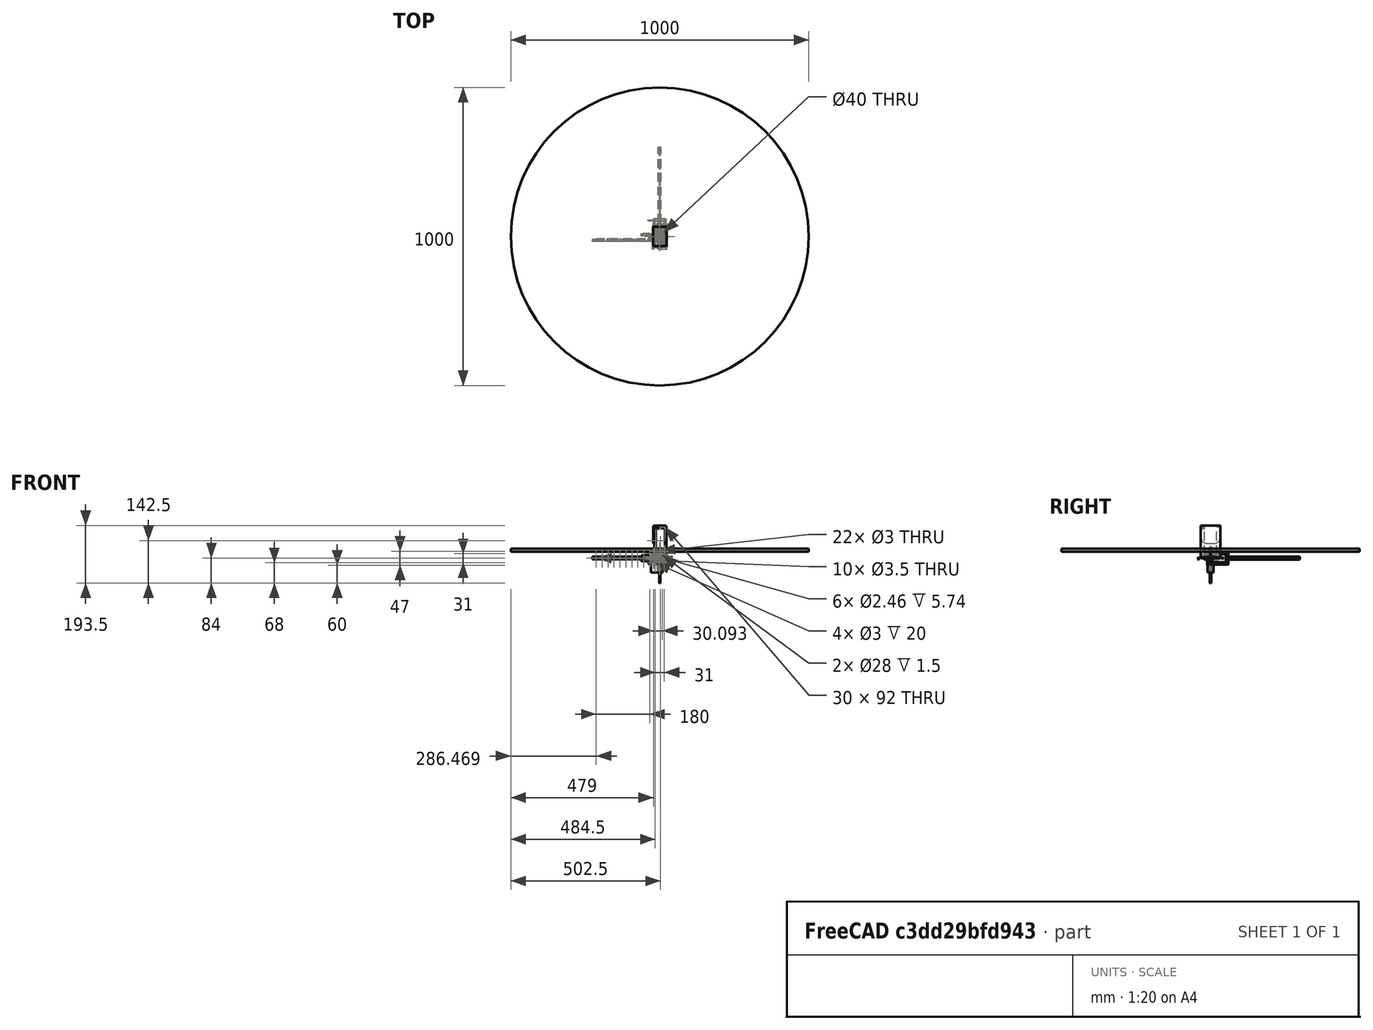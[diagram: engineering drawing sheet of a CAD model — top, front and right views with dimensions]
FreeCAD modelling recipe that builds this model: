
FCSTD DOCUMENT  (FreeCAD 2024.113R14555 (Git shallow))
Label: generic-hardware
License: All rights reserved
LicenseURL: http://en.wikipedia.org/wiki/All_rights_reserved
objects: Sketcher::SketchObject×123, PartDesign::Body×59, PartDesign::Pad×51, PartDesign::Pocket×41, PartDesign::Revolution×27, App::Part×24, PartDesign::Chamfer×22, App::Link×21, PartDesign::Fillet×21, PartDesign::PolarPattern×19, App::DocumentObjectGroup×13, Part::FeaturePython×13, Part::Feature×10, TechDraw::DrawViewDimension×9, PartDesign::FeatureBase×6, PartDesign::Groove×5, PartDesign::CoordinateSystem×4, TechDraw::DrawProjGroupItem×4, PartDesign::Line×3, Part::Mirroring×3, +13 more types
note: 943 computed .brp shape members not serialized (recipe doc carries the construction recipe); baked Part::Feature solids carry a one-line shape summary decoded from their .brp

FEATURE [Sketcher::SketchObject] Sketch
  ArcFitTolerance = 0
  ExternalBSplineMaxDegree = 0
  ExternalBSplineTolerance = 0
  FixShape = 1
  FullyConstrained = true
  InternalTolerance = 1e-06
  InvalidShape = false
  MakeInternals = false
  MapMode = 5
  Placement = pos=(0,0,0) rot=(1,0,0;1.5708rad)
  TreeRank = 0
  ValidateShape = false
  sketch-geometry (5):
    g0: LineSegment StartX=-21.15 StartY=-21.15 StartZ=0 EndX=21.15 EndY=-21.15 EndZ=0
    g1: LineSegment StartX=21.15 StartY=-21.15 StartZ=0 EndX=21.15 EndY=21.15 EndZ=0
    g2: LineSegment StartX=21.15 StartY=21.15 StartZ=0 EndX=-21.15 EndY=21.15 EndZ=0
    g3: LineSegment StartX=-21.15 StartY=21.15 StartZ=0 EndX=-21.15 EndY=-21.15 EndZ=0
    g4: GeomPoint [constr] X=0 Y=1e-16 Z=0
  constraints (12):
    c: Coincident(g0,g1)
    c: Coincident(g1,g2)
    c: Coincident(g2,g3)
    c: Coincident(g3,g0)
    c: Horizontal(g0)
    c: Horizontal(g2)
    c: Vertical(g1)
    c: Vertical(g3)
    c: Symmetric(g2,g0,g4)
    c: Coincident(g4,g-1)
    c: Equal(g2,g1)
    c: DistanceX(g2,g2) = 42.3
FEATURE [PartDesign::Pad] Pad
  AddSubType = 0
  AutoTaperInnerAngle = true
  CheckUpToFaceLimits = true
  ClaimChildren = false
  Direction = (0,-1,0)
  Fit = 0
  FitJoin = 0
  FixShape = 1
  InnerFit = 0
  InnerFitJoin = 0
  InvalidShape = false
  Length = 60
  Length2 = 10
  NewSolid = false
  Placement = pos=(0,0,0) rot=(1,0,0;1.5708rad)
  Profile = -> Sketch
  ReferenceAxis = -> Sketch [N_Axis]
  Refine = true
  Reversed = true
  Suppress = false
  TaperInnerAngle = 0
  TaperInnerAngleRev = 0
  TreeRank = 0
  Type = 0
  ValidateShape = true
  _ProfileBasedVersion = 0
FEATURE [Sketcher::SketchObject] Sketch001
  ArcFitTolerance = 0
  AttachmentSupport = -> [Pad]
  ExternalBSplineMaxDegree = 0
  ExternalBSplineTolerance = 0
  FixShape = 1
  FullyConstrained = true
  InternalTolerance = 1e-06
  InvalidShape = false
  MakeInternals = false
  MapMode = 5
  Placement = pos=(0,0,0) rot=(1,0,0;1.5708rad)
  Support = -> [Pad]
  TreeRank = 0
  ValidateShape = false
  sketch-geometry (1):
    g0: Circle CenterX=0 CenterY=0 CenterZ=0 NormalX=0 NormalY=0 NormalZ=1 AngleXU=0 Radius=11
  constraints (2):
    c: Coincident(g0,g-1)
    c: Diameter(g0) = 22
FEATURE [PartDesign::Pad] Pad001
  AddSubType = 0
  AutoTaperInnerAngle = true
  BaseFeature = -> Pad
  CheckUpToFaceLimits = true
  ClaimChildren = false
  Direction = (0,-1,-2e-16)
  Fit = 0
  FitJoin = 0
  FixShape = 1
  InnerFit = 0
  InnerFitJoin = 0
  InvalidShape = false
  Length = 2
  Length2 = 10
  NewSolid = false
  Placement = pos=(0,0,0) rot=(1,0,0;1.5708rad)
  Profile = -> Sketch001
  ReferenceAxis = -> Sketch001 [N_Axis]
  Refine = true
  Suppress = false
  TaperInnerAngle = 0
  TaperInnerAngleRev = 0
  TreeRank = 0
  Type = 0
  ValidateShape = true
  _ProfileBasedVersion = 0
FEATURE [Sketcher::SketchObject] Sketch002
  ArcFitTolerance = 0
  AttachmentSupport = -> [Pad001]
  ExternalBSplineMaxDegree = 0
  ExternalBSplineTolerance = 0
  FixShape = 1
  FullyConstrained = true
  InternalTolerance = 1e-06
  InvalidShape = false
  MakeInternals = false
  MapMode = 5
  Placement = pos=(0,0,0) rot=(1,0,0;1.5708rad)
  Support = -> [Pad001]
  TreeRank = 0
  ValidateShape = false
  sketch-geometry (1):
    g0: Circle CenterX=0 CenterY=0 CenterZ=0 NormalX=0 NormalY=0 NormalZ=1 AngleXU=0 Radius=2.5
  constraints (2):
    c: Coincident(g0,g-1)
    c: Diameter(g0) = 5
FEATURE [PartDesign::Pad] Pad002
  AddSubType = 0
  AutoTaperInnerAngle = true
  BaseFeature = -> Pad001
  CheckUpToFaceLimits = true
  ClaimChildren = false
  Direction = (0,-1,-7e-16)
  Fit = 0
  FitJoin = 0
  FixShape = 1
  InnerFit = 0
  InnerFitJoin = 0
  InvalidShape = false
  Length = 24
  Length2 = 10
  NewSolid = false
  Placement = pos=(0,0,0) rot=(1,0,0;1.5708rad)
  Profile = -> Sketch002
  ReferenceAxis = -> Sketch002 [N_Axis]
  Refine = true
  Suppress = false
  TaperInnerAngle = 0
  TaperInnerAngleRev = 0
  TreeRank = 0
  Type = 0
  ValidateShape = true
  _ProfileBasedVersion = 0
FEATURE [Sketcher::SketchObject] Sketch003
  ArcFitTolerance = 0
  ExternalBSplineMaxDegree = 0
  ExternalBSplineTolerance = 0
  ExternalGeometry = -> [Pad002]
  FixShape = 1
  FullyConstrained = true
  InternalTolerance = 1e-06
  InvalidShape = false
  MakeInternals = false
  MapMode = 5
  Placement = pos=(0,0,0) rot=(0.57735,0.57735,0.57735;2.0944rad)
  TreeRank = 0
  ValidateShape = false
  sketch-geometry (4):
    g0: LineSegment StartX=-24 StartY=2.5 StartZ=0 EndX=-24 EndY=2 EndZ=0
    g1: LineSegment StartX=-24 StartY=2 StartZ=0 EndX=-9 EndY=2 EndZ=0
    g2: LineSegment StartX=-9 StartY=2 StartZ=0 EndX=-9 EndY=2.5 EndZ=0
    g3: LineSegment StartX=-9 StartY=2.5 StartZ=0 EndX=-24 EndY=2.5 EndZ=0
  constraints (11):
    c: Coincident(g0,g1)
    c: Coincident(g1,g2)
    c: Coincident(g2,g3)
    c: Coincident(g3,g0)
    c: Vertical(g0)
    c: Vertical(g2)
    c: Horizontal(g1)
    c: Horizontal(g3)
    c: Coincident(g0,g-3)
    c: Distance(g0,g-3) = 4.5
    c: DistanceX(g1,g1) = 15
FEATURE [PartDesign::Pocket] Pocket
  AddSubType = 1
  AutoTaperInnerAngle = true
  BaseFeature = -> Pad002
  CheckUpToFaceLimits = true
  ClaimChildren = false
  Direction = (-1,-1e-16,1e-16)
  Fit = 0
  FitJoin = 0
  FixShape = 1
  InnerFit = 0
  InnerFitJoin = 0
  InvalidShape = false
  Length = 5
  Length2 = 5
  Midplane = true
  NewSolid = false
  Placement = pos=(0,0,0) rot=(1,0,0;1.5708rad)
  Profile = -> Sketch003
  ReferenceAxis = -> Sketch003 [N_Axis]
  Refine = true
  Suppress = false
  TaperInnerAngle = 0
  TaperInnerAngleRev = 0
  TreeRank = 0
  Type = 1
  ValidateShape = true
  _ProfileBasedVersion = 0
  _Version = 0
FEATURE [Sketcher::SketchObject] Sketch004
  ArcFitTolerance = 0
  ExternalBSplineMaxDegree = 0
  ExternalBSplineTolerance = 0
  FixShape = 1
  FullyConstrained = true
  InternalTolerance = 1e-06
  InvalidShape = false
  MakeInternals = false
  MapMode = 5
  Placement = pos=(0,0,0) rot=(1,0,0;1.5708rad)
  TreeRank = 0
  ValidateShape = false
  sketch-geometry (9):
    g0: LineSegment [constr] StartX=-15.5 StartY=-15.5 StartZ=0 EndX=15.5 EndY=-15.5 EndZ=0
    g1: LineSegment [constr] StartX=15.5 StartY=-15.5 StartZ=0 EndX=15.5 EndY=15.5 EndZ=0
    g2: LineSegment [constr] StartX=15.5 StartY=15.5 StartZ=0 EndX=-15.5 EndY=15.5 EndZ=0
    g3: LineSegment [constr] StartX=-15.5 StartY=15.5 StartZ=0 EndX=-15.5 EndY=-15.5 EndZ=0
    g4: GeomPoint [constr] X=0 Y=0 Z=0
    g5: Circle CenterX=-15.5 CenterY=15.5 CenterZ=0 NormalX=0 NormalY=0 NormalZ=1 AngleXU=0 Radius=1.5
    g6: Circle CenterX=15.5 CenterY=15.5 CenterZ=0 NormalX=0 NormalY=0 NormalZ=1 AngleXU=0 Radius=1.5
    g7: Circle CenterX=15.5 CenterY=-15.5 CenterZ=0 NormalX=0 NormalY=0 NormalZ=1 AngleXU=0 Radius=1.5
    g8: Circle CenterX=-15.5 CenterY=-15.5 CenterZ=0 NormalX=0 NormalY=0 NormalZ=1 AngleXU=0 Radius=1.5
  constraints (20):
    c: Coincident(g0,g1)
    c: Coincident(g1,g2)
    c: Coincident(g2,g3)
    c: Coincident(g3,g0)
    c: Horizontal(g0)
    c: Horizontal(g2)
    c: Vertical(g1)
    c: Vertical(g3)
    c: Symmetric(g2,g0,g4)
    c: Coincident(g4,g-1)
    c: Equal(g1,g2)
    c: DistanceX(g2,g2) = 31
    c: Coincident(g5,g2)
    c: Coincident(g6,g1)
    c: Coincident(g7,g0)
    c: Coincident(g8,g0)
    c: Equal(g8,g5)
    c: Equal(g5,g6)
    c: Equal(g6,g7)
    c: Diameter(g6) = 3
FEATURE [PartDesign::Pocket] Pocket001
  AddSubType = 1
  AutoTaperInnerAngle = true
  BaseFeature = -> Pocket
  CheckUpToFaceLimits = true
  ClaimChildren = false
  Direction = (0,1,0)
  Fit = 0
  FitJoin = 0
  FixShape = 1
  InnerFit = 0
  InnerFitJoin = 0
  InvalidShape = false
  Length = 20
  Length2 = 5
  NewSolid = false
  Placement = pos=(0,0,0) rot=(1,0,0;1.5708rad)
  Profile = -> Sketch004
  ReferenceAxis = -> Sketch004 [N_Axis]
  Refine = true
  Suppress = false
  TaperInnerAngle = 0
  TaperInnerAngleRev = 0
  TreeRank = 0
  Type = 0
  ValidateShape = true
  _ProfileBasedVersion = 0
  _Version = 0
FEATURE [PartDesign::Chamfer] Chamfer
  AddSubType = 0
  Angle = 45
  Base = -> Pocket001 [Edge35]
  BaseFeature = -> Pocket001
  ChamferType = 0
  FixShape = 1
  FlipDirection = false
  InvalidShape = false
  NewSolid = false
  Placement = pos=(0,0,0) rot=(1,0,0;1.5708rad)
  Refine = true
  Size = 0.2
  Size2 = 1
  SupportTransform = false
  Suppress = false
  TreeRank = 0
  UseAllEdges = false
  ValidateShape = true
FEATURE [PartDesign::Chamfer] Chamfer001
  AddSubType = 0
  Angle = 45
  Base = -> Chamfer [Edge32,Edge28,Edge30,Edge27]
  BaseFeature = -> Chamfer
  ChamferType = 0
  FixShape = 1
  FlipDirection = false
  InvalidShape = false
  NewSolid = false
  Placement = pos=(0,0,0) rot=(1,0,0;1.5708rad)
  Refine = true
  Size = 5
  Size2 = 1
  SupportTransform = false
  Suppress = false
  TreeRank = 0
  UseAllEdges = false
  ValidateShape = true
FEATURE [PartDesign::Body] Body  label="Simple-17HS24-2104S"
  AutoGroupSolids = false
  ClaimAllChildren = false
  ExportMode = 0
  FixShape = 1
  Group = -> [Sketch,Pad,Sketch001,Pad001,Sketch002,Pad002,Sketch003,Pocket,Sketch004,Pocket001,Chamfer,Chamfer001]
  InvalidShape = false
  Origin = -> Origin
  SingleSolid = true
  Tip = -> Chamfer001
  TreeRank = 0
  ValidateShape = false
  _ExportChildren = -> [Pad,Pad001,Pad002,Pocket,Pocket001,Chamfer,Chamfer001]
  _GroupVersion = 1
FEATURE [PartDesign::Line] DatumLine001
  AttacherType = Attacher::AttachEngineLine
  AttachmentOffset = pos=(0,23.5,0) rot=(0,0,1;0rad)
  FixShape = 1
  InvalidShape = false
  Length = 80
  MapMode = 16
  MinimumLength = 10
  Placement = pos=(0,0,23.5) rot=(0.57735,0.57735,0.57735;2.0944rad)
  ResizeMode = 1
  TreeRank = 0
  ValidateShape = false
FEATURE [PartDesign::Line] DatumLine002
  AttacherType = Attacher::AttachEngineLine
  FixShape = 1
  InvalidShape = false
  Length = 10
  MapMode = 29
  MinimumLength = 10
  Placement = pos=(0,0,-24) rot=(0,0.707107,0.707107;3.14159rad)
  ResizeMode = 0
  TreeRank = 0
  ValidateShape = false
FEATURE [App::Link] Link084  label="Roller001"
  AutoLinkLabel = false
  AutoPlacement = true
  LinkPlacement = pos=(0,0,0) rot=(0,-1,0;1.25664rad)
  LinkedObject = -> Body050
  Placement = pos=(0,0,0) rot=(0,-1,0;1.25664rad)
  SyncGroupVisibility = false
  TreeRank = 0
  _LinkVersion = 1
FEATURE [App::Link] Link085  label="Roller002"
  AutoLinkLabel = false
  AutoPlacement = true
  LinkPlacement = pos=(0,0,0) rot=(0,1,0;3.76991rad)
  LinkedObject = -> Link084
  Placement = pos=(0,0,0) rot=(0,1,0;3.76991rad)
  SyncGroupVisibility = false
  TreeRank = 0
  _LinkVersion = 1
FEATURE [App::Link] Link086  label="Roller003"
  AutoLinkLabel = false
  AutoPlacement = true
  LinkPlacement = pos=(0,0,0) rot=(0,1,0;2.51327rad)
  LinkedObject = -> Link085
  Placement = pos=(0,0,0) rot=(0,1,0;2.51327rad)
  SyncGroupVisibility = false
  TreeRank = 0
  _LinkVersion = 1
FEATURE [App::Link] Link087  label="Roller004"
  AutoLinkLabel = false
  AutoPlacement = true
  LinkPlacement = pos=(0,0,0) rot=(0,1,0;1.25664rad)
  LinkedObject = -> Link086
  Placement = pos=(0,0,0) rot=(0,1,0;1.25664rad)
  SyncGroupVisibility = false
  TreeRank = 0
  _LinkVersion = 1
FEATURE [App::Link] Link088  label="Rivet001"
  AutoLinkLabel = false
  AutoPlacement = true
  LinkPlacement = pos=(0,0,0) rot=(0,-1,0;1.25664rad)
  LinkedObject = -> Body051
  Placement = pos=(0,0,0) rot=(0,-1,0;1.25664rad)
  SyncGroupVisibility = false
  TreeRank = 0
  _LinkVersion = 1
FEATURE [App::Link] Link089  label="Rivet002"
  AutoLinkLabel = false
  AutoPlacement = true
  LinkPlacement = pos=(0,0,0) rot=(0,1,0;3.76991rad)
  LinkedObject = -> Link088
  Placement = pos=(0,0,0) rot=(0,1,0;3.76991rad)
  SyncGroupVisibility = false
  TreeRank = 0
  _LinkVersion = 1
FEATURE [App::Link] Link090  label="Rivet003"
  AutoLinkLabel = false
  AutoPlacement = true
  LinkPlacement = pos=(0,0,0) rot=(0,1,0;2.51327rad)
  LinkedObject = -> Link089
  Placement = pos=(0,0,0) rot=(0,1,0;2.51327rad)
  SyncGroupVisibility = false
  TreeRank = 0
  _LinkVersion = 1
FEATURE [App::Link] Link091  label="Rivet004"
  AutoLinkLabel = false
  AutoPlacement = true
  LinkPlacement = pos=(0,0,0) rot=(0,1,0;1.25664rad)
  LinkedObject = -> Link090
  Placement = pos=(0,0,0) rot=(0,1,0;1.25664rad)
  SyncGroupVisibility = false
  TreeRank = 0
  _LinkVersion = 1
FEATURE [Sketcher::SketchObject] Sketch095
  ArcFitTolerance = 0
  ExternalBSplineMaxDegree = 0
  ExternalBSplineTolerance = 0
  FixShape = 1
  FullyConstrained = true
  InternalTolerance = 1e-06
  InvalidShape = false
  MakeInternals = false
  MapMode = 5
  Placement = pos=(0,0,0) rot=(1,0,0;1.5708rad)
  TreeRank = 0
  ValidateShape = false
  sketch-geometry (2):
    g0: Circle CenterX=0 CenterY=0 CenterZ=0 NormalX=0 NormalY=0 NormalZ=1 AngleXU=0 Radius=14
    g1: Circle CenterX=0 CenterY=0 CenterZ=0 NormalX=0 NormalY=0 NormalZ=1 AngleXU=0 Radius=28.5
  constraints (4):
    c: Coincident(g0,g-1)
    c: Diameter(g0) = 28
    c: Coincident(g1,g0)
    c: Diameter(g1) = 57
FEATURE [PartDesign::Pad] Pad057
  AddSubType = 0
  AutoTaperInnerAngle = true
  CheckUpToFaceLimits = true
  ClaimChildren = false
  Direction = (0,-1,0)
  Fit = 0
  FitJoin = 0
  FixShape = 1
  InnerFit = 0
  InnerFitJoin = 0
  InvalidShape = false
  Length = 5.5
  Length2 = 100
  Midplane = true
  NewSolid = false
  Placement = pos=(0,0,0) rot=(1,0,0;1.5708rad)
  Profile = -> Sketch095
  Refine = true
  Suppress = false
  TaperInnerAngle = 0
  TaperInnerAngleRev = 0
  TreeRank = 0
  Type = 0
  ValidateShape = true
  _ProfileBasedVersion = 0
FEATURE [Sketcher::SketchObject] Sketch096
  ArcFitTolerance = 0
  AttachmentSupport = -> [XZ_Plane057]
  ExternalBSplineMaxDegree = 0
  ExternalBSplineTolerance = 0
  FixShape = 1
  FullyConstrained = true
  InternalTolerance = 1e-06
  InvalidShape = false
  MakeInternals = false
  MapMode = 5
  Placement = pos=(0,0,0) rot=(1,0,0;1.5708rad)
  TreeRank = 0
  ValidateShape = false
  sketch-geometry (2):
    g0: Circle CenterX=0 CenterY=0 CenterZ=0 NormalX=0 NormalY=0 NormalZ=1 AngleXU=0 Radius=6
    g1: Circle CenterX=0 CenterY=0 CenterZ=0 NormalX=0 NormalY=0 NormalZ=1 AngleXU=0 Radius=14
  constraints (4):
    c: Coincident(g0,g-1)
    c: Diameter(g0) = 12
    c: Coincident(g1,g0)
    c: Diameter(g1) = 28
FEATURE [PartDesign::Pad] Pad058
  AddSubType = 0
  AutoTaperInnerAngle = true
  BaseFeature = -> Pad057
  CheckUpToFaceLimits = true
  ClaimChildren = false
  Direction = (0,-1,-2e-16)
  Fit = 0
  FitJoin = 0
  FixShape = 1
  InnerFit = 0
  InnerFitJoin = 0
  InvalidShape = false
  Length = 2.5
  Length2 = 100
  Midplane = true
  NewSolid = false
  Placement = pos=(0,0,0) rot=(1,0,0;1.5708rad)
  Profile = -> Sketch096
  Refine = true
  Suppress = false
  TaperInnerAngle = 0
  TaperInnerAngleRev = 0
  TreeRank = 0
  Type = 0
  ValidateShape = true
  _ProfileBasedVersion = 0
FEATURE [Sketcher::SketchObject] Sketch097
  ArcFitTolerance = 0
  ExternalBSplineMaxDegree = 0
  ExternalBSplineTolerance = 0
  FixShape = 1
  FullyConstrained = false
  InternalTolerance = 1e-06
  InvalidShape = false
  MakeInternals = false
  MapMode = 5
  Placement = pos=(0,0,0) rot=(1,0,0;1.5708rad)
  TreeRank = 0
  ValidateShape = false
  sketch-geometry (6):
    g0: LineSegment StartX=-9.7 StartY=26.7985 StartZ=0 EndX=-9.7 EndY=17.7985 EndZ=0
    g1: LineSegment StartX=9.7 StartY=26.7985 StartZ=0 EndX=9.7 EndY=17.7985 EndZ=0
    g2: ArcOfCircle CenterX=-1.9e-15 CenterY=37.1169 CenterZ=0 NormalX=0 NormalY=0 NormalZ=1 AngleXU=0 Radius=21.6169 StartAngle=4.24705 EndAngle=5.17773
    g3: GeomPoint [constr] X=0 Y=15.5 Z=0
    g4: ArcOfCircle CenterX=0 CenterY=0 CenterZ=0 NormalX=0 NormalY=0 NormalZ=1 AngleXU=0 Radius=28.5 StartAngle=1.22351 EndAngle=1.91809
    g5: Circle [constr] CenterX=0 CenterY=0 CenterZ=0 NormalX=0 NormalY=0 NormalZ=1 AngleXU=0 Radius=28.5
  constraints (16):
    c: Vertical(g0)
    c: Vertical(g1)
    c: Symmetric(g1,g0,g-2)
    c: Equal(g0,g1)
    c: Coincident(g2,g0)
    c: Coincident(g2,g1)
    c: PointOnObject(g3,g2)
    c: PointOnObject(g3,g-2)
    c: DistanceY(g-1,g3) = 15.5
    c: DistanceY(g1,g1) = 9
    c: Coincident(g4,g-1)
    c: Coincident(g4,g0)
    c: DistanceX(g0,g1) = 19.4
    c: Coincident(g5,g4)
    c: PointOnObject(g1,g5)
    c: Diameter(g5) = 57
FEATURE [PartDesign::Pocket] Pocket036
  AddSubType = 1
  AutoTaperInnerAngle = true
  BaseFeature = -> Pad058
  CheckUpToFaceLimits = true
  ClaimChildren = false
  Direction = (0,1,0)
  Fit = 0
  FitJoin = 0
  FixShape = 1
  InnerFit = 0
  InnerFitJoin = 0
  InvalidShape = false
  Length = 5
  Length2 = 100
  Midplane = true
  NewSolid = false
  Placement = pos=(0,0,0) rot=(1,0,0;1.5708rad)
  Profile = -> Sketch097
  Refine = true
  Suppress = false
  TaperInnerAngle = 0
  TaperInnerAngleRev = 0
  TreeRank = 0
  Type = 1
  ValidateShape = true
  _ProfileBasedVersion = 0
  _Version = 0
FEATURE [PartDesign::PolarPattern] PolarPattern017
  AddSubType = 0
  Angle = 360
  Axis = -> Sketch097 [N_Axis]
  BaseFeature = -> Pocket036
  CopyShape = true
  FixShape = 1
  InvalidShape = false
  NewSolid = false
  Occurrences = 5
  OriginalSubs = -> [Pocket036]
  Originals = -> [Pocket036]
  ParallelTransform = true
  Placement = pos=(0,0,0) rot=(1,0,0;1.5708rad)
  Refine = true
  SubTransform = true
  Suppress = false
  TreeRank = 0
  ValidateShape = true
  _Version = 0
FEATURE [Sketcher::SketchObject] Sketch098
  ArcFitTolerance = 0
  ExternalBSplineMaxDegree = 0
  ExternalBSplineTolerance = 0
  FixShape = 1
  FullyConstrained = true
  InternalTolerance = 1e-06
  InvalidShape = false
  MakeInternals = false
  MapMode = 5
  Placement = pos=(0,0,0) rot=(0.57735,0.57735,0.57735;2.0944rad)
  TreeRank = 0
  ValidateShape = false
  sketch-geometry (3):
    g0: Circle CenterX=0 CenterY=23.5 CenterZ=0 NormalX=0 NormalY=0 NormalZ=1 AngleXU=0 Radius=1
    g1: Circle [constr] CenterX=0 CenterY=23.5 CenterZ=0 NormalX=0 NormalY=0 NormalZ=1 AngleXU=0 Radius=6.5
    g2: GeomPoint [constr] X=0 Y=30 Z=0
  constraints (7):
    c: PointOnObject(g0,g-2)
    c: Diameter(g0) = 2
    c: Coincident(g1,g0)
    c: Diameter(g1) = 13
    c: PointOnObject(g2,g1)
    c: PointOnObject(g2,g-2)
    c: DistanceY(g2) = 30
FEATURE [PartDesign::Pad] Pad059
  AddSubType = 0
  AutoTaperInnerAngle = true
  BaseFeature = -> PolarPattern017
  CheckUpToFaceLimits = true
  ClaimChildren = false
  Direction = (1,1e-16,-1e-16)
  Fit = 0
  FitJoin = 0
  FixShape = 1
  InnerFit = 0
  InnerFitJoin = 0
  InvalidShape = false
  Length = 20
  Length2 = 100
  Midplane = true
  NewSolid = false
  Placement = pos=(0,0,0) rot=(1,0,0;1.5708rad)
  Profile = -> Sketch098
  Refine = true
  Suppress = false
  TaperInnerAngle = 0
  TaperInnerAngleRev = 0
  TreeRank = 0
  Type = 0
  ValidateShape = true
  _ProfileBasedVersion = 0
FEATURE [PartDesign::PolarPattern] PolarPattern018
  AddSubType = 0
  Angle = 360
  Axis = -> Y_Axis057
  BaseFeature = -> Pad059
  CopyShape = true
  FixShape = 1
  InvalidShape = false
  NewSolid = false
  Occurrences = 5
  OriginalSubs = -> [Pad059]
  Originals = -> [Pad059]
  ParallelTransform = true
  Placement = pos=(0,0,0) rot=(1,0,0;1.5708rad)
  Refine = true
  SubTransform = true
  Suppress = false
  TreeRank = 0
  ValidateShape = true
  _Version = 0
FEATURE [Sketcher::SketchObject] Sketch099
  ArcFitTolerance = 0
  ExternalBSplineMaxDegree = 0
  ExternalBSplineTolerance = 0
  FixShape = 1
  FullyConstrained = true
  InternalTolerance = 1e-06
  InvalidShape = false
  MakeInternals = false
  MapMode = 5
  Placement = pos=(0,0,0) rot=(1,0,0;1.5708rad)
  TreeRank = 0
  ValidateShape = false
  sketch-geometry (1):
    g0: Circle CenterX=0 CenterY=10.5 CenterZ=0 NormalX=0 NormalY=0 NormalZ=1 AngleXU=0 Radius=1.5
  constraints (3):
    c: PointOnObject(g0,g-2)
    c: Diameter(g0) = 3
    c: DistanceY(g0) = 10.5
FEATURE [PartDesign::Pocket] Pocket037
  AddSubType = 1
  AutoTaperInnerAngle = true
  BaseFeature = -> PolarPattern018
  CheckUpToFaceLimits = true
  ClaimChildren = false
  Direction = (0,1,0)
  Fit = 0
  FitJoin = 0
  FixShape = 1
  InnerFit = 0
  InnerFitJoin = 0
  InvalidShape = false
  Length = 5
  Length2 = 100
  Midplane = true
  NewSolid = false
  Placement = pos=(0,0,0) rot=(1,0,0;1.5708rad)
  Profile = -> Sketch099
  Refine = true
  Suppress = false
  TaperInnerAngle = 0
  TaperInnerAngleRev = 0
  TreeRank = 0
  Type = 1
  ValidateShape = true
  _ProfileBasedVersion = 0
  _Version = 0
FEATURE [PartDesign::PolarPattern] PolarPattern019
  AddSubType = 0
  Angle = 360
  Axis = -> Y_Axis057
  BaseFeature = -> Pocket037
  CopyShape = true
  FixShape = 1
  InvalidShape = false
  NewSolid = false
  Occurrences = 6
  OriginalSubs = -> [Pocket037]
  Originals = -> [Pocket037]
  ParallelTransform = true
  Placement = pos=(0,0,0) rot=(1,0,0;1.5708rad)
  Refine = true
  SubTransform = true
  Suppress = false
  TreeRank = 0
  ValidateShape = true
  _Version = 0
FEATURE [Sketcher::SketchObject] Sketch100
  ArcFitTolerance = 0
  ExternalBSplineMaxDegree = 0
  ExternalBSplineTolerance = 0
  FixShape = 1
  FullyConstrained = true
  InternalTolerance = 1e-06
  InvalidShape = false
  MakeInternals = false
  MapMode = 5
  Placement = pos=(0,0,0) rot=(1,0,0;1.5708rad)
  TreeRank = 0
  ValidateShape = false
  sketch-geometry (1):
    g0: Circle CenterX=0 CenterY=-24 CenterZ=0 NormalX=0 NormalY=0 NormalZ=1 AngleXU=0 Radius=1.6
  constraints (3):
    c: PointOnObject(g0,g-2)
    c: Diameter(g0) = 3.2
    c: DistanceY(g0) = -24
FEATURE [PartDesign::Pocket] Pocket038
  AddSubType = 1
  AutoTaperInnerAngle = true
  BaseFeature = -> PolarPattern019
  CheckUpToFaceLimits = true
  ClaimChildren = false
  Direction = (0,1,0)
  Fit = 0
  FitJoin = 0
  FixShape = 1
  InnerFit = 0
  InnerFitJoin = 0
  InvalidShape = false
  Length = 5
  Length2 = 100
  Midplane = true
  NewSolid = false
  Placement = pos=(0,0,0) rot=(1,0,0;1.5708rad)
  Profile = -> Sketch100
  Refine = true
  Suppress = false
  TaperInnerAngle = 0
  TaperInnerAngleRev = 0
  TreeRank = 0
  Type = 1
  ValidateShape = true
  _ProfileBasedVersion = 0
  _Version = 0
FEATURE [PartDesign::PolarPattern] PolarPattern020
  AddSubType = 0
  Angle = 360
  Axis = -> Sketch100 [N_Axis]
  BaseFeature = -> Pocket038
  CopyShape = true
  FixShape = 1
  InvalidShape = false
  NewSolid = false
  Occurrences = 5
  OriginalSubs = -> [Pocket038]
  Originals = -> [Pocket038]
  ParallelTransform = true
  Placement = pos=(0,0,0) rot=(1,0,0;1.5708rad)
  Refine = true
  SubTransform = true
  Suppress = false
  TreeRank = 0
  ValidateShape = true
  _Version = 0
FEATURE [PartDesign::Body] Body047  label="MainPlate"
  AutoGroupSolids = false
  ClaimAllChildren = false
  ExportMode = 0
  FixShape = 1
  Group = -> [Sketch095,Pad057,Sketch096,Pad058,Sketch097,Pocket036,Sketch098,PolarPattern017,Pad059,PolarPattern018,Sketch099,Pocket037,PolarPattern019,Sketch100,Pocket038,PolarPattern020]
  InvalidShape = false
  Origin = -> Origin071
  SingleSolid = true
  Tip = -> PolarPattern020
  TreeRank = 0
  ValidateShape = false
  _ExportChildren = -> [Pad057,Pad058,Pocket036,PolarPattern017,Pad059,PolarPattern018,Pocket037,PolarPattern019,Pocket038,PolarPattern020]
  _GroupVersion = 1
FEATURE [Sketcher::SketchObject] Sketch114
  ArcFitTolerance = 0
  ExternalBSplineMaxDegree = 0
  ExternalBSplineTolerance = 0
  FixShape = 1
  FullyConstrained = true
  InternalTolerance = 1e-06
  InvalidShape = false
  MakeInternals = false
  MapMode = 5
  Placement = pos=(0,0,0) rot=(1,0,0;1.5708rad)
  TreeRank = 0
  ValidateShape = false
  sketch-geometry (8):
    g0: ArcOfCircle CenterX=1.7e-15 CenterY=0.729167 CenterZ=0 NormalX=0 NormalY=0 NormalZ=1 AngleXU=0 Radius=29.2708 StartAngle=1.24927 EndAngle=1.89232
    g1: LineSegment [constr] StartX=-9.25 StartY=28.5 StartZ=0 EndX=-9.25 EndY=23.5 EndZ=0
    g2: LineSegment [constr] StartX=-9.25 StartY=23.5 StartZ=0 EndX=9.25 EndY=23.5 EndZ=0
    g3: LineSegment [constr] StartX=9.25 StartY=23.5 StartZ=0 EndX=9.25 EndY=28.5 EndZ=0
    g4: GeomPoint [constr] X=0 Y=30 Z=0
    g5: LineSegment StartX=-9.25 StartY=28.5 StartZ=0 EndX=-9.25 EndY=24.5 EndZ=0
    g6: LineSegment StartX=-9.25 StartY=24.5 StartZ=0 EndX=9.25 EndY=24.5 EndZ=0
    g7: LineSegment StartX=9.25 StartY=24.5 StartZ=0 EndX=9.25 EndY=28.5 EndZ=0
  constraints (22):
    c: Coincident(g1,g0)
    c: Vertical(g1)
    c: Coincident(g2,g1)
    c: Horizontal(g2)
    c: Coincident(g3,g2)
    c: Coincident(g3,g0)
    c: Vertical(g3)
    c: Symmetric(g0,g0,g-2)
    c: PointOnObject(g4,g0)
    c: PointOnObject(g4,g-2)
    c: DistanceY(g4) = 30
    c: DistanceX(g0,g0) = 18.5
    c: DistanceY(g2,g4) = 6.5
    c: DistanceY(g3,g3) = 5
    c: Coincident(g5,g0)
    c: PointOnObject(g5,g1)
    c: Coincident(g6,g5)
    c: PointOnObject(g6,g3)
    c: Horizontal(g6)
    c: Coincident(g7,g6)
    c: Coincident(g7,g0)
    c: DistanceY(g2,g6) = 1
FEATURE [PartDesign::Revolution] Revolution003
  AddSubType = 0
  Angle = 360
  Axis = (1,1e-16,-1e-16)
  Base = (0,0,23.5)
  ClaimChildren = false
  Fit = 0
  FitJoin = 0
  FixShape = 1
  InnerFit = 0
  InnerFitJoin = 0
  InvalidShape = false
  NewSolid = false
  Placement = pos=(0,0,0) rot=(1,0,0;1.5708rad)
  Profile = -> Sketch114
  ReferenceAxis = -> DatumLine001
  Refine = true
  Suppress = false
  TreeRank = 0
  ValidateShape = true
  _ProfileBasedVersion = 0
FEATURE [PartDesign::Fillet] Fillet029
  AddSubType = 0
  Base = -> Revolution003 [Edge3,Edge1]
  BaseFeature = -> Revolution003
  FixShape = 1
  InvalidShape = false
  NewSolid = false
  Placement = pos=(0,0,0) rot=(1,0,0;1.5708rad)
  Radius = 0.2
  Refine = true
  SupportTransform = false
  Suppress = false
  TreeRank = 0
  UseAllEdges = false
  ValidateShape = true
FEATURE [PartDesign::Body] Body050  label="Roller"
  AutoGroupSolids = false
  ClaimAllChildren = false
  ExportMode = 0
  FixShape = 1
  Group = -> [Sketch114,DatumLine001,Revolution003,Fillet029]
  InvalidShape = false
  Origin = -> Origin077
  SingleSolid = true
  Tip = -> Fillet029
  TreeRank = 0
  ValidateShape = false
  _ExportChildren = -> [DatumLine001,Revolution003,Fillet029]
  _GroupVersion = 1
FEATURE [App::Part] Part020  label="Rollers"
  ClaimAllChildren = false
  ExportMode = 1
  Group = -> [Body050,Link084,Link085,Link086,Link087]
  Origin = -> Origin072
  TreeRank = 0
  _ExportChildren = -> [Body050,Link084,Link085,Link086,Link087]
  _GroupVersion = 1
FEATURE [Sketcher::SketchObject] Sketch115
  ArcFitTolerance = 0
  ExternalBSplineMaxDegree = 0
  ExternalBSplineTolerance = 0
  FixShape = 1
  FullyConstrained = true
  InternalTolerance = 1e-06
  InvalidShape = false
  MakeInternals = false
  MapMode = 5
  Placement = pos=(0,0,0) rot=(0.57735,0.57735,0.57735;2.0944rad)
  TreeRank = 0
  ValidateShape = false
  sketch-geometry (10):
    g0: LineSegment [constr] StartX=-3.75 StartY=-24 StartZ=0 EndX=3.75 EndY=-24 EndZ=0
    g1: LineSegment [constr] StartX=3.75 StartY=-24 StartZ=0 EndX=3.75 EndY=-22.5 EndZ=0
    g2: ArcOfCircle CenterX=-1.97 CenterY=-24 CenterZ=0 NormalX=0 NormalY=0 NormalZ=1 AngleXU=0 Radius=1.78 StartAngle=2.02439 EndAngle=3.14159
    g3: LineSegment StartX=-2.75 StartY=-22.4 StartZ=0 EndX=2.75 EndY=-22.4 EndZ=0
    g4: ArcOfCircle CenterX=-0.125 CenterY=-24 CenterZ=0 NormalX=0 NormalY=0 NormalZ=1 AngleXU=0 Radius=4.15519 StartAngle=0.369334 EndAngle=0.806672
    g5: LineSegment StartX=2.75 StartY=-22.4 StartZ=0 EndX=2.75 EndY=-21 EndZ=0
    g6: LineSegment StartX=-3.75 StartY=-24 StartZ=0 EndX=2.75 EndY=-24 EndZ=0
    g7: LineSegment StartX=2.75 StartY=-24 StartZ=0 EndX=2.75 EndY=-23.2 EndZ=0
    g8: LineSegment StartX=2.75 StartY=-23.2 StartZ=0 EndX=3.75 EndY=-23.2 EndZ=0
    g9: LineSegment StartX=3.75 StartY=-23.2 StartZ=0 EndX=3.75 EndY=-22.5 EndZ=0
  constraints (31):
    c: Horizontal(g0)
    c: Coincident(g1,g0)
    c: Vertical(g1)
    c: PointOnObject(g2,g0)
    c: Coincident(g2,g0)
    c: Coincident(g3,g2)
    c: Horizontal(g3)
    c: PointOnObject(g4,g0)
    c: Coincident(g4,g1)
    c: Coincident(g5,g3)
    c: Coincident(g5,g4)
    c: Vertical(g5)
    c: DistanceY(g0) = -24
    c: DistanceX(g2) = -2.75
    c: DistanceX(g3) = 2.75
    c: DistanceY(g0,g4) = 3
    c: DistanceY(g1,g1) = 1.5
    c: DistanceX(g3,g1) = 1
    c: DistanceY(g0,g3) = 1.6
    c: DistanceX(g0,g2) = 1
    c: Coincident(g6,g2)
    c: PointOnObject(g6,g0)
    c: Coincident(g7,g6)
    c: Vertical(g7)
    c: Coincident(g8,g7)
    c: PointOnObject(g8,g1)
    c: Horizontal(g8)
    c: Coincident(g9,g8)
    c: Coincident(g9,g4)
    c: DistanceY(g7,g7) = 0.8
    c: DistanceX(g8,g8) = 1
FEATURE [PartDesign::Revolution] Revolution004
  AddSubType = 0
  Angle = 360
  Axis = (1e-16,1,-2e-16)
  Base = (0,0,-24)
  ClaimChildren = false
  Fit = 0
  FitJoin = 0
  FixShape = 1
  InnerFit = 0
  InnerFitJoin = 0
  InvalidShape = false
  NewSolid = false
  Placement = pos=(0,0,0) rot=(0.57735,0.57735,0.57735;2.0944rad)
  Profile = -> Sketch115
  ReferenceAxis = -> DatumLine002
  Refine = true
  Reversed = true
  Suppress = false
  TreeRank = 0
  ValidateShape = true
  _ProfileBasedVersion = 0
FEATURE [PartDesign::Body] Body051  label="Rivet"
  AutoGroupSolids = false
  ClaimAllChildren = false
  ExportMode = 0
  FixShape = 1
  Group = -> [Sketch115,DatumLine002,Revolution004]
  InvalidShape = false
  Origin = -> Origin078
  SingleSolid = true
  Tip = -> Revolution004
  TreeRank = 0
  ValidateShape = false
  _ExportChildren = -> [DatumLine002,Revolution004]
  _GroupVersion = 1
FEATURE [App::Part] Part021  label="Rivets"
  ClaimAllChildren = false
  ExportMode = 1
  Group = -> [Body051,Link088,Link089,Link090,Link091]
  Origin = -> Origin073
  TreeRank = 0
  _ExportChildren = -> [Body051,Link088,Link089,Link090,Link091]
  _GroupVersion = 1
FEATURE [App::Part] Part018  label="OmniPancake"
  ClaimAllChildren = false
  ExportMode = 1
  Group = -> [Body047,Part020,Part021]
  Origin = -> Origin067
  TreeRank = 0
  _ExportChildren = -> [Body047,Part020,Part021]
  _GroupVersion = 1
FEATURE [App::Link] Link  label="OmniPancake001"
  AutoLinkLabel = false
  AutoPlacement = true
  LinkedObject = -> Part018
  SyncGroupVisibility = false
  TreeRank = 0
  _LinkVersion = 1
FEATURE [App::Link] Link092  label="OmniPancake002"
  AutoLinkLabel = false
  AutoPlacement = true
  LinkPlacement = pos=(1.8e-15,11.5,-1.6e-15) rot=(0,1,0;3.14159rad)
  LinkedObject = -> Part018
  Placement = pos=(1.8e-15,11.5,-1.6e-15) rot=(0,1,0;3.14159rad)
  SyncGroupVisibility = false
  TreeRank = 0
  _LinkVersion = 1
FEATURE [Part::Feature] Part__Feature  label="OMC-Stepper-17HS24-2104S"
  FixShape = 1
  InvalidShape = false
  Placement = pos=(0,60,1.3e-14) rot=(0.57735,0.57735,-0.57735;2.0944rad)
  TreeRank = 0
  ValidateShape = false
  shape: bbox 71.15 x 84 x 42.32 mm, 279 faces (baked)
FEATURE [App::Part] Part022  label="17HS24-2104S"
  ClaimAllChildren = false
  ExportMode = 1
  Group = -> [Body,Part__Feature]
  Origin = -> Origin080
  TreeRank = 0
  _ExportChildren = -> [Body,Part__Feature]
  _GroupVersion = 1
FEATURE [App::DocumentObjectGroup] Group  label="Motors"
  ClaimAllChildren = true
  ExportMode = 1
  Group = -> [Part022]
  TreeRank = 0
  _GroupVersion = 1
FEATURE [Sketcher::SketchObject] Sketch116
  ArcFitTolerance = 0
  ExternalBSplineMaxDegree = 0
  ExternalBSplineTolerance = 0
  FixShape = 1
  FullyConstrained = true
  InternalTolerance = 1e-06
  InvalidShape = false
  MakeInternals = false
  MapMode = 5
  TreeRank = 0
  ValidateShape = false
  sketch-geometry (10):
    g0: LineSegment StartX=-6.8 StartY=0 StartZ=0 EndX=-6.8 EndY=0.8 EndZ=0
    g1: LineSegment StartX=-6.8 StartY=0.8 StartZ=0 EndX=-5.4 EndY=0.8 EndZ=0
    g2: LineSegment StartX=-5.4 StartY=0.8 StartZ=0 EndX=-5.4 EndY=-2.7 EndZ=0
    g3: LineSegment StartX=-5.4 StartY=-2.7 StartZ=0 EndX=-6 EndY=-2.7 EndZ=0
    g4: LineSegment StartX=-6 StartY=-2.7 StartZ=0 EndX=-6 EndY=0 EndZ=0
    g5: LineSegment StartX=-6 StartY=0 StartZ=0 EndX=-6.8 EndY=0 EndZ=0
    g6: LineSegment StartX=-4.6 StartY=0.8 StartZ=0 EndX=-4 EndY=0.8 EndZ=0
    g7: LineSegment StartX=-4 StartY=0.8 StartZ=0 EndX=-4 EndY=-2.7 EndZ=0
    g8: LineSegment StartX=-4 StartY=-2.7 StartZ=0 EndX=-4.6 EndY=-2.7 EndZ=0
    g9: LineSegment StartX=-4.6 StartY=-2.7 StartZ=0 EndX=-4.6 EndY=0.8 EndZ=0
  constraints (30):
    c: Vertical(g0)
    c: Coincident(g0,g1)
    c: Horizontal(g1)
    c: Coincident(g1,g2)
    c: Vertical(g2)
    c: Coincident(g2,g3)
    c: Horizontal(g3)
    c: Coincident(g3,g4)
    c: Vertical(g4)
    c: Coincident(g4,g5)
    c: Coincident(g5,g0)
    c: Horizontal(g5)
    c: Coincident(g6,g7)
    c: Coincident(g7,g8)
    c: Coincident(g8,g9)
    c: Coincident(g9,g6)
    c: Horizontal(g6)
    c: Horizontal(g8)
    c: Vertical(g7)
    c: Vertical(g9)
    c: PointOnObject(g6,g1)
    c: PointOnObject(g4,g-1)
    c: DistanceY(g2,g2) = 3.5
    c: PointOnObject(g8,g3)
    c: DistanceX(g3) = -6
    c: DistanceX(g6) = -4
    c: Equal(g3,g6)
    c: DistanceX(g6,g6) = 0.6
    c: DistanceX(g0) = -6.8
    c: DistanceY(g0,g0) = 0.8
FEATURE [PartDesign::Revolution] Revolution005
  AddSubType = 0
  Angle = 360
  Axis = (0,1,0)
  Base = (0,0,0)
  ClaimChildren = false
  Fit = 0
  FitJoin = 0
  FixShape = 1
  InnerFit = 0
  InnerFitJoin = 0
  InvalidShape = false
  NewSolid = false
  Profile = -> Sketch116
  ReferenceAxis = -> Sketch116 [V_Axis]
  Refine = true
  Suppress = false
  TreeRank = 0
  ValidateShape = true
  _ProfileBasedVersion = 0
FEATURE [PartDesign::Body] Body052  label="CoreMF128"
  AutoGroupSolids = false
  ClaimAllChildren = false
  ExportMode = 0
  FixShape = 1
  Group = -> [Sketch116,Revolution005]
  InvalidShape = false
  Origin = -> Origin016
  Tip = -> Revolution005
  TreeRank = 0
  ValidateShape = false
  _ExportChildren = -> [Revolution005]
  _GroupVersion = 1
FEATURE [Sketcher::SketchObject] Sketch117
  ArcFitTolerance = 0
  ExternalBSplineMaxDegree = 0
  ExternalBSplineTolerance = 0
  FixShape = 1
  FullyConstrained = true
  InternalTolerance = 1e-06
  InvalidShape = false
  MakeInternals = false
  MapMode = 5
  TreeRank = 0
  ValidateShape = false
  sketch-geometry (4):
    g0: LineSegment StartX=-5.5 StartY=0.55 StartZ=0 EndX=-4.5 EndY=0.55 EndZ=0
    g1: LineSegment StartX=-4.5 StartY=0.55 StartZ=0 EndX=-4.5 EndY=-2.45 EndZ=0
    g2: LineSegment StartX=-4.5 StartY=-2.45 StartZ=0 EndX=-5.5 EndY=-2.45 EndZ=0
    g3: LineSegment StartX=-5.5 StartY=-2.45 StartZ=0 EndX=-5.5 EndY=0.55 EndZ=0
  constraints (12):
    c: Coincident(g0,g1)
    c: Coincident(g1,g2)
    c: Coincident(g2,g3)
    c: Coincident(g3,g0)
    c: Horizontal(g0)
    c: Horizontal(g2)
    c: Vertical(g1)
    c: Vertical(g3)
    c: DistanceY(g3,g3) = 3
    c: DistanceX(g0,g0) = 1
    c: DistanceX(g0,g-1) = 4.5
    c: DistanceY(g-1,g0) = 0.55
FEATURE [PartDesign::Revolution] Revolution006
  AddSubType = 0
  Angle = 360
  Axis = (0,1,0)
  Base = (0,0,0)
  ClaimChildren = false
  Fit = 0
  FitJoin = 0
  FixShape = 1
  InnerFit = 0
  InnerFitJoin = 0
  InvalidShape = false
  NewSolid = false
  Profile = -> Sketch117
  ReferenceAxis = -> Sketch117 [V_Axis]
  Refine = true
  Suppress = false
  TreeRank = 0
  ValidateShape = true
  _ProfileBasedVersion = 0
FEATURE [PartDesign::Body] Body053  label="SleeveMF128"
  AutoGroupSolids = false
  ClaimAllChildren = false
  ExportMode = 0
  FixShape = 1
  Group = -> [Sketch117,Revolution006]
  InvalidShape = false
  Origin = -> Origin081
  SingleSolid = true
  Tip = -> Revolution006
  TreeRank = 0
  ValidateShape = false
  _ExportChildren = -> [Revolution006]
  _GroupVersion = 1
FEATURE [App::Part] Part023  label="MF128"
  ClaimAllChildren = false
  ExportMode = 1
  Group = -> [Body052,Body053]
  Origin = -> Origin076
  TreeRank = 0
  _ExportChildren = -> [Body052,Body053]
  _GroupVersion = 1
FEATURE [Sketcher::SketchObject] Sketch160
  ArcFitTolerance = 0
  ExternalBSplineMaxDegree = 0
  ExternalBSplineTolerance = 0
  FixShape = 1
  FullyConstrained = true
  InternalTolerance = 1e-06
  InvalidShape = false
  MakeInternals = false
  MapMode = 5
  TreeRank = 0
  ValidateShape = false
  sketch-geometry (10):
    g0: LineSegment StartX=-4.6 StartY=0 StartZ=0 EndX=-4.6 EndY=0.6 EndZ=0
    g1: LineSegment StartX=-4.6 StartY=0.6 StartZ=0 EndX=-3.4 EndY=0.6 EndZ=0
    g2: LineSegment StartX=-3.4 StartY=0.6 StartZ=0 EndX=-3.4 EndY=-2.4 EndZ=0
    g3: LineSegment StartX=-3.4 StartY=-2.4 StartZ=0 EndX=-4 EndY=-2.4 EndZ=0
    g4: LineSegment StartX=-4 StartY=-2.4 StartZ=0 EndX=-4 EndY=0 EndZ=0
    g5: LineSegment StartX=-4 StartY=0 StartZ=0 EndX=-4.6 EndY=0 EndZ=0
    g6: LineSegment StartX=-2.1 StartY=0.6 StartZ=0 EndX=-1.5 EndY=0.6 EndZ=0
    g7: LineSegment StartX=-1.5 StartY=0.6 StartZ=0 EndX=-1.5 EndY=-2.4 EndZ=0
    g8: LineSegment StartX=-1.5 StartY=-2.4 StartZ=0 EndX=-2.1 EndY=-2.4 EndZ=0
    g9: LineSegment StartX=-2.1 StartY=-2.4 StartZ=0 EndX=-2.1 EndY=0.6 EndZ=0
  constraints (30):
    c: Vertical(g0)
    c: Coincident(g0,g1)
    c: Horizontal(g1)
    c: Coincident(g1,g2)
    c: Vertical(g2)
    c: Coincident(g2,g3)
    c: Horizontal(g3)
    c: Coincident(g3,g4)
    c: Vertical(g4)
    c: Coincident(g4,g5)
    c: Coincident(g5,g0)
    c: Horizontal(g5)
    c: Coincident(g6,g7)
    c: Coincident(g7,g8)
    c: Coincident(g8,g9)
    c: Coincident(g9,g6)
    c: Horizontal(g6)
    c: Horizontal(g8)
    c: Vertical(g7)
    c: Vertical(g9)
    c: PointOnObject(g6,g1)
    c: PointOnObject(g4,g-1)
    c: DistanceY(g2,g2) = 3
    c: PointOnObject(g8,g3)
    c: DistanceX(g3) = -4
    c: DistanceX(g6) = -1.5
    c: Equal(g3,g6)
    c: DistanceX(g6,g6) = 0.6
    c: DistanceX(g0) = -4.6
    c: DistanceY(g0,g0) = 0.6
FEATURE [PartDesign::Revolution] Revolution010
  AddSubType = 0
  Angle = 360
  Axis = (0,1,0)
  Base = (0,0,0)
  ClaimChildren = false
  Fit = 0
  FitJoin = 0
  FixShape = 1
  InnerFit = 0
  InnerFitJoin = 0
  InvalidShape = false
  NewSolid = false
  Profile = -> Sketch160
  ReferenceAxis = -> Sketch160 [V_Axis]
  Refine = true
  Suppress = false
  TreeRank = 0
  ValidateShape = true
  _ProfileBasedVersion = 0
FEATURE [PartDesign::Body] Body074  label="CoreMF83"
  AutoGroupSolids = false
  ClaimAllChildren = false
  ExportMode = 0
  FixShape = 1
  Group = -> [Sketch160,Revolution010]
  InvalidShape = false
  Origin = -> Origin158
  Placement = pos=(0,2.8e-14,0) rot=(0,0,1;0rad)
  Tip = -> Revolution010
  TreeRank = 0
  ValidateShape = false
  _ExportChildren = -> [Revolution010]
  _GroupVersion = 1
FEATURE [Sketcher::SketchObject] Sketch161
  ArcFitTolerance = 0
  ExternalBSplineMaxDegree = 0
  ExternalBSplineTolerance = 0
  FixShape = 1
  FullyConstrained = true
  InternalTolerance = 1e-06
  InvalidShape = false
  MakeInternals = false
  MapMode = 5
  TreeRank = 0
  ValidateShape = false
  sketch-geometry (4):
    g0: LineSegment StartX=-3.4 StartY=0.5 StartZ=0 EndX=-2.1 EndY=0.5 EndZ=0
    g1: LineSegment StartX=-2.1 StartY=0.5 StartZ=0 EndX=-2.1 EndY=-2.3 EndZ=0
    g2: LineSegment StartX=-2.1 StartY=-2.3 StartZ=0 EndX=-3.4 EndY=-2.3 EndZ=0
    g3: LineSegment StartX=-3.4 StartY=-2.3 StartZ=0 EndX=-3.4 EndY=0.5 EndZ=0
  constraints (12):
    c: Coincident(g0,g1)
    c: Coincident(g1,g2)
    c: Coincident(g2,g3)
    c: Coincident(g3,g0)
    c: Horizontal(g0)
    c: Horizontal(g2)
    c: Vertical(g1)
    c: Vertical(g3)
    c: DistanceY(g3,g3) = 2.8
    c: DistanceX(g0,g0) = 1.3
    c: DistanceX(g0,g-1) = 2.1
    c: DistanceY(g-1,g0) = 0.5
FEATURE [PartDesign::Revolution] Revolution011
  AddSubType = 0
  Angle = 360
  Axis = (1e-16,1,-1e-16)
  Base = (0,0,0)
  ClaimChildren = false
  Fit = 0
  FitJoin = 0
  FixShape = 1
  InnerFit = 0
  InnerFitJoin = 0
  InvalidShape = false
  NewSolid = false
  Profile = -> Sketch161
  ReferenceAxis = -> Y_Axis092
  Refine = true
  Suppress = false
  TreeRank = 0
  ValidateShape = true
  _ProfileBasedVersion = 0
FEATURE [PartDesign::Body] Body075  label="SleeveMF83"
  AutoGroupSolids = false
  ClaimAllChildren = false
  ExportMode = 0
  FixShape = 1
  Group = -> [Sketch161,Revolution011]
  InvalidShape = false
  Origin = -> Origin159
  Placement = pos=(0,2.8e-14,0) rot=(0,0,1;0rad)
  SingleSolid = true
  Tip = -> Revolution011
  TreeRank = 0
  ValidateShape = false
  _ExportChildren = -> [Revolution011]
  _GroupVersion = 1
FEATURE [App::Part] Part034  label="MF83"
  ClaimAllChildren = false
  ExportMode = 1
  Group = -> [Body074,Body075]
  Origin = -> Origin160
  TreeRank = 0
  _ExportChildren = -> [Body074,Body075]
  _GroupVersion = 1
FEATURE [Sketcher::SketchObject] Sketch118
  ArcFitTolerance = 0
  ExternalBSplineMaxDegree = 0
  ExternalBSplineTolerance = 0
  FixShape = 1
  FullyConstrained = true
  InternalTolerance = 1e-06
  InvalidShape = false
  MakeInternals = false
  MapMode = 5
  Placement = pos=(0,0,0) rot=(1,0,0;1.5708rad)
  TreeRank = 0
  ValidateShape = false
  sketch-geometry (12):
    g0: LineSegment StartX=-6 StartY=2.67e-14 StartZ=0 EndX=-7 EndY=-1.177e-13 EndZ=0
    g1: LineSegment StartX=-7 StartY=-1.177e-13 StartZ=0 EndX=-7 EndY=4 EndZ=0
    g2: LineSegment StartX=-7 StartY=4 StartZ=0 EndX=-6 EndY=4 EndZ=0
    g3: LineSegment StartX=-6 StartY=4 StartZ=0 EndX=-6 EndY=3.6 EndZ=0
    g4: LineSegment StartX=-6 StartY=3.6 StartZ=0 EndX=-5 EndY=3.6 EndZ=0
    g5: LineSegment StartX=-5 StartY=3.6 StartZ=0 EndX=-5 EndY=4 EndZ=0
    g6: LineSegment StartX=-5 StartY=4 StartZ=0 EndX=-4 EndY=4 EndZ=0
    g7: LineSegment StartX=-4 StartY=4 StartZ=0 EndX=-4 EndY=0 EndZ=0
    g8: LineSegment StartX=-4 StartY=0 StartZ=0 EndX=-5 EndY=0 EndZ=0
    g9: LineSegment StartX=-5 StartY=0 StartZ=0 EndX=-5 EndY=0.4 EndZ=0
    g10: LineSegment StartX=-5 StartY=0.4 StartZ=0 EndX=-6 EndY=0.4 EndZ=0
    g11: LineSegment StartX=-6 StartY=0.4 StartZ=0 EndX=-6 EndY=2.67e-14 EndZ=0
  constraints (36):
    c: PointOnObject(g0,g-1)
    c: PointOnObject(g0,g-1)
    c: Coincident(g0,g1)
    c: Vertical(g1)
    c: Coincident(g1,g2)
    c: Horizontal(g2)
    c: Coincident(g2,g3)
    c: Vertical(g3)
    c: Coincident(g3,g4)
    c: Horizontal(g4)
    c: Coincident(g4,g5)
    c: Vertical(g5)
    c: Coincident(g5,g6)
    c: Horizontal(g6)
    c: Coincident(g6,g7)
    c: PointOnObject(g7,g-1)
    c: Vertical(g7)
    c: Coincident(g7,g8)
    c: PointOnObject(g8,g-1)
    c: Coincident(g8,g9)
    c: Vertical(g9)
    c: Coincident(g9,g10)
    c: Horizontal(g10)
    c: Coincident(g10,g11)
    c: Coincident(g11,g0)
    c: Vertical(g11)
    c: DistanceX(g7) = -4
    c: DistanceX(g0) = -7
    c: Equal(g8,g0)
    c: Equal(g2,g6)
    c: Equal(g4,g10)
    c: Equal(g3,g11)
    c: DistanceY(g3,g3) = 0.4
    c: DistanceX(g8,g8) = 1
    c: DistanceY(g1,g1) = 4
    c: PointOnObject(g2,g6)
FEATURE [PartDesign::Revolution] Revolution007
  AddSubType = 0
  Angle = 360
  Axis = (0,0,1)
  Base = (0,0,0)
  ClaimChildren = false
  Fit = 0
  FitJoin = 0
  FixShape = 1
  InnerFit = 0
  InnerFitJoin = 0
  InvalidShape = false
  NewSolid = false
  Placement = pos=(0,0,0) rot=(1,0,0;1.5708rad)
  Profile = -> Sketch118
  ReferenceAxis = -> Sketch118 [V_Axis]
  Refine = true
  Suppress = false
  TreeRank = 0
  ValidateShape = true
  _ProfileBasedVersion = 0
FEATURE [PartDesign::Body] Body054  label="CoreMR148"
  AutoGroupSolids = false
  ClaimAllChildren = false
  ExportMode = 0
  FixShape = 1
  Group = -> [Sketch118,Revolution007]
  InvalidShape = false
  Origin = -> Origin162
  SingleSolid = true
  Tip = -> Revolution007
  TreeRank = 0
  ValidateShape = false
  _ExportChildren = -> [Revolution007]
  _GroupVersion = 1
FEATURE [Sketcher::SketchObject] Sketch119
  ArcFitTolerance = 0
  ExternalBSplineMaxDegree = 0
  ExternalBSplineTolerance = 0
  FixShape = 1
  FullyConstrained = true
  InternalTolerance = 1e-06
  InvalidShape = false
  MakeInternals = false
  MapMode = 5
  Placement = pos=(0,0,0) rot=(1,0,0;1.5708rad)
  TreeRank = 0
  ValidateShape = false
  sketch-geometry (4):
    g0: LineSegment StartX=-6 StartY=4 StartZ=0 EndX=-5 EndY=4 EndZ=0
    g1: LineSegment StartX=-5 StartY=4 StartZ=0 EndX=-5 EndY=0 EndZ=0
    g2: LineSegment StartX=-5 StartY=0 StartZ=0 EndX=-6 EndY=0 EndZ=0
    g3: LineSegment StartX=-6 StartY=0 StartZ=0 EndX=-6 EndY=4 EndZ=0
  constraints (12):
    c: Coincident(g0,g1)
    c: Coincident(g1,g2)
    c: Coincident(g2,g3)
    c: Coincident(g3,g0)
    c: Horizontal(g0)
    c: Horizontal(g2)
    c: Vertical(g1)
    c: Vertical(g3)
    c: PointOnObject(g1,g-1)
    c: DistanceY(g3,g3) = 4
    c: DistanceX(g1) = -5
    c: DistanceX(g2) = -6
FEATURE [PartDesign::Revolution] Revolution008
  AddSubType = 0
  Angle = 360
  Axis = (0,0,1)
  Base = (0,0,0)
  ClaimChildren = false
  Fit = 0
  FitJoin = 0
  FixShape = 1
  InnerFit = 0
  InnerFitJoin = 0
  InvalidShape = false
  NewSolid = false
  Placement = pos=(0,0,0) rot=(1,0,0;1.5708rad)
  Profile = -> Sketch119
  ReferenceAxis = -> Sketch119 [V_Axis]
  Refine = true
  Suppress = false
  TreeRank = 0
  ValidateShape = true
  _ProfileBasedVersion = 0
FEATURE [PartDesign::Body] Body055  label="Sleeve"
  AutoGroupSolids = false
  ClaimAllChildren = false
  ExportMode = 0
  FixShape = 1
  Group = -> [Sketch119,Revolution008]
  InvalidShape = false
  Origin = -> Origin082
  SingleSolid = true
  Tip = -> Revolution008
  TreeRank = 0
  ValidateShape = false
  _ExportChildren = -> [Revolution008]
  _GroupVersion = 1
FEATURE [App::Part] Part001  label="MR148"
  ClaimAllChildren = false
  ExportMode = 1
  Group = -> [Body054,Body055]
  Origin = -> Origin161
  Placement = pos=(0,0,0) rot=(0,0.707107,-0.707107;3.14159rad)
  TreeRank = 0
  _ExportChildren = -> [Body054,Body055]
  _GroupVersion = 1
FEATURE [Sketcher::SketchObject] Sketch169
  ArcFitTolerance = 0
  ExternalBSplineMaxDegree = 0
  ExternalBSplineTolerance = 0
  FixShape = 1
  FullyConstrained = true
  InternalTolerance = 1e-06
  InvalidShape = false
  MakeInternals = false
  MapMode = 5
  Placement = pos=(0,0,0) rot=(1,0,0;1.5708rad)
  TreeRank = 0
  ValidateShape = false
  sketch-geometry (12):
    g0: LineSegment StartX=-5.5 StartY=1.2718e-12 StartZ=0 EndX=-6.5 EndY=1.052e-12 EndZ=0
    g1: LineSegment StartX=-6.5 StartY=1.052e-12 StartZ=0 EndX=-6.5 EndY=5 EndZ=0
    g2: LineSegment StartX=-6.5 StartY=5 StartZ=0 EndX=-5.5 EndY=5 EndZ=0
    g3: LineSegment StartX=-5.5 StartY=5 StartZ=0 EndX=-5.5 EndY=4.6 EndZ=0
    g4: LineSegment StartX=-5.5 StartY=4.6 StartZ=0 EndX=-2.5 EndY=4.6 EndZ=0
    g5: LineSegment StartX=-2.5 StartY=4.6 StartZ=0 EndX=-2.5 EndY=5 EndZ=0
    g6: LineSegment StartX=-2.5 StartY=5 StartZ=0 EndX=-1.5 EndY=5 EndZ=0
    g7: LineSegment StartX=-1.5 StartY=5 StartZ=0 EndX=-1.5 EndY=0 EndZ=0
    g8: LineSegment StartX=-1.5 StartY=0 StartZ=0 EndX=-2.5 EndY=0 EndZ=0
    g9: LineSegment StartX=-2.5 StartY=0 StartZ=0 EndX=-2.5 EndY=0.4 EndZ=0
    g10: LineSegment StartX=-2.5 StartY=0.4 StartZ=0 EndX=-5.5 EndY=0.4 EndZ=0
    g11: LineSegment StartX=-5.5 StartY=0.4 StartZ=0 EndX=-5.5 EndY=1.2718e-12 EndZ=0
  constraints (36):
    c: PointOnObject(g0,g-1)
    c: PointOnObject(g0,g-1)
    c: Coincident(g0,g1)
    c: Vertical(g1)
    c: Coincident(g1,g2)
    c: Horizontal(g2)
    c: Coincident(g2,g3)
    c: Vertical(g3)
    c: Coincident(g3,g4)
    c: Horizontal(g4)
    c: Coincident(g4,g5)
    c: Vertical(g5)
    c: Coincident(g5,g6)
    c: Horizontal(g6)
    c: Coincident(g6,g7)
    c: PointOnObject(g7,g-1)
    c: Vertical(g7)
    c: Coincident(g7,g8)
    c: PointOnObject(g8,g-1)
    c: Coincident(g8,g9)
    c: Vertical(g9)
    c: Coincident(g9,g10)
    c: Horizontal(g10)
    c: Coincident(g10,g11)
    c: Coincident(g11,g0)
    c: Vertical(g11)
    c: DistanceX(g7) = -1.5
    c: DistanceX(g0) = -6.5
    c: Equal(g8,g0)
    c: Equal(g2,g6)
    c: Equal(g4,g10)
    c: Equal(g3,g11)
    c: DistanceY(g3,g3) = 0.4
    c: DistanceX(g8,g8) = 1
    c: DistanceY(g1,g1) = 5
    c: PointOnObject(g2,g6)
FEATURE [PartDesign::Revolution] Revolution012
  AddSubType = 0
  Angle = 360
  Axis = (0,0,1)
  Base = (0,0,0)
  ClaimChildren = false
  Fit = 0
  FitJoin = 0
  FixShape = 1
  InnerFit = 0
  InnerFitJoin = 0
  InvalidShape = false
  NewSolid = false
  Placement = pos=(0,0,0) rot=(1,0,0;1.5708rad)
  Profile = -> Sketch169
  ReferenceAxis = -> Sketch169 [V_Axis]
  Refine = true
  Suppress = false
  TreeRank = 0
  ValidateShape = true
  _ProfileBasedVersion = 0
FEATURE [PartDesign::Body] Body080  label="CoreMR149"
  AutoGroupSolids = false
  ClaimAllChildren = false
  ExportMode = 0
  FixShape = 1
  Group = -> [Sketch169,Revolution012]
  InvalidShape = false
  Origin = -> Origin166
  SingleSolid = true
  Tip = -> Revolution012
  TreeRank = 0
  ValidateShape = false
  _ExportChildren = -> [Revolution012]
  _GroupVersion = 1
FEATURE [Sketcher::SketchObject] Sketch170
  ArcFitTolerance = 0
  ExternalBSplineMaxDegree = 0
  ExternalBSplineTolerance = 0
  FixShape = 1
  FullyConstrained = true
  InternalTolerance = 1e-06
  InvalidShape = false
  MakeInternals = false
  MapMode = 5
  Placement = pos=(0,0,0) rot=(1,0,0;1.5708rad)
  TreeRank = 0
  ValidateShape = false
  sketch-geometry (4):
    g0: LineSegment StartX=-5.5 StartY=5 StartZ=0 EndX=-2.5 EndY=5 EndZ=0
    g1: LineSegment StartX=-2.5 StartY=5 StartZ=0 EndX=-2.5 EndY=0 EndZ=0
    g2: LineSegment StartX=-2.5 StartY=3e-16 StartZ=0 EndX=-5.5 EndY=3e-16 EndZ=0
    g3: LineSegment StartX=-5.5 StartY=3e-16 StartZ=0 EndX=-5.5 EndY=5 EndZ=0
  constraints (12):
    c: Coincident(g0,g1)
    c: Coincident(g1,g2)
    c: Coincident(g2,g3)
    c: Coincident(g3,g0)
    c: Horizontal(g0)
    c: Horizontal(g2)
    c: Vertical(g1)
    c: Vertical(g3)
    c: PointOnObject(g1,g-1)
    c: DistanceY(g3,g3) = 5
    c: DistanceX(g1) = -2.5
    c: DistanceX(g2) = -5.5
FEATURE [PartDesign::Revolution] Revolution013
  AddSubType = 0
  Angle = 360
  Axis = (0,0,1)
  Base = (0,0,0)
  ClaimChildren = false
  Fit = 0
  FitJoin = 0
  FixShape = 1
  InnerFit = 0
  InnerFitJoin = 0
  InvalidShape = false
  NewSolid = false
  Placement = pos=(0,0,0) rot=(1,0,0;1.5708rad)
  Profile = -> Sketch170
  ReferenceAxis = -> Sketch170 [V_Axis]
  Refine = true
  Suppress = false
  TreeRank = 0
  ValidateShape = true
  _ProfileBasedVersion = 0
FEATURE [PartDesign::Body] Body081  label="Sleeve001"
  AutoGroupSolids = false
  ClaimAllChildren = false
  ExportMode = 0
  FixShape = 1
  Group = -> [Sketch170,Revolution013]
  InvalidShape = false
  Origin = -> Origin167
  SingleSolid = true
  Tip = -> Revolution013
  TreeRank = 0
  ValidateShape = false
  _ExportChildren = -> [Revolution013]
  _GroupVersion = 1
FEATURE [App::Part] Part035  label="633ZZ"
  ClaimAllChildren = false
  ExportMode = 1
  Group = -> [Body080,Body081]
  Origin = -> Origin165
  Placement = pos=(0,0,0) rot=(0,0.707107,-0.707107;3.14159rad)
  TreeRank = 0
  _ExportChildren = -> [Body080,Body081]
  _GroupVersion = 1
FEATURE [Sketcher::SketchObject] Sketch202
  ArcFitTolerance = 0
  ExternalBSplineMaxDegree = 0
  ExternalBSplineTolerance = 0
  FixShape = 1
  FullyConstrained = true
  InternalTolerance = 1e-06
  InvalidShape = false
  MakeInternals = false
  MapMode = 5
  TreeRank = 0
  ValidateShape = false
  sketch-geometry (12):
    g0: LineSegment StartX=0 StartY=1.5 StartZ=0 EndX=4 EndY=1.5 EndZ=0
    g1: LineSegment StartX=4 StartY=1.5 StartZ=0 EndX=4 EndY=2.5 EndZ=0
    g2: LineSegment StartX=4 StartY=2.5 StartZ=0 EndX=3.5 EndY=2.5 EndZ=0
    g3: LineSegment StartX=3.5 StartY=2.5 StartZ=0 EndX=3.5 EndY=4 EndZ=0
    g4: LineSegment StartX=3.5 StartY=4 StartZ=0 EndX=4 EndY=4 EndZ=0
    g5: LineSegment StartX=4 StartY=4 StartZ=0 EndX=4 EndY=5 EndZ=0
    g6: LineSegment StartX=4 StartY=5 StartZ=0 EndX=0 EndY=5 EndZ=0
    g7: LineSegment StartX=0 StartY=5 StartZ=0 EndX=0 EndY=4 EndZ=0
    g8: LineSegment StartX=0 StartY=4 StartZ=0 EndX=0.5 EndY=4 EndZ=0
    g9: LineSegment StartX=0.5 StartY=4 StartZ=0 EndX=0.5 EndY=2.5 EndZ=0
    g10: LineSegment StartX=0.5 StartY=2.5 StartZ=0 EndX=0 EndY=2.5 EndZ=0
    g11: LineSegment StartX=0 StartY=2.5 StartZ=0 EndX=0 EndY=1.5 EndZ=0
  constraints (36):
    c: PointOnObject(g0,g-2)
    c: Horizontal(g0)
    c: Coincident(g1,g0)
    c: Vertical(g1)
    c: Coincident(g1,g2)
    c: Horizontal(g2)
    c: Coincident(g2,g3)
    c: Vertical(g3)
    c: Coincident(g3,g4)
    c: Horizontal(g4)
    c: Coincident(g4,g5)
    c: Vertical(g5)
    c: Coincident(g5,g6)
    c: PointOnObject(g6,g-2)
    c: Horizontal(g6)
    c: Coincident(g6,g7)
    c: PointOnObject(g7,g-2)
    c: Coincident(g7,g8)
    c: Horizontal(g8)
    c: Coincident(g8,g9)
    c: Vertical(g9)
    c: Coincident(g9,g10)
    c: PointOnObject(g10,g-2)
    c: Horizontal(g10)
    c: Coincident(g10,g11)
    c: Coincident(g11,g0)
    c: Equal(g4,g8)
    c: Equal(g10,g2)
    c: DistanceY(g-1,g0) = 1.5
    c: PointOnObject(g9,g2)
    c: PointOnObject(g8,g4)
    c: DistanceY(g-1,g6) = 5
    c: DistanceY(g-1,g10) = 2.5
    c: DistanceY(g-1,g7) = 4
    c: DistanceX(g6,g6) = 4
    c: DistanceX(g8,g3) = 3
FEATURE [PartDesign::Revolution] Revolution018
  AddSubType = 0
  Angle = 360
  Axis = (1,0,0)
  Base = (0,0,0)
  ClaimChildren = false
  Fit = 0
  FitJoin = 0
  FixShape = 1
  InnerFit = 0
  InnerFitJoin = 0
  InvalidShape = false
  NewSolid = false
  Profile = -> Sketch202
  ReferenceAxis = -> Sketch202 [H_Axis]
  Refine = true
  Suppress = false
  TreeRank = 0
  ValidateShape = true
  _ProfileBasedVersion = 0
FEATURE [PartDesign::Body] Body097
  AutoGroupSolids = false
  ClaimAllChildren = false
  ExportMode = 0
  FixShape = 1
  Group = -> [Sketch202,Revolution018]
  InvalidShape = false
  Origin = -> Origin188
  SingleSolid = true
  Tip = -> Revolution018
  TreeRank = 0
  ValidateShape = false
  _ExportChildren = -> [Revolution018]
  _GroupVersion = 1
FEATURE [Sketcher::SketchObject] Sketch203
  ArcFitTolerance = 0
  ExternalBSplineMaxDegree = 0
  ExternalBSplineTolerance = 0
  FixShape = 1
  FullyConstrained = true
  InternalTolerance = 1e-06
  InvalidShape = false
  MakeInternals = false
  MapMode = 5
  TreeRank = 0
  ValidateShape = false
  sketch-geometry (4):
    g0: LineSegment StartX=0.1 StartY=4 StartZ=0 EndX=3.9 EndY=4 EndZ=0
    g1: LineSegment StartX=3.9 StartY=4 StartZ=0 EndX=3.9 EndY=2.5 EndZ=0
    g2: LineSegment StartX=3.9 StartY=2.5 StartZ=0 EndX=0.1 EndY=2.5 EndZ=0
    g3: LineSegment StartX=0.1 StartY=2.5 StartZ=0 EndX=0.1 EndY=4 EndZ=0
  constraints (12):
    c: Coincident(g0,g1)
    c: Coincident(g1,g2)
    c: Coincident(g2,g3)
    c: Coincident(g3,g0)
    c: Horizontal(g0)
    c: Horizontal(g2)
    c: Vertical(g1)
    c: Vertical(g3)
    c: DistanceY(g-1,g2) = 2.5
    c: DistanceY(g-1,g0) = 4
    c: DistanceX(g0,g0) = 3.8
    c: DistanceX(g-1,g2) = 0.1
FEATURE [PartDesign::Revolution] Revolution019
  AddSubType = 0
  Angle = 360
  Axis = (1,0,0)
  Base = (0,0,0)
  ClaimChildren = false
  Fit = 0
  FitJoin = 0
  FixShape = 1
  InnerFit = 0
  InnerFitJoin = 0
  InvalidShape = false
  NewSolid = false
  Profile = -> Sketch203
  ReferenceAxis = -> Sketch203 [H_Axis]
  Refine = true
  Suppress = false
  TreeRank = 0
  ValidateShape = true
  _ProfileBasedVersion = 0
FEATURE [PartDesign::Body] Body098
  AutoGroupSolids = false
  ClaimAllChildren = false
  ExportMode = 0
  FixShape = 1
  Group = -> [Sketch203,Revolution019]
  InvalidShape = false
  Origin = -> Origin189
  SingleSolid = true
  Tip = -> Revolution019
  TreeRank = 0
  ValidateShape = false
  _ExportChildren = -> [Revolution019]
  _GroupVersion = 1
FEATURE [App::Part] Part041  label="623ZZ"
  ClaimAllChildren = false
  ExportMode = 1
  Group = -> [Body097,Body098]
  Origin = -> Origin187
  Placement = pos=(0,0,0) rot=(0,0,1;4.71239rad)
  TreeRank = 0
  _ExportChildren = -> [Body097,Body098]
  _GroupVersion = 1
FEATURE [Sketcher::SketchObject] Sketch204
  ArcFitTolerance = 0
  ExternalBSplineMaxDegree = 0
  ExternalBSplineTolerance = 0
  FixShape = 1
  FullyConstrained = true
  InternalTolerance = 1e-06
  InvalidShape = false
  MakeInternals = false
  MapMode = 5
  TreeRank = 0
  ValidateShape = false
  sketch-geometry (7):
    g0: LineSegment StartX=4 StartY=0 StartZ=0 EndX=4 EndY=4 EndZ=0
    g1: LineSegment StartX=4 StartY=4 StartZ=0 EndX=6 EndY=4 EndZ=0
    g2: LineSegment StartX=6 StartY=4 StartZ=0 EndX=6 EndY=3.25 EndZ=0
    g3: LineSegment StartX=6 StartY=3.25 StartZ=0 EndX=4.85 EndY=2 EndZ=0
    g4: LineSegment StartX=4.85 StartY=2 StartZ=0 EndX=6 EndY=0.75 EndZ=0
    g5: LineSegment StartX=6 StartY=0.75 StartZ=0 EndX=6 EndY=0 EndZ=0
    g6: LineSegment StartX=6 StartY=0 StartZ=0 EndX=4 EndY=0 EndZ=0
  constraints (21):
    c: PointOnObject(g0,g-1)
    c: Vertical(g0)
    c: Coincident(g0,g1)
    c: Horizontal(g1)
    c: Coincident(g1,g2)
    c: Vertical(g2)
    c: Coincident(g2,g3)
    c: Coincident(g3,g4)
    c: Coincident(g4,g5)
    c: PointOnObject(g5,g-1)
    c: Vertical(g5)
    c: Coincident(g5,g6)
    c: Coincident(g6,g0)
    c: DistanceX(g-1,g0) = 4
    c: Equal(g3,g4)
    c: Equal(g1,g6)
    c: Equal(g5,g2)
    c: DistanceX(g-1,g5) = 6
    c: DistanceX(g-1,g3) = 4.85
    c: DistanceY(g0,g0) = 4
    c: DistanceY(g4,g2) = 2.5
FEATURE [PartDesign::Revolution] Revolution020
  AddSubType = 0
  Angle = 360
  Axis = (0,1,0)
  Base = (0,0,0)
  ClaimChildren = false
  Fit = 0
  FitJoin = 0
  FixShape = 1
  InnerFit = 0
  InnerFitJoin = 0
  InvalidShape = false
  NewSolid = false
  Profile = -> Sketch204
  ReferenceAxis = -> Sketch204 [V_Axis]
  Refine = true
  Reversed = true
  Suppress = false
  TreeRank = 0
  ValidateShape = true
  _ProfileBasedVersion = 0
FEATURE [PartDesign::Body] Body101  label="V623ZZ-extern"
  AutoGroupSolids = false
  ClaimAllChildren = false
  ExportMode = 0
  FixShape = 1
  Group = -> [Sketch204,Revolution020]
  InvalidShape = false
  Origin = -> Origin194
  SingleSolid = true
  Tip = -> Revolution020
  TreeRank = 0
  ValidateShape = false
  _ExportChildren = -> [Revolution020]
  _GroupVersion = 1
FEATURE [Sketcher::SketchObject] Sketch205
  ArcFitTolerance = 0
  ExternalBSplineMaxDegree = 0
  ExternalBSplineTolerance = 0
  FixShape = 1
  FullyConstrained = true
  InternalTolerance = 1e-06
  InvalidShape = false
  MakeInternals = false
  MapMode = 5
  Placement = pos=(0,0,0) rot=(0.57735,0.57735,0.57735;2.0944rad)
  TreeRank = 0
  ValidateShape = false
  sketch-geometry (8):
    g0: LineSegment StartX=0.2 StartY=4 StartZ=0 EndX=0.2 EndY=2.1 EndZ=0
    g1: LineSegment StartX=0.2 StartY=2.1 StartZ=0 EndX=0 EndY=2.1 EndZ=0
    g2: LineSegment StartX=0 StartY=2.1 StartZ=0 EndX=0 EndY=1.5 EndZ=0
    g3: LineSegment StartX=0 StartY=1.5 StartZ=0 EndX=4 EndY=1.5 EndZ=0
    g4: LineSegment StartX=4 StartY=1.5 StartZ=0 EndX=4 EndY=2.1 EndZ=0
    g5: LineSegment StartX=4 StartY=2.1 StartZ=0 EndX=3.8 EndY=2.1 EndZ=0
    g6: LineSegment StartX=3.8 StartY=2.1 StartZ=0 EndX=3.8 EndY=4 EndZ=0
    g7: LineSegment StartX=3.8 StartY=4 StartZ=0 EndX=0.2 EndY=4 EndZ=0
  constraints (24):
    c: Vertical(g0)
    c: Coincident(g0,g1)
    c: PointOnObject(g1,g-2)
    c: Horizontal(g1)
    c: Coincident(g1,g2)
    c: PointOnObject(g2,g-2)
    c: Coincident(g2,g3)
    c: Horizontal(g3)
    c: Coincident(g3,g4)
    c: Coincident(g4,g5)
    c: Horizontal(g5)
    c: Coincident(g5,g6)
    c: Vertical(g6)
    c: Coincident(g6,g7)
    c: Coincident(g7,g0)
    c: Horizontal(g7)
    c: DistanceY(g-1,g0) = 4
    c: Equal(g1,g5)
    c: Equal(g4,g2)
    c: DistanceX(g3,g3) = 4
    c: Vertical(g4)
    c: DistanceY(g-1,g2) = 1.5
    c: DistanceY(g2,g2) = 0.6
    c: DistanceX(g1,g1) = 0.2
FEATURE [PartDesign::Revolution] Revolution021
  AddSubType = 0
  Angle = 360
  Axis = (1e-16,1,-1e-16)
  Base = (0,0,0)
  ClaimChildren = false
  Fit = 0
  FitJoin = 0
  FixShape = 1
  InnerFit = 0
  InnerFitJoin = 0
  InvalidShape = false
  NewSolid = false
  Placement = pos=(0,0,0) rot=(0.57735,0.57735,0.57735;2.0944rad)
  Profile = -> Sketch205
  ReferenceAxis = -> Y_Axis120
  Refine = true
  Suppress = false
  TreeRank = 0
  ValidateShape = true
  _ProfileBasedVersion = 0
FEATURE [PartDesign::Body] Body100  label="V623ZZ-intern"
  AutoGroupSolids = false
  ClaimAllChildren = false
  ExportMode = 0
  FixShape = 1
  Group = -> [Sketch205,Revolution021]
  InvalidShape = false
  Origin = -> Origin193
  SingleSolid = true
  Tip = -> Revolution021
  TreeRank = 0
  ValidateShape = false
  _ExportChildren = -> [Revolution021]
  _GroupVersion = 1
FEATURE [App::Part] Part043  label="V623ZZ"
  ClaimAllChildren = false
  ExportMode = 1
  Group = -> [Body100,Body101]
  Origin = -> Origin192
  Placement = pos=(0,0,0) rot=(0,0,-1;3.14159rad)
  TreeRank = 0
  _ExportChildren = -> [Body100,Body101]
  _GroupVersion = 1
FEATURE [App::DocumentObjectGroup] Group002  label="Bearings"
  ClaimAllChildren = true
  ExportMode = 1
  Group = -> [Part023,Part034,Part001,Part035,Part041,Part043]
  TreeRank = 0
  _GroupVersion = 1
FEATURE [Sketcher::SketchObject] Sketch006
  ArcFitTolerance = 0
  ExternalBSplineMaxDegree = 0
  ExternalBSplineTolerance = 0
  FixShape = 1
  FullyConstrained = true
  InternalTolerance = 1e-06
  InvalidShape = false
  MakeInternals = false
  MapMode = 5
  Placement = pos=(0,0,0) rot=(1,0,0;1.5708rad)
  TreeRank = 0
  ValidateShape = false
  sketch-geometry (14):
    g0: ArcOfCircle CenterX=0 CenterY=0 CenterZ=0 NormalX=0 NormalY=0 NormalZ=1 AngleXU=0 Radius=1.25 StartAngle=0 EndAngle=1.5708
    g1: LineSegment StartX=1e-16 StartY=1.25 StartZ=0 EndX=0 EndY=2 EndZ=0
    g2: LineSegment StartX=0 StartY=2 StartZ=0 EndX=1 EndY=2 EndZ=0
    g3: LineSegment [constr] StartX=0 StartY=0 StartZ=0 EndX=5 EndY=5 EndZ=0
    g4: LineSegment StartX=1 StartY=2 StartZ=0 EndX=3.3 EndY=4 EndZ=0
    g5: LineSegment StartX=3.3 StartY=4 StartZ=0 EndX=1.5 EndY=4 EndZ=0
    g6: LineSegment StartX=1.5 StartY=4 StartZ=0 EndX=1.5 EndY=5 EndZ=0
    g7: LineSegment StartX=1.5 StartY=5 StartZ=0 EndX=5 EndY=5 EndZ=0
    g8: LineSegment StartX=5 StartY=5 StartZ=0 EndX=5 EndY=1.5 EndZ=0
    g9: LineSegment StartX=5 StartY=1.5 StartZ=0 EndX=4 EndY=1.5 EndZ=0
    g10: LineSegment StartX=4 StartY=1.5 StartZ=0 EndX=4 EndY=3.3 EndZ=0
    g11: LineSegment StartX=4 StartY=3.3 StartZ=0 EndX=2 EndY=1 EndZ=0
    g12: LineSegment StartX=2 StartY=1 StartZ=0 EndX=2 EndY=0 EndZ=0
    g13: LineSegment StartX=2 StartY=0 StartZ=0 EndX=1.25 EndY=0 EndZ=0
  constraints (41):
    c: Coincident(g0,g-1)
    c: PointOnObject(g0,g-1)
    c: PointOnObject(g0,g-2)
    c: Coincident(g1,g0)
    c: PointOnObject(g1,g-2)
    c: Coincident(g2,g1)
    c: Horizontal(g2)
    c: Coincident(g3,g0)
    c: Angle(g-1,g3) = 0.785398
    c: DistanceX(g3) = 5
    c: Diameter(g0) = 2.5
    c: DistanceX(g2) = 1
    c: Coincident(g4,g2)
    c: Coincident(g5,g4)
    c: Horizontal(g5)
    c: Coincident(g6,g5)
    c: Vertical(g6)
    c: Coincident(g7,g6)
    c: Coincident(g7,g3)
    c: Coincident(g8,g7)
    c: Vertical(g8)
    c: Coincident(g9,g8)
    c: Coincident(g10,g9)
    c: Vertical(g10)
    c: Coincident(g11,g10)
    c: Coincident(g12,g11)
    c: PointOnObject(g12,g-1)
    c: Vertical(g12)
    c: Coincident(g13,g12)
    c: Coincident(g13,g0)
    c: Equal(g12,g2)
    c: Equal(g13,g1)
    c: Horizontal(g7)
    c: Horizontal(g9)
    c: Equal(g6,g9)
    c: Equal(g11,g4)
    c: Equal(g5,g10)
    c: DistanceY(g2,g6) = 3
    c: DistanceX(g6) = 1.5
    c: DistanceY(g6,g6) = 1
    c: DistanceX(g5,g5) = 1.8
FEATURE [PartDesign::Pad] Pad004
  AddSubType = 0
  AutoTaperInnerAngle = true
  CheckUpToFaceLimits = true
  ClaimChildren = false
  Direction = (0,-1,0)
  Fit = 0
  FitJoin = 0
  FixShape = 1
  InnerFit = 0
  InnerFitJoin = 0
  InvalidShape = false
  Length = 300
  Length2 = 100
  NewSolid = false
  Placement = pos=(0,0,0) rot=(1,0,0;1.5708rad)
  Profile = -> Sketch006
  Refine = true
  Reversed = true
  Suppress = false
  TaperInnerAngle = 0
  TaperInnerAngleRev = 0
  TreeRank = 0
  Type = 0
  ValidateShape = true
  _ProfileBasedVersion = 0
FEATURE [PartDesign::PolarPattern] PolarPattern006
  AddSubType = 0
  Angle = 360
  Axis = -> Y_Axis004
  BaseFeature = -> Pad004
  CopyShape = true
  FixShape = 1
  InvalidShape = false
  NewSolid = false
  Occurrences = 4
  OriginalSubs = -> [Pad004]
  Originals = -> [Pad004]
  ParallelTransform = true
  Placement = pos=(0,0,0) rot=(1,0,0;1.5708rad)
  Refine = true
  SubTransform = true
  Suppress = false
  TreeRank = 0
  ValidateShape = true
  _Version = 0
FEATURE [PartDesign::Body] Body004  label="MB_300"
  AutoGroupSolids = false
  ClaimAllChildren = false
  ExportMode = 0
  FixShape = 1
  Group = -> [Sketch006,Pad004,PolarPattern006]
  InvalidShape = false
  Origin = -> Origin004
  SingleSolid = true
  Tip = -> PolarPattern006
  TreeRank = 0
  ValidateShape = false
  _ExportChildren = -> [Pad004,PolarPattern006]
  _GroupVersion = 1
FEATURE [PartDesign::CoordinateSystem] Local_CS004
  AttacherType = Attacher::AttachEngine3D
  FixShape = 1
  InvalidShape = false
  MapMode = 11
  Placement = pos=(0,200,-4.4e-14) rot=(0.57735,0.57735,-0.57735;2.0944rad)
  TreeRank = 0
  ValidateShape = false
FEATURE [Sketcher::SketchObject] Sketch201
  ArcFitTolerance = 0
  ExternalBSplineMaxDegree = 0
  ExternalBSplineTolerance = 0
  FixShape = 1
  FullyConstrained = true
  InternalTolerance = 1e-06
  InvalidShape = false
  MakeInternals = false
  MapMode = 5
  Placement = pos=(0,0,0) rot=(1,0,0;1.5708rad)
  TreeRank = 0
  ValidateShape = false
  sketch-geometry (14):
    g0: ArcOfCircle CenterX=0 CenterY=0 CenterZ=0 NormalX=0 NormalY=0 NormalZ=1 AngleXU=0 Radius=1.25 StartAngle=0 EndAngle=1.5708
    g1: LineSegment StartX=1e-16 StartY=1.25 StartZ=0 EndX=0 EndY=2 EndZ=0
    g2: LineSegment StartX=0 StartY=2 StartZ=0 EndX=1 EndY=2 EndZ=0
    g3: LineSegment [constr] StartX=0 StartY=0 StartZ=0 EndX=5 EndY=5 EndZ=0
    g4: LineSegment StartX=1 StartY=2 StartZ=0 EndX=3.3 EndY=4 EndZ=0
    g5: LineSegment StartX=3.3 StartY=4 StartZ=0 EndX=1.5 EndY=4 EndZ=0
    g6: LineSegment StartX=1.5 StartY=4 StartZ=0 EndX=1.5 EndY=5 EndZ=0
    g7: LineSegment StartX=1.5 StartY=5 StartZ=0 EndX=5 EndY=5 EndZ=0
    g8: LineSegment StartX=5 StartY=5 StartZ=0 EndX=5 EndY=1.5 EndZ=0
    g9: LineSegment StartX=5 StartY=1.5 StartZ=0 EndX=4 EndY=1.5 EndZ=0
    g10: LineSegment StartX=4 StartY=1.5 StartZ=0 EndX=4 EndY=3.3 EndZ=0
    g11: LineSegment StartX=4 StartY=3.3 StartZ=0 EndX=2 EndY=1 EndZ=0
    g12: LineSegment StartX=2 StartY=1 StartZ=0 EndX=2 EndY=0 EndZ=0
    g13: LineSegment StartX=2 StartY=0 StartZ=0 EndX=1.25 EndY=0 EndZ=0
  constraints (41):
    c: Coincident(g0,g-1)
    c: PointOnObject(g0,g-1)
    c: PointOnObject(g0,g-2)
    c: Coincident(g1,g0)
    c: PointOnObject(g1,g-2)
    c: Coincident(g2,g1)
    c: Horizontal(g2)
    c: Coincident(g3,g0)
    c: Angle(g-1,g3) = 0.785398
    c: DistanceX(g3) = 5
    c: Diameter(g0) = 2.5
    c: DistanceX(g2) = 1
    c: Coincident(g4,g2)
    c: Coincident(g5,g4)
    c: Horizontal(g5)
    c: Coincident(g6,g5)
    c: Vertical(g6)
    c: Coincident(g7,g6)
    c: Coincident(g7,g3)
    c: Coincident(g8,g7)
    c: Vertical(g8)
    c: Coincident(g9,g8)
    c: Coincident(g10,g9)
    c: Vertical(g10)
    c: Coincident(g11,g10)
    c: Coincident(g12,g11)
    c: PointOnObject(g12,g-1)
    c: Vertical(g12)
    c: Coincident(g13,g12)
    c: Coincident(g13,g0)
    c: Equal(g12,g2)
    c: Equal(g13,g1)
    c: Horizontal(g7)
    c: Horizontal(g9)
    c: Equal(g6,g9)
    c: Equal(g11,g4)
    c: Equal(g5,g10)
    c: DistanceY(g2,g6) = 3
    c: DistanceX(g6) = 1.5
    c: DistanceY(g6,g6) = 1
    c: DistanceX(g5,g5) = 1.8
FEATURE [PartDesign::Pad] Pad082
  AddSubType = 0
  AlongSketchNormal = false
  AutoTaperInnerAngle = true
  CheckUpToFaceLimits = true
  ClaimChildren = false
  Direction = (0,-1,0)
  Fit = 0
  FitJoin = 0
  FixShape = 1
  InnerFit = 0
  InnerFitJoin = 0
  InvalidShape = false
  Length = 200
  Length2 = 100
  NewSolid = false
  Placement = pos=(0,0,0) rot=(1,0,0;1.5708rad)
  Profile = -> Sketch201
  Refine = true
  Reversed = true
  Suppress = false
  TaperInnerAngle = 0
  TaperInnerAngleRev = 0
  TreeRank = 0
  Type = 0
  ValidateShape = true
  _ProfileBasedVersion = 0
FEATURE [PartDesign::PolarPattern] PolarPattern014
  AddSubType = 0
  Angle = 360
  Axis = -> Y_Axis116
  BaseFeature = -> Pad082
  CopyShape = true
  FixShape = 1
  InvalidShape = false
  NewSolid = false
  Occurrences = 4
  OriginalSubs = -> [Pad082]
  Originals = -> [Pad082]
  ParallelTransform = true
  Placement = pos=(0,0,0) rot=(1,0,0;1.5708rad)
  Refine = true
  SubTransform = true
  Suppress = false
  TreeRank = 0
  ValidateShape = true
  _Version = 0
FEATURE [PartDesign::Body] Body096  label="MB_200"
  AutoGroupSolids = false
  ClaimAllChildren = false
  ExportMode = 0
  FixShape = 1
  Group = -> [Sketch201,Pad082,PolarPattern014,Local_CS004]
  InvalidShape = false
  Origin = -> Origin186
  SingleSolid = true
  Tip = -> PolarPattern014
  TreeRank = 0
  ValidateShape = false
  _ExportChildren = -> [Pad082,PolarPattern014,Local_CS004]
  _GroupVersion = 1
FEATURE [PartDesign::CoordinateSystem] Local_CS003
  AttacherType = Attacher::AttachEngine3D
  FixShape = 1
  InvalidShape = false
  MapMode = 11
  Placement = pos=(0,150,-3.3e-14) rot=(0.57735,0.57735,-0.57735;2.0944rad)
  TreeRank = 0
  ValidateShape = false
FEATURE [Sketcher::SketchObject] Sketch200
  ArcFitTolerance = 0
  ExternalBSplineMaxDegree = 0
  ExternalBSplineTolerance = 0
  FixShape = 1
  FullyConstrained = true
  InternalTolerance = 1e-06
  InvalidShape = false
  MakeInternals = false
  MapMode = 5
  Placement = pos=(0,0,0) rot=(1,0,0;1.5708rad)
  TreeRank = 0
  ValidateShape = false
  sketch-geometry (14):
    g0: ArcOfCircle CenterX=0 CenterY=0 CenterZ=0 NormalX=0 NormalY=0 NormalZ=1 AngleXU=0 Radius=1.25 StartAngle=0 EndAngle=1.5708
    g1: LineSegment StartX=1e-16 StartY=1.25 StartZ=0 EndX=0 EndY=2 EndZ=0
    g2: LineSegment StartX=0 StartY=2 StartZ=0 EndX=1 EndY=2 EndZ=0
    g3: LineSegment [constr] StartX=0 StartY=0 StartZ=0 EndX=5 EndY=5 EndZ=0
    g4: LineSegment StartX=1 StartY=2 StartZ=0 EndX=3.3 EndY=4 EndZ=0
    g5: LineSegment StartX=3.3 StartY=4 StartZ=0 EndX=1.5 EndY=4 EndZ=0
    g6: LineSegment StartX=1.5 StartY=4 StartZ=0 EndX=1.5 EndY=5 EndZ=0
    g7: LineSegment StartX=1.5 StartY=5 StartZ=0 EndX=5 EndY=5 EndZ=0
    g8: LineSegment StartX=5 StartY=5 StartZ=0 EndX=5 EndY=1.5 EndZ=0
    g9: LineSegment StartX=5 StartY=1.5 StartZ=0 EndX=4 EndY=1.5 EndZ=0
    g10: LineSegment StartX=4 StartY=1.5 StartZ=0 EndX=4 EndY=3.3 EndZ=0
    g11: LineSegment StartX=4 StartY=3.3 StartZ=0 EndX=2 EndY=1 EndZ=0
    g12: LineSegment StartX=2 StartY=1 StartZ=0 EndX=2 EndY=0 EndZ=0
    g13: LineSegment StartX=2 StartY=0 StartZ=0 EndX=1.25 EndY=0 EndZ=0
  constraints (41):
    c: Coincident(g0,g-1)
    c: PointOnObject(g0,g-1)
    c: PointOnObject(g0,g-2)
    c: Coincident(g1,g0)
    c: PointOnObject(g1,g-2)
    c: Coincident(g2,g1)
    c: Horizontal(g2)
    c: Coincident(g3,g0)
    c: Angle(g-1,g3) = 0.785398
    c: DistanceX(g3) = 5
    c: Diameter(g0) = 2.5
    c: DistanceX(g2) = 1
    c: Coincident(g4,g2)
    c: Coincident(g5,g4)
    c: Horizontal(g5)
    c: Coincident(g6,g5)
    c: Vertical(g6)
    c: Coincident(g7,g6)
    c: Coincident(g7,g3)
    c: Coincident(g8,g7)
    c: Vertical(g8)
    c: Coincident(g9,g8)
    c: Coincident(g10,g9)
    c: Vertical(g10)
    c: Coincident(g11,g10)
    c: Coincident(g12,g11)
    c: PointOnObject(g12,g-1)
    c: Vertical(g12)
    c: Coincident(g13,g12)
    c: Coincident(g13,g0)
    c: Equal(g12,g2)
    c: Equal(g13,g1)
    c: Horizontal(g7)
    c: Horizontal(g9)
    c: Equal(g6,g9)
    c: Equal(g11,g4)
    c: Equal(g5,g10)
    c: DistanceY(g2,g6) = 3
    c: DistanceX(g6) = 1.5
    c: DistanceY(g6,g6) = 1
    c: DistanceX(g5,g5) = 1.8
FEATURE [PartDesign::Pad] Pad081
  AddSubType = 0
  AlongSketchNormal = false
  AutoTaperInnerAngle = true
  CheckUpToFaceLimits = true
  ClaimChildren = false
  Direction = (0,-1,0)
  Fit = 0
  FitJoin = 0
  FixShape = 1
  InnerFit = 0
  InnerFitJoin = 0
  InvalidShape = false
  Length = 150
  Length2 = 100
  NewSolid = false
  Placement = pos=(0,0,0) rot=(1,0,0;1.5708rad)
  Profile = -> Sketch200
  Refine = true
  Reversed = true
  Suppress = false
  TaperInnerAngle = 0
  TaperInnerAngleRev = 0
  TreeRank = 0
  Type = 0
  ValidateShape = true
  _ProfileBasedVersion = 0
FEATURE [PartDesign::PolarPattern] PolarPattern013
  AddSubType = 0
  Angle = 360
  Axis = -> Y_Axis115
  BaseFeature = -> Pad081
  CopyShape = true
  FixShape = 1
  InvalidShape = false
  NewSolid = false
  Occurrences = 4
  OriginalSubs = -> [Pad081]
  Originals = -> [Pad081]
  ParallelTransform = true
  Placement = pos=(0,0,0) rot=(1,0,0;1.5708rad)
  Refine = true
  SubTransform = true
  Suppress = false
  TreeRank = 0
  ValidateShape = true
  _Version = 0
FEATURE [PartDesign::Body] Body095  label="MB_150"
  AutoGroupSolids = false
  ClaimAllChildren = false
  ExportMode = 0
  FixShape = 1
  Group = -> [Sketch200,Pad081,PolarPattern013,Local_CS003]
  InvalidShape = false
  Origin = -> Origin185
  SingleSolid = true
  Tip = -> PolarPattern013
  TreeRank = 0
  ValidateShape = false
  _ExportChildren = -> [Pad081,PolarPattern013,Local_CS003]
  _GroupVersion = 1
FEATURE [PartDesign::CoordinateSystem] Local_CS
  AttacherType = Attacher::AttachEngine3D
  FixShape = 1
  InvalidShape = false
  Placement = pos=(4.4e-14,100,0) rot=(1,0,0;1.5708rad)
  TreeRank = 0
  ValidateShape = false
FEATURE [Sketcher::SketchObject] Sketch206
  ArcFitTolerance = 0
  ExternalBSplineMaxDegree = 0
  ExternalBSplineTolerance = 0
  FixShape = 1
  FullyConstrained = true
  InternalTolerance = 1e-06
  InvalidShape = false
  MakeInternals = false
  MapMode = 5
  Placement = pos=(0,0,0) rot=(1,0,0;1.5708rad)
  TreeRank = 0
  ValidateShape = false
  sketch-geometry (14):
    g0: ArcOfCircle CenterX=0 CenterY=0 CenterZ=0 NormalX=0 NormalY=0 NormalZ=1 AngleXU=0 Radius=1.25 StartAngle=0 EndAngle=1.5708
    g1: LineSegment StartX=1e-16 StartY=1.25 StartZ=0 EndX=0 EndY=2 EndZ=0
    g2: LineSegment StartX=0 StartY=2 StartZ=0 EndX=1 EndY=2 EndZ=0
    g3: LineSegment [constr] StartX=0 StartY=0 StartZ=0 EndX=5 EndY=5 EndZ=0
    g4: LineSegment StartX=1 StartY=2 StartZ=0 EndX=3.3 EndY=4 EndZ=0
    g5: LineSegment StartX=3.3 StartY=4 StartZ=0 EndX=1.5 EndY=4 EndZ=0
    g6: LineSegment StartX=1.5 StartY=4 StartZ=0 EndX=1.5 EndY=5 EndZ=0
    g7: LineSegment StartX=1.5 StartY=5 StartZ=0 EndX=5 EndY=5 EndZ=0
    g8: LineSegment StartX=5 StartY=5 StartZ=0 EndX=5 EndY=1.5 EndZ=0
    g9: LineSegment StartX=5 StartY=1.5 StartZ=0 EndX=4 EndY=1.5 EndZ=0
    g10: LineSegment StartX=4 StartY=1.5 StartZ=0 EndX=4 EndY=3.3 EndZ=0
    g11: LineSegment StartX=4 StartY=3.3 StartZ=0 EndX=2 EndY=1 EndZ=0
    g12: LineSegment StartX=2 StartY=1 StartZ=0 EndX=2 EndY=0 EndZ=0
    g13: LineSegment StartX=2 StartY=0 StartZ=0 EndX=1.25 EndY=0 EndZ=0
  constraints (41):
    c: Coincident(g0,g-1)
    c: PointOnObject(g0,g-1)
    c: PointOnObject(g0,g-2)
    c: Coincident(g1,g0)
    c: PointOnObject(g1,g-2)
    c: Coincident(g2,g1)
    c: Horizontal(g2)
    c: Coincident(g3,g0)
    c: Angle(g-1,g3) = 0.785398
    c: DistanceX(g3) = 5
    c: Diameter(g0) = 2.5
    c: DistanceX(g2) = 1
    c: Coincident(g4,g2)
    c: Coincident(g5,g4)
    c: Horizontal(g5)
    c: Coincident(g6,g5)
    c: Vertical(g6)
    c: Coincident(g7,g6)
    c: Coincident(g7,g3)
    c: Coincident(g8,g7)
    c: Vertical(g8)
    c: Coincident(g9,g8)
    c: Coincident(g10,g9)
    c: Vertical(g10)
    c: Coincident(g11,g10)
    c: Coincident(g12,g11)
    c: PointOnObject(g12,g-1)
    c: Vertical(g12)
    c: Coincident(g13,g12)
    c: Coincident(g13,g0)
    c: Equal(g12,g2)
    c: Equal(g13,g1)
    c: Horizontal(g7)
    c: Horizontal(g9)
    c: Equal(g6,g9)
    c: Equal(g11,g4)
    c: Equal(g5,g10)
    c: DistanceY(g2,g6) = 3
    c: DistanceX(g6) = 1.5
    c: DistanceY(g6,g6) = 1
    c: DistanceX(g5,g5) = 1.8
FEATURE [PartDesign::Pad] Pad083
  AddSubType = 0
  AutoTaperInnerAngle = true
  CheckUpToFaceLimits = true
  ClaimChildren = false
  Direction = (0,-1,0)
  Fit = 0
  FitJoin = 0
  FixShape = 1
  InnerFit = 0
  InnerFitJoin = 0
  InvalidShape = false
  Length = 100
  Length2 = 100
  NewSolid = false
  Placement = pos=(0,0,0) rot=(1,0,0;1.5708rad)
  Profile = -> Sketch206
  Refine = true
  Reversed = true
  Suppress = false
  TaperInnerAngle = 0
  TaperInnerAngleRev = 0
  TreeRank = 0
  Type = 0
  ValidateShape = true
  _ProfileBasedVersion = 0
FEATURE [PartDesign::PolarPattern] PolarPattern004
  AddSubType = 0
  Angle = 360
  Axis = -> Y_Axis002
  BaseFeature = -> Pad083
  CopyShape = true
  FixShape = 1
  InvalidShape = false
  NewSolid = false
  Occurrences = 4
  OriginalSubs = -> [Pad083]
  Originals = -> [Pad083]
  ParallelTransform = true
  Placement = pos=(0,0,0) rot=(1,0,0;1.5708rad)
  Refine = true
  SubTransform = true
  Suppress = false
  TreeRank = 0
  ValidateShape = true
  _Version = 0
FEATURE [PartDesign::Body] Body002  label="MB_100"
  AutoGroupSolids = false
  ClaimAllChildren = false
  ExportMode = 0
  FixShape = 1
  Group = -> [Sketch206,Pad083,PolarPattern004,Local_CS]
  InvalidShape = false
  Origin = -> Origin002
  SingleSolid = true
  Tip = -> PolarPattern004
  TreeRank = 0
  ValidateShape = false
  _ExportChildren = -> [Pad083,PolarPattern004,Local_CS]
  _GroupVersion = 1
FEATURE [Sketcher::SketchObject] Sketch005
  ArcFitTolerance = 0
  ExternalBSplineMaxDegree = 0
  ExternalBSplineTolerance = 0
  FixShape = 1
  FullyConstrained = true
  InternalTolerance = 1e-06
  InvalidShape = false
  MakeInternals = false
  MapMode = 5
  Placement = pos=(0,0,0) rot=(1,0,0;1.5708rad)
  TreeRank = 0
  ValidateShape = false
  sketch-geometry (14):
    g0: ArcOfCircle CenterX=0 CenterY=0 CenterZ=0 NormalX=0 NormalY=0 NormalZ=1 AngleXU=0 Radius=1.25 StartAngle=0 EndAngle=1.5708
    g1: LineSegment StartX=1e-16 StartY=1.25 StartZ=0 EndX=0 EndY=2 EndZ=0
    g2: LineSegment StartX=0 StartY=2 StartZ=0 EndX=1 EndY=2 EndZ=0
    g3: LineSegment [constr] StartX=0 StartY=0 StartZ=0 EndX=5 EndY=5 EndZ=0
    g4: LineSegment StartX=1 StartY=2 StartZ=0 EndX=3.3 EndY=4 EndZ=0
    g5: LineSegment StartX=3.3 StartY=4 StartZ=0 EndX=1.5 EndY=4 EndZ=0
    g6: LineSegment StartX=1.5 StartY=4 StartZ=0 EndX=1.5 EndY=5 EndZ=0
    g7: LineSegment StartX=1.5 StartY=5 StartZ=0 EndX=5 EndY=5 EndZ=0
    g8: LineSegment StartX=5 StartY=5 StartZ=0 EndX=5 EndY=1.5 EndZ=0
    g9: LineSegment StartX=5 StartY=1.5 StartZ=0 EndX=4 EndY=1.5 EndZ=0
    g10: LineSegment StartX=4 StartY=1.5 StartZ=0 EndX=4 EndY=3.3 EndZ=0
    g11: LineSegment StartX=4 StartY=3.3 StartZ=0 EndX=2 EndY=1 EndZ=0
    g12: LineSegment StartX=2 StartY=1 StartZ=0 EndX=2 EndY=0 EndZ=0
    g13: LineSegment StartX=2 StartY=0 StartZ=0 EndX=1.25 EndY=0 EndZ=0
  constraints (41):
    c: Coincident(g0,g-1)
    c: PointOnObject(g0,g-1)
    c: PointOnObject(g0,g-2)
    c: Coincident(g1,g0)
    c: PointOnObject(g1,g-2)
    c: Coincident(g2,g1)
    c: Horizontal(g2)
    c: Coincident(g3,g0)
    c: Angle(g-1,g3) = 0.785398
    c: DistanceX(g3) = 5
    c: Diameter(g0) = 2.5
    c: DistanceX(g2) = 1
    c: Coincident(g4,g2)
    c: Coincident(g5,g4)
    c: Horizontal(g5)
    c: Coincident(g6,g5)
    c: Vertical(g6)
    c: Coincident(g7,g6)
    c: Coincident(g7,g3)
    c: Coincident(g8,g7)
    c: Vertical(g8)
    c: Coincident(g9,g8)
    c: Coincident(g10,g9)
    c: Vertical(g10)
    c: Coincident(g11,g10)
    c: Coincident(g12,g11)
    c: PointOnObject(g12,g-1)
    c: Vertical(g12)
    c: Coincident(g13,g12)
    c: Coincident(g13,g0)
    c: Equal(g12,g2)
    c: Equal(g13,g1)
    c: Horizontal(g7)
    c: Horizontal(g9)
    c: Equal(g6,g9)
    c: Equal(g11,g4)
    c: Equal(g5,g10)
    c: DistanceY(g2,g6) = 3
    c: DistanceX(g6) = 1.5
    c: DistanceY(g6,g6) = 1
    c: DistanceX(g5,g5) = 1.8
FEATURE [PartDesign::Pad] Pad003
  AddSubType = 0
  AutoTaperInnerAngle = true
  CheckUpToFaceLimits = true
  ClaimChildren = false
  Direction = (0,-1,0)
  Fit = 0
  FitJoin = 0
  FixShape = 1
  InnerFit = 0
  InnerFitJoin = 0
  InvalidShape = false
  Length = 60
  Length2 = 100
  NewSolid = false
  Placement = pos=(0,0,0) rot=(1,0,0;1.5708rad)
  Profile = -> Sketch005
  Refine = true
  Reversed = true
  Suppress = false
  TaperInnerAngle = 0
  TaperInnerAngleRev = 0
  TreeRank = 0
  Type = 0
  ValidateShape = true
  _ProfileBasedVersion = 0
FEATURE [PartDesign::PolarPattern] PolarPattern005
  AddSubType = 0
  Angle = 360
  AttacherType = Attacher::AttachEngine3D
  Axis = -> Y_Axis003
  BaseFeature = -> Pad003
  CopyShape = true
  FixShape = 1
  InvalidShape = false
  NewSolid = false
  Occurrences = 4
  OriginalSubs = -> [Pad003]
  Originals = -> [Pad003]
  ParallelTransform = true
  Placement = pos=(0,0,0) rot=(1,0,0;1.5708rad)
  Refine = true
  SubTransform = true
  Suppress = false
  TreeRank = 0
  ValidateShape = true
  _Version = 0
FEATURE [PartDesign::Body] Body003  label="MB_60"
  AutoGroupSolids = false
  ClaimAllChildren = false
  ExportMode = 0
  FixShape = 1
  Group = -> [Sketch005,Pad003,PolarPattern005]
  InvalidShape = false
  Origin = -> Origin003
  SingleSolid = true
  Tip = -> PolarPattern005
  TreeRank = 0
  ValidateShape = false
  _ExportChildren = -> [Pad003,PolarPattern005]
  _GroupVersion = 1
FEATURE [PartDesign::Plane] DatumPlane
  AttachmentOffset = pos=(0,0,5) rot=(0,0,1;0rad)
  FixShape = 1
  InvalidShape = false
  Length = 10
  MapMode = 5
  MinimumLength = 10
  MinimumWidth = 10
  Placement = pos=(5,0,0) rot=(0.57735,0.57735,0.57735;2.0944rad)
  ResizeMode = 0
  TreeRank = 0
  ValidateShape = false
  Width = 10
FEATURE [PartDesign::PolarPattern] PolarPattern
  AddSubType = 0
  Angle = 90
  Axis = -> Z_Axis001
  CopyShape = true
  FixShape = 1
  InvalidShape = false
  NewSolid = false
  Occurrences = 2
  ParallelTransform = true
  Placement = pos=(0,0,0) rot=(0.57735,0.57735,0.57735;2.0944rad)
  Refine = true
  SubTransform = true
  Suppress = false
  TreeRank = 0
  ValidateShape = true
  _Version = 0
FEATURE [PartDesign::PolarPattern] PolarPattern001
  AddSubType = 0
  Angle = 90
  Axis = -> Y_Axis001
  CopyShape = true
  FixShape = 1
  InvalidShape = false
  NewSolid = false
  Occurrences = 2
  ParallelTransform = true
  Placement = pos=(0,0,0) rot=(0.57735,0.57735,0.57735;2.0944rad)
  Refine = true
  SubTransform = true
  Suppress = false
  TreeRank = 0
  ValidateShape = true
  _Version = 0
FEATURE [PartDesign::PolarPattern] PolarPattern002
  AddSubType = 0
  Angle = 90
  Axis = -> Y_Axis001
  CopyShape = true
  FixShape = 1
  InvalidShape = false
  NewSolid = false
  Occurrences = 2
  ParallelTransform = true
  Placement = pos=(0,0,0) rot=(0.57735,0.57735,0.57735;2.0944rad)
  Refine = true
  SubTransform = true
  Suppress = false
  TreeRank = 0
  ValidateShape = true
  _Version = 0
FEATURE [PartDesign::PolarPattern] PolarPattern003
  AddSubType = 0
  Angle = 90
  Axis = -> Z_Axis001
  CopyShape = true
  FixShape = 1
  InvalidShape = false
  NewSolid = false
  Occurrences = 2
  ParallelTransform = true
  Placement = pos=(0,0,0) rot=(0.57735,0.57735,0.57735;2.0944rad)
  Refine = true
  SubTransform = true
  Suppress = false
  TreeRank = 0
  ValidateShape = true
  _Version = 0
FEATURE [Sketcher::SketchObject] Sketch207
  ArcFitTolerance = 0
  ExternalBSplineMaxDegree = 0
  ExternalBSplineTolerance = 0
  FixShape = 1
  FullyConstrained = true
  InternalTolerance = 1e-06
  InvalidShape = false
  MakeInternals = false
  MapMode = 5
  Placement = pos=(0,0,0) rot=(0.57735,0.57735,0.57735;2.0944rad)
  TreeRank = 0
  ValidateShape = false
  sketch-geometry (4):
    g0: LineSegment StartX=-5 StartY=5 StartZ=0 EndX=5 EndY=5 EndZ=0
    g1: LineSegment StartX=5 StartY=5 StartZ=0 EndX=5 EndY=-5 EndZ=0
    g2: LineSegment StartX=5 StartY=-5 StartZ=0 EndX=-5 EndY=-5 EndZ=0
    g3: LineSegment StartX=-5 StartY=-5 StartZ=0 EndX=-5 EndY=5 EndZ=0
  constraints (11):
    c: Coincident(g0,g1)
    c: Coincident(g1,g2)
    c: Coincident(g2,g3)
    c: Coincident(g3,g0)
    c: Horizontal(g0)
    c: Horizontal(g2)
    c: Vertical(g1)
    c: Vertical(g3)
    c: Symmetric(g1,g0,g-1)
    c: Equal(g0,g3)
    c: DistanceX(g0,g0) = 10
FEATURE [PartDesign::Pad] Pad084
  AddSubType = 0
  AutoTaperInnerAngle = true
  CheckUpToFaceLimits = true
  ClaimChildren = false
  Direction = (1,1e-16,-1e-16)
  Fit = 0
  FitJoin = 0
  FixShape = 1
  InnerFit = 0
  InnerFitJoin = 0
  InvalidShape = false
  Length = 10
  Length2 = 100
  Midplane = true
  NewSolid = false
  Placement = pos=(0,0,0) rot=(0.57735,0.57735,0.57735;2.0944rad)
  Profile = -> Sketch207
  Refine = true
  Suppress = false
  TaperInnerAngle = 0
  TaperInnerAngleRev = 0
  TreeRank = 0
  Type = 0
  ValidateShape = true
  _ProfileBasedVersion = 0
FEATURE [Sketcher::SketchObject] Sketch208
  ArcFitTolerance = 0
  ExternalBSplineMaxDegree = 0
  ExternalBSplineTolerance = 0
  FixShape = 1
  FullyConstrained = true
  InternalTolerance = 1e-06
  InvalidShape = false
  MakeInternals = false
  MapMode = 5
  Placement = pos=(0,0,0) rot=(0.57735,0.57735,0.57735;2.0944rad)
  TreeRank = 0
  ValidateShape = false
  sketch-geometry (1):
    g0: Circle CenterX=0 CenterY=0 CenterZ=0 NormalX=0 NormalY=0 NormalZ=1 AngleXU=0 Radius=1.5
  constraints (2):
    c: Coincident(g0,g-1)
    c: Diameter(g0) = 3
FEATURE [PartDesign::Pocket] Pocket039
  AddSubType = 1
  AutoTaperInnerAngle = true
  BaseFeature = -> Pad084
  CheckUpToFaceLimits = true
  ClaimChildren = false
  Direction = (-1,-1e-16,1e-16)
  Fit = 0
  FitJoin = 0
  FixShape = 1
  InnerFit = 0
  InnerFitJoin = 0
  InvalidShape = false
  Length = 5
  Length2 = 100
  Midplane = true
  NewSolid = false
  Placement = pos=(0,0,0) rot=(0.57735,0.57735,0.57735;2.0944rad)
  Profile = -> Sketch208
  Refine = true
  Suppress = false
  TaperInnerAngle = 0
  TaperInnerAngleRev = 0
  TreeRank = 0
  Type = 1
  ValidateShape = true
  _ProfileBasedVersion = 0
  _Version = 0
FEATURE [PartDesign::MultiTransform] MultiTransform
  AddSubType = 0
  BaseFeature = -> Pocket039
  CopyShape = true
  FixShape = 1
  InvalidShape = false
  NewSolid = false
  OriginalSubs = -> [Pocket039]
  Originals = -> [Pocket039]
  ParallelTransform = true
  Placement = pos=(0,0,0) rot=(0.57735,0.57735,0.57735;2.0944rad)
  Refine = true
  SubTransform = true
  Suppress = false
  Transformations = -> [PolarPattern,PolarPattern001]
  TreeRank = 0
  ValidateShape = true
  _Version = 0
FEATURE [Sketcher::SketchObject] Sketch209
  ArcFitTolerance = 0
  ExternalBSplineMaxDegree = 0
  ExternalBSplineTolerance = 0
  FixShape = 1
  FullyConstrained = true
  InternalTolerance = 1e-06
  InvalidShape = false
  MakeInternals = false
  MapMode = 5
  Placement = pos=(5,0,0) rot=(0.57735,0.57735,0.57735;2.0944rad)
  TreeRank = 0
  ValidateShape = false
  sketch-geometry (1):
    g0: Circle CenterX=0 CenterY=0 CenterZ=0 NormalX=0 NormalY=0 NormalZ=1 AngleXU=0 Radius=3
  constraints (2):
    c: Coincident(g0,g-1)
    c: Diameter(g0) = 6
FEATURE [PartDesign::Pocket] Pocket040
  AddSubType = 1
  AutoTaperInnerAngle = true
  BaseFeature = -> MultiTransform
  CheckUpToFaceLimits = true
  ClaimChildren = false
  Direction = (-1,-1e-16,1e-16)
  Fit = 0
  FitJoin = 0
  FixShape = 1
  InnerFit = 0
  InnerFitJoin = 0
  InvalidShape = false
  Length = 8
  Length2 = 100
  NewSolid = false
  Placement = pos=(0,0,0) rot=(0.57735,0.57735,0.57735;2.0944rad)
  Profile = -> Sketch209
  Refine = true
  Suppress = false
  TaperInnerAngle = 0
  TaperInnerAngleRev = 0
  TreeRank = 0
  Type = 0
  ValidateShape = true
  _ProfileBasedVersion = 0
  _Version = 0
FEATURE [PartDesign::MultiTransform] MultiTransform001
  AddSubType = 0
  BaseFeature = -> Pocket040
  CopyShape = true
  FixShape = 1
  InvalidShape = false
  NewSolid = false
  OriginalSubs = -> [Pocket040]
  Originals = -> [Pocket040]
  ParallelTransform = true
  Placement = pos=(0,0,0) rot=(0.57735,0.57735,0.57735;2.0944rad)
  Refine = true
  SubTransform = true
  Suppress = false
  Transformations = -> [PolarPattern002,PolarPattern003]
  TreeRank = 0
  ValidateShape = true
  _Version = 0
FEATURE [PartDesign::Body] Body001  label="Corner"
  AutoGroupSolids = false
  ClaimAllChildren = false
  ExportMode = 0
  FixShape = 1
  Group = -> [Sketch207,Pad084,Sketch208,Pocket039,MultiTransform,PolarPattern,PolarPattern001,DatumPlane,Sketch209,Pocket040,MultiTransform001,PolarPattern002,PolarPattern003]
  InvalidShape = false
  Origin = -> Origin001
  SingleSolid = true
  Tip = -> MultiTransform001
  TreeRank = 0
  ValidateShape = false
  _ExportChildren = -> [Pad084,Pocket039,MultiTransform,DatumPlane,Pocket040,MultiTransform001]
  _GroupVersion = 1
FEATURE [Image::ImagePlane] ImagePlane
  Placement = pos=(6.5,8e-15,18) rot=(1,0,0;1.5708rad)
  TreeRank = 0
  XSize = 78.8003
  YSize = 45.6564
FEATURE [Sketcher::SketchObject] Sketch189
  ArcFitTolerance = 0
  ExternalBSplineMaxDegree = 0
  ExternalBSplineTolerance = 0
  FixShape = 1
  FullyConstrained = true
  InternalTolerance = 1e-06
  InvalidShape = false
  MakeInternals = false
  MapMode = 5
  TreeRank = 0
  ValidateShape = false
  sketch-geometry (10):
    g0: ArcOfCircle CenterX=-14.1 CenterY=14.1 CenterZ=0 NormalX=0 NormalY=0 NormalZ=1 AngleXU=0 Radius=5.195 StartAngle=1.5708 EndAngle=3.14159
    g1: LineSegment StartX=-14.1 StartY=19.295 StartZ=0 EndX=14.1 EndY=19.295 EndZ=0
    g2: ArcOfCircle CenterX=14.1 CenterY=14.1 CenterZ=0 NormalX=0 NormalY=0 NormalZ=1 AngleXU=0 Radius=5.195 StartAngle=6.5809e-12 EndAngle=1.5708
    g3: LineSegment StartX=19.295 StartY=14.1 StartZ=0 EndX=19.295 EndY=-14.1 EndZ=0
    g4: ArcOfCircle CenterX=14.1 CenterY=-14.1 CenterZ=0 NormalX=0 NormalY=0 NormalZ=1 AngleXU=0 Radius=5.195 StartAngle=4.71239 EndAngle=6.28319
    g5: LineSegment StartX=14.1 StartY=-19.295 StartZ=0 EndX=-14.1 EndY=-19.295 EndZ=0
    g6: ArcOfCircle CenterX=-14.1 CenterY=-14.1 CenterZ=0 NormalX=0 NormalY=0 NormalZ=1 AngleXU=0 Radius=5.195 StartAngle=3.14159 EndAngle=4.71239
    g7: LineSegment StartX=-19.295 StartY=-14.1 StartZ=0 EndX=-19.295 EndY=14.1 EndZ=0
    g8: GeomPoint [constr] X=-19.295 Y=19.295 Z=0
    g9: GeomPoint [constr] X=19.295 Y=-19.295 Z=0
  constraints (23):
    c: Tangent(g0,g1) = 1.5708
    c: Tangent(g1,g2) = 1.5708
    c: Tangent(g2,g3) = 1.5708
    c: Tangent(g3,g4) = 1.5708
    c: Tangent(g4,g5) = 1.5708
    c: Tangent(g5,g6) = 1.5708
    c: Tangent(g6,g7) = 1.5708
    c: Tangent(g7,g0) = 1.5708
    c: Horizontal(g1)
    c: Horizontal(g5)
    c: Vertical(g3)
    c: Vertical(g7)
    c: Equal(g0,g2)
    c: Equal(g2,g4)
    c: Equal(g4,g6)
    c: PointOnObject(g8,g1)
    c: PointOnObject(g8,g7)
    c: PointOnObject(g9,g3)
    c: PointOnObject(g9,g5)
    c: Symmetric(g0,g4,g-1)
    c: Equal(g1,g3)
    c: DistanceY(g4,g1) = 38.59
    c: DistanceX(g0,g2) = 28.2
FEATURE [PartDesign::Pad] Pad077
  AddSubType = 0
  AlongSketchNormal = false
  AutoTaperInnerAngle = true
  CheckUpToFaceLimits = true
  ClaimChildren = false
  Direction = (0,0,1)
  Fit = 0
  FitJoin = 0
  FixShape = 1
  InnerFit = 0
  InnerFitJoin = 0
  InvalidShape = false
  Length = 20.7
  Length2 = 100
  NewSolid = false
  Profile = -> Sketch189
  Refine = true
  Suppress = false
  TaperAngle = -2
  TaperInnerAngle = 2
  TaperInnerAngleRev = 0
  TreeRank = 0
  Type = 0
  ValidateShape = true
  _ProfileBasedVersion = 0
FEATURE [Sketcher::SketchObject] Sketch190
  ArcFitTolerance = 0
  AttachmentSupport = -> [Pad077]
  ExternalBSplineMaxDegree = 0
  ExternalBSplineTolerance = 0
  FixShape = 1
  FullyConstrained = true
  InternalTolerance = 1e-06
  InvalidShape = false
  MakeInternals = false
  MapMode = 5
  Placement = pos=(0,0,20.7) rot=(0,0,1;0rad)
  Support = -> [Pad077]
  TreeRank = 0
  ValidateShape = false
  sketch-geometry (1):
    g0: Circle CenterX=0 CenterY=0 CenterZ=0 NormalX=0 NormalY=0 NormalZ=1 AngleXU=0 Radius=17.645
  constraints (2):
    c: Coincident(g0,g-1)
    c: Diameter(g0) = 35.29
FEATURE [PartDesign::Pad] Pad078
  AddSubType = 0
  AlongSketchNormal = false
  AutoTaperInnerAngle = true
  BaseFeature = -> Pad077
  CheckUpToFaceLimits = true
  ClaimChildren = false
  Direction = (0,0,1)
  Fit = 0
  FitJoin = 0
  FixShape = 1
  InnerFit = 0
  InnerFitJoin = 0
  InvalidShape = false
  Length = 12.8
  Length2 = 100
  NewSolid = false
  Profile = -> Sketch190
  Refine = true
  Suppress = false
  TaperAngle = -1.5
  TaperInnerAngle = 1.5
  TaperInnerAngleRev = 0
  TreeRank = 0
  Type = 0
  ValidateShape = true
  _ProfileBasedVersion = 0
FEATURE [Sketcher::SketchObject] Sketch191
  ArcFitTolerance = 0
  AttachmentOffset = pos=(0,0,17) rot=(0,0,1;0rad)
  ExternalBSplineMaxDegree = 0
  ExternalBSplineTolerance = 0
  FixShape = 1
  FullyConstrained = true
  InternalTolerance = 1e-06
  InvalidShape = false
  MakeInternals = false
  MapMode = 5
  Placement = pos=(0,-17,-4e-15) rot=(1,0,0;1.5708rad)
  TreeRank = 0
  ValidateShape = false
  sketch-geometry (5):
    g0: LineSegment StartX=-5 StartY=6.3 StartZ=0 EndX=-5 EndY=1.3 EndZ=0
    g1: LineSegment StartX=-5 StartY=1.3 StartZ=0 EndX=5 EndY=1.3 EndZ=0
    g2: LineSegment StartX=5 StartY=1.3 StartZ=0 EndX=5 EndY=6.3 EndZ=0
    g3: LineSegment StartX=5 StartY=6.3 StartZ=0 EndX=-5 EndY=6.3 EndZ=0
    g4: GeomPoint [constr] X=1.3758e-12 Y=3.8 Z=0
  constraints (13):
    c: Coincident(g0,g1)
    c: Coincident(g1,g2)
    c: Coincident(g2,g3)
    c: Coincident(g3,g0)
    c: Horizontal(g1)
    c: Horizontal(g3)
    c: Vertical(g0)
    c: Vertical(g2)
    c: Symmetric(g1,g0,g4)
    c: PointOnObject(g4,g-2)
    c: DistanceX(g3,g3) = 10
    c: DistanceY(g2,g2) = 5
    c: DistanceY(g-1,g4) = 3.8
FEATURE [PartDesign::Pocket] Pocket061
  AddSubType = 1
  AutoTaperInnerAngle = true
  BaseFeature = -> Pad078
  CheckUpToFaceLimits = true
  ClaimChildren = false
  Direction = (0,1,0)
  Fit = 0
  FitJoin = 0
  FixShape = 1
  InnerFit = 0
  InnerFitJoin = 0
  InvalidShape = false
  Length = 5
  Length2 = 100
  NewSolid = false
  Profile = -> Sketch191
  Refine = true
  Reversed = true
  Suppress = false
  TaperInnerAngle = 0
  TaperInnerAngleRev = 0
  TreeRank = 0
  Type = 1
  ValidateShape = true
  _ProfileBasedVersion = 0
  _Version = 0
FEATURE [Sketcher::SketchObject] Sketch192
  ArcFitTolerance = 0
  AttachmentSupport = -> [Pocket061]
  ExternalBSplineMaxDegree = 0
  ExternalBSplineTolerance = 0
  FixShape = 1
  FullyConstrained = false
  InternalTolerance = 1e-06
  InvalidShape = false
  MakeInternals = false
  MapMode = 5
  Placement = pos=(0,-17,0) rot=(1,0,0;1.5708rad)
  Support = -> [Pocket061]
  TreeRank = 0
  ValidateShape = false
  sketch-geometry (8):
    g0: Circle CenterX=-2.295 CenterY=3.8 CenterZ=0 NormalX=0 NormalY=0 NormalZ=1 AngleXU=0 Radius=0.765
    g1: Circle CenterX=-0.765 CenterY=3.8 CenterZ=0 NormalX=0 NormalY=0 NormalZ=1 AngleXU=0 Radius=0.765
    g2: Circle CenterX=0.765 CenterY=3.8 CenterZ=0 NormalX=0 NormalY=0 NormalZ=1 AngleXU=0 Radius=0.765
    g3: Circle CenterX=2.295 CenterY=3.8 CenterZ=0 NormalX=0 NormalY=0 NormalZ=1 AngleXU=0 Radius=0.765
    g4: LineSegment [constr] StartX=-2.295 StartY=3.8 StartZ=0 EndX=-0.765 EndY=3.8 EndZ=0
    g5: LineSegment [constr] StartX=-0.765 StartY=3.8 StartZ=0 EndX=0.765 EndY=3.8 EndZ=0
    g6: LineSegment [constr] StartX=0.765 StartY=3.8 StartZ=0 EndX=2.295 EndY=3.8 EndZ=0
    g7: GeomPoint [constr] X=1.8986e-12 Y=3.8 Z=0
  constraints (16):
    c: Horizontal(g3,g2)
    c: Symmetric(g1,g2,g-2)
    c: Symmetric(g0,g3,g-2)
    c: Coincident(g4,g0)
    c: Coincident(g4,g1)
    c: Coincident(g5,g1)
    c: Coincident(g5,g2)
    c: Coincident(g6,g2)
    c: Coincident(g6,g3)
    c: Equal(g6,g5)
    c: PointOnObject(g7,g5)
    c: Equal(g0,g1)
    c: Equal(g1,g2)
    c: Equal(g2,g3)
    c: Tangent(g3,g2)
    c: DistanceX(g4,g4) = 1.53
FEATURE [PartDesign::Pad] Pad079
  AddSubType = 0
  AlongSketchNormal = false
  AutoTaperInnerAngle = true
  BaseFeature = -> Pocket061
  CheckUpToFaceLimits = true
  ClaimChildren = false
  Direction = (0,-1,2e-16)
  Fit = 0
  FitJoin = 0
  FixShape = 1
  InnerFit = 0
  InnerFitJoin = 0
  InvalidShape = false
  Length = 10
  Length2 = 100
  NewSolid = false
  Profile = -> Sketch192
  Refine = true
  Suppress = false
  TaperInnerAngle = 0
  TaperInnerAngleRev = 0
  TreeRank = 0
  Type = 0
  ValidateShape = true
  _ProfileBasedVersion = 0
FEATURE [PartDesign::Fillet] Fillet045
  AddSubType = 0
  Base = -> Pad079 [Edge36]
  BaseFeature = -> Pad079
  FixShape = 1
  InvalidShape = false
  NewSolid = false
  Radius = 1
  Refine = true
  SupportTransform = false
  Suppress = false
  TreeRank = 0
  UseAllEdges = false
  ValidateShape = true
FEATURE [PartDesign::Fillet] Fillet046
  AddSubType = 0
  Base = -> Fillet045 [Edge13]
  BaseFeature = -> Fillet045
  FixShape = 1
  InvalidShape = false
  NewSolid = false
  Radius = 1
  Refine = true
  SupportTransform = false
  Suppress = false
  TreeRank = 0
  UseAllEdges = false
  ValidateShape = true
FEATURE [Sketcher::SketchObject] Sketch193
  ArcFitTolerance = 0
  AttachmentSupport = -> [Fillet046]
  ExternalBSplineMaxDegree = 0
  ExternalBSplineTolerance = 0
  FixShape = 1
  FullyConstrained = true
  InternalTolerance = 1e-06
  InvalidShape = false
  MakeInternals = false
  MapMode = 5
  Placement = pos=(0,0,33.5) rot=(0,0,1;0rad)
  Support = -> [Fillet046]
  TreeRank = 0
  ValidateShape = false
  sketch-geometry (3):
    g0: LineSegment StartX=13 StartY=-0.866025 StartZ=0 EndX=13 EndY=0.866025 EndZ=0
    g1: LineSegment StartX=13 StartY=0.866025 StartZ=0 EndX=14.5 EndY=-2.501e-11 EndZ=0
    g2: LineSegment StartX=14.5 StartY=-2.501e-11 StartZ=0 EndX=13 EndY=-0.866025 EndZ=0
  constraints (9):
    c: Vertical(g0)
    c: Coincident(g0,g1)
    c: PointOnObject(g1,g-1)
    c: Coincident(g1,g2)
    c: Coincident(g2,g0)
    c: Equal(g2,g1)
    c: Equal(g1,g0)
    c: DistanceX(g-1,g0) = 13
    c: DistanceX(g0,g1) = 1.5
FEATURE [PartDesign::Pocket] Pocket062
  AddSubType = 1
  AutoTaperInnerAngle = true
  BaseFeature = -> Fillet046
  CheckUpToFaceLimits = true
  ClaimChildren = false
  Direction = (0,0,-1)
  Fit = 0
  FitJoin = 0
  FixShape = 1
  InnerFit = 0
  InnerFitJoin = 0
  InvalidShape = false
  Length = 1
  Length2 = 100
  NewSolid = false
  Profile = -> Sketch193
  Refine = true
  Suppress = false
  TaperInnerAngle = 0
  TaperInnerAngleRev = 0
  TreeRank = 0
  Type = 0
  ValidateShape = true
  _ProfileBasedVersion = 0
  _Version = 0
FEATURE [Sketcher::SketchObject] Sketch194
  ArcFitTolerance = 0
  AttachmentSupport = -> [Pocket062]
  ExternalBSplineMaxDegree = 0
  ExternalBSplineTolerance = 0
  FixShape = 1
  FullyConstrained = true
  InternalTolerance = 1e-06
  InvalidShape = false
  MakeInternals = false
  MapMode = 5
  Placement = pos=(0,0,0) rot=(0,0,1;3.14159rad)
  Support = -> [Pocket062]
  TreeRank = 0
  ValidateShape = false
  sketch-geometry (4):
    g0: Circle [constr] CenterX=-14.1 CenterY=14.1 CenterZ=0 NormalX=0 NormalY=0 NormalZ=1 AngleXU=0 Radius=2.4
    g1: Circle [constr] CenterX=14.1 CenterY=-14.1 CenterZ=0 NormalX=0 NormalY=0 NormalZ=1 AngleXU=0 Radius=2.4
    g2: Circle CenterX=-14.1 CenterY=14.1 CenterZ=0 NormalX=0 NormalY=0 NormalZ=1 AngleXU=0 Radius=1.225
    g3: Circle CenterX=14.1 CenterY=-14.1 CenterZ=0 NormalX=0 NormalY=0 NormalZ=1 AngleXU=0 Radius=1.225
  constraints (9):
    c: Symmetric(g0,g1,g-1)
    c: Equal(g0,g1)
    c: Diameter(g0) = 4.8
    c: DistanceX(g0,g-1) = 14.1
    c: DistanceY(g-1,g0) = 14.1
    c: Coincident(g2,g0)
    c: Coincident(g3,g1)
    c: Equal(g3,g2)
    c: Diameter(g3) = 2.45
FEATURE [Sketcher::SketchObject] Sketch195
  ArcFitTolerance = 0
  AttachmentOffset = pos=(0,0,21.7) rot=(0,0,1;0rad)
  ExternalBSplineMaxDegree = 0
  ExternalBSplineTolerance = 0
  FixShape = 1
  FullyConstrained = true
  InternalTolerance = 1e-06
  InvalidShape = false
  MakeInternals = false
  MapMode = 5
  Placement = pos=(0,0,21.7) rot=(0,0,1;0rad)
  TreeRank = 0
  ValidateShape = false
  sketch-geometry (2):
    g0: Circle CenterX=0 CenterY=0 CenterZ=0 NormalX=0 NormalY=0 NormalZ=1 AngleXU=0 Radius=20
    g1: Circle CenterX=0 CenterY=0 CenterZ=0 NormalX=0 NormalY=0 NormalZ=1 AngleXU=0 Radius=500
  constraints (4):
    c: Coincident(g0,g-1)
    c: Coincident(g1,g0)
    c: Diameter(g1) = 1000
    c: Diameter(g0) = 40
FEATURE [PartDesign::Pad] Pad013
  AddSubType = 0
  AlongSketchNormal = false
  AutoTaperInnerAngle = true
  CheckUpToFaceLimits = true
  ClaimChildren = false
  Direction = (0,0,1)
  Fit = 0
  FitJoin = 0
  FixShape = 1
  InnerFit = 0
  InnerFitJoin = 0
  InvalidShape = false
  Length = 10
  Length2 = 100
  NewSolid = false
  Placement = pos=(0,0,21.7) rot=(0,0,1;0rad)
  Profile = -> Sketch195
  Refine = true
  Suppress = false
  TaperInnerAngle = 0
  TaperInnerAngleRev = 0
  TreeRank = 0
  Type = 0
  ValidateShape = true
  _ProfileBasedVersion = 0
FEATURE [PartDesign::Body] Body091  label="OpticalWindow"
  AutoGroupSolids = false
  ClaimAllChildren = false
  ExportMode = 0
  FixShape = 1
  Group = -> [Sketch195,Pad013]
  InvalidShape = false
  Origin = -> Origin182
  SingleSolid = true
  Tip = -> Pad013
  TreeRank = 0
  ValidateShape = false
  _ExportChildren = -> [Pad013]
  _GroupVersion = 1
FEATURE [Sketcher::SketchObject] Sketch086
  ArcFitTolerance = 0
  ExternalBSplineMaxDegree = 0
  ExternalBSplineTolerance = 0
  FixShape = 1
  FullyConstrained = true
  InternalTolerance = 1e-06
  InvalidShape = false
  MakeInternals = false
  MapMode = 5
  Placement = pos=(0,0,0) rot=(1,0,0;1.5708rad)
  TreeRank = 0
  ValidateShape = false
  sketch-geometry (12):
    g0: LineSegment StartX=-37 StartY=-18.5 StartZ=0 EndX=-37 EndY=-16 EndZ=0
    g1: LineSegment StartX=-37 StartY=-16 StartZ=0 EndX=-30 EndY=-16 EndZ=0
    g2: LineSegment StartX=-30 StartY=-16 StartZ=0 EndX=-30 EndY=-8 EndZ=0
    g3: LineSegment StartX=-30 StartY=-8 StartZ=0 EndX=10 EndY=-8 EndZ=0
    g4: LineSegment StartX=10 StartY=-8 StartZ=0 EndX=10 EndY=-16 EndZ=0
    g5: LineSegment StartX=10 StartY=-16 StartZ=0 EndX=17 EndY=-16 EndZ=0
    g6: LineSegment StartX=17 StartY=-16 StartZ=0 EndX=17 EndY=-18.5 EndZ=0
    g7: LineSegment StartX=17 StartY=-18.5 StartZ=0 EndX=10 EndY=-18.5 EndZ=0
    g8: LineSegment StartX=10 StartY=-18.5 StartZ=0 EndX=10 EndY=-47 EndZ=0
    g9: LineSegment StartX=10 StartY=-47 StartZ=0 EndX=-30 EndY=-47 EndZ=0
    g10: LineSegment StartX=-30 StartY=-47 StartZ=0 EndX=-30 EndY=-18.5 EndZ=0
    g11: LineSegment StartX=-30 StartY=-18.5 StartZ=0 EndX=-37 EndY=-18.5 EndZ=0
  constraints (33):
    c: Vertical(g0)
    c: Coincident(g0,g1)
    c: Horizontal(g1)
    c: Coincident(g1,g2)
    c: Vertical(g2)
    c: Coincident(g2,g3)
    c: Horizontal(g3)
    c: Coincident(g3,g4)
    c: Coincident(g4,g5)
    c: Coincident(g5,g6)
    c: Vertical(g6)
    c: Coincident(g6,g7)
    c: Horizontal(g7)
    c: Coincident(g7,g8)
    c: Vertical(g8)
    c: Coincident(g8,g9)
    c: Horizontal(g9)
    c: Coincident(g9,g10)
    c: Coincident(g10,g11)
    c: Coincident(g11,g0)
    c: Horizontal(g11)
    c: Tangent(g4,g8) = -1.5708
    c: Tangent(g10,g2)
    c: Equal(g1,g5)
    c: Tangent(g1,g5)
    c: Equal(g6,g0)
    c: DistanceX(g-1,g3) = 10
    c: DistanceX(g0,g5) = 54
    c: DistanceX(g10,g7) = 40
    c: DistanceY(g9,g-1) = 47
    c: DistanceY(g3,g-1) = 8
    c: DistanceY(g6,g6) = 2.5
    c: DistanceY(g0,g-1) = 18.5
FEATURE [PartDesign::Pad] Pad050
  AddSubType = 0
  AutoTaperInnerAngle = true
  CheckUpToFaceLimits = true
  ClaimChildren = false
  Direction = (0,-1,0)
  Fit = 0
  FitJoin = 0
  FixShape = 1
  InnerFit = 0
  InnerFitJoin = 0
  InvalidShape = false
  Length = 20
  Length2 = 100
  Midplane = true
  NewSolid = false
  Placement = pos=(0,0,0) rot=(1,0,0;1.5708rad)
  Profile = -> Sketch086
  Refine = true
  Suppress = false
  TaperInnerAngle = 0
  TaperInnerAngleRev = 0
  TreeRank = 0
  Type = 0
  ValidateShape = true
  _ProfileBasedVersion = 0
FEATURE [Sketcher::SketchObject] Sketch087
  ArcFitTolerance = 0
  ExternalBSplineMaxDegree = 0
  ExternalBSplineTolerance = 0
  FixShape = 1
  FullyConstrained = true
  InternalTolerance = 1e-06
  InvalidShape = false
  MakeInternals = false
  MapMode = 5
  TreeRank = 0
  ValidateShape = false
  sketch-geometry (4):
    g0: Circle CenterX=14.5 CenterY=5 CenterZ=0 NormalX=0 NormalY=0 NormalZ=1 AngleXU=0 Radius=2
    g1: Circle CenterX=14.5 CenterY=-5 CenterZ=0 NormalX=0 NormalY=0 NormalZ=1 AngleXU=0 Radius=2
    g2: Circle CenterX=-34.5 CenterY=5 CenterZ=0 NormalX=0 NormalY=0 NormalZ=1 AngleXU=0 Radius=2
    g3: Circle CenterX=-34.5 CenterY=-5 CenterZ=0 NormalX=0 NormalY=0 NormalZ=1 AngleXU=0 Radius=2
  constraints (10):
    c: Equal(g2,g3)
    c: Equal(g3,g1)
    c: Equal(g1,g0)
    c: Symmetric(g0,g1,g-1)
    c: Symmetric(g2,g3,g-1)
    c: Horizontal(g2,g0)
    c: Diameter(g0) = 4
    c: DistanceY(g1,g0) = 10
    c: DistanceX(g2,g0) = 49
    c: DistanceX(g-1,g0) = 14.5
FEATURE [PartDesign::Pocket] Pocket033
  AddSubType = 1
  AutoTaperInnerAngle = true
  BaseFeature = -> Pad050
  CheckUpToFaceLimits = true
  ClaimChildren = false
  Direction = (0,0,-1)
  Fit = 0
  FitJoin = 0
  FixShape = 1
  InnerFit = 0
  InnerFitJoin = 0
  InvalidShape = false
  Length = 5
  Length2 = 100
  NewSolid = false
  Placement = pos=(0,0,0) rot=(1,0,0;1.5708rad)
  Profile = -> Sketch087
  Refine = true
  Suppress = false
  TaperInnerAngle = 0
  TaperInnerAngleRev = 0
  TreeRank = 0
  Type = 1
  ValidateShape = true
  _ProfileBasedVersion = 0
  _Version = 0
FEATURE [PartDesign::Fillet] Fillet024
  AddSubType = 0
  Base = -> Pocket033 [Edge28,Edge19,Edge4,Edge3]
  BaseFeature = -> Pocket033
  FixShape = 1
  InvalidShape = false
  NewSolid = false
  Placement = pos=(0,0,0) rot=(1,0,0;1.5708rad)
  Radius = 1
  Refine = true
  SupportTransform = false
  Suppress = false
  TreeRank = 0
  UseAllEdges = false
  ValidateShape = true
FEATURE [Sketcher::SketchObject] Sketch090
  ArcFitTolerance = 0
  AttachmentOffset = pos=(0,0,-2) rot=(0,0,1;0rad)
  ExternalBSplineMaxDegree = 0
  ExternalBSplineTolerance = 0
  FixShape = 1
  FullyConstrained = true
  InternalTolerance = 1e-06
  InvalidShape = false
  MakeInternals = false
  MapMode = 5
  Placement = pos=(0,0,-2) rot=(0,0,1;0rad)
  TreeRank = 0
  ValidateShape = false
  sketch-geometry (1):
    g0: Circle CenterX=0 CenterY=0 CenterZ=0 NormalX=0 NormalY=0 NormalZ=1 AngleXU=0 Radius=3
  constraints (2):
    c: Coincident(g0,g-1)
    c: Diameter(g0) = 6
FEATURE [PartDesign::Pad] Pad053
  AddSubType = 0
  AutoTaperInnerAngle = true
  CheckUpToFaceLimits = true
  ClaimChildren = false
  Direction = (0,0,1)
  Fit = 0
  FitJoin = 0
  FixShape = 1
  InnerFit = 0
  InnerFitJoin = 0
  InvalidShape = false
  Length = 10
  Length2 = 100
  NewSolid = false
  Placement = pos=(0,0,-2) rot=(0,0,1;0rad)
  Profile = -> Sketch090
  Refine = true
  Reversed = true
  Suppress = false
  TaperInnerAngle = 0
  TaperInnerAngleRev = 0
  TreeRank = 0
  Type = 0
  ValidateShape = true
  _ProfileBasedVersion = 0
FEATURE [PartDesign::Chamfer] Chamfer029
  AddSubType = 0
  Angle = 45
  Base = -> Pad053 [Edge2]
  BaseFeature = -> Pad053
  ChamferType = 0
  FixShape = 1
  FlipDirection = false
  InvalidShape = false
  NewSolid = false
  Placement = pos=(0,0,-2) rot=(0,0,1;0rad)
  Refine = true
  Size = 0.5
  Size2 = 1
  SupportTransform = false
  Suppress = false
  TreeRank = 0
  UseAllEdges = false
  ValidateShape = true
FEATURE [PartDesign::Body] Body043  label="ServoAxis001"
  AutoGroupSolids = false
  ClaimAllChildren = false
  ExportMode = 0
  FixShape = 1
  Group = -> [Sketch090,Pad053,Chamfer029]
  InvalidShape = false
  Origin = -> Origin064
  SingleSolid = true
  Tip = -> Chamfer029
  TreeRank = 0
  ValidateShape = false
  _ExportChildren = -> [Pad053,Chamfer029]
  _GroupVersion = 1
FEATURE [Sketcher::SketchObject] Sketch162
  ArcFitTolerance = 0
  ExternalBSplineMaxDegree = 0
  ExternalBSplineTolerance = 0
  FixShape = 1
  FullyConstrained = true
  InternalTolerance = 1e-06
  InvalidShape = false
  MakeInternals = false
  MapMode = 5
  TreeRank = 0
  ValidateShape = false
  sketch-geometry (12):
    g0: LineSegment StartX=-17 StartY=2.106e-12 StartZ=0 EndX=-21.7 EndY=5.127e-13 EndZ=0
    g1: LineSegment StartX=-21.7 StartY=5.127e-13 StartZ=0 EndX=-21.7 EndY=-2.4 EndZ=0
    g2: LineSegment StartX=-21.7 StartY=-2.4 StartZ=0 EndX=-17 EndY=-2.4 EndZ=0
    g3: LineSegment StartX=-17 StartY=-2.4 StartZ=0 EndX=-17 EndY=-6.8 EndZ=0
    g4: LineSegment StartX=-17 StartY=-6.8 StartZ=0 EndX=6 EndY=-6.8 EndZ=0
    g5: LineSegment StartX=6 StartY=-6.8 StartZ=0 EndX=6 EndY=-2.4 EndZ=0
    g6: LineSegment StartX=6 StartY=-2.4 StartZ=0 EndX=10.7 EndY=-2.4 EndZ=0
    g7: LineSegment StartX=10.7 StartY=-2.4 StartZ=0 EndX=10.7 EndY=1.124e-12 EndZ=0
    g8: LineSegment StartX=10.7 StartY=1.1239e-12 StartZ=0 EndX=6 EndY=-1.9734e-12 EndZ=0
    g9: LineSegment StartX=6 StartY=-1.9734e-12 StartZ=0 EndX=6 EndY=15.8 EndZ=0
    g10: LineSegment StartX=6 StartY=15.8 StartZ=0 EndX=-17 EndY=15.8 EndZ=0
    g11: LineSegment StartX=-17 StartY=15.8 StartZ=0 EndX=-17 EndY=2.1068e-12 EndZ=0
  constraints (36):
    c: PointOnObject(g0,g-1)
    c: PointOnObject(g0,g-1)
    c: Coincident(g0,g1)
    c: Vertical(g1)
    c: Coincident(g1,g2)
    c: Horizontal(g2)
    c: Coincident(g2,g3)
    c: Vertical(g3)
    c: Coincident(g3,g4)
    c: Horizontal(g4)
    c: Coincident(g4,g5)
    c: Vertical(g5)
    c: Coincident(g5,g6)
    c: Horizontal(g6)
    c: Coincident(g6,g7)
    c: PointOnObject(g7,g-1)
    c: Vertical(g7)
    c: Coincident(g7,g8)
    c: PointOnObject(g8,g-1)
    c: Coincident(g8,g9)
    c: Vertical(g9)
    c: Coincident(g9,g10)
    c: Horizontal(g10)
    c: Coincident(g10,g11)
    c: Coincident(g11,g0)
    c: Vertical(g11)
    c: Equal(g0,g2)
    c: Equal(g2,g6)
    c: Equal(g6,g8)
    c: DistanceX(g4) = 6
    c: DistanceX(g4,g4) = 23
    c: DistanceX(g1,g6) = 32.4
    c: DistanceY(g3,g3) = 4.4
    c: DistanceY(g1,g1) = 2.4
    c: Equal(g7,g1)
    c: DistanceY(g9,g9) = 15.8
FEATURE [PartDesign::Pad] Pad068
  AddSubType = 0
  AlongSketchNormal = false
  AutoTaperInnerAngle = true
  CheckUpToFaceLimits = true
  ClaimChildren = false
  Direction = (0,0,1)
  Fit = 0
  FitJoin = 0
  FixShape = 1
  InnerFit = 0
  InnerFitJoin = 0
  InvalidShape = false
  Length = 12
  Length2 = 100
  Midplane = true
  NewSolid = false
  Profile = -> Sketch162
  Refine = true
  Suppress = false
  TaperInnerAngle = 0
  TaperInnerAngleRev = 0
  TreeRank = 0
  Type = 0
  ValidateShape = true
  _ProfileBasedVersion = 0
FEATURE [Sketcher::SketchObject] Sketch163
  ArcFitTolerance = 0
  AttachmentSupport = -> [Pad068]
  ExternalBSplineMaxDegree = 0
  ExternalBSplineTolerance = 0
  FixShape = 1
  FullyConstrained = true
  InternalTolerance = 1e-06
  InvalidShape = false
  MakeInternals = false
  MapMode = 5
  Placement = pos=(0,-6.8,0) rot=(1,0,0;1.5708rad)
  Support = -> [Pad068]
  TreeRank = 0
  ValidateShape = false
  sketch-geometry (4):
    g0: ArcOfCircle CenterX=-5.554e-13 CenterY=-7.838e-13 CenterZ=0 NormalX=0 NormalY=0 NormalZ=1 AngleXU=0 Radius=6 StartAngle=3.57137 EndAngle=8.995
    g1: ArcOfCircle CenterX=-6 CenterY=4.736e-13 CenterZ=0 NormalX=0 NormalY=0 NormalZ=1 AngleXU=0 Radius=2.5 StartAngle=1.5708 EndAngle=4.71239
    g2: LineSegment StartX=-6 StartY=2.5 StartZ=0 EndX=-5.45436 EndY=2.5 EndZ=0
    g3: LineSegment StartX=-6 StartY=-2.5 StartZ=0 EndX=-5.45436 EndY=-2.5 EndZ=0
  constraints (11):
    c: Coincident(g0,g-1)
    c: PointOnObject(g1,g-1)
    c: Coincident(g2,g0)
    c: Coincident(g3,g0)
    c: Horizontal(g3)
    c: Horizontal(g2)
    c: Tangent(g2,g1) = 1.5708
    c: Tangent(g3,g1) = -1.5708
    c: Radius(g0) = 6
    c: DistanceY(g1,g1) = 5
    c: DistanceX(g1,g0) = 6
FEATURE [PartDesign::Pad] Pad069
  AddSubType = 0
  AlongSketchNormal = false
  AutoTaperInnerAngle = true
  BaseFeature = -> Pad068
  CheckUpToFaceLimits = true
  ClaimChildren = false
  Direction = (0,-1,2e-16)
  Fit = 0
  FitJoin = 0
  FixShape = 1
  InnerFit = 0
  InnerFitJoin = 0
  InvalidShape = false
  Length = 4
  Length2 = 100
  NewSolid = false
  Profile = -> Sketch163
  Refine = true
  Suppress = false
  TaperInnerAngle = 0
  TaperInnerAngleRev = 0
  TreeRank = 0
  Type = 0
  ValidateShape = true
  _ProfileBasedVersion = 0
FEATURE [Sketcher::SketchObject] Sketch164
  ArcFitTolerance = 0
  ExternalBSplineMaxDegree = 0
  ExternalBSplineTolerance = 0
  ExternalGeometry = -> [Pad069]
  FixShape = 1
  FullyConstrained = true
  InternalTolerance = 1e-06
  InvalidShape = false
  MakeInternals = false
  MapMode = 5
  Placement = pos=(0,0,0) rot=(1,0,0;1.5708rad)
  TreeRank = 0
  ValidateShape = false
  sketch-geometry (4):
    g0: Circle CenterX=-19.25 CenterY=-8.88e-14 CenterZ=0 NormalX=0 NormalY=0 NormalZ=1 AngleXU=0 Radius=1
    g1: Circle CenterX=8.25 CenterY=8.765e-12 CenterZ=0 NormalX=0 NormalY=0 NormalZ=1 AngleXU=0 Radius=1
    g2: LineSegment [constr] StartX=-21.7 StartY=-6 StartZ=0 EndX=10.7 EndY=6 EndZ=0
    g3: GeomPoint [constr] X=-5.5 Y=5.2304e-12 Z=0
  constraints (8):
    c: PointOnObject(g0,g-1)
    c: DistanceX(g0,g1) = 27.5
    c: Equal(g0,g1)
    c: Diameter(g0) = 2
    c: Coincident(g2,g-3)
    c: Coincident(g2,g-4)
    c: Symmetric(g-4,g-3,g3)
    c: Symmetric(g0,g1,g3)
FEATURE [PartDesign::Pocket] Pocket052
  AddSubType = 1
  AutoTaperInnerAngle = true
  BaseFeature = -> Pad069
  CheckUpToFaceLimits = true
  ClaimChildren = false
  Direction = (0,1,0)
  Fit = 0
  FitJoin = 0
  FixShape = 1
  InnerFit = 0
  InnerFitJoin = 0
  InvalidShape = false
  Length = 5
  Length2 = 100
  NewSolid = false
  Profile = -> Sketch164
  Refine = true
  Reversed = true
  Suppress = false
  TaperInnerAngle = 0
  TaperInnerAngleRev = 0
  TreeRank = 0
  Type = 1
  ValidateShape = true
  _ProfileBasedVersion = 0
  _Version = 0
FEATURE [PartDesign::Body] Body076  label="BodyServo90S"
  AutoGroupSolids = false
  ClaimAllChildren = false
  ExportMode = 0
  FixShape = 1
  Group = -> [Sketch162,Pad068,Sketch163,Pad069,Sketch164,Pocket052]
  InvalidShape = false
  Origin = -> Origin195
  SingleSolid = true
  Tip = -> Pocket052
  TreeRank = 0
  ValidateShape = false
  _ExportChildren = -> [Pad068,Pad069,Pocket052]
  _GroupVersion = 1
FEATURE [Sketcher::SketchObject] Sketch165
  ArcFitTolerance = 0
  ExternalBSplineMaxDegree = 0
  ExternalBSplineTolerance = 0
  FixShape = 1
  FullyConstrained = true
  InternalTolerance = 1e-06
  InvalidShape = false
  MakeInternals = false
  MapMode = 5
  Placement = pos=(0,-10.8,2e-15) rot=(1,0,0;1.5708rad)
  TreeRank = 0
  ValidateShape = false
  sketch-geometry (1):
    g0: Circle CenterX=0 CenterY=0 CenterZ=0 NormalX=0 NormalY=0 NormalZ=1 AngleXU=0 Radius=2.25
  constraints (2):
    c: Coincident(g0,g-1)
    c: Diameter(g0) = 4.5
FEATURE [PartDesign::Pad] Pad070
  AddSubType = 0
  AlongSketchNormal = false
  AutoTaperInnerAngle = true
  CheckUpToFaceLimits = true
  ClaimChildren = false
  Direction = (0,-1,0)
  Fit = 0
  FitJoin = 0
  FixShape = 1
  InnerFit = 0
  InnerFitJoin = 0
  InvalidShape = false
  Length = 2.4
  Length2 = 100
  NewSolid = false
  Placement = pos=(0,-10.8,2e-15) rot=(1,0,0;1.5708rad)
  Profile = -> Sketch165
  Refine = true
  Suppress = false
  TaperInnerAngle = 0
  TaperInnerAngleRev = 0
  TreeRank = 0
  Type = 0
  ValidateShape = true
  _ProfileBasedVersion = 0
FEATURE [PartDesign::Body] Body077  label="AxleServo90S"
  AutoGroupSolids = false
  ClaimAllChildren = false
  ExportMode = 0
  FixShape = 1
  Group = -> [Sketch165,Pad070]
  InvalidShape = false
  Origin = -> Origin197
  SingleSolid = true
  Tip = -> Pad070
  TreeRank = 0
  ValidateShape = false
  _ExportChildren = -> [Pad070]
  _GroupVersion = 1
FEATURE [Sketcher::SketchObject] Sketch166
  ArcFitTolerance = 0
  AttachmentSupport = -> [Pocket052]
  ExternalBSplineMaxDegree = 0
  ExternalBSplineTolerance = 0
  FixShape = 1
  FullyConstrained = true
  InternalTolerance = 1e-06
  InvalidShape = false
  MakeInternals = false
  MapMode = 5
  Placement = pos=(6,0,0) rot=(0.57735,0.57735,0.57735;2.0944rad)
  Support = -> [Pocket052]
  TreeRank = 0
  ValidateShape = false
  sketch-geometry (3):
    g0: Circle CenterX=10 CenterY=-9.4173e-12 CenterZ=0 NormalX=0 NormalY=0 NormalZ=1 AngleXU=0 Radius=0.5
    g1: Circle CenterX=10 CenterY=1 CenterZ=0 NormalX=0 NormalY=0 NormalZ=1 AngleXU=0 Radius=0.5
    g2: Circle CenterX=10 CenterY=-1 CenterZ=0 NormalX=0 NormalY=0 NormalZ=1 AngleXU=0 Radius=0.5
  constraints (9):
    c: PointOnObject(g0,g-1)
    c: Tangent(g1,g0)
    c: Tangent(g2,g0)
    c: Vertical(g2,g0)
    c: Vertical(g0,g1)
    c: Equal(g1,g0)
    c: Equal(g1,g2)
    c: Diameter(g1) = 1
    c: DistanceX(g0) = 10
FEATURE [PartDesign::Pad] Pad071
  AddSubType = 0
  AlongSketchNormal = false
  AutoTaperInnerAngle = true
  CheckUpToFaceLimits = true
  ClaimChildren = false
  Direction = (1,0,0)
  Fit = 0
  FitJoin = 0
  FixShape = 1
  InnerFit = 0
  InnerFitJoin = 0
  InvalidShape = false
  Length = 10
  Length2 = 100
  NewSolid = false
  Profile = -> Sketch166
  Refine = true
  Suppress = false
  TaperInnerAngle = 0
  TaperInnerAngleRev = 0
  TreeRank = 0
  Type = 0
  ValidateShape = true
  _ProfileBasedVersion = 0
FEATURE [PartDesign::Body] Body078  label="Cables001"
  AutoGroupSolids = false
  ClaimAllChildren = false
  ExportMode = 0
  FixShape = 1
  Group = -> [Sketch166,Pad071]
  InvalidShape = false
  Origin = -> Origin163
  SingleSolid = true
  Tip = -> Pad071
  TreeRank = 0
  ValidateShape = false
  _ExportChildren = -> [Pad071]
  _GroupVersion = 1
FEATURE [App::Part] Part044  label="MG-SG90"
  ClaimAllChildren = false
  ExportMode = 1
  Group = -> [Body076,Body077,Body078]
  Origin = -> Origin196
  TreeRank = 0
  _ExportChildren = -> [Body076,Body077,Body078]
  _GroupVersion = 1
FEATURE [Sketcher::SketchObject] Sketch123
  ArcFitTolerance = 0
  ExternalBSplineMaxDegree = 0
  ExternalBSplineTolerance = 0
  FixShape = 1
  FullyConstrained = false
  InternalTolerance = 1e-06
  InvalidShape = false
  MakeInternals = false
  MapMode = 5
  Placement = pos=(0,0,0) rot=(1,0,0;1.5708rad)
  TreeRank = 0
  ValidateShape = false
  sketch-geometry (17):
    g0: ArcOfCircle CenterX=0 CenterY=0 CenterZ=0 NormalX=0 NormalY=0 NormalZ=1 AngleXU=0 Radius=8 StartAngle=5.67415 EndAngle=10.0338
    g1: ArcOfCircle CenterX=4.3e-15 CenterY=1 CenterZ=0 NormalX=0 NormalY=0 NormalZ=1 AngleXU=0 Radius=26 StartAngle=4.4405 EndAngle=4.98428
    g2: ArcOfCircle CenterX=6.42511 CenterY=-22.0462 CenterZ=0 NormalX=0 NormalY=0 NormalZ=1 AngleXU=0 Radius=2.07489 StartAngle=4.98428 EndAngle=6.60035
    g3: ArcOfCircle CenterX=-6.42511 CenterY=-22.0462 CenterZ=0 NormalX=0 NormalY=0 NormalZ=1 AngleXU=0 Radius=2.07489 StartAngle=2.82443 EndAngle=4.4405
    g4: LineSegment [constr] StartX=8.5 StartY=0 StartZ=0 EndX=8.5 EndY=-36.4357 EndZ=0
    g5: GeomPoint [constr] X=0 Y=-25 Z=0
    g6: GeomPoint [constr] X=0 Y=8 Z=0
    g7: Circle CenterX=-5.5 CenterY=-21 CenterZ=0 NormalX=0 NormalY=0 NormalZ=1 AngleXU=0 Radius=1.5
    g8: Circle CenterX=0 CenterY=-21 CenterZ=0 NormalX=0 NormalY=0 NormalZ=1 AngleXU=0 Radius=1.5
    g9: Circle CenterX=5.5 CenterY=-21 CenterZ=0 NormalX=0 NormalY=0 NormalZ=1 AngleXU=0 Radius=1.5
    g10: Circle CenterX=-4 CenterY=-17 CenterZ=0 NormalX=0 NormalY=0 NormalZ=1 AngleXU=0 Radius=1.5
    g11: Circle CenterX=4 CenterY=-17 CenterZ=0 NormalX=0 NormalY=0 NormalZ=1 AngleXU=0 Radius=1.5
    g12: LineSegment StartX=8.39651 StartY=-21.3991 StartZ=0 EndX=5.42127 EndY=-12.335 EndZ=0
    g13: LineSegment StartX=-8.39651 StartY=-21.3991 StartZ=0 EndX=-5.42127 EndY=-12.335 EndZ=0
    g14: ArcOfCircle CenterX=-13.7605 CenterY=-9.59771 CenterZ=0 NormalX=0 NormalY=0 NormalZ=1 AngleXU=0 Radius=8.777 StartAngle=5.96602 EndAngle=6.89222
    g15: ArcOfCircle CenterX=13.7605 CenterY=-9.59771 CenterZ=0 NormalX=0 NormalY=0 NormalZ=1 AngleXU=0 Radius=8.777 StartAngle=2.53256 EndAngle=3.45876
    g16: LineSegment [constr] StartX=-5 StartY=-9.06 StartZ=0 EndX=5 EndY=-9.06 EndZ=0
  constraints (43):
    c: Coincident(g0,g-1)
    c: Diameter(g0) = 16
    c: Symmetric(g1,g1,g-2)
    c: Tangent(g3,g1) = -1.5708
    c: Tangent(g2,g1) = -1.5708
    c: Symmetric(g3,g2,g-2)
    c: PointOnObject(g4,g-1)
    c: Vertical(g4)
    c: Tangent(g2,g4)
    c: DistanceX(g4) = 8.5
    c: PointOnObject(g5,g1)
    c: PointOnObject(g6,g0)
    c: PointOnObject(g6,g-2)
    c: PointOnObject(g5,g-2)
    c: DistanceY(g5,g6) = 33
    c: PointOnObject(g8,g-2)
    c: Horizontal(g7,g8)
    c: Symmetric(g10,g11,g-2)
    c: Symmetric(g7,g9,g-2)
    c: DistanceY(g11) = -17
    c: DistanceY(g9) = -21
    c: Diameter(g7) = 3
    c: Equal(g7,g10)
    c: Equal(g7,g8)
    c: Equal(g7,g9)
    c: Equal(g7,g11)
    c: DistanceX(g7,g9) = 11
    c: DistanceX(g10,g11) = 8
    c: Tangent(g13,g3) = 1.5708
    c: Tangent(g12,g2) = -1.5708
    c: Tangent(g15,g12) = 1.5708
    c: Tangent(g15,g0) = 1.5708
    c: PointOnObject(g16,g14)
    c: Horizontal(g16)
    c: PointOnObject(g16,g15)
    c: DistanceX(g16,g16) = 10
    c: Tangent(g14,g13) = -1.5708
    c: Tangent(g14,g0) = 1.5708
    c: Distance(g2,g1) = 3
    c: Diameter(g1) = 52
    c: Equal(g15,g14)
    c: DistanceY(g16,g0) = 9.06
    c: Radius(g15) = 8.777
FEATURE [PartDesign::Pad] Pad066
  AddSubType = 0
  AutoTaperInnerAngle = true
  CheckUpToFaceLimits = true
  ClaimChildren = false
  Direction = (0,-1,0)
  Fit = 0
  FitJoin = 0
  FixShape = 1
  InnerFit = 0
  InnerFitJoin = 0
  InvalidShape = false
  Length = 4
  Length2 = 100
  NewSolid = false
  Placement = pos=(0,0,0) rot=(1,0,0;1.5708rad)
  Profile = -> Sketch123
  Refine = true
  Reversed = true
  Suppress = false
  TaperInnerAngle = 0
  TaperInnerAngleRev = 0
  TreeRank = 0
  Type = 0
  ValidateShape = true
  _ProfileBasedVersion = 0
FEATURE [Sketcher::SketchObject] Sketch124
  ArcFitTolerance = 0
  ExternalBSplineMaxDegree = 0
  ExternalBSplineTolerance = 0
  FixShape = 1
  FullyConstrained = true
  InternalTolerance = 1e-06
  InvalidShape = false
  MakeInternals = false
  MapMode = 5
  Placement = pos=(0,0,0) rot=(1,0,0;1.5708rad)
  TreeRank = 0
  ValidateShape = false
  sketch-geometry (1):
    g0: Circle CenterX=0 CenterY=0 CenterZ=0 NormalX=0 NormalY=0 NormalZ=1 AngleXU=0 Radius=8
  constraints (2):
    c: Coincident(g0,g-1)
    c: Diameter(g0) = 16
FEATURE [PartDesign::Pad] Pad067
  AddSubType = 0
  AutoTaperInnerAngle = true
  BaseFeature = -> Pad066
  CheckUpToFaceLimits = true
  ClaimChildren = false
  Direction = (0,-1,0)
  Fit = 0
  FitJoin = 0
  FixShape = 1
  InnerFit = 0
  InnerFitJoin = 0
  InvalidShape = false
  Length = 10
  Length2 = 100
  NewSolid = false
  Placement = pos=(0,0,0) rot=(1,0,0;1.5708rad)
  Profile = -> Sketch124
  Refine = true
  Reversed = true
  Suppress = false
  TaperInnerAngle = 0
  TaperInnerAngleRev = 0
  TreeRank = 0
  Type = 0
  ValidateShape = true
  _ProfileBasedVersion = 0
FEATURE [Sketcher::SketchObject] Sketch125
  ArcFitTolerance = 0
  ExternalBSplineMaxDegree = 0
  ExternalBSplineTolerance = 0
  FixShape = 1
  FullyConstrained = true
  InternalTolerance = 1e-06
  InvalidShape = false
  MakeInternals = false
  MapMode = 5
  Placement = pos=(0,10,0) rot=(-1,0,0;1.5708rad)
  TreeRank = 0
  ValidateShape = false
  sketch-geometry (1):
    g0: Circle CenterX=0 CenterY=0 CenterZ=0 NormalX=0 NormalY=0 NormalZ=1 AngleXU=0 Radius=3
  constraints (2):
    c: Coincident(g0,g-1)
    c: Diameter(g0) = 6
FEATURE [PartDesign::Pocket] Pocket049
  AddSubType = 1
  AutoTaperInnerAngle = true
  BaseFeature = -> Pad067
  CheckUpToFaceLimits = true
  ClaimChildren = false
  Direction = (0,-1,0)
  Fit = 0
  FitJoin = 0
  FixShape = 1
  InnerFit = 0
  InnerFitJoin = 0
  InvalidShape = false
  Length = 3.2
  Length2 = 100
  NewSolid = false
  Placement = pos=(0,0,0) rot=(1,0,0;1.5708rad)
  Profile = -> Sketch125
  Refine = true
  Suppress = false
  TaperInnerAngle = 0
  TaperInnerAngleRev = 0
  TreeRank = 0
  Type = 0
  ValidateShape = true
  _ProfileBasedVersion = 0
  _Version = 0
FEATURE [Sketcher::SketchObject] Sketch126
  ArcFitTolerance = 0
  ExternalBSplineMaxDegree = 0
  ExternalBSplineTolerance = 0
  FixShape = 1
  FullyConstrained = true
  InternalTolerance = 1e-06
  InvalidShape = false
  MakeInternals = false
  MapMode = 5
  Placement = pos=(0,0,0) rot=(1,0,0;1.5708rad)
  TreeRank = 0
  ValidateShape = false
  sketch-geometry (1):
    g0: Circle CenterX=0 CenterY=0 CenterZ=0 NormalX=0 NormalY=0 NormalZ=1 AngleXU=0 Radius=1.5
  constraints (2):
    c: Coincident(g0,g-1)
    c: Diameter(g0) = 3
FEATURE [PartDesign::Pocket] Pocket050
  AddSubType = 1
  AutoTaperInnerAngle = true
  BaseFeature = -> Pocket049
  CheckUpToFaceLimits = true
  ClaimChildren = false
  Direction = (0,1,0)
  Fit = 0
  FitJoin = 0
  FixShape = 1
  InnerFit = 0
  InnerFitJoin = 0
  InvalidShape = false
  Length = 5
  Length2 = 100
  NewSolid = false
  Placement = pos=(0,0,0) rot=(1,0,0;1.5708rad)
  Profile = -> Sketch126
  Refine = true
  Suppress = false
  TaperInnerAngle = 0
  TaperInnerAngleRev = 0
  TreeRank = 0
  Type = 1
  ValidateShape = true
  _ProfileBasedVersion = 0
  _Version = 0
FEATURE [Sketcher::SketchObject] Sketch127
  ArcFitTolerance = 0
  ExternalBSplineMaxDegree = 0
  ExternalBSplineTolerance = 0
  FixShape = 1
  FullyConstrained = true
  InternalTolerance = 1e-06
  InvalidShape = false
  MakeInternals = false
  MapMode = 5
  Placement = pos=(0,0,0) rot=(1,0,0;1.5708rad)
  TreeRank = 0
  ValidateShape = false
  sketch-geometry (1):
    g0: Circle CenterX=0 CenterY=0 CenterZ=0 NormalX=0 NormalY=0 NormalZ=1 AngleXU=0 Radius=3.75
  constraints (2):
    c: Coincident(g0,g-1)
    c: Diameter(g0) = 7.5
FEATURE [PartDesign::Pocket] Pocket051
  AddSubType = 1
  AutoTaperInnerAngle = true
  BaseFeature = -> Pocket050
  CheckUpToFaceLimits = true
  ClaimChildren = false
  Direction = (0,1,0)
  Fit = 0
  FitJoin = 0
  FixShape = 1
  InnerFit = 0
  InnerFitJoin = 0
  InvalidShape = false
  Length = 4
  Length2 = 100
  NewSolid = false
  Placement = pos=(0,0,0) rot=(1,0,0;1.5708rad)
  Profile = -> Sketch127
  Refine = true
  Suppress = false
  TaperInnerAngle = 0
  TaperInnerAngleRev = 0
  TreeRank = 0
  Type = 0
  ValidateShape = true
  _ProfileBasedVersion = 0
  _Version = 0
FEATURE [PartDesign::Chamfer] Chamfer040
  AddSubType = 0
  Angle = 45
  Base = -> Pocket051 [Edge24,Edge14]
  BaseFeature = -> Pocket051
  ChamferType = 0
  FixShape = 1
  FlipDirection = false
  InvalidShape = false
  NewSolid = false
  Placement = pos=(0,0,0) rot=(1,0,0;1.5708rad)
  Refine = true
  Size = 0.2
  Size2 = 1
  SupportTransform = false
  Suppress = false
  TreeRank = 0
  UseAllEdges = false
  ValidateShape = true
FEATURE [PartDesign::Chamfer] Chamfer041
  AddSubType = 0
  Angle = 45
  Base = -> Chamfer040 [Edge25]
  BaseFeature = -> Chamfer040
  ChamferType = 0
  FixShape = 1
  FlipDirection = false
  InvalidShape = false
  NewSolid = false
  Placement = pos=(0,0,0) rot=(1,0,0;1.5708rad)
  Refine = true
  Size = 0.2
  Size2 = 1
  SupportTransform = false
  Suppress = false
  TreeRank = 0
  UseAllEdges = false
  ValidateShape = true
FEATURE [PartDesign::Body] Body057  label="ElasticServoHorn"
  AutoGroupSolids = false
  ClaimAllChildren = false
  ExportMode = 0
  FixShape = 1
  Group = -> [Sketch123,Pad066,Sketch124,Pad067,Sketch125,Pocket049,Sketch126,Pocket050,Sketch127,Pocket051,Chamfer040,Chamfer041]
  InvalidShape = false
  Origin = -> Origin085
  Placement = pos=(-1.09497e-05,-4.80001,-1.51983e-05) rot=(0,1,0;1.5708rad)
  SingleSolid = true
  Tip = -> Chamfer041
  TreeRank = 0
  ValidateShape = false
  _ExportChildren = -> [Pad066,Pad067,Pocket049,Pocket050,Pocket051,Chamfer040,Chamfer041]
  _GroupVersion = 1
FEATURE [Sketcher::SketchObject] Sketch088
  ArcFitTolerance = 0
  ExternalBSplineMaxDegree = 0
  ExternalBSplineTolerance = 0
  FixShape = 1
  FullyConstrained = true
  InternalTolerance = 1e-06
  InvalidShape = false
  MakeInternals = false
  MapMode = 5
  TreeRank = 0
  ValidateShape = false
  sketch-geometry (7):
    g0: Circle CenterX=0 CenterY=0 CenterZ=0 NormalX=0 NormalY=0 NormalZ=1 AngleXU=0 Radius=10
    g1: Circle CenterX=0 CenterY=7 CenterZ=0 NormalX=0 NormalY=0 NormalZ=1 AngleXU=0 Radius=1.5
    g2: Circle CenterX=7 CenterY=0 CenterZ=0 NormalX=0 NormalY=0 NormalZ=1 AngleXU=0 Radius=1.5
    g3: Circle CenterX=0 CenterY=-7 CenterZ=0 NormalX=0 NormalY=0 NormalZ=1 AngleXU=0 Radius=1.5
    g4: Circle CenterX=-7 CenterY=0 CenterZ=0 NormalX=0 NormalY=0 NormalZ=1 AngleXU=0 Radius=1.5
    g5: Circle [constr] CenterX=0 CenterY=0 CenterZ=0 NormalX=0 NormalY=0 NormalZ=1 AngleXU=0 Radius=7
    g6: Circle CenterX=0 CenterY=0 CenterZ=0 NormalX=0 NormalY=0 NormalZ=1 AngleXU=0 Radius=1.5
  constraints (18):
    c: Coincident(g0,g-1)
    c: Diameter(g0) = 20
    c: PointOnObject(g1,g-2)
    c: PointOnObject(g2,g-1)
    c: PointOnObject(g3,g-2)
    c: PointOnObject(g4,g-1)
    c: Equal(g4,g1)
    c: Equal(g1,g2)
    c: Equal(g2,g3)
    c: Diameter(g1) = 3
    c: Coincident(g5,g0)
    c: PointOnObject(g1,g5)
    c: PointOnObject(g2,g5)
    c: PointOnObject(g3,g5)
    c: PointOnObject(g4,g5)
    c: DistanceX(g4,g2) = 14
    c: Coincident(g6,g0)
    c: Equal(g2,g6)
FEATURE [PartDesign::Pad] Pad052
  AddSubType = 0
  AutoTaperInnerAngle = true
  CheckUpToFaceLimits = true
  ClaimChildren = false
  Direction = (0,0,1)
  Fit = 0
  FitJoin = 0
  FixShape = 1
  InnerFit = 0
  InnerFitJoin = 0
  InvalidShape = false
  Length = 2
  Length2 = 100
  NewSolid = false
  Profile = -> Sketch088
  Refine = true
  Reversed = true
  Suppress = false
  TaperInnerAngle = 0
  TaperInnerAngleRev = 0
  TreeRank = 0
  Type = 0
  ValidateShape = true
  _ProfileBasedVersion = 0
FEATURE [Sketcher::SketchObject] Sketch089
  ArcFitTolerance = 0
  ExternalBSplineMaxDegree = 0
  ExternalBSplineTolerance = 0
  FixShape = 1
  FullyConstrained = true
  InternalTolerance = 1e-06
  InvalidShape = false
  MakeInternals = false
  MapMode = 5
  TreeRank = 0
  ValidateShape = false
  sketch-geometry (2):
    g0: Circle CenterX=0 CenterY=0 CenterZ=0 NormalX=0 NormalY=0 NormalZ=1 AngleXU=0 Radius=4.7
    g1: Circle CenterX=0 CenterY=0 CenterZ=0 NormalX=0 NormalY=0 NormalZ=1 AngleXU=0 Radius=3
  constraints (4):
    c: Coincident(g0,g-1)
    c: Coincident(g1,g0)
    c: Diameter(g0) = 9.4
    c: Diameter(g1) = 6
FEATURE [PartDesign::Pad] Pad051
  AddSubType = 0
  AutoTaperInnerAngle = true
  BaseFeature = -> Pad052
  CheckUpToFaceLimits = true
  ClaimChildren = false
  Direction = (0,0,1)
  Fit = 0
  FitJoin = 0
  FixShape = 1
  InnerFit = 0
  InnerFitJoin = 0
  InvalidShape = false
  Length = 5.4
  Length2 = 100
  NewSolid = false
  Profile = -> Sketch089
  Refine = true
  Reversed = true
  Suppress = false
  TaperInnerAngle = 0
  TaperInnerAngleRev = 0
  TreeRank = 0
  Type = 0
  ValidateShape = true
  _ProfileBasedVersion = 0
FEATURE [PartDesign::Body] Body042  label="RoundServoHorn"
  AutoGroupSolids = false
  ClaimAllChildren = false
  ExportMode = 0
  FixShape = 1
  Group = -> [Sketch088,Pad052,Sketch089,Pad051]
  InvalidShape = false
  Origin = -> Origin063
  Placement = pos=(0,0,0) rot=(1,0,0;1.5708rad)
  SingleSolid = true
  Tip = -> Pad051
  TreeRank = 0
  ValidateShape = false
  _ExportChildren = -> [Pad052,Pad051]
  _GroupVersion = 1
FEATURE [App::DocumentObjectGroup] Group006  label="ServoHorn"
  ClaimAllChildren = true
  ExportMode = 1
  Group = -> [Body057,Body042]
  TreeRank = 0
  _GroupVersion = 1
FEATURE [Sketcher::SketchObject] Sketch171
  ArcFitTolerance = 0
  ExternalBSplineMaxDegree = 0
  ExternalBSplineTolerance = 0
  FixShape = 1
  FullyConstrained = true
  InternalTolerance = 1e-06
  InvalidShape = false
  MakeInternals = false
  MapMode = 5
  TreeRank = 0
  ValidateShape = false
  sketch-geometry (1):
    g0: Circle CenterX=0 CenterY=0 CenterZ=0 NormalX=0 NormalY=0 NormalZ=1 AngleXU=0 Radius=9
  constraints (2):
    c: Coincident(g0,g-1)
    c: Diameter(g0) = 18
FEATURE [PartDesign::Pad] Pad073
  AddSubType = 0
  AlongSketchNormal = false
  AutoTaperInnerAngle = true
  CheckUpToFaceLimits = true
  ClaimChildren = false
  Direction = (0,0,1)
  Fit = 0
  FitJoin = 0
  FixShape = 1
  InnerFit = 0
  InnerFitJoin = 0
  InvalidShape = false
  Length = 9
  Length2 = 100
  NewSolid = false
  Profile = -> Sketch171
  Refine = true
  Suppress = false
  TaperInnerAngle = 0
  TaperInnerAngleRev = 0
  TreeRank = 0
  Type = 0
  ValidateShape = true
  _ProfileBasedVersion = 0
FEATURE [PartDesign::Fillet] Fillet041
  AddSubType = 0
  Base = -> Pad073 [Edge3]
  BaseFeature = -> Pad073
  FixShape = 1
  InvalidShape = false
  NewSolid = false
  Radius = 0.4
  Refine = true
  SupportTransform = false
  Suppress = false
  TreeRank = 0
  UseAllEdges = false
  ValidateShape = true
FEATURE [Sketcher::SketchObject] Sketch172
  ArcFitTolerance = 0
  ExternalBSplineMaxDegree = 0
  ExternalBSplineTolerance = 0
  FixShape = 1
  FullyConstrained = true
  InternalTolerance = 1e-06
  InvalidShape = false
  MakeInternals = false
  MapMode = 5
  Placement = pos=(0,0,0) rot=(1,0,0;1.5708rad)
  TreeRank = 0
  ValidateShape = false
  sketch-geometry (8):
    g0: LineSegment StartX=0 StartY=-2.075e-13 StartZ=0 EndX=7.75 EndY=-2.075e-13 EndZ=0
    g1: LineSegment StartX=7.75 StartY=-2.075e-13 StartZ=0 EndX=7.75 EndY=-3 EndZ=0
    g2: LineSegment StartX=7.75 StartY=-3 StartZ=0 EndX=8.8 EndY=-3 EndZ=0
    g3: LineSegment StartX=8.8 StartY=-3 StartZ=0 EndX=8.8 EndY=-10.5 EndZ=0
    g4: LineSegment StartX=8.8 StartY=-10.5 StartZ=0 EndX=7.75 EndY=-10.5 EndZ=0
    g5: LineSegment StartX=7.75 StartY=-10.5 StartZ=0 EndX=7.75 EndY=-19 EndZ=0
    g6: LineSegment StartX=7.75 StartY=-19 StartZ=0 EndX=0 EndY=-19 EndZ=0
    g7: LineSegment StartX=0 StartY=-19 StartZ=0 EndX=0 EndY=-2.061e-13 EndZ=0
  constraints (23):
    c: Coincident(g-1,g0)
    c: Horizontal(g0)
    c: Coincident(g0,g1)
    c: Vertical(g1)
    c: Coincident(g1,g2)
    c: Horizontal(g2)
    c: Coincident(g2,g3)
    c: Vertical(g3)
    c: Coincident(g3,g4)
    c: Coincident(g4,g5)
    c: Vertical(g5)
    c: Coincident(g5,g6)
    c: PointOnObject(g6,g-2)
    c: Horizontal(g6)
    c: Coincident(g6,g7)
    c: Coincident(g7,g0)
    c: DistanceY(g1,g1) = 3
    c: DistanceX(g2) = 8.8
    c: DistanceX(g1) = 7.75
    c: PointOnObject(g5,g1)
    c: DistanceY(g3,g3) = 7.5
    c: Horizontal(g4)
    c: DistanceY(g7,g7) = 19
FEATURE [PartDesign::Revolution] Revolution014
  AddSubType = 0
  Angle = 360
  Axis = (0,0,1)
  Base = (0,0,0)
  BaseFeature = -> Fillet041
  ClaimChildren = false
  Fit = 0
  FitJoin = 0
  FixShape = 1
  InnerFit = 0
  InnerFitJoin = 0
  InvalidShape = false
  NewSolid = false
  Profile = -> Sketch172
  ReferenceAxis = -> Sketch172 [V_Axis]
  Refine = true
  Reversed = true
  Suppress = false
  TreeRank = 0
  ValidateShape = true
  _ProfileBasedVersion = 0
FEATURE [PartDesign::Body] Body082  label="MainBody"
  AutoGroupSolids = false
  ClaimAllChildren = false
  ExportMode = 0
  FixShape = 1
  Group = -> [Sketch171,Pad073,Fillet041,Sketch172,Revolution014]
  InvalidShape = false
  Origin = -> Origin169
  SingleSolid = true
  Tip = -> Revolution014
  TreeRank = 0
  ValidateShape = false
  _ExportChildren = -> [Pad073,Fillet041,Revolution014]
  _GroupVersion = 1
FEATURE [Sketcher::SketchObject] Sketch173
  ArcFitTolerance = 0
  ExternalBSplineMaxDegree = 0
  ExternalBSplineTolerance = 0
  FixShape = 1
  FullyConstrained = true
  InternalTolerance = 1e-06
  InvalidShape = false
  MakeInternals = false
  MapMode = 5
  Placement = pos=(0,-4e-15,-19) rot=(1,0,0;3.14159rad)
  TreeRank = 0
  ValidateShape = false
  sketch-geometry (5):
    g0: LineSegment StartX=9.5 StartY=9.5 StartZ=0 EndX=-9.5 EndY=9.5 EndZ=0
    g1: LineSegment StartX=-9.5 StartY=9.5 StartZ=0 EndX=-9.5 EndY=-9.5 EndZ=0
    g2: LineSegment StartX=-9.5 StartY=-9.5 StartZ=0 EndX=9.5 EndY=-9.5 EndZ=0
    g3: LineSegment StartX=9.5 StartY=-9.5 StartZ=0 EndX=9.5 EndY=9.5 EndZ=0
    g4: Circle [constr] CenterX=-1.2948e-12 CenterY=-4.7939e-12 CenterZ=0 NormalX=0 NormalY=0 NormalZ=1 AngleXU=0 Radius=13.435
  constraints (14):
    c: Coincident(g0,g1)
    c: Coincident(g1,g2)
    c: Coincident(g2,g3)
    c: Coincident(g3,g0)
    c: Equal(g0,g1)
    c: Equal(g0,g2)
    c: Equal(g0,g3)
    c: PointOnObject(g0,g4)
    c: PointOnObject(g1,g4)
    c: PointOnObject(g2,g4)
    c: PointOnObject(g3,g4)
    c: Coincident(g4,g-1)
    c: Horizontal(g0)
    c: DistanceX(g0,g0) = 19
FEATURE [PartDesign::Pad] Pad074
  AddSubType = 0
  AlongSketchNormal = false
  AutoTaperInnerAngle = true
  CheckUpToFaceLimits = true
  ClaimChildren = false
  Direction = (0,-1e-16,-1)
  Fit = 0
  FitJoin = 0
  FixShape = 1
  InnerFit = 0
  InnerFitJoin = 0
  InvalidShape = false
  Length = 14.5
  Length2 = 100
  NewSolid = false
  Placement = pos=(0,-4e-15,-19) rot=(1,0,0;3.14159rad)
  Profile = -> Sketch173
  Refine = true
  Suppress = false
  TaperInnerAngle = 0
  TaperInnerAngleRev = 0
  TreeRank = 0
  Type = 0
  ValidateShape = true
  _ProfileBasedVersion = 0
FEATURE [PartDesign::Fillet] Fillet042
  AddSubType = 0
  Base = -> Pad074 [Edge11,Edge6]
  BaseFeature = -> Pad074
  FixShape = 1
  InvalidShape = false
  NewSolid = false
  Placement = pos=(0,-4e-15,-19) rot=(1,0,0;3.14159rad)
  Radius = 1
  Refine = true
  SupportTransform = false
  Suppress = false
  TreeRank = 0
  UseAllEdges = false
  ValidateShape = true
FEATURE [PartDesign::Body] Body083  label="ElectronicBody"
  AutoGroupSolids = false
  ClaimAllChildren = false
  ExportMode = 0
  FixShape = 1
  Group = -> [Sketch173,Pad074,Fillet042]
  InvalidShape = false
  Origin = -> Origin170
  SingleSolid = true
  Tip = -> Fillet042
  TreeRank = 0
  ValidateShape = false
  _ExportChildren = -> [Pad074,Fillet042]
  _GroupVersion = 1
FEATURE [Sketcher::SketchObject] Sketch174
  ArcFitTolerance = 0
  AttachmentSupport = -> [Fillet042]
  ExternalBSplineMaxDegree = 0
  ExternalBSplineTolerance = 0
  FixShape = 1
  FullyConstrained = true
  InternalTolerance = 1e-06
  InvalidShape = false
  MakeInternals = false
  MapMode = 5
  Placement = pos=(0,-4e-15,-33.5) rot=(1,0,0;3.14159rad)
  Support = -> [Fillet042]
  TreeRank = 0
  ValidateShape = false
  sketch-geometry (16):
    g0: LineSegment StartX=-7.75 StartY=7.3 StartZ=0 EndX=-7.25 EndY=7.3 EndZ=0
    g1: LineSegment StartX=-7.25 StartY=7.3 StartZ=0 EndX=-7.25 EndY=4.5 EndZ=0
    g2: LineSegment StartX=-7.25 StartY=4.5 StartZ=0 EndX=-7.75 EndY=4.5 EndZ=0
    g3: LineSegment StartX=-7.75 StartY=4.5 StartZ=0 EndX=-7.75 EndY=7.3 EndZ=0
    g4: LineSegment StartX=7.25 StartY=7.3 StartZ=0 EndX=7.75 EndY=7.3 EndZ=0
    g5: LineSegment StartX=7.75 StartY=7.3 StartZ=0 EndX=7.75 EndY=4.5 EndZ=0
    g6: LineSegment StartX=7.75 StartY=4.5 StartZ=0 EndX=7.25 EndY=4.5 EndZ=0
    g7: LineSegment StartX=7.25 StartY=4.5 StartZ=0 EndX=7.25 EndY=7.3 EndZ=0
    g8: LineSegment StartX=7.25 StartY=-4.5 StartZ=0 EndX=7.75 EndY=-4.5 EndZ=0
    g9: LineSegment StartX=7.75 StartY=-4.5 StartZ=0 EndX=7.75 EndY=-7.3 EndZ=0
    g10: LineSegment StartX=7.75 StartY=-7.3 StartZ=0 EndX=7.25 EndY=-7.3 EndZ=0
    g11: LineSegment StartX=7.25 StartY=-7.3 StartZ=0 EndX=7.25 EndY=-4.5 EndZ=0
    g12: LineSegment StartX=-7.75 StartY=-4.5 StartZ=0 EndX=-7.25 EndY=-4.5 EndZ=0
    g13: LineSegment StartX=-7.25 StartY=-4.5 StartZ=0 EndX=-7.25 EndY=-7.3 EndZ=0
    g14: LineSegment StartX=-7.25 StartY=-7.3 StartZ=0 EndX=-7.75 EndY=-7.3 EndZ=0
    g15: LineSegment StartX=-7.75 StartY=-7.3 StartZ=0 EndX=-7.75 EndY=-4.5 EndZ=0
  constraints (46):
    c: Coincident(g0,g1)
    c: Coincident(g1,g2)
    c: Coincident(g2,g3)
    c: Coincident(g3,g0)
    c: Horizontal(g0)
    c: Horizontal(g2)
    c: Vertical(g1)
    c: Vertical(g3)
    c: DistanceX(g1,g-1) = 7.25
    c: DistanceX(g0,g0) = 0.5
    c: DistanceY(g3,g3) = 2.8
    c: DistanceY(g2) = 4.5
    c: Coincident(g4,g5)
    c: Coincident(g5,g6)
    c: Coincident(g6,g7)
    c: Coincident(g7,g4)
    c: Horizontal(g4)
    c: Horizontal(g6)
    c: Vertical(g5)
    c: Vertical(g7)
    c: Coincident(g8,g9)
    c: Coincident(g9,g10)
    c: Coincident(g10,g11)
    c: Coincident(g11,g8)
    c: Horizontal(g8)
    c: Horizontal(g10)
    c: Vertical(g9)
    c: Vertical(g11)
    c: Coincident(g12,g13)
    c: Coincident(g13,g14)
    c: Coincident(g14,g15)
    c: Coincident(g15,g12)
    c: Horizontal(g12)
    c: Horizontal(g14)
    c: Vertical(g13)
    c: Vertical(g15)
    c: Equal(g12,g8)
    c: Equal(g8,g6)
    c: Equal(g6,g2)
    c: Equal(g1,g7)
    c: Equal(g7,g11)
    c: Equal(g11,g13)
    c: Horizontal(g13,g10)
    c: Vertical(g8,g5)
    c: Symmetric(g0,g4,g-2)
    c: Symmetric(g12,g1,g-1)
FEATURE [PartDesign::Pad] Pad075
  AddSubType = 0
  AlongSketchNormal = false
  AutoTaperInnerAngle = true
  CheckUpToFaceLimits = true
  ClaimChildren = false
  Direction = (0,0,-1)
  Fit = 0
  FitJoin = 0
  FixShape = 1
  InnerFit = 0
  InnerFitJoin = 0
  InvalidShape = false
  Length = 8.5
  Length2 = 100
  NewSolid = false
  Placement = pos=(0,-4e-15,-19) rot=(1,0,0;3.14159rad)
  Profile = -> Sketch174
  ReferenceAxis = -> Sketch174 [N_Axis]
  Refine = true
  Suppress = false
  TaperInnerAngle = 0
  TaperInnerAngleRev = 0
  TreeRank = 0
  Type = 0
  ValidateShape = true
  _ProfileBasedVersion = 0
FEATURE [PartDesign::Chamfer] Chamfer045
  AddSubType = 0
  Angle = 45
  Base = -> Pad075 [Edge57,Edge53,Edge41,Edge37,Edge65,Edge61,Edge49,Edge45]
  BaseFeature = -> Pad075
  ChamferType = 0
  FixShape = 1
  FlipDirection = false
  InvalidShape = false
  NewSolid = false
  Placement = pos=(0,-4e-15,-19) rot=(1,0,0;3.14159rad)
  Refine = true
  Size = 0.6
  Size2 = 1
  SupportTransform = false
  Suppress = false
  TreeRank = 0
  UseAllEdges = false
  ValidateShape = true
FEATURE [Sketcher::SketchObject] Sketch175
  ArcFitTolerance = 0
  ExternalBSplineMaxDegree = 0
  ExternalBSplineTolerance = 0
  FixShape = 1
  FullyConstrained = false
  InternalTolerance = 1e-06
  InvalidShape = false
  MakeInternals = false
  MapMode = 5
  Placement = pos=(0,0,0) rot=(0.57735,0.57735,0.57735;2.0944rad)
  TreeRank = 0
  ValidateShape = false
  sketch-geometry (8):
    g0: ArcOfCircle CenterX=-6 CenterY=-38.7066 CenterZ=0 NormalX=0 NormalY=0 NormalZ=1 AngleXU=0 Radius=0.456793 StartAngle=1.3e-15 EndAngle=3.14159
    g1: ArcOfCircle CenterX=-6 CenterY=-40.4194 CenterZ=0 NormalX=0 NormalY=0 NormalZ=1 AngleXU=0 Radius=0.456793 StartAngle=3.14159 EndAngle=6.28319
    g2: LineSegment StartX=-6.45679 StartY=-38.7066 StartZ=0 EndX=-6.45679 EndY=-40.4194 EndZ=0
    g3: LineSegment StartX=-5.54321 StartY=-40.4194 StartZ=0 EndX=-5.54321 EndY=-38.7066 EndZ=0
    g4: ArcOfCircle CenterX=6 CenterY=-38.7066 CenterZ=0 NormalX=0 NormalY=0 NormalZ=1 AngleXU=0 Radius=0.417287 StartAngle=-5.3e-15 EndAngle=3.14159
    g5: ArcOfCircle CenterX=6 CenterY=-40.4194 CenterZ=0 NormalX=0 NormalY=0 NormalZ=1 AngleXU=0 Radius=0.417287 StartAngle=3.14159 EndAngle=6.28319
    g6: LineSegment StartX=5.58271 StartY=-38.7066 StartZ=0 EndX=5.58271 EndY=-40.4194 EndZ=0
    g7: LineSegment StartX=6.41729 StartY=-40.4194 StartZ=0 EndX=6.41729 EndY=-38.7066 EndZ=0
  constraints (14):
    c: Tangent(g0,g2) = -1.5708
    c: Tangent(g2,g1) = -1.5708
    c: Tangent(g1,g3) = -1.5708
    c: Tangent(g3,g0) = -1.5708
    c: Equal(g0,g1)
    c: Tangent(g4,g6) = -1.5708
    c: Tangent(g6,g5) = -1.5708
    c: Tangent(g5,g7) = -1.5708
    c: Tangent(g7,g4) = -1.5708
    c: Equal(g4,g5)
    c: Symmetric(g4,g0,g-2)
    c: Symmetric(g5,g1,g-2)
    c: Vertical(g1,g0)
    c: DistanceX(g0) = -6
FEATURE [PartDesign::Pocket] Pocket054
  AddSubType = 1
  AutoTaperInnerAngle = true
  BaseFeature = -> Chamfer045
  CheckUpToFaceLimits = true
  ClaimChildren = false
  Direction = (-1,-1e-16,1e-16)
  Fit = 0
  FitJoin = 0
  FixShape = 1
  InnerFit = 0
  InnerFitJoin = 0
  InvalidShape = false
  Length = 5
  Length2 = 100
  Midplane = true
  NewSolid = false
  Placement = pos=(0,-4e-15,-19) rot=(1,0,0;3.14159rad)
  Profile = -> Sketch175
  Refine = true
  Suppress = false
  TaperInnerAngle = 0
  TaperInnerAngleRev = 0
  TreeRank = 0
  Type = 1
  ValidateShape = true
  _ProfileBasedVersion = 0
  _Version = 0
FEATURE [PartDesign::Body] Body084  label="ElectronicPins"
  AutoGroupSolids = false
  ClaimAllChildren = false
  ExportMode = 0
  FixShape = 1
  Group = -> [Sketch174,Pad075,Chamfer045,Sketch175,Pocket054]
  InvalidShape = false
  Origin = -> Origin171
  SingleSolid = true
  Tip = -> Pocket054
  TreeRank = 0
  ValidateShape = false
  _ExportChildren = -> [Pad075,Chamfer045,Pocket054]
  _GroupVersion = 1
FEATURE [Sketcher::SketchObject] Sketch176
  ArcFitTolerance = 0
  ExternalBSplineMaxDegree = 0
  ExternalBSplineTolerance = 0
  FixShape = 1
  FullyConstrained = true
  InternalTolerance = 1e-06
  InvalidShape = false
  MakeInternals = false
  MapMode = 5
  Placement = pos=(0,0,0) rot=(0.57735,0.57735,0.57735;2.0944rad)
  TreeRank = 0
  ValidateShape = false
  sketch-geometry (12):
    g0: LineSegment StartX=-7.5 StartY=0 StartZ=0 EndX=-7.5 EndY=17 EndZ=0
    g1: LineSegment StartX=-7.5 StartY=17 StartZ=0 EndX=-12 EndY=17 EndZ=0
    g2: LineSegment StartX=-12 StartY=17 StartZ=0 EndX=-12 EndY=20 EndZ=0
    g3: LineSegment [constr] StartX=-7.5 StartY=0 StartZ=0 EndX=7.5 EndY=0 EndZ=0
    g4: LineSegment [constr] StartX=7.5 StartY=0 StartZ=0 EndX=7.5 EndY=17 EndZ=0
    g5: LineSegment [constr] StartX=7.5 StartY=17 StartZ=0 EndX=12 EndY=17 EndZ=0
    g6: LineSegment [constr] StartX=12 StartY=17 StartZ=0 EndX=12 EndY=20 EndZ=0
    g7: ArcOfCircle [constr] CenterX=-1.51e-14 CenterY=-51.5 CenterZ=0 NormalX=0 NormalY=0 NormalZ=1 AngleXU=0 Radius=72.5 StartAngle=1.40451 EndAngle=1.73708
    g8: GeomPoint [constr] X=4.5e-15 Y=21 Z=0
    g9: LineSegment StartX=0 StartY=0 StartZ=0 EndX=4.5e-15 EndY=21 EndZ=0
    g10: LineSegment StartX=-7.5 StartY=0 StartZ=0 EndX=0 EndY=0 EndZ=0
    g11: ArcOfCircle CenterX=-1.51e-14 CenterY=-51.5 CenterZ=0 NormalX=0 NormalY=0 NormalZ=1 AngleXU=0 Radius=72.5 StartAngle=1.5708 EndAngle=1.73708
  constraints (31):
    c: PointOnObject(g0,g-1)
    c: Vertical(g0)
    c: Coincident(g0,g1)
    c: Horizontal(g1)
    c: Coincident(g1,g2)
    c: Coincident(g0,g3)
    c: Coincident(g3,g4)
    c: Vertical(g4)
    c: Coincident(g4,g5)
    c: Horizontal(g5)
    c: Coincident(g5,g6)
    c: Vertical(g6)
    c: Vertical(g2)
    c: Equal(g6,g2)
    c: Symmetric(g0,g3,g-1)
    c: Symmetric(g6,g2,g-2)
    c: DistanceX(g0,g4) = 15
    c: DistanceY(g4) = 17
    c: DistanceY(g2,g2) = 3
    c: DistanceX(g1,g5) = 24
    c: Coincident(g7,g2)
    c: Coincident(g7,g6)
    c: PointOnObject(g8,g-2)
    c: Coincident(g9,g-1)
    c: Coincident(g9,g8)
    c: Coincident(g10,g0)
    c: Coincident(g10,g9)
    c: Coincident(g11,g7)
    c: Coincident(g11,g9)
    c: Coincident(g11,g2)
    c: DistanceY(g9) = 21
FEATURE [PartDesign::Revolution] Revolution015
  AddSubType = 0
  Angle = 360
  Axis = (1e-16,-1e-16,1)
  Base = (0,0,0)
  ClaimChildren = false
  Fit = 0
  FitJoin = 0
  FixShape = 1
  InnerFit = 0
  InnerFitJoin = 0
  InvalidShape = false
  NewSolid = false
  Placement = pos=(0,0,0) rot=(0.57735,0.57735,0.57735;2.0944rad)
  Profile = -> Sketch176
  ReferenceAxis = -> Sketch176 [V_Axis]
  Refine = true
  Suppress = false
  TreeRank = 0
  ValidateShape = true
  _ProfileBasedVersion = 0
FEATURE [PartDesign::Fillet] Fillet043
  AddSubType = 0
  Base = -> Revolution015 [Edge6]
  BaseFeature = -> Revolution015
  FixShape = 1
  InvalidShape = false
  NewSolid = false
  Placement = pos=(0,0,0) rot=(0.57735,0.57735,0.57735;2.0944rad)
  Radius = 1
  Refine = true
  SupportTransform = false
  Suppress = false
  TreeRank = 0
  UseAllEdges = false
  ValidateShape = true
FEATURE [PartDesign::Body] Body085  label="ButtonCaps"
  AutoGroupSolids = false
  ClaimAllChildren = false
  ExportMode = 0
  FixShape = 1
  Group = -> [Sketch176,Revolution015,Fillet043]
  InvalidShape = false
  Origin = -> Origin172
  SingleSolid = true
  Tip = -> Fillet043
  TreeRank = 0
  ValidateShape = false
  _ExportChildren = -> [Revolution015,Fillet043]
  _GroupVersion = 1
FEATURE [App::Part] Part036  label="BAU-2195813"
  ClaimAllChildren = false
  ExportMode = 1
  Group = -> [Body082,Body083,Body084,Body085]
  Origin = -> Origin168
  TreeRank = 0
  _ExportChildren = -> [Body082,Body083,Body084,Body085]
  _GroupVersion = 1
FEATURE [Part::Feature] Solid002  label="PanelUsb (GrabCAD)"
  FixShape = 1
  InvalidShape = false
  Placement = pos=(0,0,0) rot=(0,-1,0;1.5708rad)
  TreeRank = 0
  ValidateShape = false
  shape: bbox 16.24 x 40.24 x 83.5 mm, 159 faces (baked)
FEATURE [Sketcher::SketchObject] Sketch025
  ArcFitTolerance = 0
  ExternalBSplineMaxDegree = 0
  ExternalBSplineTolerance = 0
  FixShape = 1
  FullyConstrained = true
  InternalTolerance = 1e-06
  InvalidShape = false
  MakeInternals = false
  MapMode = 5
  TreeRank = 0
  ValidateShape = false
  sketch-geometry (5):
    g0: LineSegment StartX=-22.5 StartY=-32.5 StartZ=0 EndX=-22.5 EndY=32.5 EndZ=0
    g1: LineSegment StartX=-22.5 StartY=32.5 StartZ=0 EndX=22.5 EndY=32.5 EndZ=0
    g2: LineSegment StartX=22.5 StartY=32.5 StartZ=0 EndX=22.5 EndY=-32.5 EndZ=0
    g3: LineSegment StartX=22.5 StartY=-32.5 StartZ=0 EndX=-22.5 EndY=-32.5 EndZ=0
    g4: GeomPoint [constr] X=0 Y=0 Z=0
  constraints (12):
    c: Coincident(g0,g1)
    c: Coincident(g1,g2)
    c: Coincident(g2,g3)
    c: Coincident(g3,g0)
    c: Horizontal(g1)
    c: Horizontal(g3)
    c: Vertical(g0)
    c: Vertical(g2)
    c: Symmetric(g1,g0,g4)
    c: Coincident(g4,g-1)
    c: DistanceY(g0,g0) = 65
    c: DistanceX(g1,g1) = 45
FEATURE [PartDesign::Pad] Pad010
  AddSubType = 0
  AlongSketchNormal = false
  AutoTaperInnerAngle = true
  CheckUpToFaceLimits = true
  ClaimChildren = false
  Direction = (0,0,1)
  Fit = 0
  FitJoin = 0
  FixShape = 1
  InnerFit = 0
  InnerFitJoin = 0
  InvalidShape = false
  Length = 110
  Length2 = 10
  NewSolid = false
  Profile = -> Sketch025
  ReferenceAxis = -> Sketch025 [N_Axis]
  Refine = true
  Suppress = false
  TaperInnerAngle = 0
  TaperInnerAngleRev = 0
  TreeRank = 0
  Type = 0
  ValidateShape = true
  _ProfileBasedVersion = 0
FEATURE [PartDesign::Fillet] Fillet009
  AddSubType = 0
  Base = -> Pad010 [Edge4,Edge10]
  BaseFeature = -> Pad010
  FixShape = 1
  InvalidShape = false
  NewSolid = false
  Radius = 6
  Refine = true
  SupportTransform = false
  Suppress = false
  TreeRank = 0
  UseAllEdges = false
  ValidateShape = true
FEATURE [Sketcher::SketchObject] Sketch026
  ArcFitTolerance = 0
  AttachmentSupport = -> [Fillet009]
  ExternalBSplineMaxDegree = 0
  ExternalBSplineTolerance = 0
  ExternalGeometry = -> [Fillet009]
  FixShape = 1
  FullyConstrained = true
  InternalTolerance = 1e-06
  InvalidShape = false
  MakeInternals = false
  MapMode = 5
  Placement = pos=(0,-32.5,0) rot=(1,0,0;1.5708rad)
  Support = -> [Fillet009]
  TreeRank = 0
  ValidateShape = false
  sketch-geometry (4):
    g0: LineSegment StartX=17.5 StartY=105 StartZ=0 EndX=-12.5 EndY=105 EndZ=0
    g1: LineSegment StartX=-12.5 StartY=105 StartZ=0 EndX=-12.5 EndY=13 EndZ=0
    g2: LineSegment StartX=-12.5 StartY=13 StartZ=0 EndX=17.5 EndY=13 EndZ=0
    g3: LineSegment StartX=17.5 StartY=13 StartZ=0 EndX=17.5 EndY=105 EndZ=0
  constraints (12):
    c: Coincident(g0,g1)
    c: Coincident(g1,g2)
    c: Coincident(g2,g3)
    c: Coincident(g3,g0)
    c: Horizontal(g0)
    c: Horizontal(g2)
    c: Vertical(g1)
    c: Vertical(g3)
    c: DistanceX(g0,g-3) = 5
    c: DistanceX(g0,g0) = 30
    c: DistanceY(g-3,g2) = 13
    c: DistanceY(g0,g-4) = 5
FEATURE [PartDesign::Pocket] Pocket013
  AddSubType = 1
  AlongSketchNormal = false
  AutoTaperInnerAngle = true
  BaseFeature = -> Fillet009
  CheckUpToFaceLimits = true
  ClaimChildren = false
  Direction = (0,1,-2e-16)
  Fit = 0
  FitJoin = 0
  FixShape = 1
  InnerFit = 0
  InnerFitJoin = 0
  InvalidShape = false
  Length = 12
  Length2 = 10
  NewSolid = false
  Profile = -> Sketch026
  ReferenceAxis = -> Sketch026 [N_Axis]
  Refine = true
  Suppress = false
  TaperInnerAngle = 0
  TaperInnerAngleRev = 0
  TreeRank = 0
  Type = 0
  ValidateShape = true
  _ProfileBasedVersion = 0
  _Version = 0
FEATURE [PartDesign::Mirrored] Mirrored001
  AddSubType = 0
  BaseFeature = -> Pocket013
  CopyShape = true
  FixShape = 1
  InvalidShape = false
  MirrorPlane = -> XZ_Plane011
  NewSolid = false
  OriginalSubs = -> [Pocket013]
  Originals = -> [Pocket013]
  ParallelTransform = true
  Refine = true
  SubTransform = true
  Suppress = false
  TreeRank = 0
  ValidateShape = true
  _Version = 0
FEATURE [Sketcher::SketchObject] Sketch027
  ArcFitTolerance = 0
  AttachmentSupport = -> [Mirrored001]
  ExternalBSplineMaxDegree = 0
  ExternalBSplineTolerance = 0
  ExternalGeometry = -> [Mirrored001]
  FixShape = 1
  FullyConstrained = false
  InternalTolerance = 1e-06
  InvalidShape = false
  MakeInternals = false
  MapMode = 5
  Placement = pos=(0,-20.5,4.7e-15) rot=(1,0,0;1.5708rad)
  Support = -> [Mirrored001]
  TreeRank = 0
  ValidateShape = false
  sketch-geometry (3):
    g0: Circle CenterX=-5 CenterY=101 CenterZ=0 NormalX=0 NormalY=0 NormalZ=1 AngleXU=0 Radius=2
    g1: Circle CenterX=10 CenterY=101 CenterZ=0 NormalX=0 NormalY=0 NormalZ=1 AngleXU=0 Radius=2
    g2: LineSegment [constr] StartX=2.5 StartY=105 StartZ=0 EndX=2.5 EndY=91.3759 EndZ=0
  constraints (7):
    c: Equal(g1,g0)
    c: Diameter(g1) = 4
    c: Vertical(g2)
    c: Symmetric(g-3,g-3,g2)
    c: Symmetric(g0,g1,g2)
    c: DistanceX(g0,g1) = 15
    c: DistanceY(g1,g-3) = 4
FEATURE [PartDesign::Pad] Pad011
  AddSubType = 0
  AlongSketchNormal = false
  AutoTaperInnerAngle = true
  BaseFeature = -> Mirrored001
  CheckUpToFaceLimits = true
  ClaimChildren = false
  Direction = (0,-1,2e-16)
  Fit = 0
  FitJoin = 0
  FixShape = 1
  InnerFit = 0
  InnerFitJoin = 0
  InvalidShape = false
  Length = 10
  Length2 = 10
  NewSolid = false
  Profile = -> Sketch027
  ReferenceAxis = -> Sketch027 [N_Axis]
  Refine = true
  Suppress = false
  TaperInnerAngle = 0
  TaperInnerAngleRev = 0
  TreeRank = 0
  Type = 0
  ValidateShape = true
  _ProfileBasedVersion = 0
FEATURE [Sketcher::SketchObject] Sketch028
  ArcFitTolerance = 0
  AttachmentSupport = -> [Pad011]
  ExternalBSplineMaxDegree = 0
  ExternalBSplineTolerance = 0
  ExternalGeometry = -> [Pad011]
  FixShape = 1
  FullyConstrained = true
  InternalTolerance = 1e-06
  InvalidShape = false
  MakeInternals = false
  MapMode = 5
  Placement = pos=(-22.5,0,0) rot=(0.57735,-0.57735,-0.57735;2.0944rad)
  Support = -> [Pad011]
  TreeRank = 0
  ValidateShape = false
  sketch-geometry (4):
    g0: LineSegment StartX=-32.5 StartY=0 StartZ=0 EndX=32.5 EndY=0 EndZ=0
    g1: LineSegment StartX=32.5 StartY=0 StartZ=0 EndX=32.5 EndY=50 EndZ=0
    g2: LineSegment StartX=32.5 StartY=50 StartZ=0 EndX=-32.5 EndY=50 EndZ=0
    g3: LineSegment StartX=-32.5 StartY=50 StartZ=0 EndX=-32.5 EndY=0 EndZ=0
  constraints (11):
    c: Coincident(g0,g1)
    c: Coincident(g1,g2)
    c: Coincident(g2,g3)
    c: Coincident(g3,g0)
    c: Horizontal(g0)
    c: Horizontal(g2)
    c: Vertical(g1)
    c: Vertical(g3)
    c: Coincident(g0,g-3)
    c: PointOnObject(g1,g-4)
    c: DistanceY(g1,g-5) = 60
FEATURE [PartDesign::Pocket] Pocket014
  AddSubType = 1
  AlongSketchNormal = false
  AutoTaperInnerAngle = true
  BaseFeature = -> Pad011
  CheckUpToFaceLimits = true
  ClaimChildren = false
  Direction = (1,0,0)
  Fit = 0
  FitJoin = 0
  FixShape = 1
  InnerFit = 0
  InnerFitJoin = 0
  InvalidShape = false
  Length = 5
  Length2 = 10
  NewSolid = false
  Profile = -> Sketch028
  ReferenceAxis = -> Sketch028 [N_Axis]
  Refine = true
  Suppress = false
  TaperInnerAngle = 0
  TaperInnerAngleRev = 0
  TreeRank = 0
  Type = 0
  ValidateShape = true
  _ProfileBasedVersion = 0
  _Version = 0
FEATURE [PartDesign::Fillet] Fillet010
  AddSubType = 0
  Base = -> Pocket014 [Edge6,Edge5]
  BaseFeature = -> Pocket014
  FixShape = 1
  InvalidShape = false
  NewSolid = false
  Radius = 20
  Refine = true
  SupportTransform = false
  Suppress = false
  TreeRank = 0
  UseAllEdges = false
  ValidateShape = true
FEATURE [PartDesign::Fillet] Fillet011
  AddSubType = 0
  Base = -> Fillet010 [Edge37,Edge40]
  BaseFeature = -> Fillet010
  FixShape = 1
  InvalidShape = false
  NewSolid = false
  Radius = 3
  Refine = true
  SupportTransform = false
  Suppress = false
  TreeRank = 0
  UseAllEdges = false
  ValidateShape = true
FEATURE [PartDesign::Body] Body011  label="Gens ACE - 6S - 1250mAh + Bag"
  AutoGroupSolids = false
  ClaimAllChildren = false
  ExportMode = 0
  FixShape = 1
  Group = -> [Sketch025,Pad010,Fillet009,Sketch026,Pocket013,Mirrored001,Sketch027,Pad011,Sketch028,Pocket014,Fillet010,Fillet011]
  InvalidShape = false
  Origin = -> Origin198
  SingleSolid = true
  Tip = -> Fillet011
  TreeRank = 0
  ValidateShape = false
  _ExportChildren = -> [Pad010,Fillet009,Pocket013,Mirrored001,Pad011,Pocket014,Fillet010,Fillet011]
  _GroupVersion = 1
FEATURE [App::DocumentObjectGroup] Group009  label="Batteries"
  ClaimAllChildren = true
  ExportMode = 1
  Group = -> [Body011]
  TreeRank = 0
  _GroupVersion = 1
FEATURE [Part::Feature] Compound  label="2.8in TFT(Without Glass)- Tucked Cable"
  FixShape = 1
  InvalidShape = false
  Placement = pos=(-0.0570641,-2.2987,1.6256) rot=(0,0,1;3.14159rad)
  TreeRank = 0
  ValidateShape = false
  shape: bbox 50.13 x 69.5 x 2.736 mm, 295 faces, 4 solids (baked)
FEATURE [App::Link] Link030  label="0603 Capacitor"
  AutoLinkLabel = false
  AutoPlacement = true
  LinkPlacement = pos=(-2.48397,19.738,0.00254) rot=(0,1,0;3.14159rad)
  LinkedObject = -> Solid004
  Placement = pos=(-2.48397,19.738,0.00254) rot=(0,1,0;3.14159rad)
  SyncGroupVisibility = false
  TreeRank = 0
  _LinkVersion = 1
FEATURE [App::Link] Link031  label="0603 Resistor"
  AutoLinkLabel = false
  AutoPlacement = true
  LinkPlacement = pos=(-3.87947,-4.76172,0.00254) rot=(1,0,0;3.14159rad)
  LinkedObject = -> Solid003
  Placement = pos=(-3.87947,-4.76172,0.00254) rot=(1,0,0;3.14159rad)
  SyncGroupVisibility = false
  TreeRank = 0
  _LinkVersion = 1
FEATURE [App::Link] Link032  label="0603 Resistor001"
  AutoLinkLabel = false
  AutoPlacement = true
  LinkPlacement = pos=(-2.33553,-0.993585,0.00254) rot=(0,1,0;3.14159rad)
  LinkedObject = -> Solid003
  Placement = pos=(-2.33553,-0.993585,0.00254) rot=(0,1,0;3.14159rad)
  SyncGroupVisibility = false
  TreeRank = 0
  _LinkVersion = 1
FEATURE [App::Link] Link033  label="0603 Resistor002"
  AutoLinkLabel = false
  AutoPlacement = true
  LinkPlacement = pos=(-12.9341,26.6747,0.00254) rot=(0,1,0;3.14159rad)
  LinkedObject = -> Solid003
  Placement = pos=(-12.9341,26.6747,0.00254) rot=(0,1,0;3.14159rad)
  SyncGroupVisibility = false
  TreeRank = 0
  _LinkVersion = 1
FEATURE [App::Link] Link034  label="0603 Resistor003"
  AutoLinkLabel = false
  AutoPlacement = true
  LinkPlacement = pos=(4.53383,19.5922,0.00254) rot=(0,1,0;3.14159rad)
  LinkedObject = -> Solid003
  Placement = pos=(4.53383,19.5922,0.00254) rot=(0,1,0;3.14159rad)
  SyncGroupVisibility = false
  TreeRank = 0
  _LinkVersion = 1
FEATURE [App::Link] Link035  label="0603 Resistor004"
  AutoLinkLabel = false
  AutoPlacement = true
  LinkPlacement = pos=(4.38027,26.5372,0.00254) rot=(0,1,0;3.14159rad)
  LinkedObject = -> Solid003
  Placement = pos=(4.38027,26.5372,0.00254) rot=(0,1,0;3.14159rad)
  SyncGroupVisibility = false
  TreeRank = 0
  _LinkVersion = 1
FEATURE [App::Link] Link036  label="SOT23-3"
  AutoLinkLabel = false
  AutoPlacement = true
  LinkPlacement = pos=(-3.37348,23.944,0.105) rot=(0.999996,-0.002749,0;3.14159rad)
  LinkedObject = -> Solid005
  Placement = pos=(-3.37348,23.944,0.105) rot=(0.999996,-0.002749,0;3.14159rad)
  SyncGroupVisibility = false
  TreeRank = 0
  _LinkVersion = 1
FEATURE [Part::Feature] Solid  label="2.8 LCD TFT Module - Without Glass"
  FixShape = 1
  InvalidShape = false
  TreeRank = 0
  ValidateShape = false
  shape: bbox 50.16 x 85.92 x 10.69 mm, 1917 faces (baked)
FEATURE [Part::Feature] Solid001  label="5035000993"
  FixShape = 1
  InvalidShape = false
  Placement = pos=(3.55645,-3.30468,-2.85) rot=(0.707107,0.707107,0;3.14159rad)
  TreeRank = 0
  ValidateShape = false
  shape: bbox 21.53 x 28.61 x 2.96 mm, 602 faces (baked)
FEATURE [Part::Feature] Solid003  label="0603 Resistor005"
  FixShape = 1
  InvalidShape = false
  Placement = pos=(-2.2311,-3.165,0.00254) rot=(0,1,0;3.14159rad)
  TreeRank = 0
  ValidateShape = false
  shape: bbox 1.617 x 0.8669 x 0.4669 mm, 38 faces (baked)
FEATURE [Part::Feature] Solid004  label="0603 Capacitor001"
  FixShape = 1
  InvalidShape = false
  Placement = pos=(-14.5217,25.6289,0.00254) rot=(1,0,0;3.14159rad)
  TreeRank = 0
  ValidateShape = false
  shape: bbox 1.6 x 0.8382 x 0.8382 mm, 24 faces (baked)
FEATURE [Part::Feature] Solid005  label="SOT23-004"
  FixShape = 1
  InvalidShape = false
  Placement = pos=(3.6167,23.9432,0.105) rot=(0.70831,0.705902,0;3.14159rad)
  TreeRank = 0
  ValidateShape = false
  shape: bbox 3.014 x 2.849 x 1.193 mm, 52 faces (baked)
FEATURE [App::Part] Part014  label="2.8 TFT Module"
  ClaimAllChildren = false
  ExportMode = 1
  Group = -> [Solid,Solid001,Solid003,Solid004,Link030,Link031,Link032,Link033,Link034,Link035,Solid005,Link036,Compound]
  Origin = -> Origin199
  Placement = pos=(0,0,0) rot=(-1,0,0;1.5708rad)
  TreeRank = 0
  _ExportChildren = -> [Solid,Solid001,Solid003,Solid004,Link030,Link031,Link032,Link033,Link034,Link035,Solid005,Link036,Compound]
  _GroupVersion = 1
FEATURE [App::VRMLObject] SparkFun_Optical_Tracking_Odometry_Sensor
  Placement = pos=(0,0,0.8) rot=(0,0,1;0rad)
  TreeRank = 0
FEATURE [Sketcher::SketchObject] Sketch210
  ArcFitTolerance = 0
  ExternalBSplineMaxDegree = 0
  ExternalBSplineTolerance = 0
  FixShape = 1
  FullyConstrained = true
  InternalTolerance = 1e-06
  InvalidShape = false
  MakeInternals = false
  MapMode = 5
  TreeRank = 0
  ValidateShape = false
  sketch-geometry (14):
    g0: LineSegment StartX=-12.7 StartY=-12.7 StartZ=0 EndX=12.7 EndY=-12.7 EndZ=0
    g1: LineSegment StartX=12.7 StartY=-12.7 StartZ=0 EndX=12.7 EndY=12.7 EndZ=0
    g2: LineSegment StartX=12.7 StartY=12.7 StartZ=0 EndX=-12.7 EndY=12.7 EndZ=0
    g3: LineSegment StartX=-12.7 StartY=12.7 StartZ=0 EndX=-12.7 EndY=-12.7 EndZ=0
    g4: GeomPoint [constr] X=0 Y=0 Z=0
    g5: LineSegment [constr] StartX=-10.16 StartY=-10.16 StartZ=0 EndX=10.16 EndY=-10.16 EndZ=0
    g6: LineSegment [constr] StartX=10.16 StartY=-10.16 StartZ=0 EndX=10.16 EndY=10.16 EndZ=0
    g7: LineSegment [constr] StartX=10.16 StartY=10.16 StartZ=0 EndX=-10.16 EndY=10.16 EndZ=0
    g8: LineSegment [constr] StartX=-10.16 StartY=10.16 StartZ=0 EndX=-10.16 EndY=-10.16 EndZ=0
    g9: GeomPoint [constr] X=0 Y=0 Z=0
    g10: Circle CenterX=-10.16 CenterY=10.16 CenterZ=0 NormalX=0 NormalY=0 NormalZ=1 AngleXU=0 Radius=1.5
    g11: Circle CenterX=10.16 CenterY=10.16 CenterZ=0 NormalX=0 NormalY=0 NormalZ=1 AngleXU=0 Radius=1.5
    g12: Circle CenterX=10.16 CenterY=-10.16 CenterZ=0 NormalX=0 NormalY=0 NormalZ=1 AngleXU=0 Radius=1.5
    g13: Circle CenterX=-10.16 CenterY=-10.16 CenterZ=0 NormalX=0 NormalY=0 NormalZ=1 AngleXU=0 Radius=1.5
  constraints (32):
    c: Coincident(g0,g1)
    c: Coincident(g1,g2)
    c: Coincident(g2,g3)
    c: Coincident(g3,g0)
    c: Horizontal(g0)
    c: Horizontal(g2)
    c: Vertical(g1)
    c: Vertical(g3)
    c: Symmetric(g2,g0,g4)
    c: Coincident(g4,g-1)
    c: DistanceX(g2,g2) = 25.4
    c: Equal(g1,g2)
    c: Coincident(g5,g6)
    c: Coincident(g6,g7)
    c: Coincident(g7,g8)
    c: Coincident(g8,g5)
    c: Horizontal(g5)
    c: Horizontal(g7)
    c: Vertical(g6)
    c: Vertical(g8)
    c: Symmetric(g7,g5,g9)
    c: Coincident(g9,g4)
    c: Equal(g6,g7)
    c: DistanceX(g7,g7) = 20.32
    c: Coincident(g10,g7)
    c: Coincident(g11,g6)
    c: Coincident(g12,g5)
    c: Coincident(g13,g5)
    c: Equal(g11,g10)
    c: Equal(g10,g13)
    c: Equal(g13,g12)
    c: Diameter(g11) = 3
FEATURE [PartDesign::Pad] Pad085
  AddSubType = 0
  AutoTaperInnerAngle = true
  CheckUpToFaceLimits = true
  ClaimChildren = false
  Direction = (0,0,1)
  Fit = 0
  FitJoin = 0
  FixShape = 1
  InnerFit = 0
  InnerFitJoin = 0
  InvalidShape = false
  Length = 1.6
  Length2 = 10
  NewSolid = false
  Profile = -> Sketch210
  ReferenceAxis = -> Sketch210 [N_Axis]
  Refine = true
  Suppress = false
  TaperInnerAngle = 0
  TaperInnerAngleRev = 0
  TreeRank = 0
  Type = 0
  ValidateShape = true
  _ProfileBasedVersion = 0
FEATURE [PartDesign::Body] Body102  label="SimpleOTOS-SparkFun"
  AutoGroupSolids = false
  ClaimAllChildren = false
  ExportMode = 0
  FixShape = 1
  Group = -> [Sketch210,Pad085]
  InvalidShape = false
  Origin = -> Origin201
  SingleSolid = true
  Tip = -> Pad085
  TreeRank = 0
  ValidateShape = false
  _ExportChildren = -> [Pad085]
  _GroupVersion = 1
FEATURE [App::Part] Part045  label="SparkFun OTOS - SEN-24904"
  ClaimAllChildren = false
  ExportMode = 1
  Group = -> [SparkFun_Optical_Tracking_Odometry_Sensor,Body102]
  Origin = -> Origin200
  TreeRank = 0
  _ExportChildren = -> [SparkFun_Optical_Tracking_Odometry_Sensor,Body102]
  _GroupVersion = 1
FEATURE [PartDesign::CoordinateSystem] Local_CS005
  AttacherType = Attacher::AttachEngine3D
  FixShape = 1
  InvalidShape = false
  MapMode = 11
  Placement = pos=(0,40,-1.8e-14) rot=(1,0,0;1.5708rad)
  TreeRank = 0
  ValidateShape = false
FEATURE [Sketcher::SketchObject] Sketch211
  ArcFitTolerance = 0
  ExternalBSplineMaxDegree = 0
  ExternalBSplineTolerance = 0
  FixShape = 1
  FullyConstrained = true
  InternalTolerance = 1e-06
  InvalidShape = false
  MakeInternals = false
  MapMode = 5
  Placement = pos=(0,0,0) rot=(1,0,0;1.5708rad)
  TreeRank = 0
  ValidateShape = false
  sketch-geometry (14):
    g0: ArcOfCircle CenterX=0 CenterY=0 CenterZ=0 NormalX=0 NormalY=0 NormalZ=1 AngleXU=0 Radius=1.25 StartAngle=0 EndAngle=1.5708
    g1: LineSegment StartX=1e-16 StartY=1.25 StartZ=0 EndX=0 EndY=2 EndZ=0
    g2: LineSegment StartX=0 StartY=2 StartZ=0 EndX=1 EndY=2 EndZ=0
    g3: LineSegment [constr] StartX=0 StartY=0 StartZ=0 EndX=5 EndY=5 EndZ=0
    g4: LineSegment StartX=1 StartY=2 StartZ=0 EndX=3.3 EndY=4 EndZ=0
    g5: LineSegment StartX=3.3 StartY=4 StartZ=0 EndX=1.5 EndY=4 EndZ=0
    g6: LineSegment StartX=1.5 StartY=4 StartZ=0 EndX=1.5 EndY=5 EndZ=0
    g7: LineSegment StartX=1.5 StartY=5 StartZ=0 EndX=5 EndY=5 EndZ=0
    g8: LineSegment StartX=5 StartY=5 StartZ=0 EndX=5 EndY=1.5 EndZ=0
    g9: LineSegment StartX=5 StartY=1.5 StartZ=0 EndX=4 EndY=1.5 EndZ=0
    g10: LineSegment StartX=4 StartY=1.5 StartZ=0 EndX=4 EndY=3.3 EndZ=0
    g11: LineSegment StartX=4 StartY=3.3 StartZ=0 EndX=2 EndY=1 EndZ=0
    g12: LineSegment StartX=2 StartY=1 StartZ=0 EndX=2 EndY=0 EndZ=0
    g13: LineSegment StartX=2 StartY=0 StartZ=0 EndX=1.25 EndY=0 EndZ=0
  constraints (41):
    c: Coincident(g0,g-1)
    c: PointOnObject(g0,g-1)
    c: PointOnObject(g0,g-2)
    c: Coincident(g1,g0)
    c: PointOnObject(g1,g-2)
    c: Coincident(g2,g1)
    c: Horizontal(g2)
    c: Coincident(g3,g0)
    c: Angle(g-1,g3) = 0.785398
    c: DistanceX(g3) = 5
    c: Diameter(g0) = 2.5
    c: DistanceX(g2) = 1
    c: Coincident(g4,g2)
    c: Coincident(g5,g4)
    c: Horizontal(g5)
    c: Coincident(g6,g5)
    c: Vertical(g6)
    c: Coincident(g7,g6)
    c: Coincident(g7,g3)
    c: Coincident(g8,g7)
    c: Vertical(g8)
    c: Coincident(g9,g8)
    c: Coincident(g10,g9)
    c: Vertical(g10)
    c: Coincident(g11,g10)
    c: Coincident(g12,g11)
    c: PointOnObject(g12,g-1)
    c: Vertical(g12)
    c: Coincident(g13,g12)
    c: Coincident(g13,g0)
    c: Equal(g12,g2)
    c: Equal(g13,g1)
    c: Horizontal(g7)
    c: Horizontal(g9)
    c: Equal(g6,g9)
    c: Equal(g11,g4)
    c: Equal(g5,g10)
    c: DistanceY(g2,g6) = 3
    c: DistanceX(g6) = 1.5
    c: DistanceY(g6,g6) = 1
    c: DistanceX(g5,g5) = 1.8
FEATURE [PartDesign::Pad] Pad086
  AddSubType = 0
  AutoTaperInnerAngle = true
  CheckUpToFaceLimits = true
  ClaimChildren = false
  Direction = (0,-1,0)
  Fit = 0
  FitJoin = 0
  FixShape = 1
  InnerFit = 0
  InnerFitJoin = 0
  InvalidShape = false
  Length = 40
  Length2 = 100
  NewSolid = false
  Placement = pos=(0,0,0) rot=(1,0,0;1.5708rad)
  Profile = -> Sketch211
  ReferenceAxis = -> Sketch211 [N_Axis]
  Refine = true
  Reversed = true
  Suppress = false
  TaperInnerAngle = 0
  TaperInnerAngleRev = 0
  TreeRank = 0
  Type = 0
  ValidateShape = true
  _ProfileBasedVersion = 0
FEATURE [PartDesign::PolarPattern] PolarPattern021
  AddSubType = 0
  Angle = 360
  AttacherType = Attacher::AttachEngine3D
  Axis = -> Y_Axis125
  BaseFeature = -> Pad086
  CopyShape = true
  FixShape = 1
  InvalidShape = false
  NewSolid = false
  Occurrences = 4
  OriginalSubs = -> [Pad086]
  Originals = -> [Pad086]
  ParallelTransform = true
  Placement = pos=(0,0,0) rot=(1,0,0;1.5708rad)
  Refine = true
  SubTransform = true
  Suppress = false
  TreeRank = 0
  ValidateShape = true
  _Version = 0
FEATURE [PartDesign::Body] Body103  label="MB_40"
  AutoGroupSolids = false
  ClaimAllChildren = false
  ExportMode = 0
  FixShape = 1
  Group = -> [Sketch211,Pad086,PolarPattern021,Local_CS005]
  InvalidShape = false
  Origin = -> Origin202
  SingleSolid = true
  Tip = -> PolarPattern021
  TreeRank = 0
  ValidateShape = false
  _ExportChildren = -> [Pad086,PolarPattern021,Local_CS005]
  _GroupVersion = 1
FEATURE [Sketcher::SketchObject] Sketch212
  ArcFitTolerance = 0
  ExternalBSplineMaxDegree = 0
  ExternalBSplineTolerance = 0
  FixShape = 1
  FullyConstrained = true
  InternalTolerance = 1e-06
  InvalidShape = false
  MakeInternals = false
  MapMode = 5
  Placement = pos=(0,0,0) rot=(0.57735,0.57735,0.57735;2.0944rad)
  TreeRank = 0
  ValidateShape = false
  sketch-geometry (5):
    g0: LineSegment StartX=-5 StartY=-5 StartZ=0 EndX=5 EndY=-5 EndZ=0
    g1: LineSegment StartX=5 StartY=-5 StartZ=0 EndX=5 EndY=5 EndZ=0
    g2: LineSegment StartX=5 StartY=5 StartZ=0 EndX=-5 EndY=5 EndZ=0
    g3: LineSegment StartX=-5 StartY=5 StartZ=0 EndX=-5 EndY=-5 EndZ=0
    g4: GeomPoint [constr] X=0 Y=0 Z=0
  constraints (12):
    c: Coincident(g0,g1)
    c: Coincident(g1,g2)
    c: Coincident(g2,g3)
    c: Coincident(g3,g0)
    c: Horizontal(g0)
    c: Horizontal(g2)
    c: Vertical(g1)
    c: Vertical(g3)
    c: Symmetric(g2,g0,g4)
    c: Coincident(g4,g-1)
    c: Equal(g2,g1)
    c: DistanceX(g2,g2) = 10
FEATURE [PartDesign::Pad] Pad087
  AddSubType = 0
  AutoTaperInnerAngle = true
  CheckUpToFaceLimits = true
  ClaimChildren = false
  Direction = (1,1e-16,-1e-16)
  Fit = 0
  FitJoin = 0
  FixShape = 1
  InnerFit = 0
  InnerFitJoin = 0
  InvalidShape = false
  Length = 10
  Length2 = 10
  Midplane = true
  NewSolid = false
  Placement = pos=(0,0,0) rot=(0.57735,0.57735,0.57735;2.0944rad)
  Profile = -> Sketch212
  ReferenceAxis = -> Sketch212 [N_Axis]
  Refine = true
  Suppress = false
  TaperInnerAngle = 0
  TaperInnerAngleRev = 0
  TreeRank = 0
  Type = 0
  ValidateShape = true
  _ProfileBasedVersion = 0
FEATURE [Sketcher::SketchObject] Sketch213
  ArcFitTolerance = 0
  ExternalBSplineMaxDegree = 0
  ExternalBSplineTolerance = 0
  FixShape = 1
  FullyConstrained = true
  InternalTolerance = 1e-06
  InvalidShape = false
  MakeInternals = false
  MapMode = 5
  Placement = pos=(0,0,0) rot=(0.57735,0.57735,0.57735;2.0944rad)
  TreeRank = 0
  ValidateShape = false
  sketch-geometry (1):
    g0: Circle CenterX=0 CenterY=0 CenterZ=0 NormalX=0 NormalY=0 NormalZ=1 AngleXU=0 Radius=1.5
  constraints (2):
    c: Coincident(g0,g-1)
    c: Diameter(g0) = 3
FEATURE [PartDesign::Pocket] Pocket063
  AddSubType = 1
  AutoTaperInnerAngle = true
  BaseFeature = -> Pad087
  CheckUpToFaceLimits = true
  ClaimChildren = false
  Direction = (-1,-1e-16,1e-16)
  Fit = 0
  FitJoin = 0
  FixShape = 1
  InnerFit = 0
  InnerFitJoin = 0
  InvalidShape = false
  Length = 5
  Length2 = 5
  Midplane = true
  NewSolid = false
  Placement = pos=(0,0,0) rot=(0.57735,0.57735,0.57735;2.0944rad)
  Profile = -> Sketch213
  ReferenceAxis = -> Sketch213 [N_Axis]
  Refine = true
  Suppress = false
  TaperInnerAngle = 0
  TaperInnerAngleRev = 0
  TreeRank = 0
  Type = 1
  ValidateShape = true
  _ProfileBasedVersion = 0
  _Version = 0
FEATURE [PartDesign::PolarPattern] PolarPattern022
  AddSubType = 0
  Angle = 90
  Axis = -> Z_Axis126
  BaseFeature = -> Pocket063
  CopyShape = true
  FixShape = 1
  InvalidShape = false
  NewSolid = false
  Occurrences = 2
  OriginalSubs = -> [Pocket063]
  Originals = -> [Pocket063]
  ParallelTransform = true
  Placement = pos=(0,0,0) rot=(0.57735,0.57735,0.57735;2.0944rad)
  Refine = true
  SubTransform = true
  Suppress = false
  TreeRank = 0
  ValidateShape = true
  _Version = 0
FEATURE [Sketcher::SketchObject] Sketch214
  ArcFitTolerance = 0
  AttachmentSupport = -> [PolarPattern022]
  ExternalBSplineMaxDegree = 0
  ExternalBSplineTolerance = 0
  FixShape = 1
  FullyConstrained = true
  InternalTolerance = 1e-06
  InvalidShape = false
  MakeInternals = false
  MapMode = 5
  Placement = pos=(5,6.7e-15,-1.7e-15) rot=(0.57735,0.57735,0.57735;2.0944rad)
  Support = -> [PolarPattern022]
  TreeRank = 0
  ValidateShape = false
  sketch-geometry (1):
    g0: Circle CenterX=0 CenterY=0 CenterZ=0 NormalX=0 NormalY=0 NormalZ=1 AngleXU=0 Radius=3
  constraints (2):
    c: Coincident(g0,g-1)
    c: Diameter(g0) = 6
FEATURE [PartDesign::Pocket] Pocket064
  AddSubType = 1
  AutoTaperInnerAngle = true
  BaseFeature = -> PolarPattern022
  CheckUpToFaceLimits = true
  ClaimChildren = false
  Direction = (-1,-1.3e-15,2e-16)
  Fit = 0
  FitJoin = 0
  FixShape = 1
  InnerFit = 0
  InnerFitJoin = 0
  InvalidShape = false
  Length = 8
  Length2 = 5
  NewSolid = false
  Placement = pos=(0,0,0) rot=(0.57735,0.57735,0.57735;2.0944rad)
  Profile = -> Sketch214
  ReferenceAxis = -> Sketch214 [N_Axis]
  Refine = true
  Suppress = false
  TaperInnerAngle = 0
  TaperInnerAngleRev = 0
  TreeRank = 0
  Type = 0
  ValidateShape = true
  _ProfileBasedVersion = 0
  _Version = 0
FEATURE [Sketcher::SketchObject] Sketch215
  ArcFitTolerance = 0
  AttachmentSupport = -> [Pocket064]
  ExternalBSplineMaxDegree = 0
  ExternalBSplineTolerance = 0
  FixShape = 1
  FullyConstrained = true
  InternalTolerance = 1e-06
  InvalidShape = false
  MakeInternals = false
  MapMode = 5
  Placement = pos=(-6.7e-15,5,4.2e-15) rot=(-0.57735,-0.57735,-0.57735;2.0944rad)
  Support = -> [Pocket064]
  TreeRank = 0
  ValidateShape = false
  sketch-geometry (1):
    g0: Circle CenterX=0 CenterY=0 CenterZ=0 NormalX=0 NormalY=0 NormalZ=1 AngleXU=0 Radius=3
  constraints (2):
    c: Coincident(g0,g-1)
    c: Diameter(g0) = 6
FEATURE [PartDesign::Pocket] Pocket065
  AddSubType = 1
  AutoTaperInnerAngle = true
  BaseFeature = -> Pocket064
  CheckUpToFaceLimits = true
  ClaimChildren = false
  Direction = (1.3e-15,-1,-9e-16)
  Fit = 0
  FitJoin = 0
  FixShape = 1
  InnerFit = 0
  InnerFitJoin = 0
  InvalidShape = false
  Length = 8
  Length2 = 5
  NewSolid = false
  Placement = pos=(0,0,0) rot=(0.57735,0.57735,0.57735;2.0944rad)
  Profile = -> Sketch215
  ReferenceAxis = -> Sketch215 [N_Axis]
  Refine = true
  Suppress = false
  TaperInnerAngle = 0
  TaperInnerAngleRev = 0
  TreeRank = 0
  Type = 0
  ValidateShape = true
  _ProfileBasedVersion = 0
  _Version = 0
FEATURE [Sketcher::SketchObject] Sketch216
  ArcFitTolerance = 0
  ExternalBSplineMaxDegree = 0
  ExternalBSplineTolerance = 0
  ExternalGeometry = -> [Pocket065]
  FixShape = 1
  FullyConstrained = true
  InternalTolerance = 1e-06
  InvalidShape = false
  MakeInternals = false
  MapMode = 5
  Placement = pos=(0,0,0) rot=(0.57735,0.57735,0.57735;2.0944rad)
  TreeRank = 0
  ValidateShape = false
  sketch-geometry (3):
    g0: LineSegment StartX=-3 StartY=3 StartZ=0 EndX=-6 EndY=0 EndZ=0
    g1: LineSegment StartX=-3 StartY=1.43506e-08 StartZ=0 EndX=-6 EndY=0 EndZ=0
    g2: LineSegment StartX=-3 StartY=1.43506e-08 StartZ=0 EndX=-3 EndY=3 EndZ=0
  constraints (8):
    c: PointOnObject(g0,g-3)
    c: PointOnObject(g0,g-1)
    c: Coincident(g1,g-3)
    c: Coincident(g1,g0)
    c: Coincident(g2,g1)
    c: Coincident(g2,g0)
    c: DistanceY(g2,g2) = 3
    c: Angle(g0,g2) = 0.785398
FEATURE [PartDesign::Groove] Groove
  AddSubType = 1
  Angle = 360
  Axis = (1e-16,1,-1e-16)
  Base = (0,0,0)
  BaseFeature = -> Pocket065
  ClaimChildren = false
  Fit = 0
  FitJoin = 0
  FixShape = 1
  InnerFit = 0
  InnerFitJoin = 0
  InvalidShape = false
  NewSolid = false
  Placement = pos=(0,0,0) rot=(0.57735,0.57735,0.57735;2.0944rad)
  Profile = -> Sketch216
  ReferenceAxis = -> Y_Axis126
  Refine = true
  Reversed = true
  Suppress = false
  TreeRank = 0
  ValidateShape = true
  _ProfileBasedVersion = 0
FEATURE [PartDesign::PolarPattern] PolarPattern023
  AddSubType = 0
  Angle = 90
  Axis = -> Z_Axis126
  BaseFeature = -> Groove
  CopyShape = true
  FixShape = 1
  InvalidShape = false
  NewSolid = false
  Occurrences = 2
  OriginalSubs = -> [Groove]
  Originals = -> [Groove]
  ParallelTransform = true
  Placement = pos=(0,0,0) rot=(0.57735,0.57735,0.57735;2.0944rad)
  Refine = true
  Reversed = true
  SubTransform = true
  Suppress = false
  TreeRank = 0
  ValidateShape = true
  _Version = 0
FEATURE [Sketcher::SketchObject] Sketch217
  ArcFitTolerance = 0
  AttachmentSupport = -> [PolarPattern023]
  ExternalBSplineMaxDegree = 0
  ExternalBSplineTolerance = 0
  FixShape = 1
  FullyConstrained = true
  InternalTolerance = 1e-06
  InvalidShape = false
  MakeInternals = false
  MapMode = 5
  Placement = pos=(-2.5e-15,3e-15,-5) rot=(0.707107,0.707107,0;3.14159rad)
  Support = -> [PolarPattern023]
  TreeRank = 0
  ValidateShape = false
  sketch-geometry (1):
    g0: Circle CenterX=0 CenterY=0 CenterZ=0 NormalX=0 NormalY=0 NormalZ=1 AngleXU=0 Radius=3
  constraints (2):
    c: Coincident(g0,g-1)
    c: Diameter(g0) = 6
FEATURE [PartDesign::Pocket] Pocket066
  AddSubType = 1
  AutoTaperInnerAngle = true
  BaseFeature = -> PolarPattern023
  CheckUpToFaceLimits = true
  ClaimChildren = false
  Direction = (5e-16,-6e-16,1)
  Fit = 0
  FitJoin = 0
  FixShape = 1
  InnerFit = 0
  InnerFitJoin = 0
  InvalidShape = false
  Length = 5
  Length2 = 5
  NewSolid = false
  Placement = pos=(0,0,0) rot=(0.57735,0.57735,0.57735;2.0944rad)
  Profile = -> Sketch217
  ReferenceAxis = -> Sketch217 [N_Axis]
  Refine = true
  Suppress = false
  TaperInnerAngle = 0
  TaperInnerAngleRev = 0
  TreeRank = 0
  Type = 1
  ValidateShape = true
  _ProfileBasedVersion = 0
  _Version = 0
FEATURE [Sketcher::SketchObject] Sketch218
  ArcFitTolerance = 0
  ExternalBSplineMaxDegree = 0
  ExternalBSplineTolerance = 0
  ExternalGeometry = -> [Pocket066]
  FixShape = 1
  FullyConstrained = true
  InternalTolerance = 1e-06
  InvalidShape = false
  MakeInternals = false
  MapMode = 5
  Placement = pos=(0,0,0) rot=(0.57735,0.57735,0.57735;2.0944rad)
  TreeRank = 0
  ValidateShape = false
  sketch-geometry (5):
    g0: LineSegment StartX=-5 StartY=5 StartZ=0 EndX=-5.42979 EndY=7 EndZ=0
    g1: LineSegment StartX=-5.42979 StartY=7 StartZ=0 EndX=4.41829 EndY=8.73648 EndZ=0
    g2: LineSegment StartX=4.41829 StartY=8.73648 StartZ=0 EndX=5 EndY=5 EndZ=0
    g3: LineSegment StartX=5 StartY=5 StartZ=0 EndX=-5 EndY=5 EndZ=0
    g4: LineSegment [constr] StartX=2.1e-15 StartY=5 StartZ=0 EndX=-0.505748 EndY=7.86824 EndZ=0
  constraints (12):
    c: Coincident(g-3,g0)
    c: Coincident(g0,g1)
    c: Coincident(g1,g2)
    c: Coincident(g2,g-3)
    c: Coincident(g2,g3)
    c: Coincident(g3,g0)
    c: Distance(g1,g1) = 10
    c: Angle(g-2,g1) = 1.74533
    c: Symmetric(g3,g3,g4)
    c: Symmetric(g1,g1,g4)
    c: Perpendicular(g1,g4)
    c: DistanceY(g0,g0) = 2
FEATURE [PartDesign::Pad] Pad088
  AddSubType = 0
  AutoTaperInnerAngle = true
  BaseFeature = -> Pocket066
  CheckUpToFaceLimits = true
  ClaimChildren = false
  Direction = (1,1e-16,-1e-16)
  Fit = 0
  FitJoin = 0
  FixShape = 1
  InnerFit = 0
  InnerFitJoin = 0
  InvalidShape = false
  Length = 10
  Length2 = 10
  Midplane = true
  NewSolid = false
  Placement = pos=(0,0,0) rot=(0.57735,0.57735,0.57735;2.0944rad)
  Profile = -> Sketch218
  ReferenceAxis = -> Sketch218 [N_Axis]
  Refine = true
  Suppress = false
  TaperInnerAngle = 0
  TaperInnerAngleRev = 0
  TreeRank = 0
  Type = 0
  ValidateShape = true
  _ProfileBasedVersion = 0
FEATURE [Sketcher::SketchObject] Sketch219
  ArcFitTolerance = 0
  ExternalBSplineMaxDegree = 0
  ExternalBSplineTolerance = 0
  ExternalGeometry = -> [Pad088]
  FixShape = 1
  FullyConstrained = true
  InternalTolerance = 1e-06
  InvalidShape = false
  MakeInternals = false
  MapMode = 5
  Placement = pos=(0,0,0) rot=(0.57735,0.57735,0.57735;2.0944rad)
  TreeRank = 0
  ValidateShape = false
  sketch-geometry (8):
    g0: LineSegment [constr] StartX=-0.505748 StartY=7.86824 StartZ=0 EndX=-1.3e-15 EndY=5 EndZ=0
    g1: LineSegment StartX=-0.505748 StartY=7.86824 StartZ=0 EndX=0.971463 EndY=8.12871 EndZ=0
    g2: LineSegment StartX=0.971463 StartY=8.12871 StartZ=0 EndX=1.13419 EndY=7.20583 EndZ=0
    g3: LineSegment StartX=1.13419 StartY=7.20583 StartZ=0 EndX=2.81908 EndY=6.02606 EndZ=0
    g4: LineSegment StartX=2.81908 StartY=6.02606 StartZ=0 EndX=3 EndY=5 EndZ=0
    g5: LineSegment StartX=3 StartY=5 StartZ=0 EndX=0.0904611 EndY=4.48697 EndZ=0
    g6: LineSegment StartX=0.0904611 StartY=4.48697 StartZ=0 EndX=-0.505748 EndY=7.86824 EndZ=0
    g7: LineSegment [constr] StartX=-3 StartY=5 StartZ=0 EndX=2.81908 EndY=6.02606 EndZ=0
  constraints (20):
    c: Symmetric(g-4,g-4,g0)
    c: Symmetric(g-3,g-3,g0)
    c: Coincident(g0,g1)
    c: PointOnObject(g1,g-4)
    c: Coincident(g1,g2)
    c: Coincident(g2,g3)
    c: Coincident(g3,g4)
    c: Coincident(g4,g-3)
    c: Coincident(g4,g5)
    c: Coincident(g5,g6)
    c: Coincident(g6,g1)
    c: Perpendicular(g6,g5)
    c: Angle(g3,g5) = 0.785398
    c: Perpendicular(g1,g2)
    c: Distance(g1,g1) = 1.5
    c: PointOnObject(g0,g6)
    c: Perpendicular(g5,g4)
    c: Coincident(g7,g-3)
    c: Coincident(g7,g3)
    c: Perpendicular(g4,g7)
FEATURE [Sketcher::SketchObject] Sketch221
  ArcFitTolerance = 0
  ExternalBSplineMaxDegree = 0
  ExternalBSplineTolerance = 0
  FixShape = 1
  FullyConstrained = true
  InternalTolerance = 1e-06
  InvalidShape = false
  MakeInternals = false
  MapMode = 5
  Placement = pos=(0,0,0) rot=(0.57735,0.57735,0.57735;2.0944rad)
  TreeRank = 0
  ValidateShape = false
  sketch-geometry (5):
    g0: LineSegment StartX=-5 StartY=-5 StartZ=0 EndX=5 EndY=-5 EndZ=0
    g1: LineSegment StartX=5 StartY=-5 StartZ=0 EndX=5 EndY=5 EndZ=0
    g2: LineSegment StartX=5 StartY=5 StartZ=0 EndX=-5 EndY=5 EndZ=0
    g3: LineSegment StartX=-5 StartY=5 StartZ=0 EndX=-5 EndY=-5 EndZ=0
    g4: GeomPoint [constr] X=0 Y=0 Z=0
  constraints (12):
    c: Coincident(g0,g1)
    c: Coincident(g1,g2)
    c: Coincident(g2,g3)
    c: Coincident(g3,g0)
    c: Horizontal(g0)
    c: Horizontal(g2)
    c: Vertical(g1)
    c: Vertical(g3)
    c: Symmetric(g2,g0,g4)
    c: Coincident(g4,g-1)
    c: Equal(g1,g2)
    c: DistanceX(g2,g2) = 10
FEATURE [PartDesign::Pad] Pad090
  AddSubType = 0
  AutoTaperInnerAngle = true
  CheckUpToFaceLimits = true
  ClaimChildren = false
  Direction = (1,1e-16,-1e-16)
  Fit = 0
  FitJoin = 0
  FixShape = 1
  InnerFit = 0
  InnerFitJoin = 0
  InvalidShape = false
  Length = 10
  Length2 = 10
  Midplane = true
  NewSolid = false
  Placement = pos=(0,0,0) rot=(0.57735,0.57735,0.57735;2.0944rad)
  Profile = -> Sketch221
  ReferenceAxis = -> Sketch221 [N_Axis]
  Refine = true
  Suppress = false
  TaperInnerAngle = 0
  TaperInnerAngleRev = 0
  TreeRank = 0
  Type = 0
  ValidateShape = true
  _ProfileBasedVersion = 0
FEATURE [Sketcher::SketchObject] Sketch222
  ArcFitTolerance = 0
  ExternalBSplineMaxDegree = 0
  ExternalBSplineTolerance = 0
  FixShape = 1
  FullyConstrained = true
  InternalTolerance = 1e-06
  InvalidShape = false
  MakeInternals = false
  MapMode = 5
  Placement = pos=(0,0,0) rot=(0.57735,0.57735,0.57735;2.0944rad)
  TreeRank = 0
  ValidateShape = false
  sketch-geometry (1):
    g0: Circle CenterX=0 CenterY=0 CenterZ=0 NormalX=0 NormalY=0 NormalZ=1 AngleXU=0 Radius=1.5
  constraints (2):
    c: Coincident(g0,g-1)
    c: Diameter(g0) = 3
FEATURE [PartDesign::Pocket] Pocket067
  AddSubType = 1
  AutoTaperInnerAngle = true
  BaseFeature = -> Pad090
  CheckUpToFaceLimits = true
  ClaimChildren = false
  Direction = (-1,-1e-16,1e-16)
  Fit = 0
  FitJoin = 0
  FixShape = 1
  InnerFit = 0
  InnerFitJoin = 0
  InvalidShape = false
  Length = 5
  Length2 = 5
  Midplane = true
  NewSolid = false
  Placement = pos=(0,0,0) rot=(0.57735,0.57735,0.57735;2.0944rad)
  Profile = -> Sketch222
  ReferenceAxis = -> Sketch222 [N_Axis]
  Refine = true
  Suppress = false
  TaperInnerAngle = 0
  TaperInnerAngleRev = 0
  TreeRank = 0
  Type = 1
  ValidateShape = true
  _ProfileBasedVersion = 0
  _Version = 0
FEATURE [Sketcher::SketchObject] Sketch223
  ArcFitTolerance = 0
  ExternalBSplineMaxDegree = 0
  ExternalBSplineTolerance = 0
  FixShape = 1
  FullyConstrained = true
  InternalTolerance = 1e-06
  InvalidShape = false
  MakeInternals = false
  MapMode = 5
  TreeRank = 0
  ValidateShape = false
  sketch-geometry (1):
    g0: Circle CenterX=0 CenterY=0 CenterZ=0 NormalX=0 NormalY=0 NormalZ=1 AngleXU=0 Radius=1.5
  constraints (2):
    c: Coincident(g0,g-1)
    c: Diameter(g0) = 3
FEATURE [PartDesign::Pocket] Pocket068
  AddSubType = 1
  AutoTaperInnerAngle = true
  BaseFeature = -> Pocket067
  CheckUpToFaceLimits = true
  ClaimChildren = false
  Direction = (0,0,-1)
  Fit = 0
  FitJoin = 0
  FixShape = 1
  InnerFit = 0
  InnerFitJoin = 0
  InvalidShape = false
  Length = 5
  Length2 = 5
  Midplane = true
  NewSolid = false
  Placement = pos=(0,0,0) rot=(0.57735,0.57735,0.57735;2.0944rad)
  Profile = -> Sketch223
  ReferenceAxis = -> Sketch223 [N_Axis]
  Refine = true
  Suppress = false
  TaperInnerAngle = 0
  TaperInnerAngleRev = 0
  TreeRank = 0
  Type = 1
  ValidateShape = true
  _ProfileBasedVersion = 0
  _Version = 0
FEATURE [Sketcher::SketchObject] Sketch224
  ArcFitTolerance = 0
  ExternalBSplineMaxDegree = 0
  ExternalBSplineTolerance = 0
  ExternalGeometry = -> [Pocket068]
  FixShape = 1
  FullyConstrained = true
  InternalTolerance = 1e-06
  InvalidShape = false
  MakeInternals = false
  MapMode = 5
  Placement = pos=(0,0,0) rot=(0.57735,0.57735,0.57735;2.0944rad)
  TreeRank = 0
  ValidateShape = false
  sketch-geometry (6):
    g0: LineSegment StartX=5 StartY=-5 StartZ=0 EndX=5 EndY=5 EndZ=0
    g1: LineSegment StartX=5 StartY=5 StartZ=0 EndX=20.4122 EndY=5 EndZ=0
    g2: LineSegment StartX=20.4122 StartY=5 StartZ=0 EndX=22.3228 EndY=-5.83584 EndZ=0
    g3: LineSegment StartX=22.3228 StartY=-5.83584 StartZ=0 EndX=12.4748 EndY=-7.57232 EndZ=0
    g4: LineSegment StartX=12.4748 StartY=-7.57232 StartZ=0 EndX=12.0212 EndY=-5 EndZ=0
    g5: LineSegment StartX=12.0212 StartY=-5 StartZ=0 EndX=5 EndY=-5 EndZ=0
  constraints (16):
    c: Coincident(g-3,g0)
    c: Coincident(g0,g-3)
    c: Coincident(g0,g1)
    c: Horizontal(g1)
    c: Coincident(g1,g2)
    c: Coincident(g2,g3)
    c: Coincident(g3,g4)
    c: Coincident(g4,g5)
    c: Coincident(g5,g0)
    c: Horizontal(g5)
    c: Distance(g3,g3) = 10
    c: Perpendicular(g3,g2)
    c: Perpendicular(g3,g4)
    c: Angle(g5,g4) = 1.74533
    c: Distance(g3,g0) = 7.905
    c: Distance(g0,g2) = 17.343
FEATURE [PartDesign::Pad] Pad091
  AddSubType = 0
  AutoTaperInnerAngle = true
  BaseFeature = -> Pocket068
  CheckUpToFaceLimits = true
  ClaimChildren = false
  Direction = (1,1e-16,-1e-16)
  Fit = 0
  FitJoin = 0
  FixShape = 1
  InnerFit = 0
  InnerFitJoin = 0
  InvalidShape = false
  Length = 10
  Length2 = 10
  Midplane = true
  NewSolid = false
  Placement = pos=(0,0,0) rot=(0.57735,0.57735,0.57735;2.0944rad)
  Profile = -> Sketch224
  ReferenceAxis = -> Sketch224 [N_Axis]
  Refine = true
  Suppress = false
  TaperInnerAngle = 0
  TaperInnerAngleRev = 0
  TreeRank = 0
  Type = 0
  ValidateShape = true
  _ProfileBasedVersion = 0
FEATURE [Sketcher::SketchObject] Sketch225
  ArcFitTolerance = 0
  ExternalBSplineMaxDegree = 0
  ExternalBSplineTolerance = 0
  ExternalGeometry = -> [Pad091]
  FixShape = 1
  FullyConstrained = true
  InternalTolerance = 1e-06
  InvalidShape = false
  MakeInternals = false
  MapMode = 5
  Placement = pos=(0,0,0) rot=(0.57735,0.57735,0.57735;2.0944rad)
  TreeRank = 0
  ValidateShape = false
  sketch-geometry (7):
    g0: LineSegment [constr] StartX=15.3351 StartY=5 StartZ=0 EndX=17.3988 EndY=-6.70408 EndZ=0
    g1: LineSegment StartX=15.9216 StartY=-6.96456 StartZ=0 EndX=17.3988 EndY=-6.70408 EndZ=0
    g2: LineSegment StartX=17.3988 StartY=-6.70408 StartZ=0 EndX=15.2371 EndY=5.55567 EndZ=0
    g3: LineSegment StartX=15.2371 StartY=5.55567 StartZ=0 EndX=12.0857 EndY=5 EndZ=0
    g4: LineSegment StartX=12.0857 StartY=5 StartZ=0 EndX=13.6049 EndY=-3.61597 EndZ=0
    g5: LineSegment StartX=13.6049 StartY=-3.61597 StartZ=0 EndX=15.5743 EndY=-4.99494 EndZ=0
    g6: LineSegment StartX=15.5743 StartY=-4.99494 StartZ=0 EndX=15.9216 EndY=-6.96456 EndZ=0
  constraints (20):
    c: PointOnObject(g0,g-4)
    c: Symmetric(g-3,g-3,g0)
    c: Perpendicular(g-3,g0)
    c: PointOnObject(g1,g-3)
    c: Coincident(g1,g0)
    c: Coincident(g1,g2)
    c: Coincident(g2,g3)
    c: Coincident(g3,g4)
    c: Coincident(g4,g5)
    c: Coincident(g5,g6)
    c: Coincident(g6,g1)
    c: Perpendicular(g6,g1)
    c: Distance(g1,g1) = 1.5
    c: Distance(g6,g6) = 2
    c: Angle(g6,g5) = 0.785398
    c: Perpendicular(g4,g3)
    c: Distance(g3,g3) = 3.2
    c: PointOnObject(g0,g2)
    c: Perpendicular(g2,g3)
    c: PointOnObject(g3,g-4)
FEATURE [PartDesign::Groove] Groove002
  AddSubType = 1
  Angle = 360
  Axis = (-1.5e-15,2.06375,-11.7041)
  Base = (-1.1e-15,15.3351,5)
  BaseFeature = -> Pad091
  ClaimChildren = false
  Fit = 0
  FitJoin = 0
  FixShape = 1
  InnerFit = 0
  InnerFitJoin = 0
  InvalidShape = false
  NewSolid = false
  Placement = pos=(0,0,0) rot=(0.57735,0.57735,0.57735;2.0944rad)
  Profile = -> Sketch225
  ReferenceAxis = -> Sketch225 [Axis]
  Refine = true
  Suppress = false
  TreeRank = 0
  ValidateShape = true
  _ProfileBasedVersion = 0
FEATURE [Sketcher::SketchObject] Sketch226
  ArcFitTolerance = 0
  AttachmentSupport = -> [Groove002]
  ExternalBSplineMaxDegree = 0
  ExternalBSplineTolerance = 0
  FixShape = 1
  FullyConstrained = true
  InternalTolerance = 1e-06
  InvalidShape = false
  MakeInternals = false
  MapMode = 5
  Placement = pos=(3.5e-15,-1.9e-15,5) rot=(0,0,-1;1.5708rad)
  Support = -> [Groove002]
  TreeRank = 0
  ValidateShape = false
  sketch-geometry (1):
    g0: Circle CenterX=0 CenterY=0 CenterZ=0 NormalX=0 NormalY=0 NormalZ=1 AngleXU=0 Radius=3.2
  constraints (2):
    c: Coincident(g0,g-1)
    c: Diameter(g0) = 6.4
FEATURE [PartDesign::Pocket] Pocket069
  AddSubType = 1
  AutoTaperInnerAngle = true
  BaseFeature = -> Groove002
  CheckUpToFaceLimits = true
  ClaimChildren = false
  Direction = (-7e-16,4e-16,-1)
  Fit = 0
  FitJoin = 0
  FixShape = 1
  InnerFit = 0
  InnerFitJoin = 0
  InvalidShape = false
  Length = 8
  Length2 = 5
  NewSolid = false
  Placement = pos=(0,0,0) rot=(0.57735,0.57735,0.57735;2.0944rad)
  Profile = -> Sketch226
  ReferenceAxis = -> Sketch226 [N_Axis]
  Refine = true
  Suppress = false
  TaperInnerAngle = 0
  TaperInnerAngleRev = 0
  TreeRank = 0
  Type = 0
  ValidateShape = true
  _ProfileBasedVersion = 0
  _Version = 0
FEATURE [Sketcher::SketchObject] Sketch227
  ArcFitTolerance = 0
  AttachmentSupport = -> [Pocket069]
  ExternalBSplineMaxDegree = 0
  ExternalBSplineTolerance = 0
  FixShape = 1
  FullyConstrained = true
  InternalTolerance = 1e-06
  InvalidShape = false
  MakeInternals = false
  MapMode = 5
  Placement = pos=(5,1.02e-14,-4.9e-15) rot=(0.57735,0.57735,0.57735;2.0944rad)
  Support = -> [Pocket069]
  TreeRank = 0
  ValidateShape = false
  sketch-geometry (1):
    g0: Circle CenterX=0 CenterY=0 CenterZ=0 NormalX=0 NormalY=0 NormalZ=1 AngleXU=0 Radius=3.2
  constraints (2):
    c: Coincident(g0,g-1)
    c: Diameter(g0) = 6.4
FEATURE [PartDesign::Pocket] Pocket070
  AddSubType = 1
  AutoTaperInnerAngle = true
  BaseFeature = -> Pocket069
  CheckUpToFaceLimits = true
  ClaimChildren = false
  Direction = (-1,-1.9e-15,8e-16)
  Fit = 0
  FitJoin = 0
  FixShape = 1
  InnerFit = 0
  InnerFitJoin = 0
  InvalidShape = false
  Length = 8
  Length2 = 5
  NewSolid = false
  Placement = pos=(0,0,0) rot=(0.57735,0.57735,0.57735;2.0944rad)
  Profile = -> Sketch227
  ReferenceAxis = -> Sketch227 [N_Axis]
  Refine = true
  Suppress = false
  TaperInnerAngle = 0
  TaperInnerAngleRev = 0
  TreeRank = 0
  Type = 0
  ValidateShape = true
  _ProfileBasedVersion = 0
  _Version = 0
FEATURE [Sketcher::SketchObject] Sketch228
  ArcFitTolerance = 0
  ExternalBSplineMaxDegree = 0
  ExternalBSplineTolerance = 0
  ExternalGeometry = -> [Pocket070]
  FixShape = 1
  FullyConstrained = true
  InternalTolerance = 1e-06
  InvalidShape = false
  MakeInternals = false
  MapMode = 5
  Placement = pos=(0,0,0) rot=(0.57735,0.57735,0.57735;2.0944rad)
  TreeRank = 0
  ValidateShape = false
  sketch-geometry (5):
    g0: LineSegment StartX=-1.5 StartY=-5 StartZ=0 EndX=-1.5 EndY=-4.7 EndZ=0
    g1: LineSegment StartX=-1.5 StartY=-4.7 StartZ=0 EndX=-3.2 EndY=-3 EndZ=0
    g2: LineSegment StartX=-3.2 StartY=-3 StartZ=0 EndX=0 EndY=-3 EndZ=0
    g3: LineSegment StartX=0 StartY=-3 StartZ=0 EndX=0 EndY=-5 EndZ=0
    g4: LineSegment StartX=0 StartY=-5 StartZ=0 EndX=-1.5 EndY=-5 EndZ=0
  constraints (13):
    c: Coincident(g0,g-3)
    c: Coincident(g1,g0)
    c: PointOnObject(g2,g-2)
    c: Horizontal(g2)
    c: Coincident(g3,g2)
    c: PointOnObject(g3,g-3)
    c: Vertical(g3)
    c: Coincident(g4,g3)
    c: Coincident(g4,g0)
    c: Vertical(g0)
    c: Coincident(g1,g2)
    c: Angle(g1,g2) = 0.785398
    c: Coincident(g1,g-4)
FEATURE [PartDesign::Groove] Groove003
  AddSubType = 1
  Angle = 360
  Axis = (1e-16,1e-16,1)
  Base = (0,0,0)
  BaseFeature = -> Pocket070
  ClaimChildren = false
  Fit = 0
  FitJoin = 0
  FixShape = 1
  InnerFit = 0
  InnerFitJoin = 0
  InvalidShape = false
  NewSolid = false
  Placement = pos=(0,0,0) rot=(0.57735,0.57735,0.57735;2.0944rad)
  Profile = -> Sketch228
  ReferenceAxis = -> Z_Axis132
  Refine = true
  Reversed = true
  Suppress = false
  TreeRank = 0
  ValidateShape = true
  _ProfileBasedVersion = 0
FEATURE [PartDesign::PolarPattern] PolarPattern024
  AddSubType = 0
  Angle = 90
  Axis = -> Y_Axis132
  BaseFeature = -> Groove003
  CopyShape = true
  FixShape = 1
  InvalidShape = false
  NewSolid = false
  Occurrences = 2
  OriginalSubs = -> [Groove003]
  Originals = -> [Groove003]
  ParallelTransform = true
  Placement = pos=(0,0,0) rot=(0.57735,0.57735,0.57735;2.0944rad)
  Refine = true
  SubTransform = true
  Suppress = false
  TreeRank = 0
  ValidateShape = true
  _Version = 0
FEATURE [PartDesign::Chamfer] Chamfer049
  AddSubType = 0
  Angle = 45
  Base = -> PolarPattern024 [Edge11,Edge6,Edge1,Edge2]
  BaseFeature = -> PolarPattern024
  ChamferType = 0
  FixShape = 1
  FlipDirection = false
  InvalidShape = false
  NewSolid = false
  Placement = pos=(0,0,0) rot=(0.57735,0.57735,0.57735;2.0944rad)
  Refine = true
  Size = 1
  Size2 = 1
  SupportTransform = false
  Suppress = false
  TreeRank = 0
  UseAllEdges = false
  ValidateShape = true
FEATURE [Sketcher::SketchObject] Sketch229
  ArcFitTolerance = 0
  AttachmentSupport = -> [Chamfer049]
  ExternalBSplineMaxDegree = 0
  ExternalBSplineTolerance = 0
  ExternalGeometry = -> [Chamfer049]
  FixShape = 1
  FullyConstrained = true
  InternalTolerance = 1e-06
  InvalidShape = false
  MakeInternals = false
  MapMode = 5
  Placement = pos=(5,1.46e-14,-6.5e-15) rot=(0.57735,0.57735,0.57735;2.0944rad)
  Support = -> [Chamfer049]
  TreeRank = 0
  ValidateShape = false
  sketch-geometry (11):
    g0: LineSegment StartX=23.2045 StartY=-10.8358 StartZ=0 EndX=20.5858 EndY=4.01519 EndZ=0
    g1: LineSegment StartX=20.5858 StartY=4.01519 StartZ=0 EndX=19.4122 EndY=5 EndZ=0
    g2: LineSegment StartX=19.4122 StartY=5 StartZ=0 EndX=-4 EndY=5 EndZ=0
    g3: LineSegment StartX=-4 StartY=5 StartZ=0 EndX=-5 EndY=4 EndZ=0
    g4: LineSegment StartX=-5 StartY=4 StartZ=0 EndX=-5 EndY=-13.3034 EndZ=0
    g5: LineSegment StartX=-5 StartY=-13.3034 StartZ=0 EndX=23.2045 EndY=-10.8358 EndZ=0
    g6: LineSegment [constr] StartX=23.2045 StartY=-10.8358 StartZ=0 EndX=-5 EndY=-10.8358 EndZ=0
    g7: LineSegment [constr] StartX=-5 StartY=-13.3034 StartZ=0 EndX=22.776 EndY=-8.40576 EndZ=0
    g8: LineSegment [constr] StartX=22.776 StartY=-8.40576 StartZ=0 EndX=23.2045 EndY=-10.8358 EndZ=0
    g9: LineSegment [constr] StartX=-5 StartY=-10.8358 StartZ=0 EndX=-5 EndY=-13.3034 EndZ=0
    g10: Circle CenterX=0 CenterY=0 CenterZ=0 NormalX=0 NormalY=0 NormalZ=1 AngleXU=0 Radius=3
  constraints (26):
    c: Coincident(g0,g-4)
    c: Coincident(g0,g1)
    c: Coincident(g1,g-5)
    c: Coincident(g1,g2)
    c: Coincident(g2,g-6)
    c: Coincident(g2,g3)
    c: Coincident(g3,g-7)
    c: Coincident(g3,g4)
    c: Vertical(g4)
    c: Coincident(g4,g5)
    c: Coincident(g5,g0)
    c: PointOnObject(g-3,g0)
    c: Coincident(g0,g6)
    c: PointOnObject(g6,g4)
    c: Horizontal(g6)
    c: Coincident(g4,g7)
    c: PointOnObject(g7,g0)
    c: Perpendicular(g7,g0)
    c: Coincident(g7,g8)
    c: Coincident(g8,g0)
    c: Coincident(g6,g9)
    c: Coincident(g9,g4)
    c: Equal(g8,g9)
    c: DistanceY(g0,g-3) = 5
    c: Coincident(g10,g-1)
    c: Diameter(g10) = 6
FEATURE [PartDesign::Pad] Pad092
  AddSubType = 0
  AutoTaperInnerAngle = true
  BaseFeature = -> Chamfer049
  CheckUpToFaceLimits = true
  ClaimChildren = false
  Direction = (1,2.8e-15,-1.3e-15)
  Fit = 0
  FitJoin = 0
  FixShape = 1
  InnerFit = 0
  InnerFitJoin = 0
  InvalidShape = false
  Length = 3
  Length2 = 10
  NewSolid = false
  Placement = pos=(0,0,0) rot=(0.57735,0.57735,0.57735;2.0944rad)
  Profile = -> Sketch229
  ReferenceAxis = -> Sketch229 [N_Axis]
  Refine = true
  Suppress = false
  TaperInnerAngle = 0
  TaperInnerAngleRev = 0
  TreeRank = 0
  Type = 0
  ValidateShape = true
  _ProfileBasedVersion = 0
FEATURE [PartDesign::Chamfer] Chamfer050
  AddSubType = 0
  Angle = 45
  Base = -> Pad092 [Edge53,Edge52]
  BaseFeature = -> Pad092
  ChamferType = 0
  FixShape = 1
  FlipDirection = false
  InvalidShape = false
  NewSolid = false
  Placement = pos=(0,0,0) rot=(0.57735,0.57735,0.57735;2.0944rad)
  Refine = true
  Size = 1
  Size2 = 1
  SupportTransform = false
  Suppress = false
  TreeRank = 0
  UseAllEdges = false
  ValidateShape = true
FEATURE [Sketcher::SketchObject] Sketch230
  ArcFitTolerance = 0
  ExternalBSplineMaxDegree = 0
  ExternalBSplineTolerance = 0
  FixShape = 1
  FullyConstrained = true
  InternalTolerance = 1e-06
  InvalidShape = false
  MakeInternals = false
  MapMode = 5
  Placement = pos=(0,0,0) rot=(1,0,0;1.5708rad)
  TreeRank = 0
  ValidateShape = false
  sketch-geometry (1):
    g0: Circle CenterX=0 CenterY=0 CenterZ=0 NormalX=0 NormalY=0 NormalZ=1 AngleXU=0 Radius=13.9
  constraints (2):
    c: Coincident(g0,g-1)
    c: Diameter(g0) = 27.8
FEATURE [PartDesign::Pad] Pad093
  AddSubType = 0
  AutoTaperInnerAngle = true
  CheckUpToFaceLimits = true
  ClaimChildren = false
  Direction = (0,-1,0)
  Fit = 0
  FitJoin = 0
  FixShape = 1
  InnerFit = 0
  InnerFitJoin = 0
  InvalidShape = false
  Length = 9
  Length2 = 10
  NewSolid = false
  Placement = pos=(0,0,0) rot=(1,0,0;1.5708rad)
  Profile = -> Sketch230
  ReferenceAxis = -> Sketch230 [N_Axis]
  Refine = true
  Reversed = true
  Suppress = false
  TaperInnerAngle = 0
  TaperInnerAngleRev = 0
  TreeRank = 0
  Type = 0
  ValidateShape = true
  _ProfileBasedVersion = 0
FEATURE [Sketcher::SketchObject] Sketch231
  ArcFitTolerance = 0
  AttachmentSupport = -> [Pad093]
  ExternalBSplineMaxDegree = 0
  ExternalBSplineTolerance = 0
  FixShape = 1
  FullyConstrained = true
  InternalTolerance = 1e-06
  InvalidShape = false
  MakeInternals = false
  MapMode = 5
  Placement = pos=(0,0,0) rot=(1,0,0;1.5708rad)
  Support = -> [Pad093]
  TreeRank = 0
  ValidateShape = false
  sketch-geometry (1):
    g0: Circle CenterX=0 CenterY=10.5 CenterZ=0 NormalX=0 NormalY=0 NormalZ=1 AngleXU=0 Radius=2.1
  constraints (3):
    c: PointOnObject(g0,g-2)
    c: DistanceY(g-1,g0) = 10.5
    c: Diameter(g0) = 4.2
FEATURE [PartDesign::Pocket] Pocket071
  AddSubType = 1
  AutoTaperInnerAngle = true
  BaseFeature = -> Pad093
  CheckUpToFaceLimits = true
  ClaimChildren = false
  Direction = (0,1,2e-16)
  Fit = 0
  FitJoin = 0
  FixShape = 1
  InnerFit = 0
  InnerFitJoin = 0
  InvalidShape = false
  Length = 5
  Length2 = 5
  NewSolid = false
  Placement = pos=(0,0,0) rot=(1,0,0;1.5708rad)
  Profile = -> Sketch231
  ReferenceAxis = -> Sketch231 [N_Axis]
  Refine = true
  Suppress = false
  TaperInnerAngle = 0
  TaperInnerAngleRev = 0
  TreeRank = 0
  Type = 1
  ValidateShape = true
  _ProfileBasedVersion = 0
  _Version = 0
FEATURE [PartDesign::PolarPattern] PolarPattern025
  AddSubType = 0
  Angle = 360
  Axis = -> Y_Axis134
  BaseFeature = -> Pocket071
  CopyShape = true
  FixShape = 1
  InvalidShape = false
  NewSolid = false
  Occurrences = 6
  OriginalSubs = -> [Pocket071]
  Originals = -> [Pocket071]
  ParallelTransform = true
  Placement = pos=(0,0,0) rot=(1,0,0;1.5708rad)
  Refine = true
  SubTransform = true
  Suppress = false
  TreeRank = 0
  ValidateShape = true
  _Version = 0
FEATURE [Sketcher::SketchObject] Sketch232
  ArcFitTolerance = 0
  ExternalBSplineMaxDegree = 0
  ExternalBSplineTolerance = 0
  FixShape = 1
  FullyConstrained = true
  InternalTolerance = 1e-06
  InvalidShape = false
  MakeInternals = false
  MapMode = 5
  Placement = pos=(0,0,0) rot=(1,0,0;1.5708rad)
  TreeRank = 0
  ValidateShape = false
  sketch-geometry (1):
    g0: Circle CenterX=0 CenterY=0 CenterZ=0 NormalX=0 NormalY=0 NormalZ=1 AngleXU=0 Radius=2.5
  constraints (2):
    c: Coincident(g0,g-1)
    c: Diameter(g0) = 5
FEATURE [PartDesign::Pocket] Pocket072
  AddSubType = 1
  AutoTaperInnerAngle = true
  BaseFeature = -> PolarPattern025
  CheckUpToFaceLimits = true
  ClaimChildren = false
  Direction = (0,1,0)
  Fit = 0
  FitJoin = 0
  FixShape = 1
  InnerFit = 0
  InnerFitJoin = 0
  InvalidShape = false
  Length = 5
  Length2 = 5
  NewSolid = false
  Placement = pos=(0,0,0) rot=(1,0,0;1.5708rad)
  Profile = -> Sketch232
  ReferenceAxis = -> Sketch232 [N_Axis]
  Refine = true
  Suppress = false
  TaperInnerAngle = 0
  TaperInnerAngleRev = 0
  TreeRank = 0
  Type = 1
  ValidateShape = true
  _ProfileBasedVersion = 0
  _Version = 0
FEATURE [Sketcher::SketchObject] Sketch233
  ArcFitTolerance = 0
  ExternalBSplineMaxDegree = 0
  ExternalBSplineTolerance = 0
  ExternalGeometry = -> [Pocket072]
  FixShape = 1
  FullyConstrained = true
  InternalTolerance = 1e-06
  InvalidShape = false
  MakeInternals = false
  MapMode = 5
  Placement = pos=(0,0,0) rot=(1,0,0;1.5708rad)
  TreeRank = 0
  ValidateShape = false
  sketch-geometry (2):
    g0: LineSegment StartX=12.9696 StartY=5 StartZ=0 EndX=12.9696 EndY=-5 EndZ=0
    g1: ArcOfCircle CenterX=0 CenterY=0 CenterZ=0 NormalX=0 NormalY=0 NormalZ=1 AngleXU=0 Radius=13.9 StartAngle=5.91523 EndAngle=6.65114
  constraints (6):
    c: PointOnObject(g0,g-3)
    c: Vertical(g0)
    c: Coincident(g1,g-1)
    c: Coincident(g1,g0)
    c: Coincident(g1,g0)
    c: DistanceY(g0,g0) = 10
FEATURE [PartDesign::Pocket] Pocket073
  AddSubType = 1
  AutoTaperInnerAngle = true
  BaseFeature = -> Pocket072
  CheckUpToFaceLimits = true
  ClaimChildren = false
  Direction = (0,1,0)
  Fit = 0
  FitJoin = 0
  FixShape = 1
  InnerFit = 0
  InnerFitJoin = 0
  InvalidShape = false
  Length = 5
  Length2 = 5
  NewSolid = false
  Placement = pos=(0,0,0) rot=(1,0,0;1.5708rad)
  Profile = -> Sketch233
  ReferenceAxis = -> Sketch233 [N_Axis]
  Refine = true
  Suppress = false
  TaperInnerAngle = 0
  TaperInnerAngleRev = 0
  TreeRank = 0
  Type = 1
  ValidateShape = true
  _ProfileBasedVersion = 0
  _Version = 0
FEATURE [Sketcher::SketchObject] Sketch234
  ArcFitTolerance = 0
  AttachmentSupport = -> [Pocket073]
  ExternalBSplineMaxDegree = 0
  ExternalBSplineTolerance = 0
  ExternalGeometry = -> [Pocket073]
  FixShape = 1
  FullyConstrained = true
  InternalTolerance = 1e-06
  InvalidShape = false
  MakeInternals = false
  MapMode = 5
  Placement = pos=(12.9696,0,0) rot=(0.707107,0,0.707107;3.14159rad)
  Support = -> [Pocket073]
  TreeRank = 0
  ValidateShape = false
  sketch-geometry (2):
    g0: Circle CenterX=-5.2e-15 CenterY=-4.5 CenterZ=0 NormalX=0 NormalY=0 NormalZ=1 AngleXU=0 Radius=2.1
    g1: LineSegment [constr] StartX=-1.03e-14 StartY=-9 StartZ=0 EndX=0 EndY=0 EndZ=0
  constraints (4):
    c: Diameter(g0) = 4.2
    c: Symmetric(g-3,g-3,g1)
    c: Coincident(g1,g-1)
    c: Symmetric(g1,g1,g0)
FEATURE [PartDesign::Pocket] Pocket074
  AddSubType = 1
  AutoTaperInnerAngle = true
  BaseFeature = -> Pocket073
  CheckUpToFaceLimits = true
  ClaimChildren = false
  Direction = (-1,0,2e-16)
  Fit = 0
  FitJoin = 0
  FixShape = 1
  InnerFit = 0
  InnerFitJoin = 0
  InvalidShape = false
  Length = 13
  Length2 = 5
  NewSolid = false
  Placement = pos=(0,0,0) rot=(1,0,0;1.5708rad)
  Profile = -> Sketch234
  ReferenceAxis = -> Sketch234 [N_Axis]
  Refine = true
  Suppress = false
  TaperInnerAngle = 0
  TaperInnerAngleRev = 0
  TreeRank = 0
  Type = 0
  ValidateShape = true
  _ProfileBasedVersion = 0
  _Version = 0
FEATURE [PartDesign::Chamfer] Chamfer052
  AddSubType = 0
  Angle = 45
  Base = -> Pocket074 [Face4,Face2]
  BaseFeature = -> Pocket074
  ChamferType = 0
  FixShape = 1
  FlipDirection = false
  InvalidShape = false
  NewSolid = false
  Placement = pos=(0,0,0) rot=(1,0,0;1.5708rad)
  Refine = true
  Size = 0.4
  Size2 = 1
  SupportTransform = false
  Suppress = false
  TreeRank = 0
  UseAllEdges = false
  ValidateShape = true
FEATURE [PartDesign::Chamfer] Chamfer053
  AddSubType = 0
  Angle = 45
  Base = -> Chamfer052 [Edge7]
  BaseFeature = -> Chamfer052
  ChamferType = 0
  FixShape = 1
  FlipDirection = false
  InvalidShape = false
  NewSolid = false
  Placement = pos=(0,0,0) rot=(1,0,0;1.5708rad)
  Refine = true
  Size = 0.8
  Size2 = 1
  SupportTransform = false
  Suppress = false
  TreeRank = 0
  UseAllEdges = false
  ValidateShape = true
FEATURE [PartDesign::Body] Body110  label="NoyauRoue"
  AutoGroupSolids = false
  ClaimAllChildren = false
  ExportMode = 0
  FixShape = 1
  Group = -> [Sketch230,Pad093,Sketch231,Pocket071,PolarPattern025,Sketch232,Pocket072,Sketch233,Pocket073,Sketch234,Pocket074,Chamfer052,Chamfer053]
  InvalidShape = false
  Origin = -> Origin211
  Placement = pos=(3e-15,1.25,0) rot=(0,0,1;0rad)
  SingleSolid = true
  Tip = -> Chamfer053
  TreeRank = 0
  ValidateShape = false
  _ExportChildren = -> [Pad093,Pocket071,PolarPattern025,Pocket072,Pocket073,Pocket074,Chamfer052,Chamfer053]
  _GroupVersion = 1
FEATURE [Part::FeaturePython] Insert001  label="M3x5.74-Insert"  # Fasteners workbench fastener (typed FeaturePython)
  FixShape = 1
  InvalidShape = false
  Placement = pos=(-9.09327,1.25,-5.25) rot=(1,0,0;1.5708rad)
  TreeRank = 0
  ValidateShape = false
  baseObject = -> Body110 [Edge22]
  diameter = 3
  externalDiam = 4.55
  invert = false
  leftHanded = false
  length = 5.74
  matchOuter = false
  offset = 0
  thread = false
  type = 0
FEATURE [Part::FeaturePython] Insert002  label="M3x5.74-Insert001"  # Fasteners workbench fastener (typed FeaturePython)
  FixShape = 1
  InvalidShape = false
  Placement = pos=(3e-15,1.25,10.5) rot=(1,0,0;1.5708rad)
  TreeRank = 0
  ValidateShape = false
  baseObject = -> Body110 [Edge27]
  diameter = 3
  externalDiam = 4.55
  invert = false
  leftHanded = false
  length = 5.74
  matchOuter = false
  offset = 0
  thread = false
  type = 0
FEATURE [Part::FeaturePython] Insert003  label="M3x5.74-Insert002"  # Fasteners workbench fastener (typed FeaturePython)
  FixShape = 1
  InvalidShape = false
  Placement = pos=(9.09327,1.25,-5.25) rot=(1,0,0;1.5708rad)
  TreeRank = 0
  ValidateShape = false
  baseObject = -> Body110 [Edge26]
  diameter = 3
  externalDiam = 4.55
  invert = false
  leftHanded = false
  length = 5.74
  matchOuter = false
  offset = 0
  thread = false
  type = 0
FEATURE [Part::FeaturePython] Insert  label="M3x5.74-Insert006"  # Fasteners workbench fastener (typed FeaturePython)
  FixShape = 1
  InvalidShape = false
  Placement = pos=(9.09327,10.25,5.25) rot=(-1,0,0;1.5708rad)
  TreeRank = 0
  ValidateShape = false
  baseObject = -> Body110 [Edge35]
  diameter = 3
  externalDiam = 4.55
  invert = true
  leftHanded = false
  length = 5.74
  matchOuter = false
  offset = 0
  thread = false
  type = 0
FEATURE [Part::FeaturePython] Insert004  label="M3x5.74-Insert007"  # Fasteners workbench fastener (typed FeaturePython)
  FixShape = 1
  InvalidShape = false
  Placement = pos=(-9.09327,10.25,5.25) rot=(-1,0,0;1.5708rad)
  TreeRank = 0
  ValidateShape = false
  baseObject = -> Body110 [Edge30]
  diameter = 3
  externalDiam = 4.55
  invert = true
  leftHanded = false
  length = 5.74
  matchOuter = false
  offset = 0
  thread = false
  type = 0
FEATURE [Part::FeaturePython] Insert005  label="M3x5.74-Insert008"  # Fasteners workbench fastener (typed FeaturePython)
  FixShape = 1
  InvalidShape = false
  Placement = pos=(4e-15,10.25,-10.5) rot=(-1,0,0;1.5708rad)
  TreeRank = 0
  ValidateShape = false
  baseObject = -> Body110 [Edge31]
  diameter = 3
  externalDiam = 4.55
  invert = true
  leftHanded = false
  length = 5.74
  matchOuter = false
  offset = 0
  thread = false
  type = 0
FEATURE [Part::FeaturePython] Insert006  label="M3x5.74-Insert009"  # Fasteners workbench fastener (typed FeaturePython)
  FixShape = 1
  InvalidShape = false
  Placement = pos=(12.9696,5.75,-5e-15) rot=(0,1,0;1.5708rad)
  TreeRank = 0
  ValidateShape = false
  baseObject = -> Body110 [Edge1]
  diameter = 3
  externalDiam = 4.55
  invert = false
  leftHanded = false
  length = 5.74
  matchOuter = false
  offset = 0
  thread = false
  type = 0
FEATURE [App::DocumentObjectGroup] Group010  label="Visserie"
  ClaimAllChildren = true
  ExportMode = 1
  Group = -> [Insert001,Insert002,Insert003,Insert004,Insert,Insert005,Insert006]
  TreeRank = 0
  _GroupVersion = 1
FEATURE [App::Part] Part048  label="NoyauAssembled"
  ClaimAllChildren = false
  ExportMode = 1
  Group = -> [Body110,Group010,Insert001,Insert002,Insert003,Insert004,Insert,Insert005,Insert006]
  Origin = -> Origin212
  TreeRank = 0
  _ExportChildren = -> [Body110,Group010]
  _GroupVersion = 1
FEATURE [Part::FeaturePython] Screw  label="M3x6-Vis"  # Fasteners workbench fastener (typed FeaturePython)
  FixShape = 1
  InvalidShape = false
  Placement = pos=(-9.09327,12.75,-5.25) rot=(-1,0,0;1.5708rad)
  TreeRank = 0
  ValidateShape = false
  baseObject = -> Body047 [Edge95]
  diameter = 1
  invert = true
  leftHanded = false
  length = 0
  lengthCustom = 6
  matchOuter = false
  offset = 11.5
  thread = false
  type = 58
FEATURE [Part::FeaturePython] Screw005  label="M3x6-Vis008"  # Fasteners workbench fastener (typed FeaturePython)
  FixShape = 1
  InvalidShape = false
  Placement = pos=(9.09327,12.75,-5.25) rot=(-1,0,0;1.5708rad)
  TreeRank = 0
  ValidateShape = false
  baseObject = -> Body047 [Edge98]
  diameter = 1
  invert = true
  leftHanded = false
  length = 0
  lengthCustom = 6
  matchOuter = false
  offset = 11.5
  thread = false
  type = 58
FEATURE [Part::FeaturePython] Screw006  label="M3x6-Vis009"  # Fasteners workbench fastener (typed FeaturePython)
  FixShape = 1
  InvalidShape = false
  Placement = pos=(0,12.75,10.5) rot=(-1,0,0;1.5708rad)
  TreeRank = 0
  ValidateShape = false
  baseObject = -> Body047 [Edge100]
  diameter = 1
  invert = true
  leftHanded = false
  length = 0
  lengthCustom = 6
  matchOuter = false
  offset = 11.5
  thread = false
  type = 58
FEATURE [Part::FeaturePython] Screw007  label="M3x6-Vis003"  # Fasteners workbench fastener (typed FeaturePython)
  FixShape = 1
  InvalidShape = false
  Placement = pos=(0,-1.25,10.5) rot=(1,0,0;1.5708rad)
  TreeRank = 0
  ValidateShape = false
  baseObject = -> Body047 [Edge114]
  diameter = 1
  invert = false
  leftHanded = false
  length = 0
  lengthCustom = 6
  matchOuter = false
  offset = 0
  thread = false
  type = 58
FEATURE [Part::FeaturePython] Screw008  label="M3x6-Vis004"  # Fasteners workbench fastener (typed FeaturePython)
  FixShape = 1
  InvalidShape = false
  Placement = pos=(-9.09327,-1.25,-5.25) rot=(1,0,0;1.5708rad)
  TreeRank = 0
  ValidateShape = false
  baseObject = -> Body047 [Edge104]
  diameter = 1
  invert = false
  leftHanded = false
  length = 0
  lengthCustom = 6
  matchOuter = false
  offset = 0
  thread = false
  type = 58
FEATURE [Part::FeaturePython] Screw009  label="M3x6-Vis005"  # Fasteners workbench fastener (typed FeaturePython)
  FixShape = 1
  InvalidShape = false
  Placement = pos=(9.09327,-1.25,-5.25) rot=(1,0,0;1.5708rad)
  TreeRank = 0
  ValidateShape = false
  baseObject = -> Body047 [Edge110]
  diameter = 1
  invert = false
  leftHanded = false
  length = 0
  lengthCustom = 6
  matchOuter = false
  offset = 0
  thread = false
  type = 58
FEATURE [App::DocumentObjectGroup] Group011  label="VisserieOmniWheel"
  ClaimAllChildren = true
  ExportMode = 1
  Group = -> [Screw,Screw005,Screw006,Screw007,Screw008,Screw009]
  TreeRank = 0
  _GroupVersion = 1
FEATURE [Part::Feature] Part__Feature001  label="mgn9c"
  FixShape = 1
  InvalidShape = false
  Placement = pos=(-47.5,2,0) rot=(0,0,1;0rad)
  TreeRank = 0
  ValidateShape = false
  shape: bbox 28.92 x 8.018 x 20.02 mm, 85 faces (baked)
FEATURE [Part::Feature] Part__Feature002  label="mgnr9"
  FixShape = 1
  InvalidShape = false
  TreeRank = 0
  ValidateShape = false
  shape: bbox 75 x 6.5 x 9 mm, 60 faces (baked)
FEATURE [PartDesign::FeatureBase] BaseFeature
  BaseFeature = -> Part__Feature002
  FixShape = 1
  InvalidShape = false
  NewSolid = false
  Suppress = false
  TreeRank = 0
  ValidateShape = true
FEATURE [PartDesign::Pad] Pad095
  AddSubType = 0
  AutoTaperInnerAngle = true
  BaseFeature = -> BaseFeature
  CheckUpToFaceLimits = true
  ClaimChildren = false
  Direction = (-1,0,0)
  Fit = 0
  FitJoin = 0
  FixShape = 1
  InnerFit = 0
  InnerFitJoin = 0
  InvalidShape = false
  Length = 125
  Length2 = 10
  NewSolid = false
  Profile = -> BaseFeature [Face20]
  Refine = true
  Suppress = false
  TaperInnerAngle = 0
  TaperInnerAngleRev = 0
  TreeRank = 0
  Type = 0
  ValidateShape = true
  _ProfileBasedVersion = 0
FEATURE [Sketcher::SketchObject] Sketch235
  ArcFitTolerance = 0
  AttachmentSupport = -> [Fillet024]
  ExternalBSplineMaxDegree = 0
  ExternalBSplineTolerance = 0
  FixShape = 1
  FullyConstrained = true
  InternalTolerance = 1e-06
  InvalidShape = false
  MakeInternals = false
  MapMode = 5
  Placement = pos=(0,5.3e-15,-8) rot=(0,0,1;3.14159rad)
  Support = -> [Fillet024]
  TreeRank = 0
  ValidateShape = false
  sketch-geometry (1):
    g0: Circle CenterX=0 CenterY=0 CenterZ=0 NormalX=0 NormalY=0 NormalZ=1 AngleXU=0 Radius=6.5
  constraints (2):
    c: Coincident(g0,g-1)
    c: Diameter(g0) = 13
FEATURE [PartDesign::Pad] Pad096
  AddSubType = 0
  AutoTaperInnerAngle = true
  BaseFeature = -> Fillet024
  CheckUpToFaceLimits = true
  ClaimChildren = false
  Direction = (0,-7e-16,1)
  Fit = 0
  FitJoin = 0
  FixShape = 1
  InnerFit = 0
  InnerFitJoin = 0
  InvalidShape = false
  Length = 2
  Length2 = 10
  NewSolid = false
  Placement = pos=(0,0,0) rot=(1,0,0;1.5708rad)
  Profile = -> Sketch235
  ReferenceAxis = -> Sketch235 [N_Axis]
  Refine = true
  Suppress = false
  TaperInnerAngle = 0
  TaperInnerAngleRev = 0
  TreeRank = 0
  Type = 0
  ValidateShape = true
  _ProfileBasedVersion = 0
FEATURE [PartDesign::Fillet] Fillet
  AddSubType = 0
  Base = -> Pad096 [Edge61]
  BaseFeature = -> Pad096
  FixShape = 1
  InvalidShape = false
  NewSolid = false
  Placement = pos=(0,0,0) rot=(1,0,0;1.5708rad)
  Radius = 1
  Refine = true
  SupportTransform = false
  Suppress = false
  TreeRank = 0
  UseAllEdges = false
  ValidateShape = true
FEATURE [PartDesign::Body] Body041  label="ServoBody001"
  AutoGroupSolids = false
  ClaimAllChildren = false
  ExportMode = 0
  FixShape = 1
  Group = -> [Sketch086,Pad050,Sketch087,Pocket033,Fillet024,Sketch235,Pad096,Fillet]
  InvalidShape = false
  Origin = -> Origin062
  Placement = pos=(0,0,-1) rot=(0,0,1;0rad)
  SingleSolid = true
  Tip = -> Fillet
  TreeRank = 0
  ValidateShape = false
  _ExportChildren = -> [Pad050,Pocket033,Fillet024,Pad096,Fillet]
  _GroupVersion = 1
FEATURE [App::Part] Part015  label="MG996"
  ClaimAllChildren = false
  ExportMode = 1
  Group = -> [Body041,Body043]
  Origin = -> Origin061
  Placement = pos=(0,0,0) rot=(1,0,0;1.5708rad)
  TreeRank = 0
  _ExportChildren = -> [Body041,Body043]
  _GroupVersion = 1
FEATURE [App::DocumentObjectGroup] Group005  label="Servomotors"
  ClaimAllChildren = true
  ExportMode = 1
  Group = -> [Part015,Part044]
  TreeRank = 0
  _GroupVersion = 1
FEATURE [Sketcher::SketchObject] Sketch236
  ArcFitTolerance = 0
  ExternalBSplineMaxDegree = 0
  ExternalBSplineTolerance = 0
  ExternalGeometry = -> [Pad095]
  FixShape = 1
  FullyConstrained = false
  InternalTolerance = 1e-06
  InvalidShape = false
  MakeInternals = false
  MapMode = 5
  Placement = pos=(0,0,0) rot=(1,0,0;1.5708rad)
  TreeRank = 0
  ValidateShape = false
  sketch-geometry (1):
    g0: Circle CenterX=-7.5 CenterY=3e-16 CenterZ=0 NormalX=0 NormalY=0 NormalZ=1 AngleXU=0 Radius=1.75
  constraints (2):
    c: DistanceX(g-3,g-1) = 7.5
    c: DistanceX(g-4,g-3) = 20
FEATURE [PartDesign::Pocket] Pocket075
  AddSubType = 1
  AutoTaperInnerAngle = true
  BaseFeature = -> Pad095
  CheckUpToFaceLimits = true
  ClaimChildren = false
  Direction = (0,1,0)
  Fit = 0
  FitJoin = 0
  FixShape = 1
  InnerFit = 0
  InnerFitJoin = 0
  InvalidShape = false
  Length = 5
  Length2 = 5
  NewSolid = false
  Profile = -> Sketch236
  ReferenceAxis = -> Sketch236 [N_Axis]
  Refine = true
  Suppress = false
  TaperInnerAngle = 0
  TaperInnerAngleRev = 0
  TreeRank = 0
  Type = 1
  ValidateShape = true
  _ProfileBasedVersion = 0
  _Version = 0
FEATURE [PartDesign::LinearPattern] LinearPattern
  AddSubType = 0
  BaseFeature = -> Pocket075
  CopyShape = true
  Direction = -> X_Axis137
  FixShape = 1
  InvalidShape = false
  Length = 180
  NewSolid = false
  Occurrences = 10
  OriginalSubs = -> [Pocket075]
  Originals = -> [Pocket075]
  ParallelTransform = true
  Placement = pos=(-26.0308,-14.9133,0.499992) rot=(0,0,1;0rad)
  Refine = true
  Reversed = true
  SubTransform = true
  Suppress = false
  TreeRank = 0
  ValidateShape = true
  _Version = 0
FEATURE [PartDesign::Body] Body112  label="MGN9-200mm"
  AutoGroupSolids = false
  BaseFeature = -> Part__Feature002
  ClaimAllChildren = false
  ExportMode = 0
  FixShape = 1
  Group = -> [BaseFeature,Pad095,Sketch236,Pocket075,LinearPattern]
  InvalidShape = false
  Origin = -> Origin214
  SingleSolid = true
  Tip = -> LinearPattern
  TreeRank = 0
  ValidateShape = false
  _ExportChildren = -> [BaseFeature,Pad095,Pocket075,LinearPattern]
  _GroupVersion = 1
FEATURE [PartDesign::Pocket] Pocket076
  AddSubType = 1
  AutoTaperInnerAngle = true
  BaseFeature = -> Pocket062
  CheckUpToFaceLimits = true
  ClaimChildren = false
  Direction = (0,0,-1)
  Fit = 0
  FitJoin = 0
  FixShape = 1
  InnerFit = 0
  InnerFitJoin = 0
  InvalidShape = false
  Length = 5
  Length2 = 5
  NewSolid = false
  Profile = -> Sketch194
  ReferenceAxis = -> Sketch194 [N_Axis]
  Refine = true
  Reversed = true
  Suppress = false
  TaperInnerAngle = 0
  TaperInnerAngleRev = 0
  TreeRank = 0
  Type = 1
  ValidateShape = true
  _ProfileBasedVersion = 0
  _Version = 0
FEATURE [Sketcher::SketchObject] Sketch237
  ArcFitTolerance = 0
  AttachmentSupport = -> [Pocket076]
  ExternalBSplineMaxDegree = 0
  ExternalBSplineTolerance = 0
  ExternalGeometry = -> [Pocket076]
  FixShape = 1
  FullyConstrained = true
  InternalTolerance = 1e-06
  InvalidShape = false
  MakeInternals = false
  MapMode = 5
  Placement = pos=(0,0,0) rot=(1,0,0;3.14159rad)
  Support = -> [Pocket076]
  TreeRank = 0
  ValidateShape = false
  sketch-geometry (2):
    g0: Circle CenterX=14.1 CenterY=14.1 CenterZ=0 NormalX=0 NormalY=0 NormalZ=1 AngleXU=0 Radius=2.4
    g1: Circle CenterX=-14.1 CenterY=-14.1 CenterZ=0 NormalX=0 NormalY=0 NormalZ=1 AngleXU=0 Radius=2.4
  constraints (4):
    c: Coincident(g0,g-3)
    c: Coincident(g1,g-4)
    c: Equal(g0,g1)
    c: Diameter(g0) = 4.8
FEATURE [PartDesign::Pocket] Pocket077
  AddSubType = 1
  AutoTaperInnerAngle = true
  BaseFeature = -> Pocket076
  CheckUpToFaceLimits = true
  ClaimChildren = false
  Direction = (0,0,1)
  Fit = 0
  FitJoin = 0
  FixShape = 1
  InnerFit = 0
  InnerFitJoin = 0
  InvalidShape = false
  Length = 11.8
  Length2 = 5
  NewSolid = false
  Profile = -> Sketch237
  ReferenceAxis = -> Sketch237 [N_Axis]
  Refine = true
  Suppress = false
  TaperInnerAngle = 0
  TaperInnerAngleRev = 0
  TreeRank = 0
  Type = 0
  ValidateShape = true
  _ProfileBasedVersion = 0
  _Version = 0
FEATURE [PartDesign::Body] Body090  label="BaseLD06"
  AutoGroupSolids = false
  ClaimAllChildren = false
  ExportMode = 0
  FixShape = 1
  Group = -> [Sketch189,Pad077,Sketch190,Pad078,Sketch191,Pocket061,Sketch192,Pad079,Fillet045,Fillet046,Sketch193,Pocket062,Sketch194,Pocket076,Sketch237,Pocket077]
  InvalidShape = false
  Origin = -> Origin181
  SingleSolid = true
  Tip = -> Pocket077
  TreeRank = 0
  ValidateShape = false
  _ExportChildren = -> [Pad077,Pad078,Pocket061,Pad079,Fillet045,Fillet046,Pocket062,Pocket076,Pocket077]
  _GroupVersion = 1
FEATURE [App::Part] Part003  label="LD06"
  ClaimAllChildren = false
  ExportMode = 1
  Group = -> [ImagePlane,Body090,Body091]
  Origin = -> Origin180
  TreeRank = 0
  _ExportChildren = -> [ImagePlane,Body090,Body091]
  _GroupVersion = 1
FEATURE [App::DocumentObjectGroup] Group004  label="Lidar"
  ClaimAllChildren = true
  ExportMode = 1
  Group = -> [Part003]
  TreeRank = 0
  _GroupVersion = 1
FEATURE [Sketcher::SketchObject] Sketch238
  ArcFitTolerance = 1e-06
  AttachmentSupport = -> [Chamfer050]
  ExternalBSplineMaxDegree = 5
  ExternalBSplineTolerance = 0.0001
  FixShape = 1
  FullyConstrained = true
  InternalTolerance = 1e-06
  InvalidShape = false
  MakeInternals = false
  MapMode = 5
  Placement = pos=(8,2.66e-14,-1.16e-14) rot=(0.57735,0.57735,0.57735;2.0944rad)
  Support = -> [Chamfer050]
  TreeRank = 1
  ValidateShape = false
  sketch-geometry (1):
    g0: Circle CenterX=8 CenterY=0 CenterZ=0 NormalX=0 NormalY=0 NormalZ=1 AngleXU=0 Radius=1.6
  constraints (3):
    c: PointOnObject(g0,g-1)
    c: Diameter(g0) = 3.2
    c: DistanceX(g-1,g0) = 8
FEATURE [PartDesign::Pocket] Pocket078
  AddSubType = 1
  AlongSketchNormal = false
  AutoTaperInnerAngle = true
  BaseFeature = -> Chamfer050
  CheckUpToFaceLimits = true
  ClaimChildren = false
  Direction = (-1,-3.2e-15,1.4e-15)
  Fit = 0
  FitJoin = 0
  FixShape = 1
  InnerFit = 0
  InnerFitJoin = 0
  InvalidShape = false
  Length = 5
  Length2 = 10
  Linearize = true
  NewSolid = false
  Profile = -> Sketch238
  ReferenceAxis = -> Sketch238 [N_Axis]
  Refine = true
  Suppress = false
  TaperInnerAngle = 0
  TaperInnerAngleRev = 0
  TreeRank = 2
  Type = 1
  ValidateShape = true
  _ProfileBasedVersion = 1
  _Version = 1
FEATURE [Sketcher::SketchObject] Sketch239
  ArcFitTolerance = 1e-06
  AttachmentSupport = -> [Pocket078]
  ExternalBSplineMaxDegree = 5
  ExternalBSplineTolerance = 0.0001
  ExternalGeometry = -> [Pocket078]
  FixShape = 1
  FullyConstrained = true
  InternalTolerance = 1e-06
  InvalidShape = false
  MakeInternals = false
  MapMode = 5
  Placement = pos=(-5,-1.54e-14,7.3e-15) rot=(0.57735,-0.57735,-0.57735;2.0944rad)
  Support = -> [Pocket078]
  TreeRank = 3
  ValidateShape = false
  sketch-geometry (7):
    g0: LineSegment StartX=-4.82457 StartY=0 StartZ=0 EndX=-6.41229 EndY=2.75 EndZ=0
    g1: LineSegment StartX=-6.41229 StartY=2.75 StartZ=0 EndX=-9.58771 EndY=2.75 EndZ=0
    g2: LineSegment StartX=-9.58771 StartY=2.75 StartZ=0 EndX=-11.1754 EndY=-1.51e-14 EndZ=0
    g3: LineSegment StartX=-11.1754 StartY=-1.5e-14 StartZ=0 EndX=-9.58771 EndY=-2.75 EndZ=0
    g4: LineSegment StartX=-9.58771 StartY=-2.75 StartZ=0 EndX=-6.41229 EndY=-2.75 EndZ=0
    g5: LineSegment StartX=-6.41229 StartY=-2.75 StartZ=0 EndX=-4.82457 EndY=0 EndZ=0
    g6: Circle [constr] CenterX=-8 CenterY=-4e-16 CenterZ=0 NormalX=0 NormalY=0 NormalZ=1 AngleXU=0 Radius=3.17543
  constraints (16):
    c: Coincident(g0,g1)
    c: Coincident(g1,g2)
    c: Coincident(g2,g3)
    c: Coincident(g3,g4)
    c: Coincident(g4,g5)
    c: Coincident(g5,g0)
    c: Equal(g0, g1-g5) x5
    c: PointOnObject(g0,g6)
    c: PointOnObject(g1,g6)
    c: PointOnObject(g2,g6)
    c: PointOnObject(g3,g6)
    c: PointOnObject(g4,g6)
    c: PointOnObject(g5,g6)
    c: Coincident(g6,g-3)
    c: PointOnObject(g5,g-1)
    c: DistanceY(g3,g1) = 5.5
FEATURE [PartDesign::Pocket] Pocket079
  AddSubType = 1
  AlongSketchNormal = false
  AutoTaperInnerAngle = true
  BaseFeature = -> Pocket078
  CheckUpToFaceLimits = true
  ClaimChildren = false
  Direction = (1,3e-15,-1.4e-15)
  Fit = 0
  FitJoin = 0
  FixShape = 1
  InnerFit = 0
  InnerFitJoin = 0
  InvalidShape = false
  Length = 5
  Length2 = 10
  Linearize = true
  NewSolid = false
  Profile = -> Sketch239
  ReferenceAxis = -> Sketch239 [N_Axis]
  Refine = true
  Suppress = false
  TaperInnerAngle = 0
  TaperInnerAngleRev = 0
  TreeRank = 4
  Type = 0
  ValidateShape = true
  _ProfileBasedVersion = 1
  _Version = 1
FEATURE [PartDesign::Chamfer] Chamfer056
  AddSubType = 0
  Angle = 45
  Base = -> Pocket079 [Face12,Edge66,Edge49,Edge50,Edge51,Edge52,Edge53,Edge48,Edge28,Edge35,Edge37,Edge31,Edge26,Edge20,Edge43,Edge44,Edge45,Edge24]
  BaseFeature = -> Pocket079
  ChamferType = 0
  FixShape = 1
  FlipDirection = false
  InvalidShape = false
  NewSolid = false
  Refine = true
  Size = 0.4
  Size2 = 1
  SupportTransform = false
  Suppress = false
  TreeRank = 5
  UseAllEdges = false
  ValidateShape = true
FEATURE [PartDesign::Body] Body108  label="Link_100_deg"
  AutoGroupSolids = false
  ClaimAllChildren = false
  ExportMode = 0
  FixShape = 1
  Group = -> [Sketch221,Pad090,Sketch222,Pocket067,Sketch223,Pocket068,Sketch224,Pad091,Sketch225,Groove002,Sketch226,Pocket069,Sketch227,Pocket070,Sketch228,Groove003,PolarPattern024,Chamfer049,Sketch229,Pad092,Chamfer050,Sketch238,Pocket078,Sketch239,Pocket079,Chamfer056]
  InvalidShape = false
  Origin = -> Origin209
  SingleSolid = true
  Tip = -> Chamfer056
  TreeRank = 0
  ValidateShape = false
  _ExportChildren = -> [Pad090,Pocket067,Pocket068,Pad091,Groove002,Pocket069,Pocket070,Groove003,PolarPattern024,Chamfer049,Pad092,Chamfer050,Pocket078,Pocket079,Chamfer056]
  _GroupVersion = 1
FEATURE [PartDesign::FeatureBase] Clone003
  BaseFeature = -> Body108
  FixShape = 1
  InvalidShape = false
  NewSolid = false
  Suppress = false
  TreeRank = 0
  ValidateShape = true
FEATURE [PartDesign::Body] Body109  label="Link_100_deg_Clone"
  AutoGroupSolids = false
  BaseFeature = -> Body108
  ClaimAllChildren = false
  ExportMode = 0
  FixShape = 1
  Group = -> [Clone003]
  InvalidShape = false
  Origin = -> Origin210
  SingleSolid = true
  Tip = -> Clone003
  TreeRank = 0
  ValidateShape = false
  _ExportChildren = -> [Clone003]
  _GroupVersion = 1
FEATURE [Part::Mirroring] Part__Mirroring002  label="Link_100_deg_Mirror"
  Base = (0,0,0)
  FixShape = 1
  InvalidShape = false
  Normal = (1,0,0)
  Source = -> Body109
  TreeRank = 0
  ValidateShape = false
FEATURE [PartDesign::Line] DatumLine
  AttacherType = Attacher::AttachEngineLine
  AttachmentSupport = -> [Sketch219]
  FixShape = 1
  InvalidShape = false
  Length = 10
  MapMode = 24
  MinimumLength = 10
  Placement = pos=(1e-15,0.0904611,4.48697) rot=(0,0.996195,0.087156;3.14159rad)
  ResizeMode = 0
  Support = -> [Sketch219]
  TreeRank = 6
  ValidateShape = false
FEATURE [PartDesign::Groove] Groove004
  AddSubType = 1
  Angle = 360
  Axis = (-3e-16,0.173648,-0.984808)
  Base = (1e-15,0.0904611,4.48697)
  BaseFeature = -> Pad088
  ClaimChildren = false
  Fit = 0
  FitJoin = 0
  FixShape = 1
  InnerFit = 0
  InnerFitJoin = 0
  InvalidShape = false
  Linearize = true
  NewSolid = false
  Profile = -> Sketch219
  ReferenceAxis = -> DatumLine
  Refine = true
  Suppress = false
  TreeRank = 7
  ValidateShape = true
  _ProfileBasedVersion = 1
FEATURE [PartDesign::Body] Body104  label="Corner_100_deg"
  AutoGroupSolids = false
  ClaimAllChildren = false
  ExportMode = 0
  FixShape = 1
  Group = -> [Sketch212,Pad087,Sketch213,Pocket063,PolarPattern022,Sketch214,Pocket064,Sketch215,Pocket065,Sketch216,Groove,PolarPattern023,Sketch217,Pocket066,Sketch218,Pad088,DatumLine,Sketch219,Groove004]
  InvalidShape = false
  Origin = -> Origin203
  SingleSolid = true
  Tip = -> Groove004
  TreeRank = 0
  ValidateShape = false
  _ExportChildren = -> [Pad087,Pocket063,PolarPattern022,Pocket064,Pocket065,Groove,PolarPattern023,Pocket066,Pad088,DatumLine,Groove004]
  _GroupVersion = 1
FEATURE [PartDesign::FeatureBase] Clone
  BaseFeature = -> Body104
  FixShape = 1
  InvalidShape = false
  NewSolid = false
  Suppress = false
  TreeRank = 0
  ValidateShape = true
FEATURE [Sketcher::SketchObject] Sketch220
  ArcFitTolerance = 0
  AttachmentSupport = -> [Clone]
  ExternalBSplineMaxDegree = 0
  ExternalBSplineTolerance = 0
  ExternalGeometry = -> [Clone]
  FixShape = 1
  FullyConstrained = true
  InternalTolerance = 1e-06
  InvalidShape = false
  MakeInternals = false
  MapMode = 5
  Placement = pos=(5,6.7e-15,-2.2e-15) rot=(0.57735,0.57735,0.57735;2.0944rad)
  Support = -> [Clone]
  TreeRank = 0
  ValidateShape = false
  sketch-geometry (7):
    g0: LineSegment StartX=5 StartY=-5 StartZ=0 EndX=-15 EndY=-5 EndZ=0
    g1: LineSegment StartX=5 StartY=-5 StartZ=0 EndX=5 EndY=5 EndZ=0
    g2: LineSegment StartX=5 StartY=5 StartZ=0 EndX=3.44316 EndY=15 EndZ=0
    g3: LineSegment StartX=-15 StartY=-5 StartZ=0 EndX=-15 EndY=1.8e-15 EndZ=0
    g4: LineSegment StartX=3.44316 StartY=15 StartZ=0 EndX=9e-16 EndY=15 EndZ=0
    g5: ArcOfCircle CenterX=0 CenterY=0 CenterZ=0 NormalX=0 NormalY=0 NormalZ=1 AngleXU=0 Radius=15 StartAngle=1.5708 EndAngle=3.14159
    g6: Circle CenterX=0 CenterY=0 CenterZ=0 NormalX=0 NormalY=0 NormalZ=1 AngleXU=0 Radius=3
  constraints (18):
    c: Coincident(g0,g-5)
    c: Horizontal(g0)
    c: Coincident(g1,g0)
    c: Coincident(g1,g-4)
    c: Coincident(g2,g1)
    c: PointOnObject(g-3,g2)
    c: Coincident(g3,g0)
    c: PointOnObject(g3,g-1)
    c: Vertical(g3)
    c: Coincident(g4,g2)
    c: PointOnObject(g4,g-2)
    c: Horizontal(g4)
    c: Coincident(g5,g-1)
    c: Coincident(g5,g4)
    c: Coincident(g5,g3)
    c: DistanceX(g0,g0) = 20
    c: Coincident(g6,g5)
    c: Tangent(g6,g-6)
FEATURE [PartDesign::Pad] Pad089
  AddSubType = 0
  AutoTaperInnerAngle = true
  BaseFeature = -> Clone
  CheckUpToFaceLimits = true
  ClaimChildren = false
  Direction = (1,1.3e-15,-4e-16)
  Fit = 0
  FitJoin = 0
  FixShape = 1
  InnerFit = 0
  InnerFitJoin = 0
  InvalidShape = false
  Length = 3
  Length2 = 10
  NewSolid = false
  Profile = -> Sketch220
  ReferenceAxis = -> Sketch220 [N_Axis]
  Refine = true
  Suppress = false
  TaperInnerAngle = 0
  TaperInnerAngleRev = 0
  TreeRank = 0
  Type = 0
  ValidateShape = true
  _ProfileBasedVersion = 0
FEATURE [PartDesign::FeatureBase] Clone002
  BaseFeature = -> Body104
  FixShape = 1
  InvalidShape = false
  NewSolid = false
  Suppress = false
  TreeRank = 0
  ValidateShape = true
FEATURE [PartDesign::Body] Body107
  AutoGroupSolids = false
  BaseFeature = -> Body104
  ClaimAllChildren = false
  ExportMode = 0
  FixShape = 1
  Group = -> [Clone002]
  InvalidShape = false
  Origin = -> Origin208
  SingleSolid = true
  Tip = -> Clone002
  TreeRank = 0
  ValidateShape = false
  _ExportChildren = -> [Clone002]
  _GroupVersion = 1
FEATURE [Part::Mirroring] Part__Mirroring001  label="Body107 (Mirror #2)"
  Base = (0,0,0)
  FixShape = 1
  InvalidShape = false
  Normal = (1,0,0)
  Source = -> Body107
  TreeRank = 0
  ValidateShape = false
FEATURE [PartDesign::Chamfer] Chamfer054
  AddSubType = 0
  Angle = 45
  Base = -> Pad089 [Edge75,Edge85,Edge91,Edge26]
  BaseFeature = -> Pad089
  ChamferType = 0
  FixShape = 1
  FlipDirection = false
  InvalidShape = false
  NewSolid = false
  Refine = true
  Size = 1
  Size2 = 1
  SupportTransform = false
  Suppress = false
  TreeRank = 0
  UseAllEdges = false
  ValidateShape = true
FEATURE [PartDesign::Chamfer] Chamfer055
  AddSubType = 0
  Angle = 45
  Base = -> Chamfer054 [Face12]
  BaseFeature = -> Chamfer054
  ChamferType = 0
  FixShape = 1
  FlipDirection = false
  InvalidShape = false
  NewSolid = false
  Refine = true
  Size = 0.6
  Size2 = 1
  SupportTransform = false
  Suppress = false
  TreeRank = 0
  UseAllEdges = false
  ValidateShape = true
FEATURE [PartDesign::Body] Body105  label="Corner_100_deg_Side"
  AutoGroupSolids = false
  BaseFeature = -> Body104
  ClaimAllChildren = false
  ExportMode = 0
  FixShape = 1
  Group = -> [Clone,Sketch220,Pad089,Chamfer054,Chamfer055]
  InvalidShape = false
  Origin = -> Origin204
  SingleSolid = true
  Tip = -> Chamfer055
  TreeRank = 0
  ValidateShape = false
  _ExportChildren = -> [Clone,Pad089,Chamfer054,Chamfer055]
  _GroupVersion = 1
FEATURE [App::Part] Part046  label="100_deg_Corners"
  ClaimAllChildren = false
  ExportMode = 1
  Group = -> [Body105,Body104]
  Origin = -> Origin205
  TreeRank = 0
  _ExportChildren = -> [Body105,Body104]
  _GroupVersion = 1
FEATURE [PartDesign::FeatureBase] Clone001
  BaseFeature = -> Body105
  FixShape = 1
  InvalidShape = false
  NewSolid = false
  Suppress = false
  TreeRank = 0
  ValidateShape = true
FEATURE [PartDesign::Body] Body106
  AutoGroupSolids = false
  BaseFeature = -> Body105
  ClaimAllChildren = false
  ExportMode = 0
  FixShape = 1
  Group = -> [Clone001]
  InvalidShape = false
  Origin = -> Origin207
  SingleSolid = true
  Tip = -> Clone001
  TreeRank = 0
  ValidateShape = false
  _ExportChildren = -> [Clone001]
  _GroupVersion = 1
FEATURE [Part::Mirroring] Part__Mirroring  label="Body106 (Mirror #1)"
  Base = (0,0,0)
  FixShape = 1
  InvalidShape = false
  Normal = (1,0,0)
  Source = -> Body106
  TreeRank = 0
  ValidateShape = false
FEATURE [App::Part] Part047  label="100_deg_Corners_Mirror"
  ClaimAllChildren = false
  ExportMode = 1
  Group = -> [Body106,Body107,Part__Mirroring,Part__Mirroring001]
  Origin = -> Origin206
  TreeRank = 0
  _ExportChildren = -> [Part__Mirroring,Part__Mirroring001]
  _GroupVersion = 1
FEATURE [App::DocumentObjectGroup] Group003  label="MakerBeam"
  ClaimAllChildren = true
  ExportMode = 1
  Group = -> [Body004,Body096,Body095,Body002,Body003,Body001,Body103,Part046,Body108,Part047,Part__Mirroring002,Body109]
  TreeRank = 0
  _GroupVersion = 1
FEATURE [Sketcher::SketchObject] Sketch245
  ArcFitTolerance = 0
  ExternalBSplineMaxDegree = 0
  ExternalBSplineTolerance = 0
  FixShape = 1
  FullyConstrained = true
  InternalTolerance = 1e-06
  InvalidShape = false
  MakeInternals = false
  MapMode = 5
  Placement = pos=(0,0,0) rot=(1,0,0;1.5708rad)
  TreeRank = 0
  ValidateShape = false
  sketch-geometry (1):
    g0: Circle CenterX=0 CenterY=0 CenterZ=0 NormalX=0 NormalY=0 NormalZ=1 AngleXU=0 Radius=13.9
  constraints (2):
    c: Coincident(g0,g-1)
    c: Diameter(g0) = 27.8
FEATURE [PartDesign::Pad] Pad098
  AddSubType = 0
  AutoTaperInnerAngle = true
  CheckUpToFaceLimits = true
  ClaimChildren = false
  Direction = (0,-1,2e-16)
  Fit = 0
  FitJoin = 0
  FixShape = 1
  InnerFit = 0
  InnerFitJoin = 0
  InvalidShape = false
  Length = 9
  Length2 = 10
  NewSolid = false
  Placement = pos=(0,0,0) rot=(1,0,0;1.5708rad)
  Profile = -> Sketch245
  ReferenceAxis = -> Sketch245 [N_Axis]
  Refine = true
  Reversed = true
  Suppress = false
  TaperInnerAngle = 0
  TaperInnerAngleRev = 0
  TreeRank = 0
  Type = 0
  ValidateShape = true
  _ProfileBasedVersion = 0
FEATURE [Sketcher::SketchObject] Sketch246
  ArcFitTolerance = 0
  AttachmentSupport = -> [Pad098]
  ExternalBSplineMaxDegree = 0
  ExternalBSplineTolerance = 0
  FixShape = 1
  FullyConstrained = true
  InternalTolerance = 1e-06
  InvalidShape = false
  MakeInternals = false
  MapMode = 5
  Placement = pos=(0,0,0) rot=(1,0,0;1.5708rad)
  Support = -> [Pad098]
  TreeRank = 0
  ValidateShape = false
  sketch-geometry (1):
    g0: Circle CenterX=0 CenterY=10.5 CenterZ=0 NormalX=0 NormalY=0 NormalZ=1 AngleXU=0 Radius=2.1
  constraints (3):
    c: PointOnObject(g0,g-2)
    c: DistanceY(g-1,g0) = 10.5
    c: Diameter(g0) = 4.2
FEATURE [Sketcher::SketchObject] Sketch247
  ArcFitTolerance = 0
  ExternalBSplineMaxDegree = 0
  ExternalBSplineTolerance = 0
  FixShape = 1
  FullyConstrained = true
  InternalTolerance = 1e-06
  InvalidShape = false
  MakeInternals = false
  MapMode = 5
  Placement = pos=(0,0,0) rot=(1,0,0;1.5708rad)
  TreeRank = 0
  ValidateShape = false
  sketch-geometry (1):
    g0: Circle CenterX=0 CenterY=0 CenterZ=0 NormalX=0 NormalY=0 NormalZ=1 AngleXU=0 Radius=2.5
  constraints (2):
    c: Coincident(g0,g-1)
    c: Diameter(g0) = 5
FEATURE [Sketcher::SketchObject] Sketch248
  ArcFitTolerance = 0
  ExternalBSplineMaxDegree = 0
  ExternalBSplineTolerance = 0
  FixShape = 1
  FullyConstrained = true
  InternalTolerance = 1e-06
  InvalidShape = false
  MakeInternals = false
  MapMode = 5
  Placement = pos=(0,0,0) rot=(1,0,0;1.5708rad)
  TreeRank = 0
  ValidateShape = false
  sketch-geometry (2):
    g0: LineSegment StartX=12.9696 StartY=5 StartZ=0 EndX=12.9696 EndY=-5 EndZ=0
    g1: ArcOfCircle CenterX=0 CenterY=0 CenterZ=0 NormalX=0 NormalY=0 NormalZ=1 AngleXU=0 Radius=13.9 StartAngle=5.91523 EndAngle=6.65114
  constraints (6):
    c: Vertical(g0)
    c: Coincident(g1,g-1)
    c: Coincident(g1,g0)
    c: Coincident(g1,g0)
    c: DistanceY(g0,g0) = 10
    c: Radius(g1) = 13.9
FEATURE [PartDesign::Hole] Hole001
  AddSubType = 1
  BaseFeature = -> Pad098
  ClaimChildren = false
  CustomThreadClearance = 0
  Depth = 81.4597
  DepthType = 1
  Diameter = 3.4
  DrillForDepth = false
  DrillPoint = 1
  DrillPointAngle = 118
  Fit = 0
  FitJoin = 0
  FixShape = 1
  HoleCutCountersinkAngle = 90
  HoleCutCustomValues = false
  HoleCutDepth = 0
  HoleCutDiameter = 6.1
  HoleCutType = 0
  InnerFit = 0
  InnerFitJoin = 0
  InvalidShape = false
  Linearize = true
  ModelThread = false
  NewSolid = false
  Profile = -> Sketch246
  Refine = true
  Suppress = false
  Tapered = false
  TaperedAngle = 90
  ThreadClass = 0
  ThreadDepth = 81.4597
  ThreadDepthType = 0
  ThreadDirection = 0
  ThreadFit = 0
  ThreadSize = 9
  ThreadType = 1
  Threaded = false
  TreeRank = 11
  UseCustomThreadClearance = false
  ValidateShape = true
  _ProfileBasedVersion = 1
FEATURE [PartDesign::PolarPattern] PolarPattern027
  AddSubType = 0
  Angle = 360
  Axis = -> Y_Axis140
  BaseFeature = -> Hole001
  CopyShape = true
  FixShape = 1
  InvalidShape = false
  NewSolid = false
  Occurrences = 6
  OriginalSubs = -> [Hole001]
  Originals = -> [Hole001]
  ParallelTransform = true
  Refine = true
  SubTransform = true
  Suppress = false
  TreeRank = 0
  ValidateShape = true
  _Version = 0
FEATURE [PartDesign::Pocket] Pocket085
  AddSubType = 1
  AutoTaperInnerAngle = true
  BaseFeature = -> PolarPattern027
  CheckUpToFaceLimits = true
  ClaimChildren = false
  Direction = (0,1,-2e-16)
  Fit = 0
  FitJoin = 0
  FixShape = 1
  InnerFit = 0
  InnerFitJoin = 0
  InvalidShape = false
  Length = 5
  Length2 = 5
  NewSolid = false
  Profile = -> Sketch247
  ReferenceAxis = -> Sketch247 [N_Axis]
  Refine = true
  Suppress = false
  TaperInnerAngle = 0
  TaperInnerAngleRev = 0
  TreeRank = 0
  Type = 1
  ValidateShape = true
  _ProfileBasedVersion = 0
  _Version = 0
FEATURE [PartDesign::Pocket] Pocket086
  AddSubType = 1
  AutoTaperInnerAngle = true
  BaseFeature = -> Pocket085
  CheckUpToFaceLimits = true
  ClaimChildren = false
  Direction = (0,1,-2e-16)
  Fit = 0
  FitJoin = 0
  FixShape = 1
  InnerFit = 0
  InnerFitJoin = 0
  InvalidShape = false
  Length = 5
  Length2 = 5
  NewSolid = false
  Profile = -> Sketch248
  ReferenceAxis = -> Sketch248 [N_Axis]
  Refine = true
  Suppress = false
  TaperInnerAngle = 0
  TaperInnerAngleRev = 0
  TreeRank = 0
  Type = 1
  ValidateShape = true
  _ProfileBasedVersion = 0
  _Version = 0
FEATURE [Sketcher::SketchObject] Sketch249
  ArcFitTolerance = 0
  AttachmentSupport = -> [Pocket086]
  ExternalBSplineMaxDegree = 0
  ExternalBSplineTolerance = 0
  ExternalGeometry = -> [Pocket086]
  FixShape = 1
  FullyConstrained = true
  InternalTolerance = 1e-06
  InvalidShape = false
  MakeInternals = false
  MapMode = 5
  Placement = pos=(12.9696,0,0) rot=(0.57735,0.57735,0.57735;2.0944rad)
  Support = -> [Pocket086]
  TreeRank = 0
  ValidateShape = false
  sketch-geometry (2):
    g0: Circle CenterX=4.5 CenterY=0 CenterZ=0 NormalX=0 NormalY=0 NormalZ=1 AngleXU=0 Radius=2.1
    g1: LineSegment [constr] StartX=9 StartY=0 StartZ=0 EndX=0 EndY=0 EndZ=0
  constraints (5):
    c: Diameter(g0) = 4.2
    c: Coincident(g1,g-1)
    c: Symmetric(g1,g1,g0)
    c: PointOnObject(g1,g-3)
    c: PointOnObject(g1,g-1)
FEATURE [PartDesign::Hole] Hole
  AddSubType = 1
  BaseFeature = -> Pocket086
  ClaimChildren = false
  CustomThreadClearance = 0
  Depth = 13
  DepthType = 0
  Diameter = 3.4
  DrillForDepth = false
  DrillPoint = 1
  DrillPointAngle = 118
  Fit = 0
  FitJoin = 0
  FixShape = 1
  HoleCutCountersinkAngle = 90
  HoleCutCustomValues = false
  HoleCutDepth = 0
  HoleCutDiameter = 6.1
  HoleCutType = 0
  InnerFit = 0
  InnerFitJoin = 0
  InvalidShape = false
  Linearize = true
  ModelThread = false
  NewSolid = false
  Profile = -> Sketch249
  Refine = true
  Suppress = false
  Tapered = false
  TaperedAngle = 90
  ThreadClass = 0
  ThreadDepth = 13
  ThreadDepthType = 0
  ThreadDirection = 0
  ThreadFit = 0
  ThreadSize = 9
  ThreadType = 1
  Threaded = false
  TreeRank = 10
  UseCustomThreadClearance = false
  ValidateShape = true
  _ProfileBasedVersion = 1
FEATURE [PartDesign::Body] Body114  label="NoyauRoueCNC"
  AutoGroupSolids = false
  ClaimAllChildren = false
  ExportMode = 0
  FixShape = 1
  Group = -> [Sketch245,Pad098,Sketch246,Hole001,PolarPattern027,Sketch247,Pocket085,Sketch248,Pocket086,Sketch249,Hole]
  InvalidShape = false
  Origin = -> Origin217
  Placement = pos=(3e-15,1.25,0) rot=(0,0,1;0rad)
  SingleSolid = true
  Tip = -> Hole
  TreeRank = 9
  ValidateShape = false
  _ExportChildren = -> [Pad098,Hole001,PolarPattern027,Pocket085,Pocket086,Hole]
  _GroupVersion = 1
FEATURE [TechDraw::DrawSVGTemplate] Template
  EditableTexts = Designed_by_Name=Barbatronic; Drawing_number=1.0; FC-Date=17/09/2024; FC-SC=1:1; FC-SH=1; FC-Title=Noyau de roue; Subtitle=Noyau pour roue omnidirectionnelle; Weight=NA
  Height = 210
  Orientation = 1
  Template = /snap/freecad-realthunder/122/usr/share/Mod/TechDraw/Templates/A4_LandscapeTD.svg
  TreeRank = 13
  Width = 297
FEATURE [TechDraw::DrawProjGroupItem] ProjItem  label="Front"
  CoarseView = false
  Direction = (0,-1,0)
  Focus = 100
  HardHidden = false
  IsoCount = 0
  IsoHidden = false
  IsoVisible = false
  LockPosition = true
  Perspective = false
  Rotation = 0
  RotationVector = (-1,0,0)
  ScaleType = 2
  ScrubCount = 0
  SeamHidden = false
  SeamVisible = true
  SmoothHidden = false
  SmoothVisible = true
  Source = -> [Body114]
  TreeRank = 16
  Type = 0
  X = 0
  XDirection = (-1,0,0)
  Y = 0
FEATURE [TechDraw::DrawProjGroupItem] ProjItem001  label="Left"
  CoarseView = false
  Direction = (1,-1e-16,0)
  Focus = 100
  HardHidden = false
  IsoCount = 0
  IsoHidden = false
  IsoVisible = false
  LockPosition = false
  Perspective = false
  Rotation = 0
  RotationVector = (1,0,0)
  ScaleType = 2
  ScrubCount = 0
  SeamHidden = false
  SeamVisible = true
  SmoothHidden = false
  SmoothVisible = true
  Source = -> [Body114]
  TreeRank = 18
  Type = 1
  X = 37.6818
  XDirection = (-1e-16,-1,0)
  Y = 0
FEATURE [TechDraw::DrawProjGroupItem] ProjItem002  label="FrontTopLeft"
  CoarseView = false
  Direction = (0.57735,-0.57735,-0.57735)
  Focus = 100
  HardHidden = false
  IsoCount = 0
  IsoHidden = false
  IsoVisible = false
  LockPosition = false
  Perspective = false
  Rotation = 0
  RotationVector = (1,0,0)
  ScaleType = 2
  ScrubCount = 0
  SeamHidden = false
  SeamVisible = true
  SmoothHidden = false
  SmoothVisible = true
  Source = -> [Body114]
  TreeRank = 19
  Type = 6
  X = 37.6818
  XDirection = (-0.707107,-0.707107,0)
  Y = -39.526
FEATURE [TechDraw::DrawProjGroupItem] ProjItem003  label="Right"
  CoarseView = false
  Direction = (-1,-1e-16,0)
  Focus = 100
  HardHidden = false
  IsoCount = 0
  IsoHidden = false
  IsoVisible = false
  LockPosition = false
  Perspective = false
  Rotation = 0
  RotationVector = (1,0,0)
  ScaleType = 2
  ScrubCount = 0
  SeamHidden = false
  SeamVisible = true
  SmoothHidden = false
  SmoothVisible = true
  Source = -> [Body114]
  TreeRank = 20
  Type = 2
  X = -29.5
  XDirection = (-1e-16,1,0)
  Y = 0
FEATURE [TechDraw::DrawProjGroup] ProjGroup
  Anchor = -> ProjItem
  AutoDistribute = true
  LockPosition = false
  ProjectionType = 0
  Rotation = 0
  ScaleType = 0
  Source = -> [Body114]
  TreeRank = 17
  Views = -> [ProjItem,ProjItem001,ProjItem002,ProjItem003]
  X = 119.48
  Y = 135.312
  spacingX = 25
  spacingY = 25
FEATURE [TechDraw::DrawViewDimension] Dimension
  AngleOverride = false
  Arbitrary = true
  ArbitraryTolerances = false
  EqualTolerance = true
  ExtensionAngle = 0
  FormatSpec = M3 x6
  FormatSpecOverTolerance = %+.2w
  FormatSpecUnderTolerance = %+.2w
  Inverted = false
  LineAngle = 0
  LockPosition = false
  MeasureType = 1
  OverTolerance = 0
  References2D = -> [ProjItem]
  Rotation = 0
  ScaleType = 0
  TheoreticalExact = false
  TreeRank = 22
  Type = 5
  UnderTolerance = 0
  X = 17.2609
  Y = 26.5237
FEATURE [TechDraw::DrawViewDimension] Dimension001
  AngleOverride = false
  Arbitrary = false
  ArbitraryTolerances = false
  EqualTolerance = true
  ExtensionAngle = 0
  FormatSpec = R%.2w
  FormatSpecOverTolerance = %+.2w
  FormatSpecUnderTolerance = %+.2w
  Inverted = false
  LineAngle = 0
  LockPosition = false
  MeasureType = 1
  OverTolerance = 0.05
  References2D = -> [ProjItem]
  Rotation = 0
  ScaleType = 0
  TheoreticalExact = false
  TreeRank = 23
  Type = 4
  UnderTolerance = -0.05
  X = -32.3515
  Y = -28.5793
FEATURE [TechDraw::DrawViewDimension] Dimension002
  AngleOverride = false
  Arbitrary = false
  ArbitraryTolerances = false
  EqualTolerance = true
  ExtensionAngle = 0
  FormatSpec = ⌀%.2w
  FormatSpecOverTolerance = %+.2w
  FormatSpecUnderTolerance = %+.2w
  Inverted = false
  LineAngle = 0
  LockPosition = false
  MeasureType = 1
  OverTolerance = 0
  References2D = -> [ProjItem]
  Rotation = 0
  ScaleType = 0
  TheoreticalExact = false
  TreeRank = 24
  Type = 5
  UnderTolerance = 0
  X = 17.4742
  Y = -12.1242
FEATURE [TechDraw::DrawViewDimension] Dimension003
  AngleOverride = false
  Arbitrary = false
  ArbitraryTolerances = false
  EqualTolerance = true
  ExtensionAngle = 0
  FormatSpec = %.2w
  FormatSpecOverTolerance = %+.2w
  FormatSpecUnderTolerance = %+.2w
  Inverted = false
  LineAngle = 0
  LockPosition = false
  MeasureType = 1
  OverTolerance = 0.05
  References2D = -> [ProjItem003]
  Rotation = 0
  ScaleType = 0
  TheoreticalExact = false
  TreeRank = 25
  Type = 1
  UnderTolerance = -0.05
  X = -10.2962
  Y = 24.3142
FEATURE [TechDraw::DrawViewDimension] Dimension005
  AngleOverride = false
  Arbitrary = true
  ArbitraryTolerances = false
  EqualTolerance = true
  ExtensionAngle = 0
  FormatSpec = M3
  FormatSpecOverTolerance = %+.2w
  FormatSpecUnderTolerance = %+.2w
  Inverted = false
  LineAngle = 0
  LockPosition = false
  MeasureType = 1
  OverTolerance = 0
  References2D = -> [ProjItem001]
  Rotation = 0
  ScaleType = 0
  TheoreticalExact = false
  TreeRank = 27
  Type = 5
  UnderTolerance = 0
  X = 12.8924
  Y = 6.87596
FEATURE [TechDraw::DrawViewSection] SectionView  label="Section A - A"
  BaseView = -> ProjItem
  CoarseView = false
  CutSurfaceDisplay = 2
  Direction = (1,0,1e-16)
  FileGeomPattern = /snap/freecad-realthunder/122/usr/share/Mod/TechDraw/PAT/FCPAT.pat
  FileHatchPattern = /snap/freecad-realthunder/122/usr/share/Mod/TechDraw/Patterns/simple.svg
  Focus = 100
  FuseBeforeCut = false
  HardHidden = false
  HatchOffset = (0,0,0)
  HatchRotation = 0
  HatchScale = 1
  IsoCount = 0
  IsoHidden = false
  IsoVisible = false
  LockPosition = false
  NameGeomPattern = Diamant
  Perspective = false
  Rotation = -90
  ScaleType = 2
  ScrubCount = 0
  SeamHidden = false
  SeamVisible = true
  SectionDirection = 4
  SectionNormal = (1,0,1e-16)
  SectionOrigin = (0,0,0)
  SectionSymbol = A
  SmoothHidden = false
  SmoothVisible = true
  Source = -> [Body114]
  TreeRank = 28
  TrimAfterCut = false
  X = 242.358
  XDirection = (-1e-16,0,1)
  Y = 163.668
FEATURE [TechDraw::DrawViewDimension] Dimension006
  AngleOverride = false
  Arbitrary = true
  ArbitraryTolerances = false
  EqualTolerance = true
  ExtensionAngle = 0
  FormatSpec = M3
  FormatSpecOverTolerance = %+.2w
  FormatSpecUnderTolerance = %+.2w
  Inverted = false
  LineAngle = 0
  LockPosition = false
  MeasureType = 1
  OverTolerance = 0
  References2D = -> [SectionView]
  Rotation = 0
  ScaleType = 0
  TheoreticalExact = false
  TreeRank = 29
  Type = 2
  UnderTolerance = 0
  X = 6.48861
  Y = 26.9773
FEATURE [TechDraw::DrawViewDimension] Dimension007
  AngleOverride = false
  Arbitrary = true
  ArbitraryTolerances = false
  EqualTolerance = true
  ExtensionAngle = 0
  FormatSpec = M3
  FormatSpecOverTolerance = %+.2w
  FormatSpecUnderTolerance = %+.2w
  Inverted = false
  LineAngle = 0
  LockPosition = false
  MeasureType = 1
  OverTolerance = 0
  References2D = -> [SectionView]
  Rotation = 0
  ScaleType = 0
  TheoreticalExact = false
  TreeRank = 30
  Type = 2
  UnderTolerance = 0
  X = -12.2231
  Y = 3.19002
FEATURE [TechDraw::DrawViewSection] SectionView001  label="Section B - B"
  BaseView = -> ProjItem
  CoarseView = false
  CutSurfaceDisplay = 2
  Direction = (2e-16,0,-1)
  FileGeomPattern = /snap/freecad-realthunder/122/usr/share/Mod/TechDraw/PAT/FCPAT.pat
  FileHatchPattern = /snap/freecad-realthunder/122/usr/share/Mod/TechDraw/Patterns/simple.svg
  Focus = 100
  FuseBeforeCut = false
  HardHidden = false
  HatchOffset = (0,0,0)
  HatchRotation = 0
  HatchScale = 1
  IsoCount = 0
  IsoHidden = false
  IsoVisible = false
  LockPosition = false
  NameGeomPattern = Diamant
  Perspective = false
  Rotation = 0
  ScaleType = 2
  ScrubCount = 0
  SeamHidden = false
  SeamVisible = true
  SectionDirection = 4
  SectionNormal = (2e-16,0,-1)
  SectionOrigin = (0,5.75,0)
  SectionSymbol = B
  SmoothHidden = false
  SmoothVisible = true
  Source = -> [Body114]
  TreeRank = 31
  TrimAfterCut = false
  X = 242.605
  XDirection = (-1,0,-2e-16)
  Y = 99.7995
FEATURE [TechDraw::DrawViewDimension] Dimension008
  AngleOverride = false
  Arbitrary = true
  ArbitraryTolerances = false
  EqualTolerance = true
  ExtensionAngle = 0
  FormatSpec = M3
  FormatSpecOverTolerance = %+.2w
  FormatSpecUnderTolerance = %+.2w
  Inverted = false
  LineAngle = 0
  LockPosition = false
  MeasureType = 1
  OverTolerance = 0
  References2D = -> [SectionView001]
  Rotation = 0
  ScaleType = 0
  TheoreticalExact = false
  TreeRank = 32
  Type = 2
  UnderTolerance = 0
  X = -28.0724
  Y = 5.1555
FEATURE [TechDraw::DrawViewDimension] Dimension009
  AngleOverride = false
  Arbitrary = false
  ArbitraryTolerances = false
  EqualTolerance = true
  ExtensionAngle = 0
  FormatSpec = %.2w
  FormatSpecOverTolerance = %+.2w
  FormatSpecUnderTolerance = %+.2w
  Inverted = false
  LineAngle = 0
  LockPosition = false
  MeasureType = 1
  OverTolerance = 0.1
  References2D = -> [ProjItem]
  Rotation = 0
  ScaleType = 0
  TheoreticalExact = false
  TreeRank = 33
  Type = 2
  UnderTolerance = -0.1
  X = -19.7146
  Y = 1.05555
FEATURE [TechDraw::DrawViewAnnotation] Annotation
  Font = osifont
  LineSpace = 100
  LockPosition = false
  MaxWidth = -1
  Rotation = 0
  ScaleType = 0
  Text = Section A - A
  TextSize = 5
  TextStyle = 0
  TreeRank = 34
  X = 242.474
  Y = 138.232
FEATURE [TechDraw::DrawViewAnnotation] Annotation002
  Font = osifont
  LineSpace = 100
  LockPosition = false
  MaxWidth = -1
  Rotation = 0
  ScaleType = 0
  Text = Section B - B
  TextSize = 5
  TextStyle = 0
  TreeRank = 35
  X = 242.694
  Y = 88.9341
FEATURE [TechDraw::DrawPage] Page  label="NoyauRoueCNC - Plan"
  KeepUpdated = true
  NextBalloonIndex = 1
  ProjectionType = 0
  Template = -> Template
  TreeRank = 14
  Views = -> [ProjGroup,Dimension,Dimension001,Dimension002,Dimension003,Dimension005,SectionView,Dimension006,Dimension007,SectionView001,Dimension008,Dimension009,Annotation,Annotation002]
FEATURE [App::Part] Part  label="OmniWheelAssembled"
  ClaimAllChildren = false
  ExportMode = 1
  Group = -> [Link,Link092,Part048,Group011,Screw,Screw005,Screw006,Screw007,Screw008,Screw009,Body114,Page]
  Origin = -> Origin079
  Placement = pos=(0,-70,0) rot=(0,0,1;0rad)
  TreeRank = 0
  _ExportChildren = -> [Link,Link092,Part048,Group011,Body114,Page]
  _GroupVersion = 1
FEATURE [App::DocumentObjectGroup] Group001  label="Wheels"
  ClaimAllChildren = true
  ExportMode = 1
  Group = -> [Part018,Part]
  TreeRank = 0
  _GroupVersion = 1
FEATURE [PartDesign::FeatureBase] Clone004
  BaseFeature = -> Body112
  FixShape = 1
  InvalidShape = false
  NewSolid = false
  Suppress = false
  TreeRank = 45
  ValidateShape = true
FEATURE [PartDesign::Pad] Pad099
  AddSubType = 0
  AlongSketchNormal = false
  AutoTaperInnerAngle = true
  BaseFeature = -> Clone004
  CheckUpToFaceLimits = true
  ClaimChildren = false
  Direction = (1,0,0)
  Fit = 0
  FitJoin = 0
  FixShape = 1
  InnerFit = 0
  InnerFitJoin = 0
  InvalidShape = false
  Length = 25
  Length2 = 10
  Linearize = true
  NewSolid = false
  Profile = -> Clone004 [Face19]
  Refine = true
  Suppress = false
  TaperInnerAngle = 0
  TaperInnerAngleRev = 0
  TreeRank = 47
  Type = 0
  ValidateShape = true
  _ProfileBasedVersion = 1
FEATURE [PartDesign::Body] Body115  label="MGN9-225mm-Custom"
  AutoGroupSolids = false
  BaseFeature = -> Body112
  ClaimAllChildren = false
  ExportMode = 0
  FixShape = 1
  Group = -> [Clone004,Pad099]
  InvalidShape = false
  Origin = -> Origin218
  SingleSolid = true
  Tip = -> Pad099
  TreeRank = 46
  ValidateShape = false
  _ExportChildren = -> [Clone004,Pad099]
  _GroupVersion = 1
FEATURE [App::Part] Part049  label="MGN9C-RAIL"
  ClaimAllChildren = false
  ExportMode = 1
  Group = -> [Part__Feature002,Body112,Part__Feature001,Body115]
  Origin = -> Origin215
  TreeRank = 0
  _ExportChildren = -> [Part__Feature002,Body112,Part__Feature001,Body115]
  _GroupVersion = 1
FEATURE [Sketcher::SketchObject] Sketch250
  ArcFitTolerance = 1e-06
  AttachmentSupport = -> [XZ_Plane142]
  ExternalBSplineMaxDegree = 5
  ExternalBSplineTolerance = 0.0001
  FixShape = 1
  FullyConstrained = true
  InternalTolerance = 1e-06
  InvalidShape = false
  MakeInternals = false
  MapMode = 5
  Placement = pos=(0,0,0) rot=(1,0,0;1.5708rad)
  Support = -> [XZ_Plane142]
  TreeRank = 59
  ValidateShape = false
  sketch-geometry (7):
    g0: LineSegment StartX=-4.7 StartY=-30 StartZ=0 EndX=-4.7 EndY=30 EndZ=0
    g1: LineSegment StartX=-4.7 StartY=30 StartZ=0 EndX=4.7 EndY=30 EndZ=0
    g2: LineSegment StartX=4.7 StartY=30 StartZ=0 EndX=4.7 EndY=-30 EndZ=0
    g3: LineSegment StartX=4.7 StartY=-30 StartZ=0 EndX=-4.7 EndY=-30 EndZ=0
    g4: GeomPoint [constr] X=0 Y=0 Z=0
    g5: Circle CenterX=0 CenterY=23.5 CenterZ=0 NormalX=0 NormalY=0 NormalZ=1 AngleXU=0 Radius=1.5
    g6: Circle CenterX=0 CenterY=-23.5 CenterZ=0 NormalX=0 NormalY=0 NormalZ=1 AngleXU=0 Radius=1.5
  constraints (17):
    c: Coincident(g0,g1)
    c: Coincident(g1,g2)
    c: Coincident(g2,g3)
    c: Coincident(g3,g0)
    c: Horizontal(g1)
    c: Horizontal(g3)
    c: Vertical(g0)
    c: Vertical(g2)
    c: Symmetric(g1,g0,g4)
    c: Coincident(g4,g-1)
    c: PointOnObject(g5,g-2)
    c: Symmetric(g5,g6,g4)
    c: DistanceY(g6,g5) = 47
    c: DistanceY(g2,g2) = 60
    c: DistanceX(g1,g1) = 9.4
    c: Equal(g5,g6)
    c: Diameter(g5) = 3
FEATURE [PartDesign::Pad] Pad100
  AddSubType = 0
  AlongSketchNormal = false
  AutoTaperInnerAngle = true
  CheckUpToFaceLimits = true
  ClaimChildren = false
  Direction = (0,-1,2e-16)
  Fit = 0
  FitJoin = 0
  FixShape = 1
  InnerFit = 0
  InnerFitJoin = 0
  InvalidShape = false
  Length = 3
  Length2 = 10
  Linearize = true
  NewSolid = false
  Profile = -> Sketch250
  ReferenceAxis = -> Sketch250 [N_Axis]
  Refine = true
  Suppress = false
  TaperInnerAngle = 0
  TaperInnerAngleRev = 0
  TreeRank = 60
  Type = 0
  ValidateShape = true
  _ProfileBasedVersion = 1
FEATURE [PartDesign::Chamfer] Chamfer057
  AddSubType = 0
  Angle = 45
  Base = -> Pad100 [Edge15,Edge18]
  BaseFeature = -> Pad100
  ChamferType = 0
  FixShape = 1
  FlipDirection = false
  InvalidShape = false
  NewSolid = false
  Refine = true
  Size = 2
  Size2 = 1
  SupportTransform = false
  Suppress = false
  TreeRank = 61
  UseAllEdges = false
  ValidateShape = true
FEATURE [PartDesign::Fillet] Fillet047
  AddSubType = 0
  Base = -> Chamfer057 [Edge17,Edge18,Edge16,Edge19]
  BaseFeature = -> Chamfer057
  FixShape = 1
  InvalidShape = false
  NewSolid = false
  Radius = 1
  Refine = true
  SupportTransform = false
  Suppress = false
  TreeRank = 62
  UseAllEdges = false
  ValidateShape = true
FEATURE [PartDesign::Fillet] Fillet048
  AddSubType = 0
  Base = -> Fillet047 [Edge13,Edge1]
  BaseFeature = -> Fillet047
  FixShape = 1
  InvalidShape = false
  NewSolid = false
  Radius = 0.4
  Refine = true
  SupportTransform = false
  Suppress = false
  TreeRank = 63
  UseAllEdges = false
  ValidateShape = true
FEATURE [PartDesign::Body] Body116  label="FlatMagnet - 60x13,5x5 mm - 30kg"
  AutoGroupSolids = false
  ClaimAllChildren = false
  ExportMode = 0
  FixShape = 1
  Group = -> [Sketch250,Pad100,Chamfer057,Fillet047,Fillet048]
  InvalidShape = false
  Origin = -> Origin219
  SingleSolid = true
  Tip = -> Fillet048
  TreeRank = 58
  ValidateShape = false
  _ExportChildren = -> [Pad100,Chamfer057,Fillet047,Fillet048]
  _GroupVersion = 1
FEATURE [App::DocumentObjectGroup] Group012  label="Magnets"
  ClaimAllChildren = true
  ExportMode = 1
  Group = -> [Body116]
  TreeRank = 48
  _GroupVersion = 1
FEATURE [Sketcher::SketchObject] Sketch251
  ArcFitTolerance = 1e-06
  AttachmentSupport = -> [XZ_Plane143]
  ExternalBSplineMaxDegree = 5
  ExternalBSplineTolerance = 0.0001
  FullyConstrained = true
  InternalTolerance = 1e-06
  InvalidShape = false
  MakeInternals = false
  MapMode = 5
  Placement = pos=(0,0,0) rot=(1,0,0;1.5708rad)
  Support = -> [XZ_Plane143]
  TreeRank = 77
  ValidateShape = false
  sketch-geometry (8):
    g0: LineSegment StartX=0 StartY=6.5 StartZ=0 EndX=10.75 EndY=6.5 EndZ=0
    g1: LineSegment StartX=10.75 StartY=6.5 StartZ=0 EndX=10.75 EndY=1.5 EndZ=0
    g2: LineSegment StartX=10.75 StartY=1.5 StartZ=0 EndX=11.75 EndY=1.5 EndZ=0
    g3: LineSegment StartX=11.75 StartY=1.5 StartZ=0 EndX=11.75 EndY=0 EndZ=0
    g4: LineSegment StartX=11.75 StartY=0 StartZ=0 EndX=8 EndY=0 EndZ=0
    g5: LineSegment StartX=8 StartY=0 StartZ=0 EndX=8 EndY=-15 EndZ=0
    g6: LineSegment StartX=8 StartY=-15 StartZ=0 EndX=0 EndY=-15 EndZ=0
    g7: LineSegment StartX=0 StartY=-15 StartZ=0 EndX=0 EndY=6.5 EndZ=0
  constraints (24):
    c: PointOnObject(g0,g-2)
    c: Horizontal(g0)
    c: Coincident(g0,g1)
    c: Coincident(g1,g2)
    c: Horizontal(g2)
    c: Coincident(g2,g3)
    c: Vertical(g3)
    c: Coincident(g3,g4)
    c: Horizontal(g4)
    c: Coincident(g4,g5)
    c: Vertical(g5)
    c: Coincident(g5,g6)
    c: Horizontal(g6)
    c: Coincident(g6,g7)
    c: Coincident(g7,g0)
    c: Vertical(g7)
    c: Vertical(g1)
    c: PointOnObject(g4,g-1)
    c: DistanceX(g6,g6) = 8
    c: DistanceX(g3) = 11.75
    c: DistanceY(g3,g3) = 1.5
    c: DistanceX(g1) = 10.75
    c: DistanceY(g1,g1) = 5
    c: DistanceY(g5,g5) = 15
FEATURE [PartDesign::Revolution] Revolution
  AddSubType = 0
  Angle = 360
  Axis = (0,2e-16,1)
  Base = (0,0,0)
  ClaimChildren = false
  Fit = 0
  FitJoin = 0
  InnerFit = 0
  InnerFitJoin = 0
  InvalidShape = false
  Linearize = true
  NewSolid = false
  Profile = -> Sketch251
  ReferenceAxis = -> Sketch251 [V_Axis]
  Refine = true
  Reversed = true
  Suppress = false
  TreeRank = 78
  ValidateShape = true
  _ProfileBasedVersion = 1
FEATURE [PartDesign::Body] Body117  label="LBM4-16mm-Body"
  AutoGroupSolids = false
  ClaimAllChildren = false
  ExportMode = 0
  Group = -> [Sketch251,Revolution]
  InvalidShape = false
  Origin = -> Origin221
  Tip = -> Revolution
  TreeRank = 76
  ValidateShape = false
  _ExportChildren = -> [Revolution]
  _GroupVersion = 1
FEATURE [Sketcher::SketchObject] Sketch252
  ArcFitTolerance = 1e-06
  AttachmentSupport = -> [XZ_Plane144]
  ExternalBSplineMaxDegree = 5
  ExternalBSplineTolerance = 0.0001
  FullyConstrained = true
  InternalTolerance = 1e-06
  InvalidShape = false
  MakeInternals = false
  MapMode = 5
  Placement = pos=(0,0,0) rot=(1,0,0;1.5708rad)
  Support = -> [XZ_Plane144]
  TreeRank = 89
  ValidateShape = false
  sketch-geometry (8):
    g0: LineSegment StartX=0 StartY=10.5 StartZ=0 EndX=13 EndY=10.5 EndZ=0
    g1: LineSegment StartX=13 StartY=10.5 StartZ=0 EndX=13 EndY=8 EndZ=0
    g2: LineSegment StartX=13 StartY=8 StartZ=0 EndX=13.5 EndY=8 EndZ=0
    g3: LineSegment StartX=13.5 StartY=8 StartZ=0 EndX=13.5 EndY=3 EndZ=0
    g4: LineSegment StartX=13.5 StartY=3 StartZ=0 EndX=12.75 EndY=3 EndZ=0
    g5: LineSegment StartX=12.75 StartY=3 StartZ=0 EndX=12.75 EndY=0 EndZ=0
    g6: LineSegment StartX=12.75 StartY=0 StartZ=0 EndX=0 EndY=0 EndZ=0
    g7: LineSegment StartX=0 StartY=0 StartZ=0 EndX=0 EndY=10.5 EndZ=0
  constraints (23):
    c: PointOnObject(g0,g-2)
    c: Horizontal(g0)
    c: Coincident(g0,g1)
    c: Vertical(g1)
    c: Coincident(g1,g2)
    c: Horizontal(g2)
    c: Coincident(g2,g3)
    c: Vertical(g3)
    c: Coincident(g3,g4)
    c: Horizontal(g4)
    c: Coincident(g4,g5)
    c: PointOnObject(g5,g-1)
    c: Vertical(g5)
    c: Coincident(g5,g6)
    c: Coincident(g6,g-1)
    c: Coincident(g6,g7)
    c: Coincident(g7,g0)
    c: DistanceY(g3,g3) = 5
    c: DistanceX(g0,g0) = 13
    c: DistanceX(g2) = 13.5
    c: DistanceY(g7,g7) = 10.5
    c: DistanceY(g5,g5) = 3
    c: DistanceX(g6,g6) = 12.75
FEATURE [PartDesign::Revolution] Revolution022
  AddSubType = 0
  Angle = 360
  Axis = (0,2e-16,1)
  Base = (0,0,0)
  ClaimChildren = false
  Fit = 0
  FitJoin = 0
  InnerFit = 0
  InnerFitJoin = 0
  InvalidShape = false
  Linearize = true
  NewSolid = false
  Profile = -> Sketch252
  ReferenceAxis = -> Sketch252 [V_Axis]
  Refine = true
  Reversed = true
  Suppress = false
  TreeRank = 90
  ValidateShape = true
  _ProfileBasedVersion = 1
FEATURE [PartDesign::Fillet] Fillet049
  AddSubType = 0
  Base = -> Revolution022 [Edge1]
  BaseFeature = -> Revolution022
  InvalidShape = false
  NewSolid = false
  Radius = 2
  Refine = true
  SupportTransform = false
  Suppress = false
  TreeRank = 91
  UseAllEdges = false
  ValidateShape = true
FEATURE [PartDesign::Chamfer] Chamfer058
  AddSubType = 0
  Angle = 45
  Base = -> Fillet049 [Edge6,Edge8]
  BaseFeature = -> Fillet049
  ChamferType = 0
  FlipDirection = false
  InvalidShape = false
  NewSolid = false
  Refine = true
  Size = 0.4
  Size2 = 1
  SupportTransform = false
  Suppress = false
  TreeRank = 92
  UseAllEdges = false
  ValidateShape = true
FEATURE [PartDesign::Fillet] Fillet050
  AddSubType = 0
  Base = -> Chamfer058 [Edge15]
  BaseFeature = -> Chamfer058
  InvalidShape = false
  NewSolid = false
  Radius = 0.2
  Refine = true
  SupportTransform = false
  Suppress = false
  TreeRank = 93
  UseAllEdges = false
  ValidateShape = true
FEATURE [PartDesign::Body] Body118  label="LBM4-Button"
  AutoGroupSolids = false
  ClaimAllChildren = false
  ExportMode = 0
  Group = -> [Sketch252,Revolution022,Fillet049,Chamfer058,Fillet050]
  InvalidShape = false
  Origin = -> Origin222
  Placement = pos=(0,0,5.5) rot=(0,0,1;0rad)
  Tip = -> Fillet050
  TreeRank = 88
  ValidateShape = false
  _ExportChildren = -> [Revolution022,Fillet049,Chamfer058,Fillet050]
  _GroupVersion = 1
FEATURE [Sketcher::SketchObject] Sketch253
  ArcFitTolerance = 1e-06
  AttachmentSupport = -> [XZ_Plane145]
  ExternalBSplineMaxDegree = 5
  ExternalBSplineTolerance = 0.0001
  FullyConstrained = true
  InternalTolerance = 1e-06
  InvalidShape = false
  MakeInternals = false
  MapMode = 5
  Placement = pos=(0,0,0) rot=(1,0,0;1.5708rad)
  Support = -> [XZ_Plane145]
  TreeRank = 104
  ValidateShape = false
  sketch-geometry (1):
    g0: Circle CenterX=8.5 CenterY=0 CenterZ=0 NormalX=0 NormalY=0 NormalZ=1 AngleXU=0 Radius=0.75
  constraints (3):
    c: PointOnObject(g0,g-1)
    c: Diameter(g0) = 1.5
    c: DistanceX(g0) = 8.5
FEATURE [PartDesign::Revolution] Revolution023
  AddSubType = 0
  Angle = 360
  Axis = (0,2e-16,1)
  Base = (0,0,0)
  ClaimChildren = false
  Fit = 0
  FitJoin = 0
  InnerFit = 0
  InnerFitJoin = 0
  InvalidShape = false
  Linearize = true
  NewSolid = false
  Profile = -> Sketch253
  ReferenceAxis = -> Sketch253 [V_Axis]
  Refine = true
  Reversed = true
  Suppress = false
  TreeRank = 105
  ValidateShape = true
  _ProfileBasedVersion = 1
FEATURE [PartDesign::Body] Body119  label="LBM4-Joint"
  AutoGroupSolids = false
  ClaimAllChildren = false
  ExportMode = 0
  Group = -> [Sketch253,Revolution023]
  InvalidShape = false
  Origin = -> Origin223
  Placement = pos=(0,0,-0.7) rot=(0,0,1;0rad)
  Tip = -> Revolution023
  TreeRank = 103
  ValidateShape = false
  _ExportChildren = -> [Revolution023]
  _GroupVersion = 1
FEATURE [PartDesign::SubShapeBinder] Pad101_Profile  label="Pad101_Profile(Revolution)"
  BindCopyOnChange = 0
  BindMode = 0
  ClaimChildren = false
  Context = -> Group008 [Part050.Body120.Pad101_Profile.]
  EdgeTolerance = 1e-06
  FillStyle = 0
  Fuse = false
  InvalidShape = false
  MakeFace = true
  MergeEdges = true
  OffsetFill = false
  OffsetIntersection = false
  OffsetJoinType = 0
  OffsetOpenResult = false
  Outline = false
  PartialLoad = false
  Relative = true
  SplitEdges = false
  Support = -> [Revolution[Face7]]
  TightBound = false
  TreeRank = 117
  ValidateShape = false
  _Version = 8
FEATURE [PartDesign::Pad] Pad101
  AddSubType = 0
  AlongSketchNormal = false
  AutoTaperInnerAngle = true
  CheckUpToFaceLimits = true
  ClaimChildren = false
  Direction = (0,-2e-16,-1)
  Fit = 0
  FitJoin = 0
  InnerFit = 0
  InnerFitJoin = 0
  InvalidShape = false
  Length = 8
  Length2 = 10
  Linearize = true
  NewSolid = false
  Profile = -> Pad101_Profile
  Refine = true
  Suppress = false
  TaperInnerAngle = 0
  TaperInnerAngleRev = 0
  TreeRank = 118
  Type = 0
  ValidateShape = true
  _ProfileBasedVersion = 1
FEATURE [PartDesign::Body] Body120  label="LBM4-CapsuleConnecteur"
  AutoGroupSolids = false
  ClaimAllChildren = false
  ExportMode = 0
  Group = -> [Pad101,Pad101_Profile]
  InvalidShape = false
  Origin = -> Origin224
  Tip = -> Pad101
  TreeRank = 115
  ValidateShape = false
  _ExportChildren = -> [Pad101]
  _GroupVersion = 1
FEATURE [Sketcher::SketchObject] Sketch254
  ArcFitTolerance = 1e-06
  AttachmentSupport = -> [XY_Plane147]
  ExternalBSplineMaxDegree = 5
  ExternalBSplineTolerance = 0.0001
  FullyConstrained = true
  InternalTolerance = 1e-06
  InvalidShape = false
  MakeInternals = false
  MapMode = 5
  Support = -> [XY_Plane147]
  TreeRank = 129
  ValidateShape = false
  sketch-geometry (8):
    g0: LineSegment StartX=10.9697 StartY=0 StartZ=0 EndX=5.48483 EndY=9.5 EndZ=0
    g1: LineSegment StartX=5.48483 StartY=9.5 StartZ=0 EndX=-5.48483 EndY=9.5 EndZ=0
    g2: LineSegment StartX=-5.48483 StartY=9.5 StartZ=0 EndX=-10.9697 EndY=-1.8e-15 EndZ=0
    g3: LineSegment StartX=-10.9697 StartY=-1.3e-15 StartZ=0 EndX=-5.48483 EndY=-9.5 EndZ=0
    g4: LineSegment StartX=-5.48483 StartY=-9.5 StartZ=0 EndX=5.48483 EndY=-9.5 EndZ=0
    g5: LineSegment StartX=5.48483 StartY=-9.5 StartZ=0 EndX=10.9697 EndY=0 EndZ=0
    g6: Circle [constr] CenterX=0 CenterY=0 CenterZ=0 NormalX=0 NormalY=0 NormalZ=1 AngleXU=0 Radius=10.9697
    g7: Circle CenterX=0 CenterY=0 CenterZ=0 NormalX=0 NormalY=0 NormalZ=1 AngleXU=0 Radius=7.5
  constraints (18):
    c: Coincident(g0,g1)
    c: Coincident(g1,g2)
    c: Coincident(g2,g3)
    c: Coincident(g3,g4)
    c: Coincident(g4,g5)
    c: Coincident(g5,g0)
    c: Equal(g0, g1-g5) x5
    c: PointOnObject(g0,g6)
    c: PointOnObject(g1,g6)
    c: PointOnObject(g2,g6)
    c: PointOnObject(g3,g6)
    c: PointOnObject(g4,g6)
    c: PointOnObject(g5,g6)
    c: Coincident(g6,g-1)
    c: PointOnObject(g5,g-1)
    c: DistanceY(g4,g0) = 19
    c: Coincident(g7,g6)
    c: Diameter(g7) = 15
FEATURE [PartDesign::Pad] Pad102
  AddSubType = 0
  AlongSketchNormal = false
  AutoTaperInnerAngle = true
  CheckUpToFaceLimits = true
  ClaimChildren = false
  Direction = (0,0,1)
  Fit = 0
  FitJoin = 0
  InnerFit = 0
  InnerFitJoin = 0
  InvalidShape = false
  Length = 2.8
  Length2 = 10
  Linearize = true
  Midplane = true
  NewSolid = false
  Profile = -> Sketch254
  ReferenceAxis = -> Sketch254 [N_Axis]
  Refine = true
  Suppress = false
  TaperInnerAngle = 0
  TaperInnerAngleRev = 0
  TreeRank = 130
  Type = 0
  ValidateShape = true
  _ProfileBasedVersion = 1
FEATURE [PartDesign::Fillet] Fillet051
  AddSubType = 0
  Base = -> Pad102 [Edge1,Edge14,Edge2,Edge5,Edge8,Edge11]
  BaseFeature = -> Pad102
  InvalidShape = false
  NewSolid = false
  Radius = 0.6
  Refine = true
  SupportTransform = false
  Suppress = false
  TreeRank = 132
  UseAllEdges = false
  ValidateShape = true
FEATURE [Sketcher::SketchObject] Sketch255
  ArcFitTolerance = 1e-06
  AttachmentSupport = -> [XZ_Plane147]
  ExternalBSplineMaxDegree = 5
  ExternalBSplineTolerance = 0.0001
  FullyConstrained = false
  InternalTolerance = 1e-06
  InvalidShape = false
  MakeInternals = false
  MapMode = 5
  Placement = pos=(0,0,0) rot=(1,0,0;1.5708rad)
  Support = -> [XZ_Plane147]
  TreeRank = 133
  ValidateShape = false
  sketch-geometry (3):
    g0: LineSegment StartX=8.99798 StartY=1.52118 StartZ=0 EndX=10.9649 EndY=0.806128 EndZ=0
    g1: LineSegment StartX=10.9649 StartY=0.806128 StartZ=0 EndX=10.9649 EndY=1.52118 EndZ=0
    g2: LineSegment StartX=10.9649 StartY=1.52118 StartZ=0 EndX=8.99798 EndY=1.52118 EndZ=0
  constraints (5):
    c: Coincident(g0,g1)
    c: Vertical(g1)
    c: Coincident(g1,g2)
    c: Coincident(g2,g0)
    c: Horizontal(g2)
FEATURE [PartDesign::Groove] Groove005
  AddSubType = 1
  Angle = 360
  Axis = (0,2e-16,1)
  Base = (0,0,0)
  BaseFeature = -> Fillet051
  ClaimChildren = false
  Fit = 0
  FitJoin = 0
  InnerFit = 0
  InnerFitJoin = 0
  InvalidShape = false
  Linearize = true
  NewSolid = false
  Profile = -> Sketch255
  ReferenceAxis = -> Sketch255 [V_Axis]
  Refine = true
  Suppress = false
  TreeRank = 134
  ValidateShape = true
  _ProfileBasedVersion = 1
FEATURE [PartDesign::Mirrored] Mirrored
  AddSubType = 0
  BaseFeature = -> Groove005
  CopyShape = false
  InvalidShape = false
  MirrorPlane = -> XY_Plane147
  NewSolid = false
  OriginalSubs = -> [Groove005]
  Originals = -> [Groove005]
  ParallelTransform = true
  Refine = true
  SubTransform = true
  Suppress = false
  TreeRank = 135
  ValidateShape = true
  _Version = 4
FEATURE [PartDesign::Body] Body121  label="LBM4-Ecrou"
  AutoGroupSolids = false
  ClaimAllChildren = false
  ExportMode = 0
  Group = -> [Sketch254,Pad102,Fillet051,Sketch255,Groove005,Mirrored]
  InvalidShape = false
  Origin = -> Origin225
  Placement = pos=(0,0,-4.5) rot=(0,0,1;0rad)
  Tip = -> Mirrored
  TreeRank = 128
  ValidateShape = false
  _ExportChildren = -> [Pad102,Fillet051,Groove005,Mirrored]
  _GroupVersion = 1
FEATURE [App::Part] Part050  label="BAU-LBM4-16mm"
  ClaimAllChildren = false
  ExportMode = 1
  Group = -> [Body117,Body118,Body119,Body120,Body121]
  Origin = -> Origin220
  TreeRank = 66
  _ExportChildren = -> [Body117,Body118,Body119,Body120,Body121]
  _GroupVersion = 1
FEATURE [App::DocumentObjectGroup] Group008  label="ElectricComponents"
  ClaimAllChildren = true
  ExportMode = 1
  Group = -> [Part036,Solid002,Part014,Part045,Part050]
  TreeRank = 0
  _GroupVersion = 1
FEATURE [Image::ImagePlane] opera_20241026_100449  label="AdaptatorSuctionCupM5"
  TreeRank = 147
  XSize = 114.051
  YSize = 79.1215
FEATURE [Sketcher::SketchObject] Sketch256
  ArcFitTolerance = 1e-06
  AttachmentSupport = -> [XY_Plane148]
  ExternalBSplineMaxDegree = 5
  ExternalBSplineTolerance = 0.0001
  FixShape = 1
  FullyConstrained = true
  InternalTolerance = 1e-06
  InvalidShape = false
  MakeInternals = false
  MapMode = 5
  Support = -> [XY_Plane148]
  TreeRank = 148
  ValidateShape = false
  sketch-geometry (7):
    g0: LineSegment StartX=0 StartY=-6.9282 StartZ=0 EndX=6 EndY=-3.4641 EndZ=0
    g1: LineSegment StartX=6 StartY=-3.4641 StartZ=0 EndX=6 EndY=3.4641 EndZ=0
    g2: LineSegment StartX=6 StartY=3.4641 StartZ=0 EndX=0 EndY=6.9282 EndZ=0
    g3: LineSegment StartX=1e-16 StartY=6.9282 StartZ=0 EndX=-6 EndY=3.4641 EndZ=0
    g4: LineSegment StartX=-6 StartY=3.4641 StartZ=0 EndX=-6 EndY=-3.4641 EndZ=0
    g5: LineSegment StartX=-6 StartY=-3.4641 StartZ=0 EndX=0 EndY=-6.9282 EndZ=0
    g6: Circle [constr] CenterX=0 CenterY=0 CenterZ=0 NormalX=0 NormalY=0 NormalZ=1 AngleXU=0 Radius=6.9282
  constraints (16):
    c: Coincident(g0,g1)
    c: Coincident(g1,g2)
    c: Coincident(g2,g3)
    c: Coincident(g3,g4)
    c: Coincident(g4,g5)
    c: Coincident(g5,g0)
    c: Equal(g0, g1-g5) x5
    c: PointOnObject(g0,g6)
    c: PointOnObject(g1,g6)
    c: PointOnObject(g2,g6)
    c: PointOnObject(g3,g6)
    c: PointOnObject(g4,g6)
    c: PointOnObject(g5,g6)
    c: Coincident(g6,g-1)
    c: PointOnObject(g5,g-2)
    c: DistanceX(g3,g1) = 12
FEATURE [PartDesign::Pad] Pad103
  AddSubType = 0
  AlongSketchNormal = false
  AutoTaperInnerAngle = true
  CheckUpToFaceLimits = true
  ClaimChildren = false
  Direction = (0,0,1)
  Fit = 0
  FitJoin = 0
  FixShape = 1
  InnerFit = 0
  InnerFitJoin = 0
  InvalidShape = false
  Length = 8
  Length2 = 10
  Linearize = true
  NewSolid = false
  Profile = -> Sketch256
  ReferenceAxis = -> Sketch256 [N_Axis]
  Refine = true
  Suppress = false
  TaperInnerAngle = 0
  TaperInnerAngleRev = 0
  TreeRank = 149
  Type = 0
  ValidateShape = true
  _ProfileBasedVersion = 1
FEATURE [Sketcher::SketchObject] Sketch257
  ArcFitTolerance = 1e-06
  AttachmentSupport = -> [YZ_Plane148]
  ExternalBSplineMaxDegree = 5
  ExternalBSplineTolerance = 0.0001
  FixShape = 1
  FullyConstrained = true
  InternalTolerance = 1e-06
  InvalidShape = false
  MakeInternals = false
  MapMode = 5
  Placement = pos=(0,0,0) rot=(0.57735,0.57735,0.57735;2.0944rad)
  Support = -> [YZ_Plane148]
  TreeRank = 150
  ValidateShape = false
  sketch-geometry (6):
    g0: LineSegment StartX=0 StartY=0 StartZ=0 EndX=2.5 EndY=0 EndZ=0
    g1: LineSegment StartX=2.5 StartY=0 StartZ=0 EndX=2.5 EndY=-3 EndZ=0
    g2: LineSegment StartX=2.5 StartY=-3 StartZ=0 EndX=3.5 EndY=-3 EndZ=0
    g3: LineSegment StartX=3.5 StartY=-3 StartZ=0 EndX=3.5 EndY=-5.4 EndZ=0
    g4: LineSegment StartX=3.5 StartY=-5.4 StartZ=0 EndX=0 EndY=-5.4 EndZ=0
    g5: LineSegment StartX=0 StartY=-5.4 StartZ=0 EndX=0 EndY=0 EndZ=0
  constraints (17):
    c: Coincident(g-1,g0)
    c: PointOnObject(g0,g-1)
    c: Coincident(g0,g1)
    c: Vertical(g1)
    c: Coincident(g1,g2)
    c: Horizontal(g2)
    c: Coincident(g2,g3)
    c: Vertical(g3)
    c: Coincident(g3,g4)
    c: PointOnObject(g4,g-2)
    c: Horizontal(g4)
    c: Coincident(g4,g5)
    c: Coincident(g5,g0)
    c: DistanceX(g0,g0) = 2.5
    c: DistanceX(g4,g4) = 3.5
    c: DistanceY(g1,g1) = 3
    c: DistanceY(g3,g0) = 5.4
FEATURE [PartDesign::Revolution] Revolution024
  AddSubType = 0
  Angle = 360
  Axis = (-2e-16,3e-16,1)
  Base = (0,0,0)
  BaseFeature = -> Pad103
  ClaimChildren = false
  Fit = 0
  FitJoin = 0
  FixShape = 1
  InnerFit = 0
  InnerFitJoin = 0
  InvalidShape = false
  Linearize = true
  NewSolid = false
  Profile = -> Sketch257
  ReferenceAxis = -> Sketch257 [V_Axis]
  Refine = true
  Reversed = true
  Suppress = false
  TreeRank = 151
  ValidateShape = true
  _ProfileBasedVersion = 1
FEATURE [Sketcher::SketchObject] Sketch258
  ArcFitTolerance = 1e-06
  AttachmentSupport = -> [XZ_Plane148]
  ExternalBSplineMaxDegree = 5
  ExternalBSplineTolerance = 0.0001
  ExternalGeometry = -> [Revolution024]
  FixShape = 1
  FullyConstrained = true
  InternalTolerance = 1e-06
  InvalidShape = false
  MakeInternals = false
  MapMode = 5
  Placement = pos=(0,0,0) rot=(1,0,0;1.5708rad)
  Support = -> [XZ_Plane148]
  TreeRank = 152
  ValidateShape = false
  sketch-geometry (6):
    g0: LineSegment StartX=0 StartY=8 StartZ=0 EndX=0 EndY=16 EndZ=0
    g1: LineSegment StartX=0 StartY=16 StartZ=0 EndX=2.5 EndY=16 EndZ=0
    g2: LineSegment StartX=2.5 StartY=16 StartZ=0 EndX=2.5 EndY=10 EndZ=0
    g3: LineSegment StartX=2.5 StartY=10 StartZ=0 EndX=1.75 EndY=10 EndZ=0
    g4: LineSegment StartX=1.75 StartY=10 StartZ=0 EndX=1.75 EndY=8 EndZ=0
    g5: LineSegment StartX=1.75 StartY=8 StartZ=0 EndX=0 EndY=8 EndZ=0
  constraints (18):
    c: PointOnObject(g0,g-2)
    c: PointOnObject(g0,g-2)
    c: Coincident(g0,g1)
    c: Horizontal(g1)
    c: Coincident(g1,g2)
    c: Coincident(g2,g3)
    c: Horizontal(g3)
    c: Coincident(g3,g4)
    c: Vertical(g4)
    c: Coincident(g4,g5)
    c: Coincident(g5,g0)
    c: Horizontal(g5)
    c: Vertical(g2)
    c: PointOnObject(g4,g-3)
    c: DistanceX(g1,g1) = 2.5
    c: DistanceX(g5,g5) = 1.75
    c: DistanceY(g0,g0) = 8
    c: DistanceY(g2,g2) = 6
FEATURE [PartDesign::Revolution] Revolution025
  AddSubType = 0
  Angle = 360
  Axis = (0,2e-16,1)
  Base = (0,0,0)
  BaseFeature = -> Revolution024
  ClaimChildren = false
  Fit = 0
  FitJoin = 0
  FixShape = 1
  InnerFit = 0
  InnerFitJoin = 0
  InvalidShape = false
  Linearize = true
  NewSolid = false
  Profile = -> Sketch258
  ReferenceAxis = -> Sketch258 [V_Axis]
  Refine = true
  Reversed = true
  Suppress = false
  TreeRank = 153
  ValidateShape = true
  _ProfileBasedVersion = 1
FEATURE [PartDesign::Chamfer] Chamfer059
  AddSubType = 0
  Angle = 45
  Base = -> Revolution025 [Edge26,Edge29]
  BaseFeature = -> Revolution025
  ChamferType = 0
  FixShape = 1
  FlipDirection = false
  InvalidShape = false
  NewSolid = false
  Refine = true
  Size = 0.5
  Size2 = 1
  SupportTransform = false
  Suppress = false
  TreeRank = 154
  UseAllEdges = false
  ValidateShape = true
FEATURE [Sketcher::SketchObject] Sketch259
  ArcFitTolerance = 1e-06
  AttachmentSupport = -> [Chamfer059]
  ExternalBSplineMaxDegree = 5
  ExternalBSplineTolerance = 0.0001
  FixShape = 1
  FullyConstrained = true
  InternalTolerance = 1e-06
  InvalidShape = false
  MakeInternals = false
  MapMode = 5
  Placement = pos=(1.2e-15,-1.5e-15,-5.4) rot=(1,0,0;3.14159rad)
  Support = -> [Chamfer059]
  TreeRank = 155
  ValidateShape = false
  sketch-geometry (1):
    g0: Circle CenterX=0 CenterY=0 CenterZ=0 NormalX=0 NormalY=0 NormalZ=1 AngleXU=0 Radius=1.5
  constraints (2):
    c: Coincident(g0,g-1)
    c: Diameter(g0) = 3
FEATURE [PartDesign::Pocket] Pocket087
  AddSubType = 1
  AlongSketchNormal = false
  AutoTaperInnerAngle = true
  BaseFeature = -> Chamfer059
  CheckUpToFaceLimits = true
  ClaimChildren = false
  Direction = (-2e-16,3e-16,1)
  Fit = 0
  FitJoin = 0
  FixShape = 1
  InnerFit = 0
  InnerFitJoin = 0
  InvalidShape = false
  Length = 12
  Length2 = 10
  Linearize = true
  NewSolid = false
  Profile = -> Sketch259
  ReferenceAxis = -> Sketch259 [N_Axis]
  Refine = true
  Suppress = false
  TaperInnerAngle = 0
  TaperInnerAngleRev = 0
  TreeRank = 156
  Type = 0
  ValidateShape = true
  _ProfileBasedVersion = 1
  _Version = 1
FEATURE [Sketcher::SketchObject] Sketch260
  ArcFitTolerance = 1e-06
  AttachmentSupport = -> [YZ_Plane148]
  ExternalBSplineMaxDegree = 5
  ExternalBSplineTolerance = 0.0001
  FixShape = 1
  FullyConstrained = true
  InternalTolerance = 1e-06
  InvalidShape = false
  MakeInternals = false
  MapMode = 5
  Placement = pos=(0,0,0) rot=(0.57735,0.57735,0.57735;2.0944rad)
  Support = -> [YZ_Plane148]
  TreeRank = 157
  ValidateShape = false
  sketch-geometry (1):
    g0: Circle CenterX=0 CenterY=4 CenterZ=0 NormalX=0 NormalY=0 NormalZ=1 AngleXU=0 Radius=2.5
  constraints (3):
    c: PointOnObject(g0,g-2)
    c: Diameter(g0) = 5
    c: DistanceY(g-1,g0) = 4
FEATURE [PartDesign::Pocket] Pocket088
  AddSubType = 1
  AlongSketchNormal = false
  AutoTaperInnerAngle = true
  BaseFeature = -> Pocket087
  CheckUpToFaceLimits = true
  ClaimChildren = false
  Direction = (-1,2e-16,-3e-16)
  Fit = 0
  FitJoin = 0
  FixShape = 1
  InnerFit = 0
  InnerFitJoin = 0
  InvalidShape = false
  Length = 5
  Length2 = 10
  Linearize = true
  Midplane = true
  NewSolid = false
  Profile = -> Sketch260
  ReferenceAxis = -> Sketch260 [N_Axis]
  Refine = true
  Suppress = false
  TaperInnerAngle = 0
  TaperInnerAngleRev = 0
  TreeRank = 158
  Type = 1
  ValidateShape = true
  _ProfileBasedVersion = 1
  _Version = 1
FEATURE [PartDesign::Chamfer] Chamfer060
  AddSubType = 0
  Angle = 45
  Base = -> Pocket088 [Edge24,Edge27]
  BaseFeature = -> Pocket088
  ChamferType = 0
  FixShape = 1
  FlipDirection = false
  InvalidShape = false
  NewSolid = false
  Refine = true
  Size = 0.2
  Size2 = 1
  SupportTransform = false
  Suppress = false
  TreeRank = 159
  UseAllEdges = false
  ValidateShape = true
FEATURE [PartDesign::Fillet] Fillet052
  AddSubType = 0
  Base = -> Chamfer060 [Edge2,Edge5,Edge8,Edge26,Edge28,Edge21]
  BaseFeature = -> Chamfer060
  FixShape = 1
  InvalidShape = false
  NewSolid = false
  Radius = 0.4
  Refine = true
  SupportTransform = false
  Suppress = false
  TreeRank = 160
  UseAllEdges = false
  ValidateShape = true
FEATURE [PartDesign::Body] Body122  label="Adaptator-suction-cup-M5-VM"
  AutoGroupSolids = false
  ClaimAllChildren = false
  ExportMode = 0
  FixShape = 1
  Group = -> [Sketch256,Pad103,Sketch257,Revolution024,Sketch258,Revolution025,Chamfer059,Sketch259,Pocket087,Sketch260,Pocket088,Chamfer060,Fillet052]
  InvalidShape = false
  Origin = -> Origin226
  SingleSolid = true
  Tip = -> Fillet052
  TreeRank = 146
  ValidateShape = false
  _ExportChildren = -> [Pad103,Revolution024,Revolution025,Chamfer059,Pocket087,Pocket088,Chamfer060,Fillet052]
  _GroupVersion = 1
FEATURE [Sketcher::SketchObject] Sketch261
  ArcFitTolerance = 1e-06
  AttachmentSupport = -> [YZ_Plane149]
  ExternalBSplineMaxDegree = 5
  ExternalBSplineTolerance = 0.0001
  FixShape = 1
  FullyConstrained = true
  InternalTolerance = 1e-06
  InvalidShape = false
  MakeInternals = false
  MapMode = 5
  Placement = pos=(0,0,0) rot=(0.57735,0.57735,0.57735;2.0944rad)
  Support = -> [YZ_Plane149]
  TreeRank = 174
  ValidateShape = false
  sketch-geometry (8):
    g0: LineSegment StartX=3.57957 StartY=0 StartZ=0 EndX=1.78979 EndY=3.1 EndZ=0
    g1: LineSegment StartX=1.78979 StartY=3.1 StartZ=0 EndX=-1.78979 EndY=3.1 EndZ=0
    g2: LineSegment StartX=-1.78979 StartY=3.1 StartZ=0 EndX=-3.57957 EndY=6.26e-14 EndZ=0
    g3: LineSegment StartX=-3.57957 StartY=6.27e-14 StartZ=0 EndX=-1.78979 EndY=-3.1 EndZ=0
    g4: LineSegment StartX=-1.78979 StartY=-3.1 StartZ=0 EndX=1.78979 EndY=-3.1 EndZ=0
    g5: LineSegment StartX=1.78979 StartY=-3.1 StartZ=0 EndX=3.57957 EndY=0 EndZ=0
    g6: Circle [constr] CenterX=0 CenterY=0 CenterZ=0 NormalX=0 NormalY=0 NormalZ=1 AngleXU=0 Radius=3.57957
    g7: Circle CenterX=0 CenterY=0 CenterZ=0 NormalX=0 NormalY=0 NormalZ=1 AngleXU=0 Radius=1.5
  constraints (18):
    c: Coincident(g0,g1)
    c: Coincident(g1,g2)
    c: Coincident(g2,g3)
    c: Coincident(g3,g4)
    c: Coincident(g4,g5)
    c: Coincident(g5,g0)
    c: Equal(g0, g1-g5) x5
    c: PointOnObject(g0,g6)
    c: PointOnObject(g1,g6)
    c: PointOnObject(g2,g6)
    c: PointOnObject(g3,g6)
    c: PointOnObject(g4,g6)
    c: PointOnObject(g5,g6)
    c: Coincident(g6,g-1)
    c: PointOnObject(g5,g-1)
    c: DistanceY(g4,g0) = 6.2
    c: Coincident(g7,g6)
    c: Diameter(g7) = 3
FEATURE [PartDesign::Pad] Pad104
  AddSubType = 0
  AlongSketchNormal = false
  AutoTaperInnerAngle = true
  CheckUpToFaceLimits = true
  ClaimChildren = false
  Direction = (1,-2e-16,3e-16)
  Fit = 0
  FitJoin = 0
  FixShape = 1
  InnerFit = 0
  InnerFitJoin = 0
  InvalidShape = false
  Length = 2.5
  Length2 = 10
  Linearize = true
  NewSolid = false
  Profile = -> Sketch261
  ReferenceAxis = -> Sketch261 [N_Axis]
  Refine = true
  Suppress = false
  TaperInnerAngle = 0
  TaperInnerAngleRev = 0
  TreeRank = 175
  Type = 0
  ValidateShape = true
  _ProfileBasedVersion = 1
FEATURE [Sketcher::SketchObject] Sketch262
  ArcFitTolerance = 1e-06
  AttachmentSupport = -> [XZ_Plane149]
  ExternalBSplineMaxDegree = 5
  ExternalBSplineTolerance = 0.0001
  FixShape = 1
  FullyConstrained = true
  InternalTolerance = 1e-06
  InvalidShape = false
  MakeInternals = false
  MapMode = 5
  Placement = pos=(0,0,0) rot=(1,0,0;1.5708rad)
  Support = -> [XZ_Plane149]
  TreeRank = 176
  ValidateShape = false
  sketch-geometry (11):
    g0: LineSegment [constr] StartX=10 StartY=-2.25 StartZ=0 EndX=0 EndY=-2.25 EndZ=0
    g1: LineSegment StartX=0 StartY=-2.25 StartZ=0 EndX=0 EndY=-1.5 EndZ=0
    g2: LineSegment StartX=0 StartY=-1.5 StartZ=0 EndX=10 EndY=-1.5 EndZ=0
    g3: LineSegment StartX=10 StartY=-1.5 StartZ=0 EndX=10 EndY=-2.25 EndZ=0
    g4: LineSegment StartX=10 StartY=-2.25 StartZ=0 EndX=7.8 EndY=-2.5 EndZ=0
    g5: LineSegment StartX=7.8 StartY=-2.5 StartZ=0 EndX=7 EndY=-2.5 EndZ=0
    g6: LineSegment StartX=7 StartY=-2.5 StartZ=0 EndX=7 EndY=-2.25 EndZ=0
    g7: LineSegment StartX=7 StartY=-2.25 StartZ=0 EndX=4.8 EndY=-2.5 EndZ=0
    g8: LineSegment StartX=4.8 StartY=-2.5 StartZ=0 EndX=4 EndY=-2.5 EndZ=0
    g9: LineSegment StartX=4 StartY=-2.5 StartZ=0 EndX=4 EndY=-2.25 EndZ=0
    g10: LineSegment StartX=0 StartY=-2.25 StartZ=0 EndX=4 EndY=-2.25 EndZ=0
  constraints (32):
    c: PointOnObject(g0,g-2)
    c: Horizontal(g0)
    c: DistanceX(g0,g0) = 10
    c: Coincident(g0,g1)
    c: PointOnObject(g1,g-2)
    c: Coincident(g1,g2)
    c: Horizontal(g2)
    c: Coincident(g2,g3)
    c: Coincident(g3,g0)
    c: Vertical(g3)
    c: DistanceY(g0) = -2.25
    c: DistanceY(g2,g-1) = 1.5
    c: Coincident(g0,g4)
    c: Coincident(g4,g5)
    c: Horizontal(g5)
    c: Coincident(g5,g6)
    c: PointOnObject(g6,g0)
    c: Coincident(g6,g7)
    c: Coincident(g7,g8)
    c: Horizontal(g8)
    c: Coincident(g8,g9)
    c: PointOnObject(g9,g0)
    c: Vertical(g9)
    c: Vertical(g6)
    c: Equal(g5,g8)
    c: Equal(g6,g9)
    c: Equal(g7,g4)
    c: DistanceX(g6,g3) = 3
    c: DistanceY(g5,g-1) = 2.5
    c: DistanceX(g5,g5) = 0.8
    c: Coincident(g10,g1)
    c: Coincident(g10,g9)
FEATURE [PartDesign::Revolution] Revolution026
  AddSubType = 0
  Angle = 360
  Axis = (1,0,0)
  Base = (0,0,0)
  BaseFeature = -> Pad104
  ClaimChildren = false
  Fit = 0
  FitJoin = 0
  FixShape = 1
  InnerFit = 0
  InnerFitJoin = 0
  InvalidShape = false
  Linearize = true
  NewSolid = false
  Profile = -> Sketch262
  ReferenceAxis = -> Sketch262 [H_Axis]
  Refine = true
  Reversed = true
  Suppress = false
  TreeRank = 177
  ValidateShape = true
  _ProfileBasedVersion = 1
FEATURE [Sketcher::SketchObject] Sketch263
  ArcFitTolerance = 1e-06
  AttachmentSupport = -> [XZ_Plane149]
  ExternalBSplineMaxDegree = 5
  ExternalBSplineTolerance = 0.0001
  FixShape = 1
  FullyConstrained = true
  InternalTolerance = 1e-06
  InvalidShape = false
  MakeInternals = false
  MapMode = 5
  Placement = pos=(0,0,0) rot=(1,0,0;1.5708rad)
  Support = -> [XZ_Plane149]
  TreeRank = 178
  ValidateShape = false
  sketch-geometry (6):
    g0: LineSegment StartX=0 StartY=1.5 StartZ=0 EndX=-4.5 EndY=1.5 EndZ=0
    g1: LineSegment StartX=-4.5 StartY=1.5 StartZ=0 EndX=-4.5 EndY=2.5 EndZ=0
    g2: LineSegment StartX=-4.5 StartY=2.5 StartZ=0 EndX=-1.5 EndY=2.5 EndZ=0
    g3: LineSegment StartX=-1.5 StartY=2.5 StartZ=0 EndX=-1.5 EndY=2 EndZ=0
    g4: LineSegment StartX=-1.5 StartY=2 StartZ=0 EndX=0 EndY=2 EndZ=0
    g5: LineSegment StartX=0 StartY=2 StartZ=0 EndX=0 EndY=1.5 EndZ=0
  constraints (18):
    c: PointOnObject(g0,g-2)
    c: Horizontal(g0)
    c: Coincident(g0,g1)
    c: Vertical(g1)
    c: Coincident(g1,g2)
    c: Horizontal(g2)
    c: Coincident(g2,g3)
    c: Vertical(g3)
    c: Coincident(g3,g4)
    c: PointOnObject(g4,g-2)
    c: Horizontal(g4)
    c: Coincident(g4,g5)
    c: Coincident(g5,g0)
    c: DistanceY(g1) = 2.5
    c: DistanceY(g0) = 1.5
    c: DistanceY(g4) = 2
    c: DistanceX(g2,g2) = 3
    c: DistanceX(g0,g0) = 4.5
FEATURE [PartDesign::Revolution] Revolution027
  AddSubType = 0
  Angle = 360
  Axis = (1,0,0)
  Base = (0,0,0)
  BaseFeature = -> Revolution026
  ClaimChildren = false
  Fit = 0
  FitJoin = 0
  FixShape = 1
  InnerFit = 0
  InnerFitJoin = 0
  InvalidShape = false
  Linearize = true
  NewSolid = false
  Profile = -> Sketch263
  ReferenceAxis = -> Sketch263 [H_Axis]
  Refine = true
  Suppress = false
  TreeRank = 179
  ValidateShape = true
  _ProfileBasedVersion = 1
FEATURE [PartDesign::Chamfer] Chamfer061
  AddSubType = 0
  Angle = 45
  Base = -> Revolution027 [Edge5,Edge3]
  BaseFeature = -> Revolution027
  ChamferType = 0
  FixShape = 1
  FlipDirection = false
  InvalidShape = false
  NewSolid = false
  Refine = true
  Size = 0.2
  Size2 = 1
  SupportTransform = false
  Suppress = false
  TreeRank = 180
  UseAllEdges = false
  ValidateShape = true
FEATURE [PartDesign::Chamfer] Chamfer062
  AddSubType = 0
  Angle = 45
  Base = -> Chamfer061 [Edge6]
  BaseFeature = -> Chamfer061
  ChamferType = 0
  FixShape = 1
  FlipDirection = false
  InvalidShape = false
  NewSolid = false
  Refine = true
  Size = 0.2
  Size2 = 1
  SupportTransform = false
  Suppress = false
  TreeRank = 181
  UseAllEdges = false
  ValidateShape = true
FEATURE [PartDesign::Fillet] Fillet053
  AddSubType = 0
  Base = -> Chamfer062 [Edge39,Edge35,Edge43,Edge41,Edge37,Edge34]
  BaseFeature = -> Chamfer062
  FixShape = 1
  InvalidShape = false
  NewSolid = false
  Radius = 0.4
  Refine = true
  SupportTransform = false
  Suppress = false
  TreeRank = 182
  UseAllEdges = false
  ValidateShape = true
FEATURE [PartDesign::Body] Body123  label="Tube-connector-M5-ID5mm"
  AutoGroupSolids = false
  ClaimAllChildren = false
  ExportMode = 0
  FixShape = 1
  Group = -> [Sketch261,Pad104,Sketch262,Revolution026,Sketch263,Revolution027,Chamfer061,Chamfer062,Fillet053]
  InvalidShape = false
  Origin = -> Origin227
  Placement = pos=(6.7,0,4) rot=(0,0,1;0rad)
  SingleSolid = true
  Tip = -> Fillet053
  TreeRank = 170
  ValidateShape = false
  _ExportChildren = -> [Pad104,Revolution026,Revolution027,Chamfer061,Chamfer062,Fillet053]
  _GroupVersion = 1
FEATURE [App::Link] Link093  label="Link093(Tube-connector-M5-ID5mm)"
  AutoLinkLabel = true
  AutoPlacement = true
  LinkPlacement = pos=(-6.7,-7.98703e-07,4) rot=(0,1,0;3.14159rad)
  LinkedObject = -> Body123
  Placement = pos=(-6.7,-7.98703e-07,4) rot=(0,1,0;3.14159rad)
  SyncGroupVisibility = false
  TreeRank = 183
  _LinkVersion = 1
FEATURE [Sketcher::SketchObject] Sketch264
  ArcFitTolerance = 1e-06
  AttachmentSupport = -> [YZ_Plane150]
  ExternalBSplineMaxDegree = 5
  ExternalBSplineTolerance = 0.0001
  FixShape = 1
  FullyConstrained = true
  InternalTolerance = 1e-06
  InvalidShape = false
  MakeInternals = false
  MapMode = 5
  Placement = pos=(0,0,0) rot=(0.57735,0.57735,0.57735;2.0944rad)
  Support = -> [YZ_Plane150]
  TreeRank = 194
  ValidateShape = false
  sketch-geometry (2):
    g0: Circle CenterX=0 CenterY=0 CenterZ=0 NormalX=0 NormalY=0 NormalZ=1 AngleXU=0 Radius=2.5
    g1: Circle CenterX=0 CenterY=0 CenterZ=0 NormalX=0 NormalY=0 NormalZ=1 AngleXU=0 Radius=4
  constraints (4):
    c: Coincident(g0,g-1)
    c: Coincident(g1,g0)
    c: Diameter(g0) = 5
    c: Diameter(g1) = 8
FEATURE [PartDesign::Pad] Pad105
  AddSubType = 0
  AlongSketchNormal = false
  AutoTaperInnerAngle = true
  CheckUpToFaceLimits = true
  ClaimChildren = false
  Direction = (1,-2e-16,3e-16)
  Fit = 0
  FitJoin = 0
  FixShape = 1
  InnerFit = 0
  InnerFitJoin = 0
  InvalidShape = false
  Length = 0.7
  Length2 = 10
  Linearize = true
  NewSolid = false
  Profile = -> Sketch264
  ReferenceAxis = -> Sketch264 [N_Axis]
  Refine = true
  Suppress = false
  TaperInnerAngle = 0
  TaperInnerAngleRev = 0
  TreeRank = 195
  Type = 0
  ValidateShape = true
  _ProfileBasedVersion = 1
FEATURE [PartDesign::Body] Body124  label="Rondelle"
  AutoGroupSolids = false
  ClaimAllChildren = false
  ExportMode = 0
  FixShape = 1
  Group = -> [Sketch264,Pad105]
  InvalidShape = false
  Origin = -> Origin229
  Placement = pos=(6,0,4) rot=(0,0,1;0rad)
  SingleSolid = true
  Tip = -> Pad105
  TreeRank = 193
  ValidateShape = false
  _ExportChildren = -> [Pad105]
  _GroupVersion = 1
FEATURE [App::Link] Link094  label="Link094(Rondelle)"
  AutoLinkLabel = true
  AutoPlacement = true
  LinkPlacement = pos=(-6,-2.38419e-07,4) rot=(0,1,0;3.14159rad)
  LinkedObject = -> Body124
  Placement = pos=(-6,-2.38419e-07,4) rot=(0,1,0;3.14159rad)
  SyncGroupVisibility = false
  TreeRank = 196
  _LinkVersion = 1
FEATURE [App::Part] Part051  label="SuctionCupAdaptator"
  ClaimAllChildren = false
  ExportMode = 1
  Group = -> [opera_20241026_100449,Body122,Body123,Link093,Body124,Link094]
  Origin = -> Origin228
  TreeRank = 173
  _ExportChildren = -> [opera_20241026_100449,Body122,Body123,Link093,Body124,Link094]
  _GroupVersion = 1
FEATURE [Sketcher::SketchObject] Sketch265
  ArcFitTolerance = 1e-06
  AttachmentSupport = -> [XZ_Plane151]
  ExternalBSplineMaxDegree = 5
  ExternalBSplineTolerance = 0.0001
  FixShape = 1
  FullyConstrained = true
  InternalTolerance = 1e-06
  InvalidShape = false
  MakeInternals = false
  MapMode = 5
  Placement = pos=(0,0,0) rot=(1,0,0;1.5708rad)
  Support = -> [XZ_Plane151]
  TreeRank = 207
  ValidateShape = false
  sketch-geometry (9):
    g0: LineSegment StartX=7.5 StartY=0 StartZ=0 EndX=7.5 EndY=-7 EndZ=0
    g1: LineSegment StartX=7.5 StartY=-7 StartZ=0 EndX=5.25 EndY=-8.5 EndZ=0
    g2: LineSegment StartX=5.25 StartY=-8.5 StartZ=0 EndX=2 EndY=-8.5 EndZ=0
    g3: LineSegment StartX=2 StartY=-8.5 StartZ=0 EndX=2 EndY=-5.4 EndZ=0
    g4: LineSegment StartX=2 StartY=-5.4 StartZ=0 EndX=3.5 EndY=-5.4 EndZ=0
    g5: LineSegment StartX=3.5 StartY=-5.4 StartZ=0 EndX=3.5 EndY=-3 EndZ=0
    g6: LineSegment StartX=3.5 StartY=-3 StartZ=0 EndX=2.5 EndY=-3 EndZ=0
    g7: LineSegment StartX=2.5 StartY=-3 StartZ=0 EndX=2.5 EndY=0 EndZ=0
    g8: LineSegment StartX=2.5 StartY=0 StartZ=0 EndX=7.5 EndY=0 EndZ=0
  constraints (27):
    c: PointOnObject(g0,g-1)
    c: Vertical(g0)
    c: Coincident(g0,g1)
    c: Coincident(g2,g1)
    c: Horizontal(g2)
    c: Coincident(g2,g3)
    c: Vertical(g3)
    c: Coincident(g3,g4)
    c: Horizontal(g4)
    c: Coincident(g4,g5)
    c: Vertical(g5)
    c: Coincident(g5,g6)
    c: Horizontal(g6)
    c: Coincident(g6,g7)
    c: Vertical(g7)
    c: Coincident(g8,g7)
    c: Coincident(g8,g0)
    c: Horizontal(g8)
    c: DistanceX(g-1,g7) = 2.5
    c: DistanceY(g7,g7) = 3
    c: DistanceY(g4,g-1) = 5.4
    c: DistanceX(g-1,g5) = 3.5
    c: DistanceX(g-1,g0) = 7.5
    c: DistanceX(g-1,g2) = 2
    c: DistanceY(g1,g0) = 8.5
    c: DistanceX(g-1,g1) = 5.25
    c: DistanceY(g0,g0) = 7
FEATURE [PartDesign::Revolution] Revolution028
  AddSubType = 0
  Angle = 360
  Axis = (0,2e-16,1)
  Base = (0,0,0)
  ClaimChildren = false
  Fit = 0
  FitJoin = 0
  FixShape = 1
  InnerFit = 0
  InnerFitJoin = 0
  InvalidShape = false
  Linearize = true
  NewSolid = false
  Profile = -> Sketch265
  ReferenceAxis = -> Sketch265 [V_Axis]
  Refine = true
  Reversed = true
  Suppress = false
  TreeRank = 208
  ValidateShape = true
  _ProfileBasedVersion = 1
FEATURE [PartDesign::Fillet] Fillet054
  AddSubType = 0
  Base = -> Revolution028 [Edge1,Edge3]
  BaseFeature = -> Revolution028
  FixShape = 1
  InvalidShape = false
  NewSolid = false
  Radius = 1
  Refine = true
  SupportTransform = false
  Suppress = false
  TreeRank = 209
  UseAllEdges = false
  ValidateShape = true
FEATURE [Sketcher::SketchObject] Sketch266
  ArcFitTolerance = 1e-06
  AttachmentSupport = -> [XZ_Plane151]
  ExternalBSplineMaxDegree = 5
  ExternalBSplineTolerance = 0.0001
  ExternalGeometry = -> [Fillet054]
  FixShape = 1
  FullyConstrained = true
  InternalTolerance = 1e-06
  InvalidShape = false
  MakeInternals = false
  MapMode = 5
  Placement = pos=(0,0,0) rot=(1,0,0;1.5708rad)
  Support = -> [XZ_Plane151]
  TreeRank = 210
  ValidateShape = false
  sketch-geometry (12):
    g0: LineSegment StartX=5.25 StartY=-8.5 StartZ=0 EndX=8 EndY=-11.75 EndZ=0
    g1: LineSegment StartX=8 StartY=-11.75 StartZ=0 EndX=5.25 EndY=-15 EndZ=0
    g2: LineSegment StartX=5.25 StartY=-15 StartZ=0 EndX=8 EndY=-17.5 EndZ=0
    g3: LineSegment [constr] StartX=8 StartY=-17.5 StartZ=0 EndX=0 EndY=-17.5 EndZ=0
    g4: LineSegment [constr] StartX=0 StartY=-17.5 StartZ=0 EndX=0 EndY=-8.5 EndZ=0
    g5: LineSegment [constr] StartX=0 StartY=-8.5 StartZ=0 EndX=5.25 EndY=-8.5 EndZ=0
    g6: LineSegment StartX=5.25 StartY=-8.5 StartZ=0 EndX=2 EndY=-8.5 EndZ=0
    g7: LineSegment StartX=2 StartY=-8.5 StartZ=0 EndX=7.5 EndY=-11.75 EndZ=0
    g8: LineSegment StartX=7.5 StartY=-11.75 StartZ=0 EndX=4.75 EndY=-15 EndZ=0
    g9: LineSegment StartX=8 StartY=-17.5 StartZ=0 EndX=4.75 EndY=-15 EndZ=0
    g10: LineSegment [constr] StartX=7.5 StartY=-11.75 StartZ=0 EndX=8 EndY=-11.75 EndZ=0
    g11: LineSegment [constr] StartX=4.75 StartY=-15 StartZ=0 EndX=5.25 EndY=-15 EndZ=0
  constraints (31):
    c: Coincident(g-4,g0)
    c: Coincident(g0,g1)
    c: Coincident(g1,g2)
    c: Coincident(g2,g3)
    c: PointOnObject(g3,g-2)
    c: Horizontal(g3)
    c: Coincident(g3,g4)
    c: PointOnObject(g4,g-4)
    c: Vertical(g4)
    c: Coincident(g4,g5)
    c: Coincident(g5,g0)
    c: Coincident(g6,g0)
    c: Coincident(g6,g-3)
    c: Coincident(g7,g6)
    c: Coincident(g8,g7)
    c: Coincident(g9,g2)
    c: Coincident(g9,g8)
    c: DistanceX(g3,g3) = 8
    c: DistanceY(g3,g-1) = 17.5
    c: Vertical(g0,g2)
    c: Equal(g0,g1)
    c: DistanceY(g2,g1) = 2.5
    c: Vertical(g1,g0)
    c: Horizontal(g7,g0)
    c: Horizontal(g1,g8)
    c: Coincident(g10,g7)
    c: Coincident(g10,g0)
    c: Coincident(g11,g8)
    c: Coincident(g11,g1)
    c: Equal(g11,g10)
    c: DistanceX(g10,g10) = 0.5
FEATURE [PartDesign::Revolution] Revolution029
  AddSubType = 0
  Angle = 360
  Axis = (0,2e-16,1)
  Base = (0,0,0)
  BaseFeature = -> Fillet054
  ClaimChildren = false
  Fit = 0
  FitJoin = 0
  FixShape = 1
  InnerFit = 0
  InnerFitJoin = 0
  InvalidShape = false
  Linearize = true
  NewSolid = false
  Profile = -> Sketch266
  ReferenceAxis = -> Sketch266 [V_Axis]
  Refine = true
  Reversed = true
  Suppress = false
  TreeRank = 211
  ValidateShape = true
  _ProfileBasedVersion = 1
FEATURE [PartDesign::Fillet] Fillet055
  AddSubType = 0
  Base = -> Revolution029 [Edge14,Edge10,Edge17]
  BaseFeature = -> Revolution029
  FixShape = 1
  InvalidShape = false
  NewSolid = false
  Radius = 0.5
  Refine = true
  SupportTransform = false
  Suppress = false
  TreeRank = 212
  UseAllEdges = false
  ValidateShape = true
FEATURE [PartDesign::Body] Body125  label="SuctionCupDP15mm"
  AutoGroupSolids = false
  ClaimAllChildren = false
  ExportMode = 0
  FixShape = 1
  Group = -> [Sketch265,Revolution028,Fillet054,Sketch266,Revolution029,Fillet055]
  InvalidShape = false
  Origin = -> Origin230
  SingleSolid = true
  Tip = -> Fillet055
  TreeRank = 206
  ValidateShape = false
  _ExportChildren = -> [Revolution028,Fillet054,Revolution029,Fillet055]
  _GroupVersion = 1
FEATURE [App::Link] Link095  label="Link095(SuctionCupAdaptator)"
  AutoLinkLabel = true
  AutoPlacement = true
  LinkedObject = -> Part051
  SyncGroupVisibility = false
  TreeRank = 216
  _LinkVersion = 1
FEATURE [App::Link] Link096  label="Link096(SuctionCupDP15mm)"
  AutoLinkLabel = true
  AutoPlacement = true
  LinkedObject = -> Body125
  SyncGroupVisibility = false
  TreeRank = 217
  _LinkVersion = 1
FEATURE [App::Part] Part052  label="AssemblyAdaptatorSuctionCupDP15"
  ClaimAllChildren = false
  ExportMode = 1
  Group = -> [Link095,Link096]
  Origin = -> Origin231
  TreeRank = 215
  _ExportChildren = -> [Link095,Link096]
  _GroupVersion = 1
FEATURE [Sketcher::SketchObject] Sketch267
  ArcFitTolerance = 1e-06
  AttachmentSupport = -> [XY_Plane152]
  ExternalBSplineMaxDegree = 5
  ExternalBSplineTolerance = 0.0001
  FixShape = 1
  FullyConstrained = true
  InternalTolerance = 1e-06
  InvalidShape = false
  MakeInternals = false
  MapMode = 5
  Support = -> [XY_Plane152]
  TreeRank = 148
  ValidateShape = false
  sketch-geometry (7):
    g0: LineSegment StartX=0 StartY=-6.9282 StartZ=0 EndX=6 EndY=-3.4641 EndZ=0
    g1: LineSegment StartX=6 StartY=-3.4641 StartZ=0 EndX=6 EndY=3.4641 EndZ=0
    g2: LineSegment StartX=6 StartY=3.4641 StartZ=0 EndX=0 EndY=6.9282 EndZ=0
    g3: LineSegment StartX=1e-16 StartY=6.9282 StartZ=0 EndX=-6 EndY=3.4641 EndZ=0
    g4: LineSegment StartX=-6 StartY=3.4641 StartZ=0 EndX=-6 EndY=-3.4641 EndZ=0
    g5: LineSegment StartX=-6 StartY=-3.4641 StartZ=0 EndX=0 EndY=-6.9282 EndZ=0
    g6: Circle [constr] CenterX=0 CenterY=0 CenterZ=0 NormalX=0 NormalY=0 NormalZ=1 AngleXU=0 Radius=6.9282
  constraints (16):
    c: Coincident(g0,g1)
    c: Coincident(g1,g2)
    c: Coincident(g2,g3)
    c: Coincident(g3,g4)
    c: Coincident(g4,g5)
    c: Coincident(g5,g0)
    c: Equal(g0, g1-g5) x5
    c: PointOnObject(g0,g6)
    c: PointOnObject(g1,g6)
    c: PointOnObject(g2,g6)
    c: PointOnObject(g3,g6)
    c: PointOnObject(g4,g6)
    c: PointOnObject(g5,g6)
    c: Coincident(g6,g-1)
    c: PointOnObject(g5,g-2)
    c: DistanceX(g3,g1) = 12
FEATURE [PartDesign::Pad] Pad106
  AddSubType = 0
  AlongSketchNormal = false
  AutoTaperInnerAngle = true
  CheckUpToFaceLimits = true
  ClaimChildren = false
  Direction = (0,0,1)
  Fit = 0
  FitJoin = 0
  FixShape = 1
  InnerFit = 0
  InnerFitJoin = 0
  InvalidShape = false
  Length = 8
  Length2 = 10
  Linearize = true
  NewSolid = false
  Profile = -> Sketch267
  ReferenceAxis = -> Sketch267 [N_Axis]
  Refine = true
  Suppress = false
  TaperInnerAngle = 0
  TaperInnerAngleRev = 0
  TreeRank = 149
  Type = 0
  ValidateShape = true
  _ProfileBasedVersion = 1
FEATURE [Sketcher::SketchObject] Sketch268
  ArcFitTolerance = 1e-06
  AttachmentSupport = -> [YZ_Plane152]
  ExternalBSplineMaxDegree = 5
  ExternalBSplineTolerance = 0.0001
  FixShape = 1
  FullyConstrained = true
  InternalTolerance = 1e-06
  InvalidShape = false
  MakeInternals = false
  MapMode = 5
  Placement = pos=(0,0,0) rot=(0.57735,0.57735,0.57735;2.0944rad)
  Support = -> [YZ_Plane152]
  TreeRank = 150
  ValidateShape = false
  sketch-geometry (6):
    g0: LineSegment StartX=0 StartY=0 StartZ=0 EndX=2.5 EndY=0 EndZ=0
    g1: LineSegment StartX=2.5 StartY=0 StartZ=0 EndX=2.5 EndY=-3 EndZ=0
    g2: LineSegment StartX=2.5 StartY=-3 StartZ=0 EndX=3.5 EndY=-3 EndZ=0
    g3: LineSegment StartX=3.5 StartY=-3 StartZ=0 EndX=3.5 EndY=-5.4 EndZ=0
    g4: LineSegment StartX=3.5 StartY=-5.4 StartZ=0 EndX=0 EndY=-5.4 EndZ=0
    g5: LineSegment StartX=0 StartY=-5.4 StartZ=0 EndX=0 EndY=0 EndZ=0
  constraints (17):
    c: Coincident(g-1,g0)
    c: PointOnObject(g0,g-1)
    c: Coincident(g0,g1)
    c: Vertical(g1)
    c: Coincident(g1,g2)
    c: Horizontal(g2)
    c: Coincident(g2,g3)
    c: Vertical(g3)
    c: Coincident(g3,g4)
    c: PointOnObject(g4,g-2)
    c: Horizontal(g4)
    c: Coincident(g4,g5)
    c: Coincident(g5,g0)
    c: DistanceX(g0,g0) = 2.5
    c: DistanceX(g4,g4) = 3.5
    c: DistanceY(g1,g1) = 3
    c: DistanceY(g3,g0) = 5.4
FEATURE [PartDesign::Revolution] Revolution030
  AddSubType = 0
  Angle = 360
  Axis = (-2e-16,3e-16,1)
  Base = (0,0,0)
  BaseFeature = -> Pad106
  ClaimChildren = false
  Fit = 0
  FitJoin = 0
  FixShape = 1
  InnerFit = 0
  InnerFitJoin = 0
  InvalidShape = false
  Linearize = true
  NewSolid = false
  Profile = -> Sketch268
  ReferenceAxis = -> Sketch268 [V_Axis]
  Refine = true
  Reversed = true
  Suppress = false
  TreeRank = 151
  ValidateShape = true
  _ProfileBasedVersion = 1
FEATURE [Sketcher::SketchObject] Sketch269
  ArcFitTolerance = 1e-06
  AttachmentSupport = -> [XZ_Plane152]
  ExternalBSplineMaxDegree = 5
  ExternalBSplineTolerance = 0.0001
  ExternalGeometry = -> [Revolution030]
  FixShape = 1
  FullyConstrained = true
  InternalTolerance = 1e-06
  InvalidShape = false
  MakeInternals = false
  MapMode = 5
  Placement = pos=(0,0,0) rot=(1,0,0;1.5708rad)
  Support = -> [XZ_Plane152]
  TreeRank = 152
  ValidateShape = false
  sketch-geometry (6):
    g0: LineSegment StartX=0 StartY=8 StartZ=0 EndX=0 EndY=38 EndZ=0
    g1: LineSegment StartX=0 StartY=38 StartZ=0 EndX=2.5 EndY=38 EndZ=0
    g2: LineSegment StartX=2.5 StartY=38 StartZ=0 EndX=2.5 EndY=12 EndZ=0
    g3: LineSegment StartX=2.5 StartY=12 StartZ=0 EndX=4 EndY=12 EndZ=0
    g4: LineSegment StartX=4 StartY=12 StartZ=0 EndX=4 EndY=8 EndZ=0
    g5: LineSegment StartX=4 StartY=8 StartZ=0 EndX=0 EndY=8 EndZ=0
  constraints (18):
    c: PointOnObject(g0,g-2)
    c: PointOnObject(g0,g-2)
    c: Coincident(g0,g1)
    c: Horizontal(g1)
    c: Coincident(g1,g2)
    c: Coincident(g2,g3)
    c: Horizontal(g3)
    c: Coincident(g3,g4)
    c: Vertical(g4)
    c: Coincident(g4,g5)
    c: Coincident(g5,g0)
    c: Horizontal(g5)
    c: Vertical(g2)
    c: PointOnObject(g4,g-3)
    c: DistanceX(g1,g1) = 2.5
    c: DistanceY(g0,g0) = 30
    c: DistanceY(g2,g2) = 26
    c: DistanceX(g0,g4) = 4
FEATURE [PartDesign::Revolution] Revolution031
  AddSubType = 0
  Angle = 360
  Axis = (0,-2e-16,1)
  Base = (0,0,0)
  BaseFeature = -> Revolution030
  ClaimChildren = false
  Fit = 0
  FitJoin = 0
  FixShape = 1
  InnerFit = 0
  InnerFitJoin = 0
  InvalidShape = false
  Linearize = true
  NewSolid = false
  Profile = -> Sketch269
  ReferenceAxis = -> Sketch269 [V_Axis]
  Refine = true
  Reversed = true
  Suppress = false
  TreeRank = 153
  ValidateShape = true
  _ProfileBasedVersion = 1
FEATURE [PartDesign::Chamfer] Chamfer063
  AddSubType = 0
  Angle = 45
  Base = -> Revolution031 [Edge26,Edge29]
  BaseFeature = -> Revolution031
  ChamferType = 0
  FixShape = 1
  FlipDirection = false
  InvalidShape = false
  NewSolid = false
  Refine = true
  Size = 0.2
  Size2 = 1
  SupportTransform = false
  Suppress = false
  TreeRank = 154
  UseAllEdges = false
  ValidateShape = true
FEATURE [Sketcher::SketchObject] Sketch270
  ArcFitTolerance = 1e-06
  AttachmentSupport = -> [Chamfer063]
  ExternalBSplineMaxDegree = 5
  ExternalBSplineTolerance = 0.0001
  FixShape = 1
  FullyConstrained = true
  InternalTolerance = 1e-06
  InvalidShape = false
  MakeInternals = false
  MapMode = 5
  Placement = pos=(1.2e-15,-1.5e-15,-5.4) rot=(1,0,0;3.14159rad)
  Support = -> [Chamfer063]
  TreeRank = 155
  ValidateShape = false
  sketch-geometry (1):
    g0: Circle CenterX=0 CenterY=0 CenterZ=0 NormalX=0 NormalY=0 NormalZ=1 AngleXU=0 Radius=1.5
  constraints (2):
    c: Coincident(g0,g-1)
    c: Diameter(g0) = 3
FEATURE [PartDesign::Pocket] Pocket089
  AddSubType = 1
  AlongSketchNormal = false
  AutoTaperInnerAngle = true
  BaseFeature = -> Chamfer063
  CheckUpToFaceLimits = true
  ClaimChildren = false
  Direction = (-2e-16,3e-16,1)
  Fit = 0
  FitJoin = 0
  FixShape = 1
  InnerFit = 0
  InnerFitJoin = 0
  InvalidShape = false
  Length = 12
  Length2 = 10
  Linearize = true
  NewSolid = false
  Profile = -> Sketch270
  ReferenceAxis = -> Sketch270 [N_Axis]
  Refine = true
  Suppress = false
  TaperInnerAngle = 0
  TaperInnerAngleRev = 0
  TreeRank = 156
  Type = 0
  ValidateShape = true
  _ProfileBasedVersion = 1
  _Version = 1
FEATURE [Sketcher::SketchObject] Sketch271
  ArcFitTolerance = 1e-06
  AttachmentSupport = -> [YZ_Plane152]
  ExternalBSplineMaxDegree = 5
  ExternalBSplineTolerance = 0.0001
  FixShape = 1
  FullyConstrained = true
  InternalTolerance = 1e-06
  InvalidShape = false
  MakeInternals = false
  MapMode = 5
  Placement = pos=(0,0,0) rot=(0.57735,0.57735,0.57735;2.0944rad)
  Support = -> [YZ_Plane152]
  TreeRank = 157
  ValidateShape = false
  sketch-geometry (1):
    g0: Circle CenterX=0 CenterY=4 CenterZ=0 NormalX=0 NormalY=0 NormalZ=1 AngleXU=0 Radius=2.5
  constraints (3):
    c: PointOnObject(g0,g-2)
    c: Diameter(g0) = 5
    c: DistanceY(g-1,g0) = 4
FEATURE [PartDesign::Pocket] Pocket090
  AddSubType = 1
  AlongSketchNormal = false
  AutoTaperInnerAngle = true
  BaseFeature = -> Pocket089
  CheckUpToFaceLimits = true
  ClaimChildren = false
  Direction = (-1,2e-16,-3e-16)
  Fit = 0
  FitJoin = 0
  FixShape = 1
  InnerFit = 0
  InnerFitJoin = 0
  InvalidShape = false
  Length = 5
  Length2 = 10
  Linearize = true
  Midplane = true
  NewSolid = false
  Profile = -> Sketch271
  ReferenceAxis = -> Sketch271 [N_Axis]
  Refine = true
  Suppress = false
  TaperInnerAngle = 0
  TaperInnerAngleRev = 0
  TreeRank = 158
  Type = 1
  ValidateShape = true
  _ProfileBasedVersion = 1
  _Version = 1
FEATURE [PartDesign::Chamfer] Chamfer064
  AddSubType = 0
  Angle = 45
  Base = -> Pocket090 [Edge24,Edge27]
  BaseFeature = -> Pocket090
  ChamferType = 0
  FixShape = 1
  FlipDirection = false
  InvalidShape = false
  NewSolid = false
  Refine = true
  Size = 0.2
  Size2 = 1
  SupportTransform = false
  Suppress = false
  TreeRank = 159
  UseAllEdges = false
  ValidateShape = true
FEATURE [PartDesign::Fillet] Fillet056
  AddSubType = 0
  Base = -> Chamfer064 [Edge2,Edge5,Edge8,Edge26,Edge28,Edge21]
  BaseFeature = -> Chamfer064
  FixShape = 1
  InvalidShape = false
  NewSolid = false
  Radius = 0.4
  Refine = true
  SupportTransform = false
  Suppress = false
  TreeRank = 160
  UseAllEdges = false
  ValidateShape = true
FEATURE [Sketcher::SketchObject] Sketch272
  ArcFitTolerance = 1e-06
  AttachmentSupport = -> [Fillet056]
  ExternalBSplineMaxDegree = 5
  ExternalBSplineTolerance = 0.0001
  FixShape = 1
  FullyConstrained = true
  InternalTolerance = 1e-06
  InvalidShape = false
  MakeInternals = false
  MapMode = 5
  Placement = pos=(0,-8.4e-15,38) rot=(0,0,1;0rad)
  Support = -> [Fillet056]
  TreeRank = 219
  ValidateShape = false
  sketch-geometry (1):
    g0: Circle CenterX=0 CenterY=0 CenterZ=0 NormalX=0 NormalY=0 NormalZ=1 AngleXU=0 Radius=1.5
  constraints (2):
    c: Coincident(g0,g-1)
    c: Diameter(g0) = 3
FEATURE [PartDesign::Pocket] Pocket091
  AddSubType = 1
  AlongSketchNormal = false
  AutoTaperInnerAngle = true
  BaseFeature = -> Fillet056
  CheckUpToFaceLimits = true
  ClaimChildren = false
  Direction = (0,2e-16,-1)
  Fit = 0
  FitJoin = 0
  FixShape = 1
  InnerFit = 0
  InnerFitJoin = 0
  InvalidShape = false
  Length = 8
  Length2 = 10
  Linearize = true
  NewSolid = false
  Profile = -> Sketch272
  ReferenceAxis = -> Sketch272 [N_Axis]
  Refine = true
  Suppress = false
  TaperInnerAngle = 0
  TaperInnerAngleRev = 0
  TreeRank = 220
  Type = 0
  ValidateShape = true
  _ProfileBasedVersion = 1
  _Version = 1
FEATURE [PartDesign::Chamfer] Chamfer065
  AddSubType = 0
  Angle = 45
  Base = -> Pocket091 [Edge66]
  BaseFeature = -> Pocket091
  ChamferType = 0
  FixShape = 1
  FlipDirection = false
  InvalidShape = false
  NewSolid = false
  Refine = true
  Size = 0.2
  Size2 = 1
  SupportTransform = false
  Suppress = false
  TreeRank = 221
  UseAllEdges = false
  ValidateShape = true
FEATURE [PartDesign::Body] Body126  label="Adaptator-suction-cup-spring-version"
  AutoGroupSolids = false
  ClaimAllChildren = false
  ExportMode = 0
  FixShape = 1
  Group = -> [Sketch267,Pad106,Sketch268,Revolution030,Sketch269,Revolution031,Chamfer063,Sketch270,Pocket089,Sketch271,Pocket090,Chamfer064,Fillet056,Sketch272,Pocket091,Chamfer065]
  InvalidShape = false
  Origin = -> Origin232
  SingleSolid = true
  Tip = -> Chamfer065
  TreeRank = 218
  ValidateShape = false
  _ExportChildren = -> [Pad106,Revolution030,Revolution031,Chamfer063,Pocket089,Pocket090,Chamfer064,Fillet056,Pocket091,Chamfer065]
  _GroupVersion = 1
FEATURE [App::DocumentObjectGroup] Group013  label="Pneumatic"
  ClaimAllChildren = true
  ExportMode = 1
  Group = -> [Part051,Body125,Part052,Body126]
  TreeRank = 136
  _GroupVersion = 1
